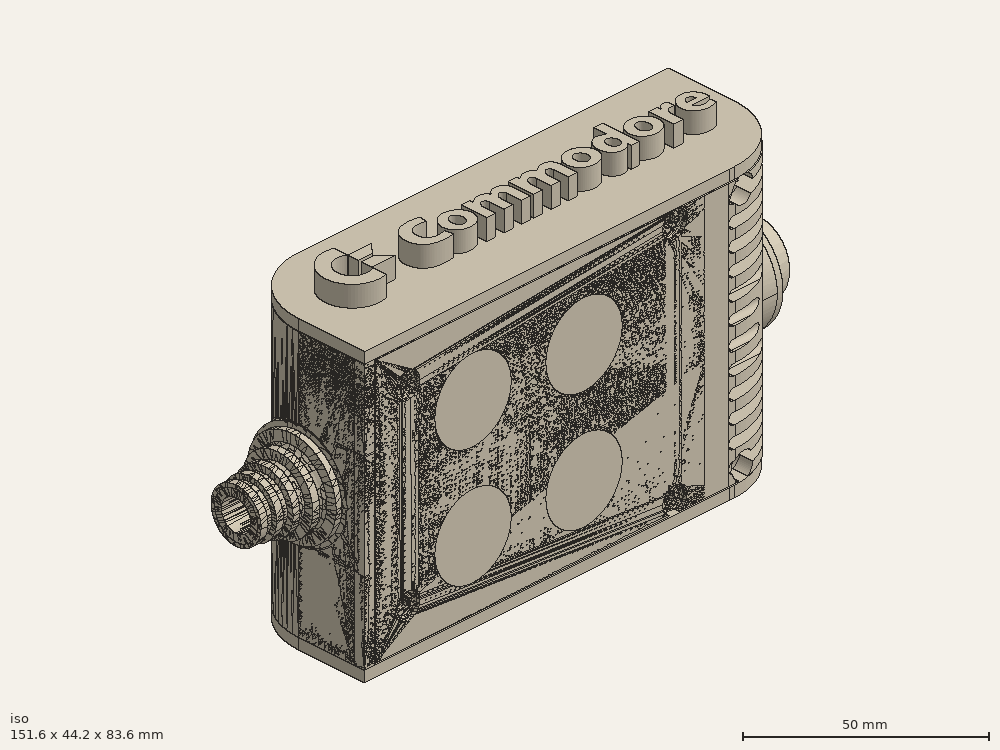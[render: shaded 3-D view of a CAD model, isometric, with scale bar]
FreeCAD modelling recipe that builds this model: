
FCSTD DOCUMENT  (FreeCAD 0.19R0.19.2)
Label: enclosure_209FCStd
License: All rights reserved
LicenseURL: http://en.wikipedia.org/wiki/All_rights_reserved
objects: Part::Revolution×152, Part::MultiFuse×146, Part::Feature×146, Sketcher::SketchObject×84, Part::Cut×71, Part::Cylinder×70, Part::Extrusion×69, Part::Fillet×58, Part::Box×36, App::MeasureDistance×4, Part::FeaturePython×2, Image::ImagePlane×1, PartDesign::Body×1, Part::Mirroring×1
note: 836 computed .brp shape members not serialized (recipe doc carries the construction recipe); baked Part::Feature solids carry a one-line shape summary decoded from their .brp

FEATURE [Sketcher::SketchObject] Sketch  label="topSketch"
  FullyConstrained = true
  sketch-geometry (20):
    g0: LineSegment StartX=5.21097e-06 StartY=3 StartZ=0 EndX=5.21097e-06 EndY=19 EndZ=0
    g1: ArcOfCircle CenterX=19 CenterY=19 CenterZ=0 NormalX=0 NormalY=0 NormalZ=1 AngleXU=0 Radius=19 StartAngle=1.5708 EndAngle=3.14159
    g2: ArcOfCircle CenterX=19 CenterY=19 CenterZ=0 NormalX=0 NormalY=0 NormalZ=1 AngleXU=0 Radius=16 StartAngle=1.5708 EndAngle=3.14159
    g3: LineSegment StartX=114 StartY=35 StartZ=0 EndX=19 EndY=35 EndZ=0
    g4: LineSegment StartX=5.21097e-06 StartY=3 StartZ=0 EndX=5.21097e-06 EndY=0 EndZ=0
    g5: LineSegment StartX=3 StartY=0 StartZ=0 EndX=5.21097e-06 EndY=0 EndZ=0
    g6: LineSegment StartX=3 StartY=19 StartZ=0 EndX=3 EndY=0 EndZ=0
    g7: LineSegment StartX=19 StartY=38 StartZ=0 EndX=124 EndY=38 EndZ=0
    g8: Circle CenterX=119 CenterY=35 CenterZ=0 NormalX=0 NormalY=0 NormalZ=1 AngleXU=0 Radius=1
    g9: Circle CenterX=121 CenterY=35 CenterZ=0 NormalX=0 NormalY=0 NormalZ=1 AngleXU=0 Radius=1
    g10: Circle CenterX=121 CenterY=33 CenterZ=0 NormalX=0 NormalY=0 NormalZ=1 AngleXU=0 Radius=1
    g11: BSplineCurve PolesCount=3 KnotsCount=2 Degree=2 IsPeriodic=0
    g12: GeomPoint X=119 Y=35 Z=0
    g13: GeomPoint X=121 Y=33 Z=0
    g14: LineSegment StartX=119 StartY=35 StartZ=0 EndX=114 EndY=35 EndZ=0
    g15: ArcOfCircle CenterX=105 CenterY=19 CenterZ=0 NormalX=0 NormalY=0 NormalZ=1 AngleXU=0 Radius=19 StartAngle=5.7297 EndAngle=6.28319
    g16: ArcOfCircle CenterX=105 CenterY=19 CenterZ=0 NormalX=0 NormalY=0 NormalZ=1 AngleXU=0 Radius=16 StartAngle=5.60905 EndAngle=6.28319
    g17: LineSegment StartX=121 StartY=33 StartZ=0 EndX=121 EndY=19 EndZ=0
    g18: LineSegment StartX=124 StartY=38 StartZ=0 EndX=124 EndY=19 EndZ=0
    g19: LineSegment StartX=117.5 StartY=9.01251 StartZ=0 EndX=121.163 EndY=9.0125 EndZ=0
  constraints (46):
    c: Vertical(g0)
    c: Block(g0)
    c: Coincident(g1,g0)
    c: Block(g1)
    c: Coincident(g2,g1)
    c: Block(g2)
    c: Coincident(g3,g2)
    c: Horizontal(g3)
    c: Tangent(g3,g2)
    c: Coincident(g4,g0)
    c: Distance(g4) = 3
    c: Vertical(g4)
    c: Coincident(g5,g4)
    c: Horizontal(g5)
    c: Coincident(g6,g2)
    c: Coincident(g6,g5)
    c: Vertical(g6)
    c: Horizontal(g7)
    c: Distance(g7) = 105
    c: Coincident(g7,g1)
    c: Block(g3)
    c: Weight(g8) = 1
    c: Equal(g8,g9)
    c: Equal(g8,g10)
    c: InternalAlignment(g8,g11)
    c: InternalAlignment(g9,g11)
    c: InternalAlignment(g10,g11)
    c: InternalAlignment(g12,g11)
    c: InternalAlignment(g13,g11)
    c: Block(g11)
    c: Coincident(g14,g11)
    c: Coincident(g14,g3)
    c: Horizontal(g14)
    c: Block(g15)
    c: Coincident(g16,g15)
    c: Block(g16)
    c: Coincident(g17,g11)
    c: Coincident(g17,g16)
    c: Vertical(g17)
    c: Distance(g17) = 14
    c: Coincident(g18,g7)
    c: Coincident(g18,g15)
    c: Vertical(g18)
    c: Distance(g18) = 19
    c: Coincident(g19,g16)
    c: Coincident(g19,g15)
FEATURE [Sketcher::SketchObject] Sketch001  label="bottomSketch"
  FullyConstrained = true
  sketch-geometry (32):
    g0: LineSegment StartX=3.3 StartY=-6.03275e-07 StartZ=0 EndX=98 EndY=-6.03275e-07 EndZ=0
    g1: ArcOfCircle CenterX=98 CenterY=19 CenterZ=0 NormalX=0 NormalY=0 NormalZ=1 AngleXU=0 Radius=19 StartAngle=4.71239 EndAngle=5.71103
    g2: LineSegment StartX=6.3 StartY=8 StartZ=0 EndX=3.3 EndY=8 EndZ=0
    g3: LineSegment StartX=3.3 StartY=8 StartZ=0 EndX=3.3 EndY=-6.03275e-07 EndZ=0
    g4: ArcOfCircle CenterX=8.3 CenterY=5 CenterZ=0 NormalX=0 NormalY=0 NormalZ=1 AngleXU=0 Radius=2 StartAngle=3.14159 EndAngle=4.71239
    g5: LineSegment StartX=6.3 StartY=8 StartZ=0 EndX=6.3 EndY=5 EndZ=0
    g6: ArcOfCircle CenterX=98 CenterY=19 CenterZ=0 NormalX=0 NormalY=0 NormalZ=1 AngleXU=0 Radius=12.7 StartAngle=4.71239 EndAngle=6.28319
    g7: LineSegment StartX=94.7 StartY=3 StartZ=0 EndX=8.3 EndY=3 EndZ=0
    g8-g12: Circle x5 (B-spline internal-alignment scaffolding for g13; pole/knot coordinates omitted)
    g13: BSplineCurve PolesCount=5 KnotsCount=3 Degree=3 IsPeriodic=0
    g14: GeomPoint X=98 Y=6.3 Z=0
    g15: GeomPoint X=96.3938 Y=4.71946 Z=0
    g16: GeomPoint X=94.7 Y=3 Z=0
    g17-g23: Circle x7 (B-spline internal-alignment scaffolding for g24; pole/knot coordinates omitted)
    g24: BSplineCurve PolesCount=7 KnotsCount=5 Degree=3 IsPeriodic=0
    g25-g29: GeomPoint x5 (B-spline internal-alignment scaffolding for g24; pole/knot coordinates omitted)
    g30: ArcOfCircle CenterX=98 CenterY=19 CenterZ=0 NormalX=0 NormalY=0 NormalZ=1 AngleXU=0 Radius=15.7 StartAngle=5.81226 EndAngle=6.28319
    g31: LineSegment StartX=110.7 StartY=19 StartZ=0 EndX=113.7 EndY=19 EndZ=0
  constraints (41):
    c: Horizontal(g0)
    c: Coincident(g1,g0)
    c: Block(g1)
    c: Horizontal(g2)
    c: Distance(g2) = 3
    c: Coincident(g3,g2)
    c: Vertical(g3)
    c: Coincident(g3,g0)
    c: Block(g4)
    c: Block(g2)
    c: Coincident(g5,g2)
    c: Coincident(g5,g4)
    c: Vertical(g5)
    c: Coincident(g6,g1)
    c: Block(g6)
    c: Coincident(g7,g4)
    c: Horizontal(g7)
    c: Block(g0)
    c: Block(g7)
    c: Block(g3)
    c: Coincident(g13,g6)
    c: Weight(g8) = 1
    c: Equal(g8, g9-g12) x4
    c: Coincident(g13,g7)
    c: InternalAlignment(g8-g12 -> g13) x5
    c: InternalAlignment(g14,g13)
    c: InternalAlignment(g15,g13)
    c: InternalAlignment(g16,g13)
    c: Block(g13)
    c: Weight(g17) = 1
    c: Equal(g17, g18-g23) x6
    c: Coincident(g24,g1)
    c: InternalAlignment(g17-g23 -> g24) x7
    c: InternalAlignment(g25-g29 -> g24) x5
    c: Block(g24)
    c: Coincident(g30,g24)
    c: Coincident(g31,g6)
    c: Coincident(g31,g30)
    c: Horizontal(g31)
    c: Block(g31)
    c: Block(g30)
FEATURE [Part::Extrusion] Extrude  label="top"
  Base = -> Sketch
  Dir = (0,0,1)
  DirMode = 2
  FaceMakerClass = Part::FaceMakerBullseye
  LengthFwd = 72
  LengthRev = 0
  Solid = true
  Symmetric = false
FEATURE [Part::Extrusion] Extrude001  label="bottom"
  Base = -> Sketch001
  Dir = (0,0,1)
  DirMode = 2
  FaceMakerClass = Part::FaceMakerBullseye
  LengthFwd = 71.4
  LengthRev = 0
  Placement = pos=(0,0,0.3) rot=(0,0,1;0rad)
  Solid = true
  Symmetric = false
FEATURE [Sketcher::SketchObject] Sketch002  label="topSketch001"
  FullyConstrained = true
  sketch-geometry (8):
    g0: ArcOfCircle CenterX=19 CenterY=19.0975 CenterZ=0 NormalX=0 NormalY=0 NormalZ=1 AngleXU=0 Radius=18.9025 StartAngle=1.5708 EndAngle=3.14674
    g1: LineSegment StartX=0.0977805 StartY=19.0003 StartZ=0 EndX=0.0977805 EndY=0.000251602 EndZ=0
    g2: LineSegment StartX=19 StartY=38 StartZ=0 EndX=124 EndY=38 EndZ=0
    g3: LineSegment StartX=0.0977805 StartY=0.000251602 StartZ=0 EndX=105.098 EndY=0.000251602 EndZ=0
    g4: LineSegment StartX=124 StartY=38 StartZ=0 EndX=125.616 EndY=38 EndZ=0
    g5: LineSegment StartX=105.098 StartY=0.000251602 StartZ=0 EndX=106.713 EndY=0.000251602 EndZ=0
    g6: ArcOfCircle CenterX=106.616 CenterY=19 CenterZ=0 NormalX=0 NormalY=0 NormalZ=1 AngleXU=0 Radius=19 StartAngle=4.71754 EndAngle=6.28319
    g7: LineSegment StartX=125.616 StartY=38 StartZ=0 EndX=125.616 EndY=19 EndZ=0
  constraints (21):
    c: Block(g0)
    c: Coincident(g1,g0)
    c: Vertical(g1)
    c: Horizontal(g2)
    c: Distance(g2) = 105
    c: Coincident(g2,g0)
    c: Distance(g1) = 19
    c: Coincident(g3,g1)
    c: Horizontal(g3)
    c: Distance(g3) = 105
    c: Coincident(g4,g2)
    c: Horizontal(g4)
    c: Distance(g4) = 1.61553
    c: Horizontal(g5)
    c: Equal(g4,g5) = 1.61553
    c: Coincident(g5,g3)
    c: Block(g6)
    c: Coincident(g6,g5)
    c: Coincident(g7,g4)
    c: Coincident(g7,g6)
    c: Vertical(g7)
FEATURE [Part::Extrusion] Extrude002  label="sideA"
  Base = -> Sketch002
  Dir = (0,0,1)
  DirMode = 2
  FaceMakerClass = Part::FaceMakerBullseye
  LengthFwd = 3
  LengthRev = 0
  Placement = pos=(0,0,-3) rot=(0,0,1;0rad)
  Solid = true
  Symmetric = false
FEATURE [Sketcher::SketchObject] Sketch003  label="topSketch002"
  FullyConstrained = true
  sketch-geometry (6):
    g0: LineSegment StartX=19 StartY=38 StartZ=0 EndX=117 EndY=38 EndZ=0
    g1: ArcOfCircle CenterX=19 CenterY=19 CenterZ=0 NormalX=0 NormalY=0 NormalZ=1 AngleXU=0 Radius=19 StartAngle=1.5708 EndAngle=3.14159
    g2: LineSegment StartX=117 StartY=38 StartZ=0 EndX=117 EndY=19 EndZ=0
    g3: LineSegment StartX=98 StartY=1.0161e-12 StartZ=0 EndX=5.22862e-06 EndY=1.0161e-12 EndZ=0
    g4: LineSegment StartX=5.22862e-06 StartY=19 StartZ=0 EndX=5.22862e-06 EndY=1.0161e-12 EndZ=0
    g5: ArcOfCircle CenterX=98 CenterY=19 CenterZ=0 NormalX=0 NormalY=0 NormalZ=1 AngleXU=0 Radius=19 StartAngle=4.71239 EndAngle=6.28319
  constraints (16):
    c: Horizontal(g0)
    c: Distance(g0) = 98
    c: Coincident(g1,g0)
    c: Block(g1)
    c: Coincident(g2,g0)
    c: Vertical(g2)
    c: Distance(g2) = 19
    c: Horizontal(g3)
    c: Coincident(g4,g1)
    c: Vertical(g4)
    c: Coincident(g3,g4)
    c: Block(g3)
    c: Coincident(g5,g2)
    c: Coincident(g5,g3)
    c: Block(g0)
    c: Block(g5)
FEATURE [Sketcher::SketchObject] Sketch004
  FullyConstrained = true
  MapMode = 3
  Placement = pos=(0,0,0) rot=(1,0,0;1.5708rad)
  Support = -> [Extrude]
  sketch-geometry (8):
    g0: Circle CenterX=80.351 CenterY=-67.6202 CenterZ=0 NormalX=0 NormalY=0 NormalZ=1 AngleXU=0 Radius=2
    g1: Circle CenterX=80.351 CenterY=-67.6202 CenterZ=0 NormalX=0 NormalY=0 NormalZ=1 AngleXU=0 Radius=3
    g2: Circle CenterX=80.351 CenterY=-4.92017 CenterZ=0 NormalX=0 NormalY=0 NormalZ=1 AngleXU=0 Radius=2
    g3: Circle CenterX=80.351 CenterY=-4.92017 CenterZ=0 NormalX=0 NormalY=0 NormalZ=1 AngleXU=0 Radius=3
    g4: Circle CenterX=23.851 CenterY=-4.92017 CenterZ=0 NormalX=0 NormalY=0 NormalZ=1 AngleXU=0 Radius=2
    g5: Circle CenterX=23.851 CenterY=-4.92017 CenterZ=0 NormalX=0 NormalY=0 NormalZ=1 AngleXU=0 Radius=3
    g6: Circle CenterX=23.851 CenterY=-67.6202 CenterZ=0 NormalX=0 NormalY=0 NormalZ=1 AngleXU=0 Radius=2
    g7: Circle CenterX=23.851 CenterY=-67.6202 CenterZ=0 NormalX=0 NormalY=0 NormalZ=1 AngleXU=0 Radius=3
  constraints (8):
    c: Block(g3)
    c: Block(g2)
    c: Block(g1)
    c: Block(g0)
    c: Block(g6)
    c: Block(g7)
    c: Block(g4)
    c: Block(g5)
FEATURE [Part::Extrusion] Extrude004
  Base = -> Sketch004
  Dir = (0,-1,2e-16)
  DirMode = 2
  FaceMakerClass = Part::FaceMakerBullseye
  LengthFwd = 6
  LengthRev = 0
  Placement = pos=(0,9,0) rot=(0,0,1;0rad)
  Solid = true
  Symmetric = false
FEATURE [Sketcher::SketchObject] Sketch005
  FullyConstrained = true
  MapMode = 3
  Placement = pos=(0,0,0) rot=(1,0,0;1.5708rad)
  Support = -> [Extrude]
  sketch-geometry (8):
    g0: Circle CenterX=80.351 CenterY=-67.6202 CenterZ=0 NormalX=0 NormalY=0 NormalZ=1 AngleXU=0 Radius=3
    g1: Circle CenterX=80.351 CenterY=-4.92017 CenterZ=0 NormalX=0 NormalY=0 NormalZ=1 AngleXU=0 Radius=3
    g2: Circle CenterX=23.851 CenterY=-4.92017 CenterZ=0 NormalX=0 NormalY=0 NormalZ=1 AngleXU=0 Radius=3
    g3: Circle CenterX=23.851 CenterY=-67.6202 CenterZ=0 NormalX=0 NormalY=0 NormalZ=1 AngleXU=0 Radius=3
    g4: Circle CenterX=23.851 CenterY=-67.6202 CenterZ=0 NormalX=0 NormalY=0 NormalZ=1 AngleXU=0 Radius=5
    g5: Circle CenterX=80.351 CenterY=-67.6202 CenterZ=0 NormalX=0 NormalY=0 NormalZ=1 AngleXU=0 Radius=5
    g6: Circle CenterX=23.851 CenterY=-4.92017 CenterZ=0 NormalX=0 NormalY=0 NormalZ=1 AngleXU=0 Radius=5
    g7: Circle CenterX=80.351 CenterY=-4.92017 CenterZ=0 NormalX=0 NormalY=0 NormalZ=1 AngleXU=0 Radius=5
  constraints (8):
    c: Block(g1)
    c: Block(g0)
    c: Block(g3)
    c: Block(g2)
    c: Block(g5)
    c: Block(g4)
    c: Block(g6)
    c: Block(g7)
FEATURE [Part::Extrusion] Extrude005
  Base = -> Sketch005
  Dir = (0,-1,2e-16)
  DirMode = 2
  FaceMakerClass = Part::FaceMakerBullseye
  LengthFwd = 2
  LengthRev = 0
  Solid = true
  Symmetric = false
FEATURE [Sketcher::SketchObject] Sketch006
  FullyConstrained = true
  MapMode = 3
  Placement = pos=(0,0,0) rot=(1,0,0;1.5708rad)
  sketch-geometry (8):
    g0: Circle CenterX=80.351 CenterY=-67.6202 CenterZ=0 NormalX=0 NormalY=0 NormalZ=1 AngleXU=0 Radius=3
    g1: Circle CenterX=80.351 CenterY=-4.92017 CenterZ=0 NormalX=0 NormalY=0 NormalZ=1 AngleXU=0 Radius=3
    g2: Circle CenterX=23.851 CenterY=-4.92017 CenterZ=0 NormalX=0 NormalY=0 NormalZ=1 AngleXU=0 Radius=3
    g3: Circle CenterX=23.851 CenterY=-67.6202 CenterZ=0 NormalX=0 NormalY=0 NormalZ=1 AngleXU=0 Radius=3
    g4: Circle CenterX=23.851 CenterY=-67.6202 CenterZ=0 NormalX=0 NormalY=0 NormalZ=1 AngleXU=0 Radius=5
    g5: Circle CenterX=80.351 CenterY=-67.6202 CenterZ=0 NormalX=0 NormalY=0 NormalZ=1 AngleXU=0 Radius=5
    g6: Circle CenterX=23.851 CenterY=-4.92017 CenterZ=0 NormalX=0 NormalY=0 NormalZ=1 AngleXU=0 Radius=5
    g7: Circle CenterX=80.351 CenterY=-4.92017 CenterZ=0 NormalX=0 NormalY=0 NormalZ=1 AngleXU=0 Radius=5
  constraints (8):
    c: Block(g1)
    c: Block(g0)
    c: Block(g3)
    c: Block(g2)
    c: Block(g5)
    c: Block(g4)
    c: Block(g6)
    c: Block(g7)
FEATURE [Part::Extrusion] Extrude007
  Base = -> Sketch006
  Dir = (0,-1,2e-16)
  DirMode = 2
  FaceMakerClass = Part::FaceMakerBullseye
  LengthFwd = 2
  LengthRev = 0
  Solid = true
  Symmetric = false
FEATURE [Part::Fillet] Fillet
  Base = -> Extrude007
  Edges = 4 edges r=1.99: [Edge6,Edge12,Edge18,Edge24]
FEATURE [Part::Cut] Cut
  Base = -> Extrude005
  Placement = pos=(0,5,0) rot=(0,0,1;0rad)
  Tool = -> Fillet
FEATURE [Part::MultiFuse] Fusion  label="pCBScrews"
  Placement = pos=(-2.5,0,72.3) rot=(0,0,1;0rad)
  Shapes = -> [Extrude004,Cut]
FEATURE [App::MeasureDistance] Distance  label="Distance: 0.69 mm"
  Distance = 0.685967
  P1 = (24.0138,2.9647,0.3)
  P2 = (23.8901,3,-0.373787)
FEATURE [App::MeasureDistance] Distance001  label="Distance: 0.53 mm"
  Distance = 0.533607
  P1 = (80.2939,3,72.2334)
  P2 = (80.281,2.99661,71.7)
FEATURE [Part::Fillet] Fillet001
  Base = -> Extrude001
  Edges = 1 edges r=2.4: [Edge17]
FEATURE [Part::Fillet] Fillet002  label="bottom001"
  Base = -> Fillet001
  Edges = 1 edges r=2.4: [Edge36]
FEATURE [Part::Fillet] Fillet003  label="top001"
  Base = -> Extrude
  Edges = 1 edges r=2: [Edge1]
FEATURE [Sketcher::SketchObject] Sketch007
  FullyConstrained = true
  sketch-geometry (16):
    g0: LineSegment StartX=4 StartY=0 StartZ=0 EndX=4 EndY=2.4 EndZ=0
    g1: LineSegment StartX=4 StartY=2.4 StartZ=0 EndX=7 EndY=2.4 EndZ=0
    g2: LineSegment StartX=4 StartY=0 StartZ=0 EndX=5.7 EndY=0 EndZ=0
    g3: LineSegment StartX=5.7 StartY=0 StartZ=0 EndX=5.7 EndY=-5.6 EndZ=0
    g4-g8: Circle x5 (B-spline internal-alignment scaffolding for g9; pole/knot coordinates omitted)
    g9: BSplineCurve PolesCount=5 KnotsCount=3 Degree=3 IsPeriodic=0
    g10: GeomPoint X=7 Y=2.4 Z=0
    g11: GeomPoint X=10.4582 Y=-1.55472 Z=0
    g12: GeomPoint X=14 Y=-5.6 Z=0
    g13: LineSegment StartX=14 StartY=-5.6 StartZ=0 EndX=14 EndY=-14.1 EndZ=0
    g14: LineSegment StartX=14 StartY=-14.1 StartZ=0 EndX=6.5 EndY=-14.1 EndZ=0
    g15: LineSegment StartX=5.7 StartY=-5.6 StartZ=0 EndX=6.5 EndY=-14.1 EndZ=0
  constraints (28):
    c: Distance(g0) = 2.4
    c: Vertical(g0)
    c: Block(g0)
    c: Coincident(g1,g0)
    c: Horizontal(g1)
    c: Distance(g1) = 3
    c: Coincident(g2,g0)
    c: Horizontal(g2)
    c: Distance(g2) = 1.7
    c: Coincident(g3,g2)
    c: Vertical(g3)
    c: Distance(g3) = 5.6
    c: Coincident(g9,g1)
    c: Weight(g4) = 1
    c: Equal(g4, g5-g8) x4
    c: InternalAlignment(g4-g8 -> g9) x5
    c: InternalAlignment(g10,g9)
    c: InternalAlignment(g11,g9)
    c: InternalAlignment(g12,g9)
    c: Block(g9)
    c: Coincident(g13,g9)
    c: Vertical(g13)
    c: Distance(g13) = 8.5
    c: Coincident(g14,g13)
    c: Horizontal(g14)
    c: Distance(g14) = 7.5
    c: Coincident(g15,g3)
    c: Coincident(g15,g14)
FEATURE [Part::Feature] Face
  shape: bbox 10 x 16.5 x 2e-07 mm, 1 faces, 0 solids (baked)
FEATURE [Part::Revolution] Revolve  label="plugHousing"
  Angle = 360
  Axis = (0,1,0)
  Base = (0,0,0)
  FaceMakerClass = Part::FaceMakerBullseye
  Placement = pos=(0,0,36.15) rot=(0,0,1;0rad)
  Solid = false
  Source = -> Face
  Symmetric = false
FEATURE [Part::Feature] Face001
  shape: bbox 10 x 16.5 x 2e-07 mm, 1 faces, 0 solids (baked)
FEATURE [Part::Revolution] Revolve001  label="plugHousing001"
  Angle = 360
  Axis = (0,1,0)
  Base = (0,0,0)
  FaceMakerClass = Part::FaceMakerBullseye
  Placement = pos=(0,0,36.15) rot=(0,0,1;0rad)
  Solid = false
  Source = -> Face001
  Symmetric = false
FEATURE [Part::MultiFuse] Fusion001  label="plugHousing002"
  Placement = pos=(0,0,0) rot=(0,0,1;1.5708rad)
  Shapes = -> [Revolve001,Revolve]
FEATURE [Part::Feature] Face002
  shape: bbox 10 x 16.5 x 2e-07 mm, 1 faces, 0 solids (baked)
FEATURE [Part::Revolution] Revolve003  label="plugHousing005"
  Angle = 360
  Axis = (0,1,0)
  Base = (0,0,0)
  FaceMakerClass = Part::FaceMakerBullseye
  Placement = pos=(0,0,36.15) rot=(0,0,1;0rad)
  Solid = false
  Source = -> Face002
  Symmetric = false
FEATURE [Part::Feature] Face003
  shape: bbox 10 x 16.5 x 2e-07 mm, 1 faces, 0 solids (baked)
FEATURE [Part::Revolution] Revolve002  label="plugHousing003"
  Angle = 360
  Axis = (0,1,0)
  Base = (0,0,0)
  FaceMakerClass = Part::FaceMakerBullseye
  Placement = pos=(0,0,36.15) rot=(0,0,1;0rad)
  Solid = false
  Source = -> Face003
  Symmetric = false
FEATURE [Part::MultiFuse] Fusion002  label="plugHousing004"
  Placement = pos=(0,0,0) rot=(0,0,1;1.5708rad)
  Shapes = -> [Revolve002,Revolve003]
FEATURE [Part::MultiFuse] Fusion003  label="plugHousing006"
  Placement = pos=(0,19,0) rot=(0,0,1;3.14159rad)
  Shapes = -> [Fusion002,Fusion001]
FEATURE [Part::Feature] Face004
  shape: bbox 10 x 16.5 x 2e-07 mm, 1 faces, 0 solids (baked)
FEATURE [Part::Revolution] Revolve006  label="plugHousing010"
  Angle = 360
  Axis = (0,1,0)
  Base = (0,0,0)
  FaceMakerClass = Part::FaceMakerBullseye
  Placement = pos=(0,0,36.15) rot=(0,0,1;0rad)
  Solid = false
  Source = -> Face004
  Symmetric = false
FEATURE [Part::Feature] Face005
  shape: bbox 10 x 16.5 x 2e-07 mm, 1 faces, 0 solids (baked)
FEATURE [Part::Revolution] Revolve007  label="plugHousing011"
  Angle = 360
  Axis = (0,1,0)
  Base = (0,0,0)
  FaceMakerClass = Part::FaceMakerBullseye
  Placement = pos=(0,0,36.15) rot=(0,0,1;0rad)
  Solid = false
  Source = -> Face005
  Symmetric = false
FEATURE [Part::Feature] Face006
  shape: bbox 10 x 16.5 x 2e-07 mm, 1 faces, 0 solids (baked)
FEATURE [Part::Revolution] Revolve004  label="plugHousing007"
  Angle = 360
  Axis = (0,1,0)
  Base = (0,0,0)
  FaceMakerClass = Part::FaceMakerBullseye
  Placement = pos=(0,0,36.15) rot=(0,0,1;0rad)
  Solid = false
  Source = -> Face006
  Symmetric = false
FEATURE [Part::MultiFuse] Fusion004  label="plugHousing009"
  Placement = pos=(0,0,0) rot=(0,0,1;1.5708rad)
  Shapes = -> [Revolve004,Revolve007]
FEATURE [Part::Feature] Face007
  shape: bbox 10 x 16.5 x 2e-07 mm, 1 faces, 0 solids (baked)
FEATURE [Part::Revolution] Revolve005  label="plugHousing008"
  Angle = 360
  Axis = (0,1,0)
  Base = (0,0,0)
  FaceMakerClass = Part::FaceMakerBullseye
  Placement = pos=(0,0,36.15) rot=(0,0,1;0rad)
  Solid = false
  Source = -> Face007
  Symmetric = false
FEATURE [Part::MultiFuse] Fusion005  label="plugHousing012"
  Placement = pos=(0,0,0) rot=(0,0,1;1.5708rad)
  Shapes = -> [Revolve006,Revolve005]
FEATURE [Part::MultiFuse] Fusion006  label="plugHousing013"
  Placement = pos=(0,19,0) rot=(0,0,1;3.14159rad)
  Shapes = -> [Fusion005,Fusion004]
FEATURE [Part::MultiFuse] Fusion007  label="plugHousing014"
  Placement = pos=(122.621,0,-0.15) rot=(0,0,1;0rad)
  Shapes = -> [Fusion003,Fusion006]
FEATURE [Part::Cylinder] Cylinder002
  Angle = 360
  AttacherType = Attacher::AttachEngine3D
  Height = 20
  Placement = pos=(0,0,36.15) rot=(0,0,1;0rad)
  Radius = 4
FEATURE [Part::Cylinder] Cylinder003
  Angle = 360
  AttacherType = Attacher::AttachEngine3D
  Height = 10
  Placement = pos=(0,0,36.15) rot=(0,0,1;0rad)
  Radius = 4
FEATURE [Part::MultiFuse] Fusion009  label="removeToCreateHoleForPlugHousing"
  Placement = pos=(70,19,36.15) rot=(0,1,0;1.5708rad)
  Shapes = -> [Cylinder002,Cylinder003]
FEATURE [Part::Cylinder] Cylinder004
  Angle = 360
  AttacherType = Attacher::AttachEngine3D
  Height = 20
  Placement = pos=(0,0,36.15) rot=(0,0,1;0rad)
  Radius = 4
FEATURE [Part::Cylinder] Cylinder005
  Angle = 360
  AttacherType = Attacher::AttachEngine3D
  Height = 10
  Placement = pos=(0,0,36.15) rot=(0,0,1;0rad)
  Radius = 4
FEATURE [Part::MultiFuse] Fusion010  label="removeToCreateHoleForPlugHousing001"
  Placement = pos=(70,19,36.15) rot=(0,1,0;1.5708rad)
  Shapes = -> [Cylinder004,Cylinder005]
FEATURE [Part::Cut] Cut001
  Base = -> Fillet003
  Tool = -> Fusion010
FEATURE [Part::Cut] Cut002  label="Bottom"
  Base = -> Fillet002
  Tool = -> Fusion009
FEATURE [Part::Feature] Face008
  shape: bbox 10 x 16.5 x 2e-07 mm, 1 faces, 0 solids (baked)
FEATURE [Part::Revolution] Revolve011  label="plugHousing021"
  Angle = 360
  Axis = (0,1,0)
  Base = (0,0,0)
  FaceMakerClass = Part::FaceMakerBullseye
  Placement = pos=(0,0,36.15) rot=(0,0,1;0rad)
  Solid = false
  Source = -> Face008
  Symmetric = false
FEATURE [Part::Feature] Face009
  shape: bbox 10 x 16.5 x 2e-07 mm, 1 faces, 0 solids (baked)
FEATURE [Part::Revolution] Revolve012  label="plugHousing022"
  Angle = 360
  Axis = (0,1,0)
  Base = (0,0,0)
  FaceMakerClass = Part::FaceMakerBullseye
  Placement = pos=(0,0,36.15) rot=(0,0,1;0rad)
  Solid = false
  Source = -> Face009
  Symmetric = false
FEATURE [Part::Feature] Face010 .. Face013  x4 (patterned run collapsed; names and placements below)
  shape: bbox 10 x 16.5 x 2e-07 mm, 1 faces, 0 solids (baked)
FEATURE [Part::Revolution] Revolve015  label="plugHousing027"
  Angle = 360
  Axis = (0,1,0)
  Base = (0,0,0)
  FaceMakerClass = Part::FaceMakerBullseye
  Placement = pos=(0,0,36.15) rot=(0,0,1;0rad)
  Solid = false
  Source = -> Face013
  Symmetric = false
FEATURE [Part::Feature] Face014
  shape: bbox 10 x 16.5 x 2e-07 mm, 1 faces, 0 solids (baked)
FEATURE [Part::Feature] Face015
  shape: bbox 10 x 16.5 x 2e-07 mm, 1 faces, 0 solids (baked)
FEATURE [Part::Feature] Face016
  shape: bbox 10 x 16.5 x 2e-07 mm, 1 faces, 0 solids (baked)
FEATURE [Part::Revolution] Revolve019  label="plugHousing033"
  Angle = 360
  Axis = (0,1,0)
  Base = (0,0,0)
  FaceMakerClass = Part::FaceMakerBullseye
  Placement = pos=(0,0,36.15) rot=(0,0,1;0rad)
  Solid = false
  Source = -> Face016
  Symmetric = false
FEATURE [Part::Feature] Face017
  shape: bbox 10 x 16.5 x 2e-07 mm, 1 faces, 0 solids (baked)
FEATURE [Part::Revolution] Revolve020  label="plugHousing034"
  Angle = 360
  Axis = (0,1,0)
  Base = (0,0,0)
  FaceMakerClass = Part::FaceMakerBullseye
  Placement = pos=(0,0,36.15) rot=(0,0,1;0rad)
  Solid = false
  Source = -> Face017
  Symmetric = false
FEATURE [Part::Feature] Face018
  shape: bbox 10 x 16.5 x 2e-07 mm, 1 faces, 0 solids (baked)
FEATURE [Part::Revolution] Revolve016  label="plugHousing030"
  Angle = 360
  Axis = (0,1,0)
  Base = (0,0,0)
  FaceMakerClass = Part::FaceMakerBullseye
  Placement = pos=(0,0,36.15) rot=(0,0,1;0rad)
  Solid = false
  Source = -> Face018
  Symmetric = false
FEATURE [Part::MultiFuse] Fusion020  label="plugHousing038"
  Placement = pos=(0,0,0) rot=(0,0,1;1.5708rad)
  Shapes = -> [Revolve016,Revolve020]
FEATURE [Part::Feature] Face019
  shape: bbox 10 x 16.5 x 2e-07 mm, 1 faces, 0 solids (baked)
FEATURE [Part::Feature] Face020
  shape: bbox 10 x 16.5 x 2e-07 mm, 1 faces, 0 solids (baked)
FEATURE [Part::Revolution] Revolve017  label="plugHousing031"
  Angle = 360
  Axis = (0,1,0)
  Base = (0,0,0)
  FaceMakerClass = Part::FaceMakerBullseye
  Placement = pos=(0,0,36.15) rot=(0,0,1;0rad)
  Solid = false
  Source = -> Face020
  Symmetric = false
FEATURE [Part::MultiFuse] Fusion021  label="plugHousing039"
  Placement = pos=(0,0,0) rot=(0,0,1;1.5708rad)
  Shapes = -> [Revolve019,Revolve017]
FEATURE [Part::MultiFuse] Fusion023  label="plugHousing041"
  Placement = pos=(0,19,0) rot=(0,0,1;3.14159rad)
  Shapes = -> [Fusion021,Fusion020]
FEATURE [Part::Revolution] Revolve022  label="plugHousing043"
  Angle = 360
  Axis = (0,1,0)
  Base = (0,0,0)
  FaceMakerClass = Part::FaceMakerBullseye
  Placement = pos=(0,0,36.15) rot=(0,0,1;0rad)
  Solid = false
  Source = -> Face019
  Symmetric = false
FEATURE [Part::Feature] Face021
  shape: bbox 10 x 16.5 x 2e-07 mm, 1 faces, 0 solids (baked)
FEATURE [Part::Revolution] Revolve023  label="plugHousing044"
  Angle = 360
  Axis = (0,1,0)
  Base = (0,0,0)
  FaceMakerClass = Part::FaceMakerBullseye
  Placement = pos=(0,0,36.15) rot=(0,0,1;0rad)
  Solid = false
  Source = -> Face021
  Symmetric = false
FEATURE [Part::Feature] Face022
  shape: bbox 10 x 16.5 x 2e-07 mm, 1 faces, 0 solids (baked)
FEATURE [Part::Revolution] Revolve018  label="plugHousing032"
  Angle = 360
  Axis = (0,1,0)
  Base = (0,0,0)
  FaceMakerClass = Part::FaceMakerBullseye
  Placement = pos=(0,0,36.15) rot=(0,0,1;0rad)
  Solid = false
  Source = -> Face022
  Symmetric = false
FEATURE [Part::MultiFuse] Fusion022  label="plugHousing040"
  Placement = pos=(0,0,0) rot=(0,0,1;1.5708rad)
  Shapes = -> [Revolve018,Revolve023]
FEATURE [Part::Feature] Face023
  shape: bbox 10 x 16.5 x 2e-07 mm, 1 faces, 0 solids (baked)
FEATURE [Part::Revolution] Revolve021  label="plugHousing035"
  Angle = 360
  Axis = (0,1,0)
  Base = (0,0,0)
  FaceMakerClass = Part::FaceMakerBullseye
  Placement = pos=(0,0,36.15) rot=(0,0,1;0rad)
  Solid = false
  Source = -> Face023
  Symmetric = false
FEATURE [Part::MultiFuse] Fusion018  label="plugHousing036"
  Placement = pos=(0,0,0) rot=(0,0,1;1.5708rad)
  Shapes = -> [Revolve022,Revolve021]
FEATURE [Part::MultiFuse] Fusion019  label="plugHousing037"
  Placement = pos=(0,19,0) rot=(0,0,1;3.14159rad)
  Shapes = -> [Fusion018,Fusion022]
FEATURE [Part::MultiFuse] Fusion024  label="plugHousing042"
  Placement = pos=(122.621,0,-0.15) rot=(0,0,1;0rad)
  Shapes = -> [Fusion023,Fusion019]
FEATURE [Part::Cylinder] Cylinder006
  Angle = 360
  AttacherType = Attacher::AttachEngine3D
  Height = 20
  Placement = pos=(0,0,36.15) rot=(0,0,1;0rad)
  Radius = 14.3
FEATURE [Part::Cylinder] Cylinder007
  Angle = 360
  AttacherType = Attacher::AttachEngine3D
  Height = 10
  Placement = pos=(0,0,36.15) rot=(0,0,1;0rad)
  Radius = 4
FEATURE [Part::MultiFuse] Fusion026  label="removeToCreteHoleForPlugHousing"
  Placement = pos=(70,19,36) rot=(0,1,0;1.5708rad)
  Shapes = -> [Cylinder006,Cylinder007]
FEATURE [Part::Box] Box001  label="Cube001"
  AttacherType = Attacher::AttachEngine3D
  Height = 28
  Length = 3
  Placement = pos=(110.7,19,22) rot=(0,0,1;0rad)
  Width = 15.7
FEATURE [Part::Cut] Cut003  label="top002"
  Base = -> Cut001
  Tool = -> Fusion007
FEATURE [Part::Revolution] Revolve008  label="plugHousing015"
  Angle = 360
  Axis = (0,1,0)
  Base = (0,0,0)
  FaceMakerClass = Part::FaceMakerBullseye
  Placement = pos=(0,0,36.15) rot=(0,0,1;0rad)
  Solid = false
  Source = -> Face010
  Symmetric = false
FEATURE [Part::MultiFuse] Fusion013  label="plugHousing020"
  Placement = pos=(0,0,0) rot=(0,0,1;1.5708rad)
  Shapes = -> [Revolve008,Revolve012]
FEATURE [Part::Cut] Cut004  label="top003"
  Base = -> Cut003
  Placement = pos=(1,0,0) rot=(0,0,1;0rad)
  Tool = -> Fusion026
FEATURE [Part::Cylinder] Cylinder008
  Angle = 360
  AttacherType = Attacher::AttachEngine3D
  Height = 20
  Placement = pos=(0,0,36.15) rot=(0,0,1;0rad)
  Radius = 10.3
FEATURE [Part::Cylinder] Cylinder009
  Angle = 360
  AttacherType = Attacher::AttachEngine3D
  Height = 10
  Placement = pos=(0,0,36.15) rot=(0,0,1;0rad)
  Radius = 4
FEATURE [Part::MultiFuse] Fusion027  label="removeToCreteHoleForPlugHousing001"
  Placement = pos=(70,19,36) rot=(0,1,0;1.5708rad)
  Shapes = -> [Cylinder008,Cylinder009]
FEATURE [Part::Cut] Cut005  label="plugHousingTab"
  Base = -> Box001
  Tool = -> Fusion027
FEATURE [Part::MultiFuse] Fusion028  label="plugHousing045"
  Shapes = -> [Fusion024,Cut005]
FEATURE [Part::Box] Box002  label="Cube002"
  AttacherType = Attacher::AttachEngine3D
  Height = 28.8
  Length = 3
  Placement = pos=(107.3,28,21.6) rot=(0,0,1;0rad)
  Width = 7
FEATURE [Part::Box] Box003  label="Cube003"
  AttacherType = Attacher::AttachEngine3D
  Height = 3
  Length = 6.4
  Placement = pos=(107.3,28,18.6) rot=(0,0,1;0rad)
  Width = 7
FEATURE [Part::Box] Box004  label="Cube004"
  AttacherType = Attacher::AttachEngine3D
  Height = 3
  Length = 6.4
  Placement = pos=(107.3,28,50.4) rot=(0,0,1;0rad)
  Width = 7
FEATURE [Part::MultiFuse] Fusion029  label="plugHousingBracketHolder"
  Shapes = -> [Box004,Box002,Box003]
FEATURE [Part::Cylinder] Cylinder010
  Angle = 360
  AttacherType = Attacher::AttachEngine3D
  Height = 20
  Placement = pos=(0,0,36.15) rot=(0,0,1;0rad)
  Radius = 14.3
FEATURE [Part::Cylinder] Cylinder011
  Angle = 360
  AttacherType = Attacher::AttachEngine3D
  Height = 10
  Placement = pos=(0,0,36.15) rot=(0,0,1;0rad)
  Radius = 4
FEATURE [Part::MultiFuse] Fusion030  label="removeToCreteHoleForPlugHousing002"
  Placement = pos=(70,19,36) rot=(0,1,0;1.5708rad)
  Shapes = -> [Cylinder010,Cylinder011]
FEATURE [Part::Cut] Cut006  label="plugHousingBracketHolder001"
  Base = -> Fusion029
  Tool = -> Fusion030
FEATURE [Part::Cylinder] Cylinder012
  Angle = 360
  AttacherType = Attacher::AttachEngine3D
  Height = 20
  Placement = pos=(0,0,36.15) rot=(0,0,1;0rad)
  Radius = 7
FEATURE [Part::Cylinder] Cylinder013
  Angle = 360
  AttacherType = Attacher::AttachEngine3D
  Height = 10
  Placement = pos=(0,0,36.15) rot=(0,0,1;0rad)
  Radius = 4
FEATURE [Part::MultiFuse] Fusion032  label="removeToCreteHoleForPlugHousing003"
  Placement = pos=(70,19,36) rot=(0,1,0;1.5708rad)
  Shapes = -> [Cylinder012,Cylinder013]
FEATURE [Part::Cut] Cut007  label="bottom002"
  Base = -> Cut002
  Tool = -> Fusion032
FEATURE [Sketcher::SketchObject] Sketch008
  FullyConstrained = true
  sketch-geometry (54):
    g0: LineSegment StartX=-4.2 StartY=0 StartZ=0 EndX=-6.2 EndY=0 EndZ=0
    g1: LineSegment StartX=-14 StartY=-18 StartZ=0 EndX=-14 EndY=-26.5 EndZ=0
    g2: LineSegment StartX=-4.2 StartY=0 StartZ=0 EndX=-4.2 EndY=-13.4877 EndZ=0
    g3: Circle CenterX=-4.2 CenterY=-13.4877 CenterZ=0 NormalX=0 NormalY=0 NormalZ=1 AngleXU=0 Radius=1
    g4: Circle CenterX=-4.2 CenterY=-26.5 CenterZ=0 NormalX=0 NormalY=0 NormalZ=1 AngleXU=0 Radius=1
    g5: Circle CenterX=-8.2 CenterY=-26.5 CenterZ=0 NormalX=0 NormalY=0 NormalZ=1 AngleXU=0 Radius=1
    g6: BSplineCurve PolesCount=3 KnotsCount=2 Degree=2 IsPeriodic=0
    g7: GeomPoint X=-4.2 Y=-13.4877 Z=0
    g8: GeomPoint X=-8.2 Y=-26.5 Z=0
    g9: LineSegment StartX=-14 StartY=-26.5 StartZ=0 EndX=-8.2 EndY=-26.5 EndZ=0
    g10: LineSegment StartX=-10.15 StartY=-12 StartZ=0 EndX=-10.15 EndY=-14 EndZ=0
    g11: LineSegment StartX=-12.8401 StartY=-16 StartZ=0 EndX=-10.1571 EndY=-16 EndZ=0
    g12: LineSegment StartX=-10.15 StartY=-14 StartZ=0 EndX=-8.70761 EndY=-14 EndZ=0
    g13: LineSegment StartX=-12.8401 StartY=-16 StartZ=0 EndX=-12.8401 EndY=-17.6958 EndZ=0
    g14: LineSegment StartX=-10.15 StartY=-12 StartZ=0 EndX=-7.79258 EndY=-12 EndZ=0
    g15: Circle CenterX=-6.2215 CenterY=-2 CenterZ=0 NormalX=0 NormalY=0 NormalZ=1 AngleXU=0 Radius=1
    g16: Circle CenterX=-6.22762 CenterY=-2.58724 CenterZ=0 NormalX=0 NormalY=0 NormalZ=1 AngleXU=0 Radius=1
    g17: Circle CenterX=-6.32538 CenterY=-4 CenterZ=0 NormalX=0 NormalY=0 NormalZ=1 AngleXU=0 Radius=1
    g18: BSplineCurve PolesCount=3 KnotsCount=2 Degree=2 IsPeriodic=0
    g19: GeomPoint X=-6.2215 Y=-2 Z=0
    g20: GeomPoint X=-6.32538 Y=-4 Z=0
    g21: Circle CenterX=-6.48644 CenterY=-5.99526 CenterZ=0 NormalX=0 NormalY=0 NormalZ=1 AngleXU=0 Radius=1
    g22: Circle CenterX=-6.58486 CenterY=-6.99526 CenterZ=0 NormalX=0 NormalY=0 NormalZ=1 AngleXU=0 Radius=1
    g23: Circle CenterX=-6.77343 CenterY=-8 CenterZ=0 NormalX=0 NormalY=0 NormalZ=1 AngleXU=0 Radius=1
    g24: BSplineCurve PolesCount=3 KnotsCount=2 Degree=2 IsPeriodic=0
    g25: GeomPoint X=-6.48644 Y=-5.99526 Z=0
    g26: GeomPoint X=-6.77343 Y=-8 Z=0
    g27: Circle CenterX=-7.19003 CenterY=-10 CenterZ=0 NormalX=0 NormalY=0 NormalZ=1 AngleXU=0 Radius=1
    g28: Circle CenterX=-7.44407 CenterY=-11.0915 CenterZ=0 NormalX=0 NormalY=0 NormalZ=1 AngleXU=0 Radius=1
    g29: Circle CenterX=-7.79258 CenterY=-12 CenterZ=0 NormalX=0 NormalY=0 NormalZ=1 AngleXU=0 Radius=1
    g30: BSplineCurve PolesCount=3 KnotsCount=2 Degree=2 IsPeriodic=0
    g31: GeomPoint X=-7.19003 Y=-10 Z=0
    g32: GeomPoint X=-7.79258 Y=-12 Z=0
    g33: Circle CenterX=-8.70761 CenterY=-14 CenterZ=0 NormalX=0 NormalY=0 NormalZ=1 AngleXU=0 Radius=1
    g34: Circle CenterX=-9.33087 CenterY=-15.1837 CenterZ=0 NormalX=0 NormalY=0 NormalZ=1 AngleXU=0 Radius=1
    g35: Circle CenterX=-10.1571 CenterY=-16 CenterZ=0 NormalX=0 NormalY=0 NormalZ=1 AngleXU=0 Radius=1
    g36: BSplineCurve PolesCount=3 KnotsCount=2 Degree=2 IsPeriodic=0
    g37: GeomPoint X=-8.70761 Y=-14 Z=0
    g38: GeomPoint X=-10.1571 Y=-16 Z=0
    g39: Circle CenterX=-12.8401 CenterY=-17.6958 CenterZ=0 NormalX=0 NormalY=0 NormalZ=1 AngleXU=0 Radius=1
    g40: Circle CenterX=-13.3521 CenterY=-17.9027 CenterZ=0 NormalX=0 NormalY=0 NormalZ=1 AngleXU=0 Radius=1
    g41: Circle CenterX=-14 CenterY=-18 CenterZ=0 NormalX=0 NormalY=0 NormalZ=1 AngleXU=0 Radius=1
    g42: BSplineCurve PolesCount=3 KnotsCount=2 Degree=2 IsPeriodic=0
    g43: GeomPoint X=-12.8401 Y=-17.6958 Z=0
    g44: GeomPoint X=-14 Y=-18 Z=0
    g45: LineSegment StartX=-6.2 StartY=0 StartZ=0 EndX=-7.2 EndY=0 EndZ=0
    g46: LineSegment StartX=-7.2 StartY=0 StartZ=0 EndX=-7.2 EndY=-2 EndZ=0
    g47: LineSegment StartX=-7.2 StartY=-2 StartZ=0 EndX=-6.2215 EndY=-2 EndZ=0
    g48: LineSegment StartX=-6.32538 StartY=-4 StartZ=0 EndX=-7.65538 EndY=-4 EndZ=0
    g49: LineSegment StartX=-7.65538 StartY=-4 StartZ=0 EndX=-7.65538 EndY=-5.99526 EndZ=0
    g50: LineSegment StartX=-7.65538 StartY=-5.99526 StartZ=0 EndX=-6.48644 EndY=-5.99526 EndZ=0
    g51: LineSegment StartX=-6.77343 StartY=-8 StartZ=0 EndX=-8.43343 EndY=-8 EndZ=0
    g52: LineSegment StartX=-8.43343 StartY=-8 StartZ=0 EndX=-8.43343 EndY=-10 EndZ=0
    g53: LineSegment StartX=-8.43343 StartY=-10 StartZ=0 EndX=-7.19003 EndY=-10 EndZ=0
  constraints (112):
    c: Horizontal(g0)
    c: Distance(g0) = 2
    c: Block(g0)
    c: Vertical(g1)
    c: Coincident(g2,g0)
    c: Vertical(g2)
    c: Block(g2)
    c: Coincident(g6,g2)
    c: Weight(g3) = 1
    c: Equal(g3,g4)
    c: Equal(g3,g5)
    c: InternalAlignment(g3,g6)
    c: InternalAlignment(g4,g6)
    c: InternalAlignment(g5,g6)
    c: InternalAlignment(g7,g6)
    c: InternalAlignment(g8,g6)
    c: Block(g6)
    c: Coincident(g9,g1)
    c: Coincident(g9,g6)
    c: Horizontal(g9)
    c: Vertical(g10)
    c: Block(g10)
    c: Horizontal(g11)
    c: Block(g11)
    c: Coincident(g12,g10)
    c: Horizontal(g12)
    c: Block(g12)
    c: Coincident(g13,g11)
    c: Vertical(g13)
    c: Block(g13)
    c: Coincident(g14,g10)
    c: Horizontal(g14)
    c: Block(g14)
    c: Block(g9)
    c: Block(g1)
    c: Weight(g15) = 1
    c: Equal(g15,g16)
    c: Equal(g15,g17)
    c: InternalAlignment(g15,g18)
    c: InternalAlignment(g16,g18)
    c: InternalAlignment(g17,g18)
    c: InternalAlignment(g19,g18)
    c: InternalAlignment(g20,g18)
    c: Weight(g21) = 1
    c: Equal(g21,g22)
    c: Equal(g21,g23)
    c: InternalAlignment(g21,g24)
    c: InternalAlignment(g22,g24)
    c: InternalAlignment(g23,g24)
    c: InternalAlignment(g25,g24)
    c: InternalAlignment(g26,g24)
    c: Weight(g27) = 1
    c: Equal(g27,g28)
    c: Equal(g27,g29)
    c: Coincident(g30,g14)
    c: InternalAlignment(g27,g30)
    c: InternalAlignment(g28,g30)
    c: InternalAlignment(g29,g30)
    c: InternalAlignment(g31,g30)
    c: InternalAlignment(g32,g30)
    c: Coincident(g36,g12)
    c: Weight(g33) = 1
    c: Equal(g33,g34)
    c: Equal(g33,g35)
    c: Coincident(g36,g11)
    c: InternalAlignment(g33,g36)
    c: InternalAlignment(g34,g36)
    c: InternalAlignment(g35,g36)
    c: InternalAlignment(g37,g36)
    c: InternalAlignment(g38,g36)
    c: Coincident(g42,g13)
    c: Weight(g39) = 1
    c: Equal(g39,g40)
    c: Equal(g39,g41)
    c: Coincident(g42,g1)
    c: InternalAlignment(g39,g42)
    c: InternalAlignment(g40,g42)
    c: InternalAlignment(g41,g42)
    c: InternalAlignment(g43,g42)
    c: InternalAlignment(g44,g42)
    c: Block(g18)
    c: Block(g24)
    c: Block(g30)
    c: Block(g36)
    c: Block(g42)
    c: Horizontal(g45)
    c: Coincident(g45,g0)
    c: Vertical(g46)
    c: Coincident(g46,g45)
    c: Coincident(g47,g46)
    c: Coincident(g47,g18)
    c: Horizontal(g47)
    c: Block(g46)
    c: Coincident(g48,g18)
    c: Horizontal(g48)
    c: Distance(g48) = 1.33
    c: Vertical(g49)
    c: Coincident(g49,g48)
    c: Coincident(g50,g49)
    c: Coincident(g50,g24)
    c: Horizontal(g50)
    c: Tangent(g50,g22)
    c: Horizontal(g51)
    c: Coincident(g51,g24)
    c: Block(g51)
    c: Vertical(g52)
    c: Block(g52)
    c: Coincident(g52,g51)
    c: Coincident(g53,g52)
    c: Coincident(g53,g30)
    c: Horizontal(g53)
    c: Distance(g1) = 8.5
FEATURE [Part::Feature] Face024
  shape: bbox 9.8 x 26.5 x 2e-07 mm, 1 faces, 0 solids (baked)
FEATURE [Part::Revolution] Revolve024
  Angle = 360
  Axis = (0,1,0)
  Base = (0,0,0)
  FaceMakerClass = Part::FaceMakerBullseye
  Placement = pos=(0,0,0) rot=(0,0,1;1.5708rad)
  Solid = false
  Source = -> Face024
  Symmetric = false
FEATURE [Part::Feature] Face025
  shape: bbox 9.8 x 26.5 x 2e-07 mm, 1 faces, 0 solids (baked)
FEATURE [Part::Revolution] Revolve025
  Angle = 360
  Axis = (0,1,0)
  Base = (0,0,0)
  FaceMakerClass = Part::FaceMakerBullseye
  Placement = pos=(0,0,0) rot=(0,0,1;1.5708rad)
  Solid = false
  Source = -> Face025
  Symmetric = false
FEATURE [Part::MultiFuse] Fusion033
  Placement = pos=(-18,19,36) rot=(0,0,1;0rad)
  Shapes = -> [Revolve025,Revolve024]
FEATURE [Part::Cylinder] Cylinder014
  Angle = 360
  AttacherType = Attacher::AttachEngine3D
  Height = 20
  Placement = pos=(0,0,36.15) rot=(0,0,1;0rad)
  Radius = 14.3
FEATURE [Part::Cylinder] Cylinder015
  Angle = 360
  AttacherType = Attacher::AttachEngine3D
  Height = 10
  Placement = pos=(0,0,36.15) rot=(0,0,1;0rad)
  Radius = 4
FEATURE [Part::MultiFuse] Fusion034  label="removeToCreteHoleForPlugHousing004"
  Placement = pos=(-42,19,36) rot=(0,1,0;1.5708rad)
  Shapes = -> [Cylinder014,Cylinder015]
FEATURE [Part::Cut] Cut008  label="top004"
  Base = -> Cut004
  Placement = pos=(-1,0,0) rot=(0,0,1;0rad)
  Tool = -> Fusion034
FEATURE [Part::Box] Box005  label="Cube005"
  AttacherType = Attacher::AttachEngine3D
  Height = 28
  Length = 3
  Placement = pos=(110.7,19,22) rot=(0,0,1;0rad)
  Width = 15.7
FEATURE [Part::Cylinder] Cylinder016
  Angle = 360
  AttacherType = Attacher::AttachEngine3D
  Height = 10
  Placement = pos=(0,0,36.15) rot=(0,0,1;0rad)
  Radius = 4
FEATURE [Part::Cylinder] Cylinder017
  Angle = 360
  AttacherType = Attacher::AttachEngine3D
  Height = 20
  Placement = pos=(0,0,36.15) rot=(0,0,1;0rad)
  Radius = 10.3
FEATURE [Part::MultiFuse] Fusion035  label="removeToCreteHoleForPlugHousing005"
  Placement = pos=(70,19,36) rot=(0,1,0;1.5708rad)
  Shapes = -> [Cylinder017,Cylinder016]
FEATURE [Part::Cut] Cut009  label="plugHousingTab001"
  Base = -> Box005
  Placement = pos=(-107.4,-14,0) rot=(0,0,1;0rad)
  Tool = -> Fusion035
FEATURE [Part::Box] Box006  label="Cube006"
  AttacherType = Attacher::AttachEngine3D
  Height = 28
  Length = 3
  Placement = pos=(110.7,19,22) rot=(0,0,1;0rad)
  Width = 15.7
FEATURE [Part::Cylinder] Cylinder018
  Angle = 360
  AttacherType = Attacher::AttachEngine3D
  Height = 10
  Placement = pos=(0,0,36.15) rot=(0,0,1;0rad)
  Radius = 4
FEATURE [Part::Cylinder] Cylinder019
  Angle = 360
  AttacherType = Attacher::AttachEngine3D
  Height = 20
  Placement = pos=(0,0,36.15) rot=(0,0,1;0rad)
  Radius = 10.3
FEATURE [Part::MultiFuse] Fusion036  label="removeToCreteHoleForPlugHousing006"
  Placement = pos=(70,19,36) rot=(0,1,0;1.5708rad)
  Shapes = -> [Cylinder019,Cylinder018]
FEATURE [Part::Cut] Cut010  label="plugHousingTab002"
  Base = -> Box006
  Placement = pos=(-107.4,-14,0) rot=(0,0,1;0rad)
  Tool = -> Fusion036
FEATURE [Part::MultiFuse] Fusion037
  Placement = pos=(9.6,23,0) rot=(0,0,1;3.14159rad)
  Shapes = -> [Cut009,Cut010]
FEATURE [Part::Box] Box  label="Cube"
  AttacherType = Attacher::AttachEngine3D
  Height = 10
  Length = 3
  Placement = pos=(3.3,4,12) rot=(0,0,1;0rad)
  Width = 10
FEATURE [Part::Fillet] Fillet004
  Base = -> Fusion028
  Edges = 1 edges r=2: [Edge25]
FEATURE [Part::Fillet] Fillet005  label="plugHousing046"
  Base = -> Fillet004
  Edges = 1 edges r=2: [Edge8]
FEATURE [Part::Fillet] Fillet006
  Base = -> Box
  Edges = 1 edges r=2: [Edge11]
FEATURE [Part::Box] Box007  label="Cube007"
  AttacherType = Attacher::AttachEngine3D
  Height = 10
  Length = 3
  Placement = pos=(3.3,4,50) rot=(0,0,1;0rad)
  Width = 10
FEATURE [Part::Fillet] Fillet007
  Base = -> Box007
  Edges = 1 edges r=2: [Edge12]
FEATURE [Part::Box] Box008  label="Cube008"
  AttacherType = Attacher::AttachEngine3D
  Height = 28
  Length = 4
  Placement = pos=(5,0,22) rot=(0,0,1;0rad)
  Width = 10
FEATURE [Part::Fillet] Fillet008
  Base = -> Box008
  Edges = 1 edges r=1: [Edge7]
FEATURE [Part::Fillet] Fillet009
  Base = -> Fillet008
  Edges = 1 edges r=2: [Edge5]
FEATURE [Part::Fillet] Fillet010
  Base = -> Fillet009
  Edges = 1 edges r=2: [Edge2]
FEATURE [Sketcher::SketchObject] Sketch009  label="topSketch003"
  FullyConstrained = true
  sketch-geometry (4):
    g0: LineSegment StartX=16.8446 StartY=31.512 StartZ=0 EndX=16.3251 EndY=34.4666 EndZ=0
    g1: ArcOfCircle CenterX=19 CenterY=19.2524 CenterZ=0 NormalX=0 NormalY=0 NormalZ=1 AngleXU=0 Radius=15.4476 StartAngle=1.74483 EndAngle=2.72717
    g2: ArcOfCircle CenterX=19 CenterY=19.2524 CenterZ=0 NormalX=0 NormalY=0 NormalZ=1 AngleXU=0 Radius=12.4476 StartAngle=1.74483 EndAngle=2.73189
    g3: LineSegment StartX=4.86004 StartY=25.4725 StartZ=0 EndX=7.58253 EndY=24.2107 EndZ=0
  constraints (7):
    c: Block(g0)
    c: Coincident(g1,g0)
    c: Coincident(g2,g0)
    c: Coincident(g3,g1)
    c: Coincident(g3,g2)
    c: Block(g1)
    c: Block(g2)
FEATURE [Part::Extrusion] Extrude008
  Base = -> Sketch009
  Dir = (0,0,1)
  DirMode = 2
  FaceMakerClass = Part::FaceMakerBullseye
  LengthFwd = 10
  LengthRev = 0
  Placement = pos=(0,0,31) rot=(0,0,1;0rad)
  Solid = true
  Symmetric = false
FEATURE [Part::Cylinder] Cylinder020
  Angle = 360
  AttacherType = Attacher::AttachEngine3D
  Height = 20
  Placement = pos=(0,0,36.15) rot=(0,0,1;0rad)
  Radius = 8.2
FEATURE [Part::Cylinder] Cylinder021
  Angle = 360
  AttacherType = Attacher::AttachEngine3D
  Height = 10
  Placement = pos=(0,0,36.15) rot=(0,0,1;0rad)
  Radius = 4
FEATURE [Part::MultiFuse] Fusion038  label="removeToCreteHoleForPlugHousing007"
  Placement = pos=(-42,19,36) rot=(0,1,0;1.5708rad)
  Shapes = -> [Cylinder020,Cylinder021]
FEATURE [Part::Cut] Cut011
  Base = -> Extrude008
  Tool = -> Fusion038
FEATURE [Part::Fillet] Fillet011
  Base = -> Cut011
  Edges = 1 edges r=2: [Edge1]
FEATURE [Part::Fillet] Fillet012
  Base = -> Fillet011
  Edges = 1 edges r=2.5: [Edge1]
FEATURE [Part::Fillet] Fillet013
  Base = -> Fillet012
  Edges = 1 edges r=2.5: [Edge2]
FEATURE [Part::Box] Box010  label="Cube010"
  AttacherType = Attacher::AttachEngine3D
  Height = 16
  Length = 8
  Placement = pos=(12.7,31.52,28) rot=(0,0,1;0rad)
  Width = 4
FEATURE [Sketcher::SketchObject] Sketch010  label="topSketch004"
  FullyConstrained = true
  sketch-geometry (4):
    g0: LineSegment StartX=16.8446 StartY=31.512 StartZ=0 EndX=16.3251 EndY=34.4666 EndZ=0
    g1: ArcOfCircle CenterX=19 CenterY=19.2524 CenterZ=0 NormalX=0 NormalY=0 NormalZ=1 AngleXU=0 Radius=15.4476 StartAngle=1.74483 EndAngle=2.72717
    g2: ArcOfCircle CenterX=19 CenterY=19.2524 CenterZ=0 NormalX=0 NormalY=0 NormalZ=1 AngleXU=0 Radius=12.4476 StartAngle=1.74483 EndAngle=2.73189
    g3: LineSegment StartX=4.86004 StartY=25.4725 StartZ=0 EndX=7.58253 EndY=24.2107 EndZ=0
  constraints (7):
    c: Block(g0)
    c: Coincident(g1,g0)
    c: Coincident(g2,g0)
    c: Coincident(g3,g1)
    c: Coincident(g3,g2)
    c: Block(g1)
    c: Block(g2)
FEATURE [Part::Cylinder] Cylinder022
  Angle = 360
  AttacherType = Attacher::AttachEngine3D
  Height = 10
  Placement = pos=(0,0,36.15) rot=(0,0,1;0rad)
  Radius = 4
FEATURE [Sketcher::SketchObject] Sketch011  label="topSketch005"
  FullyConstrained = true
  sketch-geometry (4):
    g0: LineSegment StartX=16.8446 StartY=31.512 StartZ=0 EndX=16.3251 EndY=34.4666 EndZ=0
    g1: ArcOfCircle CenterX=19 CenterY=19.2524 CenterZ=0 NormalX=0 NormalY=0 NormalZ=1 AngleXU=0 Radius=15.4476 StartAngle=1.74483 EndAngle=2.72717
    g2: ArcOfCircle CenterX=19 CenterY=19.2524 CenterZ=0 NormalX=0 NormalY=0 NormalZ=1 AngleXU=0 Radius=12.4476 StartAngle=1.74483 EndAngle=2.73189
    g3: LineSegment StartX=4.86004 StartY=25.4725 StartZ=0 EndX=7.58253 EndY=24.2107 EndZ=0
  constraints (7):
    c: Block(g0)
    c: Coincident(g1,g0)
    c: Coincident(g2,g0)
    c: Coincident(g3,g1)
    c: Coincident(g3,g2)
    c: Block(g1)
    c: Block(g2)
FEATURE [Part::Extrusion] Extrude010
  Base = -> Sketch011
  Dir = (0,0,1)
  DirMode = 2
  FaceMakerClass = Part::FaceMakerBullseye
  LengthFwd = 10.6
  LengthRev = 0
  Placement = pos=(0,0,31) rot=(0,0,1;0rad)
  Solid = true
  Symmetric = false
FEATURE [Part::Cylinder] Cylinder023
  Angle = 360
  AttacherType = Attacher::AttachEngine3D
  Height = 20
  Placement = pos=(0,0,36.15) rot=(0,0,1;0rad)
  Radius = 8.2
FEATURE [Part::MultiFuse] Fusion039  label="removeToCreteHoleForPlugHousing008"
  Placement = pos=(-42,19,36) rot=(0,1,0;1.5708rad)
  Shapes = -> [Cylinder023,Cylinder022]
FEATURE [Part::Cut] Cut012
  Base = -> Extrude010
  Placement = pos=(0,0,-0.3) rot=(0,0,1;0rad)
  Tool = -> Fusion039
FEATURE [Part::Cut] Cut013
  Base = -> Box010
  Tool = -> Cut012
FEATURE [Part::Fillet] Fillet014
  Base = -> Cut013
  Edges = 1 edges r=0.7: [Edge13]
FEATURE [Part::Fillet] Fillet015
  Base = -> Fillet014
  Edges = 1 edges r=0.7: [Edge13]
FEATURE [Part::Fillet] Fillet016
  Base = -> Fillet015
  Edges = 1 edges r=0.7: [Edge16]
FEATURE [Part::Fillet] Fillet017
  Base = -> Fillet016
  Edges = 1 edges r=0.7: [Edge11]
FEATURE [Part::Fillet] Fillet018
  Base = -> Fillet017
  Edges = 1 edges r=0.7: [Edge10]
FEATURE [Part::Fillet] Fillet019
  Base = -> Fillet018
  Edges = 1 edges r=1.2: [Edge5]
FEATURE [Part::Fillet] Fillet020
  Base = -> Fillet019
  Edges = 1 edges r=1.2: [Edge12]
FEATURE [Part::Fillet] Fillet021
  Base = -> Fillet020
  Edges = 1 edges r=2: [Edge1]
  Placement = pos=(0.3,0,0) rot=(0,0,1;0rad)
FEATURE [Part::MultiFuse] Fusion040  label="top005"
  Shapes = -> [Cut008,Fillet021]
FEATURE [Part::MultiFuse] Fusion041  label="wireHolder"
  Shapes = -> [Fusion033,Fillet013]
FEATURE [Part::MultiFuse] Fusion042
  Shapes = -> [Fillet007,Fusion041]
FEATURE [Part::MultiFuse] Fusion043  label="wireHolder001"
  Shapes = -> [Fusion042,Fillet010]
FEATURE [Part::MultiFuse] Fusion044  label="wireHolder002"
  Shapes = -> [Fillet006,Fusion037,Fusion043]
FEATURE [Part::Feature] Face026
  shape: bbox 11 x 6 x 2e-07 mm, 1 faces, 0 solids (baked)
FEATURE [Part::Revolution] Revolve026
  Angle = 360
  Axis = (0,1,0)
  Base = (0,0,0)
  FaceMakerClass = Part::FaceMakerBullseye
  Placement = pos=(30.3,-1,19.7) rot=(0,0,1;0rad)
  Solid = false
  Source = -> Face026
  Symmetric = false
FEATURE [Sketcher::SketchObject] Sketch013  label="topSketch006"
  FullyConstrained = true
  sketch-geometry (13):
    g0: LineSegment StartX=117 StartY=19 StartZ=0 EndX=117 EndY=38 EndZ=0
    g1: ArcOfCircle CenterX=98 CenterY=19 CenterZ=0 NormalX=0 NormalY=0 NormalZ=1 AngleXU=0 Radius=19 StartAngle=5.7297 EndAngle=6.28319
    g2: LineSegment StartX=0 StartY=3 StartZ=0 EndX=0 EndY=19 EndZ=0
    g3: LineSegment StartX=19 StartY=38 StartZ=0 EndX=117 EndY=38 EndZ=0
    g4: ArcOfCircle CenterX=19 CenterY=19 CenterZ=0 NormalX=0 NormalY=0 NormalZ=1 AngleXU=0 Radius=19 StartAngle=1.5708 EndAngle=3.14159
    g5: ArcOfCircle CenterX=19 CenterY=19 CenterZ=0 NormalX=0 NormalY=0 NormalZ=1 AngleXU=0 Radius=16 StartAngle=1.5708 EndAngle=3.14159
    g6: ArcOfCircle CenterX=98 CenterY=19 CenterZ=0 NormalX=0 NormalY=0 NormalZ=1 AngleXU=0 Radius=16 StartAngle=5.60905 EndAngle=6.28319
    g7: LineSegment StartX=114 StartY=19 StartZ=0 EndX=114 EndY=35 EndZ=0
    g8: LineSegment StartX=110.5 StartY=9.01251 StartZ=0 EndX=114.163 EndY=9.01251 EndZ=0
    g9: LineSegment StartX=114 StartY=35 StartZ=0 EndX=19 EndY=35 EndZ=0
    g10: LineSegment StartX=0 StartY=3 StartZ=0 EndX=0 EndY=0 EndZ=0
    g11: LineSegment StartX=3 StartY=0 StartZ=0 EndX=0 EndY=0 EndZ=0
    g12: LineSegment StartX=3 StartY=19 StartZ=0 EndX=3 EndY=0 EndZ=0
  constraints (33):
    c: Vertical(g0)
    c: Distance(g0) = 19
    c: Block(g0)
    c: Coincident(g1,g0)
    c: Block(g1)
    c: Vertical(g2)
    c: Block(g2)
    c: Coincident(g3,g0)
    c: Horizontal(g3)
    c: Distance(g3) = 98
    c: Coincident(g4,g3)
    c: Coincident(g4,g2)
    c: Block(g4)
    c: Coincident(g5,g4)
    c: Coincident(g6,g1)
    c: Block(g6)
    c: Block(g5)
    c: Coincident(g7,g6)
    c: Vertical(g7)
    c: Coincident(g8,g6)
    c: Coincident(g8,g1)
    c: Coincident(g9,g7)
    c: Coincident(g9,g5)
    c: Horizontal(g9)
    c: Tangent(g9,g5)
    c: Coincident(g10,g2)
    c: Distance(g10) = 3
    c: Vertical(g10)
    c: Coincident(g11,g10)
    c: Horizontal(g11)
    c: Coincident(g12,g5)
    c: Coincident(g12,g11)
    c: Vertical(g12)
FEATURE [Part::Extrusion] Extrude011  label="top006"
  Base = -> Sketch013
  Dir = (0,0,1)
  DirMode = 2
  FaceMakerClass = Part::FaceMakerBullseye
  LengthFwd = 72
  LengthRev = 0
  Solid = true
  Symmetric = false
FEATURE [Sketcher::SketchObject] Sketch014
  FullyConstrained = true
  MapMode = 3
  Placement = pos=(0,0,0) rot=(1,0,0;1.5708rad)
  Support = -> [Extrude011]
  sketch-geometry (8):
    g0: Circle CenterX=80.351 CenterY=-67.6202 CenterZ=0 NormalX=0 NormalY=0 NormalZ=1 AngleXU=0 Radius=2
    g1: Circle CenterX=80.351 CenterY=-67.6202 CenterZ=0 NormalX=0 NormalY=0 NormalZ=1 AngleXU=0 Radius=3
    g2: Circle CenterX=80.351 CenterY=-4.92017 CenterZ=0 NormalX=0 NormalY=0 NormalZ=1 AngleXU=0 Radius=2
    g3: Circle CenterX=80.351 CenterY=-4.92017 CenterZ=0 NormalX=0 NormalY=0 NormalZ=1 AngleXU=0 Radius=3
    g4: Circle CenterX=23.851 CenterY=-4.92017 CenterZ=0 NormalX=0 NormalY=0 NormalZ=1 AngleXU=0 Radius=2
    g5: Circle CenterX=23.851 CenterY=-4.92017 CenterZ=0 NormalX=0 NormalY=0 NormalZ=1 AngleXU=0 Radius=3
    g6: Circle CenterX=23.851 CenterY=-67.6202 CenterZ=0 NormalX=0 NormalY=0 NormalZ=1 AngleXU=0 Radius=2
    g7: Circle CenterX=23.851 CenterY=-67.6202 CenterZ=0 NormalX=0 NormalY=0 NormalZ=1 AngleXU=0 Radius=3
  constraints (8):
    c: Block(g3)
    c: Block(g2)
    c: Block(g1)
    c: Block(g0)
    c: Block(g6)
    c: Block(g7)
    c: Block(g4)
    c: Block(g5)
FEATURE [Part::Feature] Face027
  shape: bbox 11 x 6 x 2e-07 mm, 1 faces, 0 solids (baked)
FEATURE [Part::Revolution] Revolve027
  Angle = 360
  Axis = (0,1,0)
  Base = (0,0,0)
  FaceMakerClass = Part::FaceMakerBullseye
  Placement = pos=(30.3,-1,51.7) rot=(0,0,1;0rad)
  Solid = false
  Source = -> Face027
  Symmetric = false
FEATURE [Part::Feature] Face028
  shape: bbox 11 x 6 x 2e-07 mm, 1 faces, 0 solids (baked)
FEATURE [Part::Revolution] Revolve028
  Angle = 360
  Axis = (0,1,0)
  Base = (0,0,0)
  FaceMakerClass = Part::FaceMakerBullseye
  Placement = pos=(62.3,-1,19.7) rot=(0,0,1;0rad)
  Solid = false
  Source = -> Face028
  Symmetric = false
FEATURE [Part::Feature] Face029
  shape: bbox 11 x 6 x 2e-07 mm, 1 faces, 0 solids (baked)
FEATURE [Part::Revolution] Revolve029
  Angle = 360
  Axis = (0,1,0)
  Base = (0,0,0)
  FaceMakerClass = Part::FaceMakerBullseye
  Placement = pos=(62.3,-1,51.7) rot=(0,0,1;0rad)
  Solid = false
  Source = -> Face029
  Symmetric = false
FEATURE [Part::Feature] Wire
  shape: bbox 11 x 5.2 x 2e-07 mm, 0 faces, 0 solids (baked)
FEATURE [Part::Revolution] Revolve030
  Angle = 360
  Axis = (0,1,0)
  Base = (0,0,0)
  FaceMakerClass = Part::FaceMakerBullseye
  Placement = pos=(30.3,38,19.7) rot=(0,0,1;0rad)
  Solid = true
  Source = -> Wire
  Symmetric = false
FEATURE [Part::Feature] Wire001
  shape: bbox 11 x 5.2 x 2e-07 mm, 0 faces, 0 solids (baked)
FEATURE [Part::Revolution] Revolve031
  Angle = 360
  Axis = (0,1,0)
  Base = (0,0,0)
  FaceMakerClass = Part::FaceMakerBullseye
  Placement = pos=(30.3,38,51.7) rot=(0,0,1;0rad)
  Solid = true
  Source = -> Wire001
  Symmetric = false
FEATURE [Part::Feature] Wire002
  shape: bbox 11 x 5.2 x 2e-07 mm, 0 faces, 0 solids (baked)
FEATURE [Part::Revolution] Revolve032
  Angle = 360
  Axis = (0,1,0)
  Base = (0,0,0)
  FaceMakerClass = Part::FaceMakerBullseye
  Placement = pos=(62.3,38,51.7) rot=(0,0,1;0rad)
  Solid = true
  Source = -> Wire002
  Symmetric = false
FEATURE [Part::Feature] Wire003
  shape: bbox 11 x 5.2 x 2e-07 mm, 0 faces, 0 solids (baked)
FEATURE [Part::Revolution] Revolve033
  Angle = 360
  Axis = (0,1,0)
  Base = (0,0,0)
  FaceMakerClass = Part::FaceMakerBullseye
  Placement = pos=(62.3,38,19.7) rot=(0,0,1;0rad)
  Solid = true
  Source = -> Wire003
  Symmetric = false
FEATURE [Part::MultiFuse] Fusion045  label="altRandScrewHousing"
  Shapes = -> [Revolve029,Revolve027,Revolve028,Revolve026]
FEATURE [Part::MultiFuse] Fusion046  label="fanScrewHousing"
  Shapes = -> [Revolve033,Revolve032,Revolve031,Revolve030]
FEATURE [Sketcher::SketchObject] Sketch015
  FullyConstrained = true
  sketch-geometry (17):
    g0: Circle CenterX=-3.5 CenterY=23.5 CenterZ=0 NormalX=0 NormalY=0 NormalZ=1 AngleXU=0 Radius=1
    g1: Circle CenterX=-1 CenterY=15.25 CenterZ=0 NormalX=0 NormalY=0 NormalZ=1 AngleXU=0 Radius=1
    g2: Circle CenterX=-3.5 CenterY=7 CenterZ=0 NormalX=0 NormalY=0 NormalZ=1 AngleXU=0 Radius=1
    g3: BSplineCurve PolesCount=3 KnotsCount=2 Degree=2 IsPeriodic=0
    g4: GeomPoint X=-3.5 Y=23.5 Z=0
    g5: GeomPoint X=-3.5 Y=7 Z=0
    g6: Circle CenterX=-4.8 CenterY=30.5 CenterZ=0 NormalX=0 NormalY=0 NormalZ=1 AngleXU=0 Radius=1
    g7: Circle CenterX=-3.5 CenterY=30.5 CenterZ=0 NormalX=0 NormalY=0 NormalZ=1 AngleXU=0 Radius=1
    g8: Circle CenterX=-3.5 CenterY=29.2 CenterZ=0 NormalX=0 NormalY=0 NormalZ=1 AngleXU=0 Radius=1
    g9: BSplineCurve PolesCount=3 KnotsCount=2 Degree=2 IsPeriodic=0
    g10: GeomPoint X=-4.8 Y=30.5 Z=0
    g11: GeomPoint X=-3.5 Y=29.2 Z=0
    g12: LineSegment StartX=-3.5 StartY=29.2 StartZ=0 EndX=-3.5 EndY=23.5 EndZ=0
    g13: LineSegment StartX=-4.8 StartY=30.5 StartZ=0 EndX=0 EndY=30.5 EndZ=0
    g14: LineSegment StartX=-3.5 StartY=0.3 StartZ=0 EndX=0 EndY=0.3 EndZ=0
    g15: LineSegment StartX=-3.5 StartY=0.3 StartZ=0 EndX=-3.5 EndY=7 EndZ=0
    g16: LineSegment StartX=0 StartY=0.3 StartZ=0 EndX=0 EndY=30.5 EndZ=0
  constraints (33):
    c: Weight(g0) = 1
    c: Equal(g0,g1)
    c: Equal(g0,g2)
    c: InternalAlignment(g0,g3)
    c: InternalAlignment(g1,g3)
    c: InternalAlignment(g2,g3)
    c: InternalAlignment(g4,g3)
    c: InternalAlignment(g5,g3)
    c: Block(g3)
    c: Weight(g6) = 1
    c: Equal(g6,g7)
    c: Equal(g6,g8)
    c: InternalAlignment(g6,g9)
    c: InternalAlignment(g7,g9)
    c: InternalAlignment(g8,g9)
    c: InternalAlignment(g10,g9)
    c: InternalAlignment(g11,g9)
    c: Block(g9)
    c: Coincident(g12,g9)
    c: Coincident(g12,g3)
    c: Vertical(g12)
    c: Coincident(g13,g9)
    c: Horizontal(g13)
    c: Distance(g13) = 4.8
    c: Horizontal(g14)
    c: Block(g14)
    c: Coincident(g15,g14)
    c: Coincident(g15,g3)
    c: Vertical(g15)
    c: Coincident(g16,g14)
    c: Coincident(g16,g13)
    c: Vertical(g16)
    c: Tangent(g16,g1)
FEATURE [Sketcher::SketchObject] Sketch016
  FullyConstrained = true
  sketch-geometry (16):
    g0: Circle CenterX=-3.5 CenterY=23.5 CenterZ=0 NormalX=0 NormalY=0 NormalZ=1 AngleXU=0 Radius=1
    g1: Circle CenterX=-1 CenterY=15.25 CenterZ=0 NormalX=0 NormalY=0 NormalZ=1 AngleXU=0 Radius=1
    g2: Circle CenterX=-3.5 CenterY=7 CenterZ=0 NormalX=0 NormalY=0 NormalZ=1 AngleXU=0 Radius=1
    g3: BSplineCurve PolesCount=3 KnotsCount=2 Degree=2 IsPeriodic=0
    g4: GeomPoint X=-3.5 Y=23.5 Z=0
    g5: GeomPoint X=-3.5 Y=7 Z=0
    g6: LineSegment StartX=-3.5 StartY=28.2 StartZ=0 EndX=-3.5 EndY=23.5 EndZ=0
    g7: LineSegment StartX=0 StartY=29.5 StartZ=0 EndX=0 EndY=30 EndZ=0
    g8: LineSegment StartX=-3.5 StartY=28.2 StartZ=0 EndX=-3.5 EndY=30 EndZ=0
    g9: LineSegment StartX=0 StartY=30 StartZ=0 EndX=0 EndY=30.5 EndZ=0
    g10: LineSegment StartX=0 StartY=30.5 StartZ=0 EndX=-3.5 EndY=30.5 EndZ=0
    g11: LineSegment StartX=-3.5 StartY=30.5 StartZ=0 EndX=-3.5 EndY=30 EndZ=0
    g12: LineSegment StartX=0 StartY=29.5 StartZ=0 EndX=0 EndY=5 EndZ=0
    g13: LineSegment StartX=-3.5 StartY=0.3 StartZ=0 EndX=-3.5 EndY=7 EndZ=0
    g14: LineSegment StartX=-3.5 StartY=0.3 StartZ=0 EndX=0 EndY=0.3 EndZ=0
    g15: LineSegment StartX=0 StartY=5 StartZ=0 EndX=0 EndY=0.3 EndZ=0
  constraints (39):
    c: Weight(g0) = 1
    c: Equal(g0,g1)
    c: Equal(g0,g2)
    c: InternalAlignment(g0,g3)
    c: InternalAlignment(g1,g3)
    c: InternalAlignment(g2,g3)
    c: InternalAlignment(g4,g3)
    c: InternalAlignment(g5,g3)
    c: Block(g3)
    c: Coincident(g6,g3)
    c: Vertical(g6)
    c: Vertical(g7)
    c: Distance(g7) = 0.5
    c: Coincident(g8,g6)
    c: Vertical(g8)
    c: Block(g6)
    c: Block(g7)
    c: Vertical(g9)
    c: Equal(g7,g9) = 0.5
    c: Block(g9)
    c: Coincident(g9,g7)
    c: Horizontal(g10)
    c: Coincident(g10,g9)
    c: Coincident(g11,g10)
    c: Coincident(g11,g8)
    c: Vertical(g11)
    c: Block(g11)
    c: Coincident(g12,g7)
    c: Vertical(g12)
    c: Coincident(g13,g3)
    c: Vertical(g13)
    c: Distance(g13) = 6.7
    c: Coincident(g14,g13)
    c: Horizontal(g14)
    c: Block(g14)
    c: Coincident(g15,g12)
    c: Coincident(g15,g14)
    c: Vertical(g15)
    c: Block(g15)
FEATURE [Sketcher::SketchObject] Sketch017
  FullyConstrained = true
  sketch-geometry (11):
    g0: LineSegment StartX=-3.5 StartY=1e-16 StartZ=0 EndX=-1.6 EndY=1e-16 EndZ=0
    g1: LineSegment StartX=-1.6 StartY=1e-16 StartZ=0 EndX=-1.6 EndY=1.5 EndZ=0
    g2: LineSegment StartX=-3.5 StartY=1.5 StartZ=0 EndX=-1.6 EndY=1.5 EndZ=0
    g3: LineSegment StartX=-3.5 StartY=1e-16 StartZ=0 EndX=-4.8 EndY=1e-16 EndZ=0
    g4: Circle CenterX=-3.5 CenterY=1.3 CenterZ=0 NormalX=0 NormalY=0 NormalZ=1 AngleXU=0 Radius=1
    g5: Circle CenterX=-3.5 CenterY=1e-16 CenterZ=0 NormalX=0 NormalY=0 NormalZ=1 AngleXU=0 Radius=1
    g6: Circle CenterX=-4.8 CenterY=1e-16 CenterZ=0 NormalX=0 NormalY=0 NormalZ=1 AngleXU=0 Radius=1
    g7: BSplineCurve PolesCount=3 KnotsCount=2 Degree=2 IsPeriodic=0
    g8: GeomPoint X=-3.5 Y=1.3 Z=0
    g9: GeomPoint X=-4.8 Y=1e-16 Z=0
    g10: LineSegment StartX=-3.5 StartY=1.3 StartZ=0 EndX=-3.5 EndY=1.5 EndZ=0
  constraints (24):
    c: Horizontal(g0)
    c: Distance(g0) = 1.9
    c: Block(g0)
    c: Coincident(g1,g0)
    c: Vertical(g1)
    c: Coincident(g2,g1)
    c: Horizontal(g2)
    c: Coincident(g3,g0)
    c: Horizontal(g3)
    c: Distance(g3) = 1.3
    c: Weight(g4) = 1
    c: Equal(g4,g5)
    c: Coincident(g5,g0)
    c: Equal(g4,g6)
    c: Coincident(g7,g3)
    c: InternalAlignment(g4,g7)
    c: InternalAlignment(g5,g7)
    c: InternalAlignment(g6,g7)
    c: InternalAlignment(g8,g7)
    c: InternalAlignment(g9,g7)
    c: Coincident(g10,g7)
    c: Coincident(g10,g2)
    c: Vertical(g10)
    c: Block(g10)
FEATURE [Part::Feature] Face035
  shape: bbox 3.2 x 1.5 x 2e-07 mm, 1 faces, 0 solids (baked)
FEATURE [Part::Revolution] Revolve039  label="backCaseScrewRetainer"
  Angle = 360
  Axis = (0,1,0)
  Base = (0,0,0)
  FaceMakerClass = Part::FaceMakerBullseye
  Placement = pos=(12.5,3,62) rot=(0,0,1;0rad)
  Solid = false
  Source = -> Face035
  Symmetric = false
FEATURE [Part::Feature] Face036
  shape: bbox 3.2 x 1.5 x 2e-07 mm, 1 faces, 0 solids (baked)
FEATURE [Part::Feature] Face039
  shape: bbox 4.8 x 30.2 x 2e-07 mm, 1 faces, 0 solids (baked)
FEATURE [Part::Revolution] Revolve043  label="frontCaseScrewPost002"
  Angle = 360
  Axis = (0,1,0)
  Base = (0,0,0)
  FaceMakerClass = Part::FaceMakerBullseye
  Placement = pos=(89.5,4.5,3.5) rot=(0,0,1;0rad)
  Solid = false
  Source = -> Face039
  Symmetric = false
FEATURE [Part::Feature] Face042
  shape: bbox 4.8 x 30.2 x 2e-07 mm, 1 faces, 0 solids (baked)
FEATURE [Part::Revolution] Revolve046  label="frontCaseScrewPost003"
  Angle = 360
  Axis = (0,1,0)
  Base = (0,0,0)
  FaceMakerClass = Part::FaceMakerBullseye
  Placement = pos=(89.5,4.5,68.5) rot=(0,0,1;0rad)
  Solid = false
  Source = -> Face042
  Symmetric = false
FEATURE [Part::Feature] Face043
  shape: bbox 3.2 x 1.5 x 2e-07 mm, 1 faces, 0 solids (baked)
FEATURE [Part::Revolution] Revolve047  label="frontCaseScrewRetainer002"
  Angle = 360
  Axis = (0,1,0)
  Base = (0,0,0)
  FaceMakerClass = Part::FaceMakerBullseye
  Placement = pos=(89.5,3,68.5) rot=(0,0,1;0rad)
  Solid = false
  Source = -> Face043
  Symmetric = false
FEATURE [Part::Feature] Face044
  shape: bbox 3.2 x 1.5 x 2e-07 mm, 1 faces, 0 solids (baked)
FEATURE [Part::Revolution] Revolve048  label="frontCaseScrewRetainer003"
  Angle = 360
  Axis = (0,1,0)
  Base = (0,0,0)
  FaceMakerClass = Part::FaceMakerBullseye
  Placement = pos=(89.5,3,3.5) rot=(0,0,1;0rad)
  Solid = false
  Source = -> Face044
  Symmetric = false
FEATURE [App::MeasureDistance] Distance002  label="Distance: 1.67 mm"
  Distance = 1.66921
  P1 = (99.2361,4.7524,71.7)
  P2 = (99.2347,6.42161,71.7)
FEATURE [Sketcher::SketchObject] Sketch018
  FullyConstrained = true
  sketch-geometry (7):
    g0: LineSegment StartX=0 StartY=0 StartZ=0 EndX=0 EndY=6 EndZ=0
    g1: Circle CenterX=0 CenterY=0 CenterZ=0 NormalX=0 NormalY=0 NormalZ=1 AngleXU=0 Radius=1
    g2: Circle CenterX=8 CenterY=6 CenterZ=0 NormalX=0 NormalY=0 NormalZ=1 AngleXU=0 Radius=1
    g3: BSplineCurve PolesCount=3 KnotsCount=2 Degree=2 IsPeriodic=0
    g4: GeomPoint X=0 Y=0 Z=0
    g5: GeomPoint X=8 Y=6 Z=0
    g6: LineSegment StartX=0 StartY=6 StartZ=0 EndX=8 EndY=6 EndZ=0
  constraints (14):
    c: Coincident(g0,g-1)
    c: Distance(g0) = 6
    c: Vertical(g0)
    c: Coincident(g3,g0)
    c: Weight(g1) = 1
    c: Equal(g1,g2)
    c: InternalAlignment(g1,g3)
    c: InternalAlignment(g2,g3)
    c: InternalAlignment(g4,g3)
    c: InternalAlignment(g5,g3)
    c: Block(g3)
    c: Coincident(g6,g0)
    c: Coincident(g6,g3)
    c: Horizontal(g6)
FEATURE [Part::Extrusion] Extrude012  label="caseScrewPillarBracket"
  Base = -> Sketch018
  Dir = (0,0,1)
  DirMode = 2
  FaceMakerClass = Part::FaceMakerBullseye
  LengthFwd = 2.4
  LengthRev = 0
  Placement = pos=(15.76,29,8.8) rot=(0,1,0;0rad)
  Solid = true
  Symmetric = false
FEATURE [Sketcher::SketchObject] Sketch019
  FullyConstrained = true
  sketch-geometry (7):
    g0: LineSegment StartX=0 StartY=0 StartZ=0 EndX=0 EndY=6 EndZ=0
    g1: Circle CenterX=0 CenterY=0 CenterZ=0 NormalX=0 NormalY=0 NormalZ=1 AngleXU=0 Radius=1
    g2: Circle CenterX=8 CenterY=6 CenterZ=0 NormalX=0 NormalY=0 NormalZ=1 AngleXU=0 Radius=1
    g3: BSplineCurve PolesCount=3 KnotsCount=2 Degree=2 IsPeriodic=0
    g4: GeomPoint X=0 Y=0 Z=0
    g5: GeomPoint X=8 Y=6 Z=0
    g6: LineSegment StartX=0 StartY=6 StartZ=0 EndX=8 EndY=6 EndZ=0
  constraints (14):
    c: Coincident(g0,g-1)
    c: Distance(g0) = 6
    c: Vertical(g0)
    c: Coincident(g3,g0)
    c: Weight(g1) = 1
    c: Equal(g1,g2)
    c: InternalAlignment(g1,g3)
    c: InternalAlignment(g2,g3)
    c: InternalAlignment(g4,g3)
    c: InternalAlignment(g5,g3)
    c: Block(g3)
    c: Coincident(g6,g0)
    c: Coincident(g6,g3)
    c: Horizontal(g6)
FEATURE [Part::Extrusion] Extrude013  label="caseScrewPillarBracket001"
  Base = -> Sketch019
  Dir = (0,0,1)
  DirMode = 2
  FaceMakerClass = Part::FaceMakerBullseye
  LengthFwd = 2.4
  LengthRev = 0
  Placement = pos=(15.76,29,60.8) rot=(0,0,1;0rad)
  Solid = true
  Symmetric = false
FEATURE [Sketcher::SketchObject] Sketch020
  FullyConstrained = true
  sketch-geometry (7):
    g0: LineSegment StartX=0 StartY=0 StartZ=0 EndX=0 EndY=6 EndZ=0
    g1: Circle CenterX=0 CenterY=0 CenterZ=0 NormalX=0 NormalY=0 NormalZ=1 AngleXU=0 Radius=1
    g2: Circle CenterX=8 CenterY=6 CenterZ=0 NormalX=0 NormalY=0 NormalZ=1 AngleXU=0 Radius=1
    g3: BSplineCurve PolesCount=3 KnotsCount=2 Degree=2 IsPeriodic=0
    g4: GeomPoint X=0 Y=0 Z=0
    g5: GeomPoint X=8 Y=6 Z=0
    g6: LineSegment StartX=0 StartY=6 StartZ=0 EndX=8 EndY=6 EndZ=0
  constraints (14):
    c: Coincident(g0,g-1)
    c: Distance(g0) = 6
    c: Vertical(g0)
    c: Coincident(g3,g0)
    c: Weight(g1) = 1
    c: Equal(g1,g2)
    c: InternalAlignment(g1,g3)
    c: InternalAlignment(g2,g3)
    c: InternalAlignment(g4,g3)
    c: InternalAlignment(g5,g3)
    c: Block(g3)
    c: Coincident(g6,g0)
    c: Coincident(g6,g3)
    c: Horizontal(g6)
FEATURE [Part::Extrusion] Extrude014  label="caseScrewPillarBracket002"
  Base = -> Sketch020
  Dir = (0,0,1)
  DirMode = 2
  FaceMakerClass = Part::FaceMakerBullseye
  LengthFwd = 2.4
  LengthRev = 0
  Placement = pos=(13.7,29,13.26) rot=(0,-1,0;1.5708rad)
  Solid = true
  Symmetric = false
FEATURE [Sketcher::SketchObject] Sketch021
  FullyConstrained = true
  sketch-geometry (7):
    g0: LineSegment StartX=0 StartY=0 StartZ=0 EndX=0 EndY=6 EndZ=0
    g1: Circle CenterX=0 CenterY=0 CenterZ=0 NormalX=0 NormalY=0 NormalZ=1 AngleXU=0 Radius=1
    g2: Circle CenterX=8 CenterY=6 CenterZ=0 NormalX=0 NormalY=0 NormalZ=1 AngleXU=0 Radius=1
    g3: BSplineCurve PolesCount=3 KnotsCount=2 Degree=2 IsPeriodic=0
    g4: GeomPoint X=0 Y=0 Z=0
    g5: GeomPoint X=8 Y=6 Z=0
    g6: LineSegment StartX=0 StartY=6 StartZ=0 EndX=8 EndY=6 EndZ=0
  constraints (14):
    c: Coincident(g0,g-1)
    c: Distance(g0) = 6
    c: Vertical(g0)
    c: Coincident(g3,g0)
    c: Weight(g1) = 1
    c: Equal(g1,g2)
    c: InternalAlignment(g1,g3)
    c: InternalAlignment(g2,g3)
    c: InternalAlignment(g4,g3)
    c: InternalAlignment(g5,g3)
    c: Block(g3)
    c: Coincident(g6,g0)
    c: Coincident(g6,g3)
    c: Horizontal(g6)
FEATURE [Part::Extrusion] Extrude015  label="caseScrewPillarBracket003"
  Base = -> Sketch021
  Dir = (0,0,1)
  DirMode = 2
  FaceMakerClass = Part::FaceMakerBullseye
  LengthFwd = 2.4
  LengthRev = 0
  Placement = pos=(11.3,29,58.74) rot=(0,1,0;1.5708rad)
  Solid = true
  Symmetric = false
FEATURE [Sketcher::SketchObject] Sketch022
  FullyConstrained = true
  sketch-geometry (7):
    g0: LineSegment StartX=0 StartY=0 StartZ=0 EndX=0 EndY=6 EndZ=0
    g1: Circle CenterX=0 CenterY=0 CenterZ=0 NormalX=0 NormalY=0 NormalZ=1 AngleXU=0 Radius=1
    g2: Circle CenterX=8 CenterY=6 CenterZ=0 NormalX=0 NormalY=0 NormalZ=1 AngleXU=0 Radius=1
    g3: BSplineCurve PolesCount=3 KnotsCount=2 Degree=2 IsPeriodic=0
    g4: GeomPoint X=0 Y=0 Z=0
    g5: GeomPoint X=8 Y=6 Z=0
    g6: LineSegment StartX=0 StartY=6 StartZ=0 EndX=8 EndY=6 EndZ=0
  constraints (14):
    c: Coincident(g0,g-1)
    c: Distance(g0) = 6
    c: Vertical(g0)
    c: Coincident(g3,g0)
    c: Weight(g1) = 1
    c: Equal(g1,g2)
    c: InternalAlignment(g1,g3)
    c: InternalAlignment(g2,g3)
    c: InternalAlignment(g4,g3)
    c: InternalAlignment(g5,g3)
    c: Block(g3)
    c: Coincident(g6,g0)
    c: Coincident(g6,g3)
    c: Horizontal(g6)
FEATURE [Part::Extrusion] Extrude016  label="caseScrewPillarBracket004"
  Base = -> Sketch022
  Dir = (0,0,1)
  DirMode = 2
  FaceMakerClass = Part::FaceMakerBullseye
  LengthFwd = 2.4
  LengthRev = 0
  Placement = pos=(88.3,29,65.23) rot=(0,1,0;1.5708rad)
  Solid = true
  Symmetric = false
FEATURE [Sketcher::SketchObject] Sketch023
  FullyConstrained = true
  sketch-geometry (7):
    g0: LineSegment StartX=0 StartY=0 StartZ=0 EndX=0 EndY=6 EndZ=0
    g1: Circle CenterX=0 CenterY=0 CenterZ=0 NormalX=0 NormalY=0 NormalZ=1 AngleXU=0 Radius=1
    g2: Circle CenterX=8 CenterY=6 CenterZ=0 NormalX=0 NormalY=0 NormalZ=1 AngleXU=0 Radius=1
    g3: BSplineCurve PolesCount=3 KnotsCount=2 Degree=2 IsPeriodic=0
    g4: GeomPoint X=0 Y=0 Z=0
    g5: GeomPoint X=8 Y=6 Z=0
    g6: LineSegment StartX=0 StartY=6 StartZ=0 EndX=8 EndY=6 EndZ=0
  constraints (14):
    c: Coincident(g0,g-1)
    c: Distance(g0) = 6
    c: Vertical(g0)
    c: Coincident(g3,g0)
    c: Weight(g1) = 1
    c: Equal(g1,g2)
    c: InternalAlignment(g1,g3)
    c: InternalAlignment(g2,g3)
    c: InternalAlignment(g4,g3)
    c: InternalAlignment(g5,g3)
    c: Block(g3)
    c: Coincident(g6,g0)
    c: Coincident(g6,g3)
    c: Horizontal(g6)
FEATURE [Part::Extrusion] Extrude017  label="caseScrewPillarBracket005"
  Base = -> Sketch023
  Dir = (0,0,1)
  DirMode = 2
  FaceMakerClass = Part::FaceMakerBullseye
  LengthFwd = 2.4
  LengthRev = 0
  Placement = pos=(90.7,29,6.77) rot=(0,-1,0;1.5708rad)
  Solid = true
  Symmetric = false
FEATURE [Sketcher::SketchObject] Sketch024
  FullyConstrained = true
  sketch-geometry (7):
    g0: LineSegment StartX=0 StartY=0 StartZ=0 EndX=0 EndY=6 EndZ=0
    g1: Circle CenterX=0 CenterY=0 CenterZ=0 NormalX=0 NormalY=0 NormalZ=1 AngleXU=0 Radius=1
    g2: Circle CenterX=8 CenterY=6 CenterZ=0 NormalX=0 NormalY=0 NormalZ=1 AngleXU=0 Radius=1
    g3: BSplineCurve PolesCount=3 KnotsCount=2 Degree=2 IsPeriodic=0
    g4: GeomPoint X=0 Y=0 Z=0
    g5: GeomPoint X=8 Y=6 Z=0
    g6: LineSegment StartX=0 StartY=6 StartZ=0 EndX=8 EndY=6 EndZ=0
  constraints (14):
    c: Coincident(g0,g-1)
    c: Distance(g0) = 6
    c: Vertical(g0)
    c: Coincident(g3,g0)
    c: Weight(g1) = 1
    c: Equal(g1,g2)
    c: InternalAlignment(g1,g3)
    c: InternalAlignment(g2,g3)
    c: InternalAlignment(g4,g3)
    c: InternalAlignment(g5,g3)
    c: Block(g3)
    c: Coincident(g6,g0)
    c: Coincident(g6,g3)
    c: Horizontal(g6)
FEATURE [Part::Extrusion] Extrude018  label="caseScrewPillarBracket006"
  Base = -> Sketch024
  Dir = (0,0,1)
  DirMode = 2
  FaceMakerClass = Part::FaceMakerBullseye
  LengthFwd = 2.4
  LengthRev = 0
  Placement = pos=(103.7,29,6.77) rot=(0,-1,0;1.5708rad)
  Solid = true
  Symmetric = false
FEATURE [Sketcher::SketchObject] Sketch025
  FullyConstrained = true
  sketch-geometry (7):
    g0: LineSegment StartX=0 StartY=0 StartZ=0 EndX=0 EndY=6 EndZ=0
    g1: Circle CenterX=0 CenterY=0 CenterZ=0 NormalX=0 NormalY=0 NormalZ=1 AngleXU=0 Radius=1
    g2: Circle CenterX=8 CenterY=6 CenterZ=0 NormalX=0 NormalY=0 NormalZ=1 AngleXU=0 Radius=1
    g3: BSplineCurve PolesCount=3 KnotsCount=2 Degree=2 IsPeriodic=0
    g4: GeomPoint X=0 Y=0 Z=0
    g5: GeomPoint X=8 Y=6 Z=0
    g6: LineSegment StartX=0 StartY=6 StartZ=0 EndX=8 EndY=6 EndZ=0
  constraints (14):
    c: Coincident(g0,g-1)
    c: Distance(g0) = 6
    c: Vertical(g0)
    c: Coincident(g3,g0)
    c: Weight(g1) = 1
    c: Equal(g1,g2)
    c: InternalAlignment(g1,g3)
    c: InternalAlignment(g2,g3)
    c: InternalAlignment(g4,g3)
    c: InternalAlignment(g5,g3)
    c: Block(g3)
    c: Coincident(g6,g0)
    c: Coincident(g6,g3)
    c: Horizontal(g6)
FEATURE [Part::Extrusion] Extrude019  label="caseScrewPillarBracket007"
  Base = -> Sketch025
  Dir = (0,0,1)
  DirMode = 2
  FaceMakerClass = Part::FaceMakerBullseye
  LengthFwd = 2.4
  LengthRev = 0
  Placement = pos=(101.3,29,65.23) rot=(0,1,0;1.5708rad)
  Solid = true
  Symmetric = false
FEATURE [Part::Box] Box011  label="frontCaseScrewPillarBracket"
  AttacherType = Attacher::AttachEngine3D
  Height = 2.4
  Length = 16
  Placement = pos=(87,28,2.3) rot=(0,0,1;0rad)
  Width = 7
FEATURE [Part::Box] Box012  label="frontCaseScrewPillarBracket001"
  AttacherType = Attacher::AttachEngine3D
  Height = 2.4
  Length = 16
  Placement = pos=(87,28,67.3) rot=(0,0,1;0rad)
  Width = 7
FEATURE [Sketcher::SketchObject] Sketch026
  FullyConstrained = true
  sketch-geometry (17):
    g0: Circle CenterX=-3.5 CenterY=23.5 CenterZ=0 NormalX=0 NormalY=0 NormalZ=1 AngleXU=0 Radius=1
    g1: Circle CenterX=-1 CenterY=15.25 CenterZ=0 NormalX=0 NormalY=0 NormalZ=1 AngleXU=0 Radius=1
    g2: Circle CenterX=-3.5 CenterY=7 CenterZ=0 NormalX=0 NormalY=0 NormalZ=1 AngleXU=0 Radius=1
    g3: BSplineCurve PolesCount=3 KnotsCount=2 Degree=2 IsPeriodic=0
    g4: GeomPoint X=-3.5 Y=23.5 Z=0
    g5: GeomPoint X=-3.5 Y=7 Z=0
    g6: Circle CenterX=-4.8 CenterY=30.5 CenterZ=0 NormalX=0 NormalY=0 NormalZ=1 AngleXU=0 Radius=1
    g7: Circle CenterX=-3.5 CenterY=30.5 CenterZ=0 NormalX=0 NormalY=0 NormalZ=1 AngleXU=0 Radius=1
    g8: Circle CenterX=-3.5 CenterY=29.2 CenterZ=0 NormalX=0 NormalY=0 NormalZ=1 AngleXU=0 Radius=1
    g9: BSplineCurve PolesCount=3 KnotsCount=2 Degree=2 IsPeriodic=0
    g10: GeomPoint X=-4.8 Y=30.5 Z=0
    g11: GeomPoint X=-3.5 Y=29.2 Z=0
    g12: LineSegment StartX=-3.5 StartY=29.2 StartZ=0 EndX=-3.5 EndY=23.5 EndZ=0
    g13: LineSegment StartX=-4.8 StartY=30.5 StartZ=0 EndX=0 EndY=30.5 EndZ=0
    g14: LineSegment StartX=-3.5 StartY=5 StartZ=0 EndX=-3.5 EndY=7 EndZ=0
    g15: LineSegment StartX=0 StartY=5 StartZ=0 EndX=0 EndY=30.5 EndZ=0
    g16: LineSegment StartX=-3.5 StartY=5 StartZ=0 EndX=0 EndY=5 EndZ=0
  constraints (33):
    c: Weight(g0) = 1
    c: Equal(g0,g1)
    c: Equal(g0,g2)
    c: InternalAlignment(g0,g3)
    c: InternalAlignment(g1,g3)
    c: InternalAlignment(g2,g3)
    c: InternalAlignment(g4,g3)
    c: InternalAlignment(g5,g3)
    c: Block(g3)
    c: Weight(g6) = 1
    c: Equal(g6,g7)
    c: Equal(g6,g8)
    c: InternalAlignment(g6,g9)
    c: InternalAlignment(g7,g9)
    c: InternalAlignment(g8,g9)
    c: InternalAlignment(g10,g9)
    c: InternalAlignment(g11,g9)
    c: Block(g9)
    c: Coincident(g12,g9)
    c: Coincident(g12,g3)
    c: Vertical(g12)
    c: Coincident(g13,g9)
    c: Horizontal(g13)
    c: Distance(g13) = 4.8
    c: Coincident(g14,g3)
    c: Vertical(g14)
    c: Coincident(g15,g13)
    c: Vertical(g15)
    c: Tangent(g15,g1)
    c: Distance(g14) = 2
    c: Coincident(g16,g14)
    c: Horizontal(g16)
    c: Coincident(g15,g16)
FEATURE [Part::Feature] Face050
  shape: bbox 4.8 x 25.5 x 2e-07 mm, 1 faces, 0 solids (baked)
FEATURE [Part::Revolution] Revolve054  label="moreFrontCaseScrewPost001"
  Angle = 360
  Axis = (0,1,0)
  Base = (0,0,0)
  FaceMakerClass = Part::FaceMakerBullseye
  Placement = pos=(102.5,4.5,3.5) rot=(0,0,1;0rad)
  Solid = false
  Source = -> Face050
  Symmetric = false
FEATURE [Part::Feature] Face051
  shape: bbox 4.8 x 25.5 x 2e-07 mm, 1 faces, 0 solids (baked)
FEATURE [Part::Revolution] Revolve055  label="moreFrontCaseScrewPost002"
  Angle = 360
  Axis = (0,1,0)
  Base = (0,0,0)
  FaceMakerClass = Part::FaceMakerBullseye
  Placement = pos=(102.5,4.5,68.5) rot=(0,0,1;0rad)
  Solid = false
  Source = -> Face051
  Symmetric = false
FEATURE [Sketcher::SketchObject] Sketch027
  FullyConstrained = true
  sketch-geometry (10):
    g0: LineSegment StartX=-1.6 StartY=4.7 StartZ=0 EndX=-1.6 EndY=1.7 EndZ=0
    g1: LineSegment StartX=-3.5 StartY=4.7 StartZ=0 EndX=-1.6 EndY=4.7 EndZ=0
    g2: LineSegment StartX=-1.6 StartY=1.7 StartZ=0 EndX=-1.6 EndY=1.5 EndZ=0
    g3: LineSegment StartX=-1.6 StartY=1.5 StartZ=0 EndX=-5.2 EndY=1.5 EndZ=0
    g4: Circle CenterX=-3.5 CenterY=4.7 CenterZ=0 NormalX=0 NormalY=0 NormalZ=1 AngleXU=0 Radius=1
    g5: Circle CenterX=-3.59627 CenterY=2.99743 CenterZ=0 NormalX=0 NormalY=0 NormalZ=1 AngleXU=0 Radius=1
    g6: Circle CenterX=-5.2 CenterY=1.5 CenterZ=0 NormalX=0 NormalY=0 NormalZ=1 AngleXU=0 Radius=1
    g7: BSplineCurve PolesCount=3 KnotsCount=2 Degree=2 IsPeriodic=0
    g8: GeomPoint X=-3.5 Y=4.7 Z=0
    g9: GeomPoint X=-5.2 Y=1.5 Z=0
  constraints (23):
    c: Vertical(g0)
    c: Distance(g0) = 3
    c: Coincident(g1,g0)
    c: Horizontal(g1)
    c: Block(g0)
    c: Block(g1)
    c: Coincident(g2,g0)
    c: Vertical(g2)
    c: Distance(g2) = 0.2
    c: Coincident(g3,g2)
    c: Horizontal(g3)
    c: Block(g3)
    c: Coincident(g7,g1)
    c: Weight(g4) = 1
    c: Equal(g4,g5)
    c: Equal(g4,g6)
    c: Coincident(g7,g3)
    c: InternalAlignment(g4,g7)
    c: InternalAlignment(g5,g7)
    c: InternalAlignment(g6,g7)
    c: InternalAlignment(g8,g7)
    c: InternalAlignment(g9,g7)
    c: Block(g7)
FEATURE [Sketcher::SketchObject] Sketch028
  FullyConstrained = true
  sketch-geometry (18):
    g0: LineSegment StartX=0 StartY=3e-16 StartZ=0 EndX=0 EndY=1.7 EndZ=0
    g1: LineSegment StartX=-3.5 StartY=0 StartZ=0 EndX=-3.5 EndY=0.9 EndZ=0
    g2: Circle CenterX=-2.7 CenterY=1.7 CenterZ=0 NormalX=0 NormalY=0 NormalZ=1 AngleXU=0 Radius=1
    g3: Circle CenterX=-3.5 CenterY=1.7 CenterZ=0 NormalX=0 NormalY=0 NormalZ=1 AngleXU=0 Radius=1
    g4: Circle CenterX=-3.5 CenterY=0.9 CenterZ=0 NormalX=0 NormalY=0 NormalZ=1 AngleXU=0 Radius=1
    g5: BSplineCurve PolesCount=3 KnotsCount=2 Degree=2 IsPeriodic=0
    g6: GeomPoint X=-2.7 Y=1.7 Z=0
    g7: GeomPoint X=-3.5 Y=0.9 Z=0
    g8: LineSegment StartX=-3.5 StartY=0 StartZ=0 EndX=-3.5 EndY=-7 EndZ=0
    g9: LineSegment StartX=0 StartY=3e-16 StartZ=0 EndX=0 EndY=-7 EndZ=0
    g10: LineSegment StartX=-3.5 StartY=-7 StartZ=0 EndX=0 EndY=-7 EndZ=0
    g11: LineSegment StartX=-2.7 StartY=1.7 StartZ=0 EndX=-1.6 EndY=1.7 EndZ=0
    g12: LineSegment StartX=0 StartY=1.7 StartZ=0 EndX=0 EndY=4.5 EndZ=0
    g13: LineSegment StartX=0 StartY=4.5 StartZ=0 EndX=0 EndY=10.8 EndZ=0
    g14: LineSegment StartX=0 StartY=10.8 StartZ=0 EndX=-2 EndY=10.8 EndZ=0
    g15: LineSegment StartX=-1.6 StartY=4.7 StartZ=0 EndX=-1.6 EndY=1.7 EndZ=0
    g16: LineSegment StartX=-1.6 StartY=4.7 StartZ=0 EndX=-2 EndY=4.7 EndZ=0
    g17: LineSegment StartX=-2 StartY=4.7 StartZ=0 EndX=-2 EndY=10.8 EndZ=0
  constraints (44):
    c: Vertical(g0)
    c: Vertical(g1)
    c: Distance(g1) = 0.9
    c: Block(g0)
    c: Distance(g0) = 1.7
    c: Weight(g2) = 1
    c: Equal(g2,g3)
    c: Equal(g2,g4)
    c: Coincident(g5,g1)
    c: InternalAlignment(g2,g5)
    c: InternalAlignment(g3,g5)
    c: InternalAlignment(g4,g5)
    c: InternalAlignment(g6,g5)
    c: InternalAlignment(g7,g5)
    c: Block(g5)
    c: Coincident(g8,g1)
    c: Vertical(g8)
    c: Distance(g8) = 7
    c: Vertical(g9)
    c: Equal(g8,g9) = 7
    c: Coincident(g9,g0)
    c: Coincident(g10,g8)
    c: Coincident(g10,g9)
    c: Horizontal(g10)
    c: Coincident(g11,g5)
    c: Horizontal(g11)
    c: Coincident(g12,g0)
    c: Vertical(g12)
    c: Distance(g12) = 2.8
    c: Coincident(g13,g12)
    c: Vertical(g13)
    c: Distance(g13) = 6.3
    c: Coincident(g14,g13)
    c: Horizontal(g14)
    c: Distance(g14) = 2
    c: Vertical(g15)
    c: Distance(g15) = 3
    c: Block(g11)
    c: Coincident(g15,g11)
    c: Coincident(g16,g15)
    c: Horizontal(g16)
    c: Coincident(g17,g16)
    c: Coincident(g17,g14)
    c: Vertical(g17)
FEATURE [Part::Revolution] Revolve040  label="backCaseScrewRetainer001"
  Angle = 360
  Axis = (0,1,0)
  Base = (0,0,0)
  FaceMakerClass = Part::FaceMakerBullseye
  Placement = pos=(12.5,3,10) rot=(0,0,1;0rad)
  Solid = false
  Source = -> Face036
  Symmetric = false
FEATURE [Part::Feature] Face055
  shape: bbox 3.5 x 30.2 x 2e-07 mm, 1 faces, 0 solids (baked)
FEATURE [Part::Revolution] Revolve059  label="backCaseScrewPost"
  Angle = 360
  Axis = (0,1,0)
  Base = (0,0,0)
  FaceMakerClass = Part::FaceMakerBullseye
  Placement = pos=(12.5,4.5,10) rot=(0,0,1;0rad)
  Solid = false
  Source = -> Face055
  Symmetric = false
FEATURE [Part::Feature] Face056
  shape: bbox 3.5 x 30.2 x 2e-07 mm, 1 faces, 0 solids (baked)
FEATURE [Part::Revolution] Revolve060  label="backCaseScrewPost001"
  Angle = 360
  Axis = (0,1,0)
  Base = (0,0,0)
  FaceMakerClass = Part::FaceMakerBullseye
  Placement = pos=(12.5,4.5,62) rot=(0,0,1;0rad)
  Solid = false
  Source = -> Face056
  Symmetric = false
FEATURE [Part::Feature] Face057
  shape: bbox 3.5 x 17.8 x 2e-07 mm, 1 faces, 0 solids (baked)
FEATURE [Part::Revolution] Revolve061  label="removeToCreateScrewAndThreadedInsertHole"
  Angle = 360
  Axis = (0,1,0)
  Base = (0,0,0)
  FaceMakerClass = Part::FaceMakerBullseye
  Placement = pos=(12.5,0,10) rot=(0,0,1;0rad)
  Solid = false
  Source = -> Face057
  Symmetric = false
FEATURE [Part::Feature] Face058
  shape: bbox 3.5 x 17.8 x 2e-07 mm, 1 faces, 0 solids (baked)
FEATURE [Part::Revolution] Revolve062  label="removeToCreateScrewAndThreadedInsertHole001"
  Angle = 360
  Axis = (0,1,0)
  Base = (0,0,0)
  FaceMakerClass = Part::FaceMakerBullseye
  Placement = pos=(12.5,0,62) rot=(0,0,1;0rad)
  Solid = false
  Source = -> Face058
  Symmetric = false
FEATURE [Part::Feature] Face059
  shape: bbox 3.5 x 17.8 x 2e-07 mm, 1 faces, 0 solids (baked)
FEATURE [Part::Revolution] Revolve063  label="removeToCreateScrewAndThreadedInsertHole002"
  Angle = 360
  Axis = (0,1,0)
  Base = (0,0,0)
  FaceMakerClass = Part::FaceMakerBullseye
  Placement = pos=(89.5,0,68.5) rot=(0,0,1;0rad)
  Solid = false
  Source = -> Face059
  Symmetric = false
FEATURE [Part::Feature] Face060
  shape: bbox 3.5 x 17.8 x 2e-07 mm, 1 faces, 0 solids (baked)
FEATURE [Part::Revolution] Revolve064  label="removeToCreateScrewAndThreadedInsertHole003"
  Angle = 360
  Axis = (0,1,0)
  Base = (0,0,0)
  FaceMakerClass = Part::FaceMakerBullseye
  Placement = pos=(89.5,0,3.5) rot=(0,0,1;0rad)
  Solid = false
  Source = -> Face060
  Symmetric = false
FEATURE [Part::Feature] Face061
  shape: bbox 3.5 x 17.8 x 2e-07 mm, 1 faces, 0 solids (baked)
FEATURE [Part::Revolution] Revolve065  label="removeToCreateScrewAndThreadedInsertHole004"
  Angle = 360
  Axis = (0,1,0)
  Base = (0,0,0)
  FaceMakerClass = Part::FaceMakerBullseye
  Placement = pos=(102.5,4.7,3.5) rot=(0,0,1;0rad)
  Solid = false
  Source = -> Face061
  Symmetric = false
FEATURE [Part::Feature] Face062
  shape: bbox 3.5 x 17.8 x 2e-07 mm, 1 faces, 0 solids (baked)
FEATURE [Part::Revolution] Revolve066  label="removeToCreateScrewAndThreadedInsertHole005"
  Angle = 360
  Axis = (0,1,0)
  Base = (0,0,0)
  FaceMakerClass = Part::FaceMakerBullseye
  Placement = pos=(102.5,4.7,68.5) rot=(0,0,1;0rad)
  Solid = false
  Source = -> Face062
  Symmetric = false
FEATURE [Part::MultiFuse] Fusion047  label="makeHoles"
  Shapes = -> [Revolve066,Revolve065,Revolve064,Revolve063,Revolve062,Revolve061]
FEATURE [Part::Feature] Face063
  shape: bbox 3.6 x 3.2 x 2e-07 mm, 1 faces, 0 solids (baked)
FEATURE [Part::Revolution] Revolve067  label="moreFrontCaseScrewRetainer002"
  Angle = 360
  Axis = (0,1,0)
  Base = (0,0,0)
  FaceMakerClass = Part::FaceMakerBullseye
  Placement = pos=(102.5,4.5,68.5) rot=(0,0,1;0rad)
  Solid = false
  Source = -> Face063
  Symmetric = false
FEATURE [Part::Feature] Face064
  shape: bbox 3.6 x 3.2 x 2e-07 mm, 1 faces, 0 solids (baked)
FEATURE [Part::Revolution] Revolve068  label="moreFrontCaseScrewRetainer003"
  Angle = 360
  Axis = (0,1,0)
  Base = (0,0,0)
  FaceMakerClass = Part::FaceMakerBullseye
  Placement = pos=(102.5,4.5,3.5) rot=(0,0,1;0rad)
  Solid = false
  Source = -> Face064
  Symmetric = false
FEATURE [Part::Feature] Face065
  shape: bbox 3.5 x 17.8 x 2e-07 mm, 1 faces, 0 solids (baked)
FEATURE [Part::Revolution] Revolve069  label="removeToCreateScrewAndThreadedInsertHole006"
  Angle = 360
  Axis = (0,1,0)
  Base = (0,0,0)
  FaceMakerClass = Part::FaceMakerBullseye
  Placement = pos=(12.5,0,10) rot=(0,0,1;0rad)
  Solid = false
  Source = -> Face065
  Symmetric = false
FEATURE [Part::Feature] Face066
  shape: bbox 3.5 x 17.8 x 2e-07 mm, 1 faces, 0 solids (baked)
FEATURE [Part::Revolution] Revolve070  label="removeToCreateScrewAndThreadedInsertHole007"
  Angle = 360
  Axis = (0,1,0)
  Base = (0,0,0)
  FaceMakerClass = Part::FaceMakerBullseye
  Placement = pos=(12.5,0,62) rot=(0,0,1;0rad)
  Solid = false
  Source = -> Face066
  Symmetric = false
FEATURE [Part::Feature] Face067
  shape: bbox 3.5 x 17.8 x 2e-07 mm, 1 faces, 0 solids (baked)
FEATURE [Part::Revolution] Revolve071  label="removeToCreateScrewAndThreadedInsertHole008"
  Angle = 360
  Axis = (0,1,0)
  Base = (0,0,0)
  FaceMakerClass = Part::FaceMakerBullseye
  Placement = pos=(89.5,0,68.5) rot=(0,0,1;0rad)
  Solid = false
  Source = -> Face067
  Symmetric = false
FEATURE [Part::Feature] Face068
  shape: bbox 3.5 x 17.8 x 2e-07 mm, 1 faces, 0 solids (baked)
FEATURE [Part::Revolution] Revolve072  label="removeToCreateScrewAndThreadedInsertHole009"
  Angle = 360
  Axis = (0,1,0)
  Base = (0,0,0)
  FaceMakerClass = Part::FaceMakerBullseye
  Placement = pos=(89.5,0,3.5) rot=(0,0,1;0rad)
  Solid = false
  Source = -> Face068
  Symmetric = false
FEATURE [Part::Feature] Face069
  shape: bbox 3.5 x 17.8 x 2e-07 mm, 1 faces, 0 solids (baked)
FEATURE [Part::Feature] Face070
  shape: bbox 3.5 x 17.8 x 2e-07 mm, 1 faces, 0 solids (baked)
FEATURE [Part::Revolution] Revolve073  label="removeToCreateScrewAndThreadedInsertHole010"
  Angle = 360
  Axis = (0,1,0)
  Base = (0,0,0)
  FaceMakerClass = Part::FaceMakerBullseye
  Placement = pos=(102.5,4.7,3.5) rot=(0,0,1;0rad)
  Solid = false
  Source = -> Face069
  Symmetric = false
FEATURE [Part::Revolution] Revolve074  label="removeToCreateScrewAndThreadedInsertHole011"
  Angle = 360
  Axis = (0,1,0)
  Base = (0,0,0)
  FaceMakerClass = Part::FaceMakerBullseye
  Placement = pos=(102.5,4.7,68.5) rot=(0,0,1;0rad)
  Solid = false
  Source = -> Face070
  Symmetric = false
FEATURE [Part::MultiFuse] Fusion048  label="makeHoles001"
  Shapes = -> [Revolve074,Revolve073,Revolve072,Revolve071,Revolve070,Revolve069]
FEATURE [Part::MultiFuse] Fusion049  label="caseScrewRetainers"
  Shapes = -> [Revolve067,Revolve068,Revolve048,Revolve047,Revolve039,Revolve040]
FEATURE [Part::Cut] Cut015  label="caseScrewRetainers001"
  Base = -> Fusion049
  Tool = -> Fusion048
FEATURE [Part::MultiFuse] Fusion050  label="casePillars"
  Shapes = -> [Revolve055,Revolve054,Revolve043,Revolve046,Revolve059,Revolve060]
FEATURE [Part::Feature] Face071 .. Face076  x6 (patterned run collapsed; names and placements below)
  shape: bbox 3.5 x 17.8 x 2e-07 mm, 1 faces, 0 solids (baked)
FEATURE [Part::Revolution] Revolve075  label="removeToCreateScrewAndThreadedInsertHole012"
  Angle = 360
  Axis = (0,1,0)
  Base = (0,0,0)
  FaceMakerClass = Part::FaceMakerBullseye
  Placement = pos=(12.5,0,10) rot=(0,0,1;0rad)
  Solid = false
  Source = -> Face071
  Symmetric = false
FEATURE [Part::Revolution] Revolve076  label="removeToCreateScrewAndThreadedInsertHole013"
  Angle = 360
  Axis = (0,1,0)
  Base = (0,0,0)
  FaceMakerClass = Part::FaceMakerBullseye
  Placement = pos=(12.5,0,62) rot=(0,0,1;0rad)
  Solid = false
  Source = -> Face072
  Symmetric = false
FEATURE [Part::Revolution] Revolve077  label="removeToCreateScrewAndThreadedInsertHole014"
  Angle = 360
  Axis = (0,1,0)
  Base = (0,0,0)
  FaceMakerClass = Part::FaceMakerBullseye
  Placement = pos=(89.5,0,68.5) rot=(0,0,1;0rad)
  Solid = false
  Source = -> Face073
  Symmetric = false
FEATURE [Part::Revolution] Revolve078  label="removeToCreateScrewAndThreadedInsertHole015"
  Angle = 360
  Axis = (0,1,0)
  Base = (0,0,0)
  FaceMakerClass = Part::FaceMakerBullseye
  Placement = pos=(89.5,0,3.5) rot=(0,0,1;0rad)
  Solid = false
  Source = -> Face074
  Symmetric = false
FEATURE [Part::Revolution] Revolve079  label="removeToCreateScrewAndThreadedInsertHole016"
  Angle = 360
  Axis = (0,1,0)
  Base = (0,0,0)
  FaceMakerClass = Part::FaceMakerBullseye
  Placement = pos=(102.5,4.7,3.5) rot=(0,0,1;0rad)
  Solid = false
  Source = -> Face075
  Symmetric = false
FEATURE [Part::Revolution] Revolve080  label="removeToCreateScrewAndThreadedInsertHole017"
  Angle = 360
  Axis = (0,1,0)
  Base = (0,0,0)
  FaceMakerClass = Part::FaceMakerBullseye
  Placement = pos=(102.5,4.7,68.5) rot=(0,0,1;0rad)
  Solid = false
  Source = -> Face076
  Symmetric = false
FEATURE [Part::MultiFuse] Fusion051  label="makeHoles002"
  Shapes = -> [Revolve080,Revolve079,Revolve078,Revolve077,Revolve076,Revolve075]
FEATURE [Part::Cut] Cut016  label="caesPillars"
  Base = -> Fusion050
  Tool = -> Fusion051
FEATURE [Part::Revolution] Revolve009  label="plugHousing016"
  Angle = 360
  Axis = (0,1,0)
  Base = (0,0,0)
  FaceMakerClass = Part::FaceMakerBullseye
  Placement = pos=(0,0,36.15) rot=(0,0,1;0rad)
  Solid = false
  Source = -> Face012
  Symmetric = false
FEATURE [Part::MultiFuse] Fusion014  label="plugHousing023"
  Placement = pos=(0,0,0) rot=(0,0,1;1.5708rad)
  Shapes = -> [Revolve011,Revolve009]
FEATURE [Part::Revolution] Revolve010  label="plugHousing017"
  Angle = 360
  Axis = (0,1,0)
  Base = (0,0,0)
  FaceMakerClass = Part::FaceMakerBullseye
  Placement = pos=(0,0,36.15) rot=(0,0,1;0rad)
  Solid = false
  Source = -> Face014
  Symmetric = false
FEATURE [Part::MultiFuse] Fusion015  label="plugHousing024"
  Placement = pos=(0,0,0) rot=(0,0,1;1.5708rad)
  Shapes = -> [Revolve010,Revolve015]
FEATURE [Part::Revolution] Revolve014  label="plugHousing026"
  Angle = 360
  Axis = (0,1,0)
  Base = (0,0,0)
  FaceMakerClass = Part::FaceMakerBullseye
  Placement = pos=(0,0,36.15) rot=(0,0,1;0rad)
  Solid = false
  Source = -> Face011
  Symmetric = false
FEATURE [Part::Revolution] Revolve013  label="plugHousing025"
  Angle = 360
  Axis = (0,1,0)
  Base = (0,0,0)
  FaceMakerClass = Part::FaceMakerBullseye
  Placement = pos=(0,0,36.15) rot=(0,0,1;0rad)
  Solid = false
  Source = -> Face015
  Symmetric = false
FEATURE [Part::MultiFuse] Fusion016  label="plugHousing028"
  Placement = pos=(0,19,0) rot=(0,0,1;3.14159rad)
  Shapes = -> [Fusion014,Fusion013]
FEATURE [Part::MultiFuse] Fusion011  label="plugHousing018"
  Placement = pos=(0,0,0) rot=(0,0,1;1.5708rad)
  Shapes = -> [Revolve014,Revolve013]
FEATURE [Part::MultiFuse] Fusion012  label="plugHousing019"
  Placement = pos=(0,19,0) rot=(0,0,1;3.14159rad)
  Shapes = -> [Fusion011,Fusion015]
FEATURE [Part::MultiFuse] Fusion017  label="plugHousing029"
  Placement = pos=(122.621,0,-0.15) rot=(0,0,1;0rad)
  Shapes = -> [Fusion016,Fusion012]
FEATURE [Part::MultiFuse] Fusion052  label="casePillarRetainers"
  Shapes = -> [Extrude012,Extrude013,Extrude014,Extrude015,Extrude016,Extrude017,Extrude018,Extrude019,Box011,Box012]
FEATURE [Part::Feature] Face077
  shape: bbox 3.5 x 17.8 x 2e-07 mm, 1 faces, 0 solids (baked)
FEATURE [Part::Revolution] Revolve081  label="removeToCreateScrewAndThreadedInsertHole018"
  Angle = 360
  Axis = (0,1,0)
  Base = (0,0,0)
  FaceMakerClass = Part::FaceMakerBullseye
  Placement = pos=(62.3,30.3,19.7) rot=(0,0,1;0rad)
  Solid = false
  Source = -> Face077
  Symmetric = false
FEATURE [Part::Feature] Face078
  shape: bbox 3.5 x 17.8 x 2e-07 mm, 1 faces, 0 solids (baked)
FEATURE [Part::Revolution] Revolve082  label="removeToCreateScrewAndThreadedInsertHole019"
  Angle = 360
  Axis = (0,1,0)
  Base = (0,0,0)
  FaceMakerClass = Part::FaceMakerBullseye
  Placement = pos=(62.3,30.3,51.7) rot=(0,0,1;0rad)
  Solid = false
  Source = -> Face078
  Symmetric = false
FEATURE [Part::Feature] Face079
  shape: bbox 3.5 x 17.8 x 2e-07 mm, 1 faces, 0 solids (baked)
FEATURE [Part::Revolution] Revolve083  label="removeToCreateScrewAndThreadedInsertHole020"
  Angle = 360
  Axis = (0,1,0)
  Base = (0,0,0)
  FaceMakerClass = Part::FaceMakerBullseye
  Placement = pos=(30.3,30.3,19.7) rot=(0,0,1;0rad)
  Solid = false
  Source = -> Face079
  Symmetric = false
FEATURE [Part::Feature] Face080
  shape: bbox 3.5 x 17.8 x 2e-07 mm, 1 faces, 0 solids (baked)
FEATURE [Part::Revolution] Revolve084  label="removeToCreateScrewAndThreadedInsertHole021"
  Angle = 360
  Axis = (0,1,0)
  Base = (0,0,0)
  FaceMakerClass = Part::FaceMakerBullseye
  Placement = pos=(30.3,30.3,51.7) rot=(0,0,1;0rad)
  Solid = false
  Source = -> Face080
  Symmetric = false
FEATURE [Part::MultiFuse] Fusion053  label="createThreadedInsertHolesForFan"
  Shapes = -> [Revolve081,Revolve082,Revolve083,Revolve084]
FEATURE [Part::Cut] Cut017  label="fanScrewHousing001"
  Base = -> Fusion046
  Tool = -> Fusion053
FEATURE [Part::Feature] Face081
  shape: bbox 3.5 x 17.8 x 2e-07 mm, 1 faces, 0 solids (baked)
FEATURE [Part::Revolution] Revolve085  label="removeToCreateScrewAndThreadedInsertHole022"
  Angle = 360
  Axis = (0,1,0)
  Base = (0,0,0)
  FaceMakerClass = Part::FaceMakerBullseye
  Placement = pos=(62.3,30.3,19.7) rot=(0,0,1;0rad)
  Solid = false
  Source = -> Face081
  Symmetric = false
FEATURE [Part::Feature] Face082
  shape: bbox 3.5 x 17.8 x 2e-07 mm, 1 faces, 0 solids (baked)
FEATURE [Part::Revolution] Revolve086  label="removeToCreateScrewAndThreadedInsertHole023"
  Angle = 360
  Axis = (0,1,0)
  Base = (0,0,0)
  FaceMakerClass = Part::FaceMakerBullseye
  Placement = pos=(62.3,30.3,51.7) rot=(0,0,1;0rad)
  Solid = false
  Source = -> Face082
  Symmetric = false
FEATURE [Part::Feature] Face083
  shape: bbox 3.5 x 17.8 x 2e-07 mm, 1 faces, 0 solids (baked)
FEATURE [Part::Revolution] Revolve087  label="removeToCreateScrewAndThreadedInsertHole024"
  Angle = 360
  Axis = (0,1,0)
  Base = (0,0,0)
  FaceMakerClass = Part::FaceMakerBullseye
  Placement = pos=(30.3,30.3,19.7) rot=(0,0,1;0rad)
  Solid = false
  Source = -> Face083
  Symmetric = false
FEATURE [Part::Feature] Face084
  shape: bbox 3.5 x 17.8 x 2e-07 mm, 1 faces, 0 solids (baked)
FEATURE [Part::Revolution] Revolve088  label="removeToCreateScrewAndThreadedInsertHole025"
  Angle = 360
  Axis = (0,1,0)
  Base = (0,0,0)
  FaceMakerClass = Part::FaceMakerBullseye
  Placement = pos=(30.3,30.3,51.7) rot=(0,0,1;0rad)
  Solid = false
  Source = -> Face084
  Symmetric = false
FEATURE [Part::MultiFuse] Fusion054  label="createThreadedInsertHolesForFan001"
  Shapes = -> [Revolve085,Revolve086,Revolve087,Revolve088]
FEATURE [Part::Cut] Cut018  label="top007"
  Base = -> Fusion040
  Tool = -> Fusion054
FEATURE [Sketcher::SketchObject] Sketch029
  FullyConstrained = false
  Placement = pos=(0,0,0) rot=(1,0,0;1.5708rad)
  sketch-geometry (24):
    g0: ArcOfCircle CenterX=-4 CenterY=-10.5 CenterZ=0 NormalX=0 NormalY=0 NormalZ=1 AngleXU=0 Radius=1.5 StartAngle=6e-16 EndAngle=3.14159
    g1: ArcOfCircle CenterX=-34.2 CenterY=-10.5 CenterZ=0 NormalX=0 NormalY=0 NormalZ=1 AngleXU=0 Radius=1.5 StartAngle=0 EndAngle=3.14159
    g2: ArcOfCircle CenterX=-34.2 CenterY=-27.7 CenterZ=0 NormalX=0 NormalY=0 NormalZ=1 AngleXU=0 Radius=1.5 StartAngle=3.14159 EndAngle=6.28319
    g3: ArcOfCircle CenterX=-4 CenterY=-27.7 CenterZ=0 NormalX=0 NormalY=0 NormalZ=1 AngleXU=0 Radius=1.5 StartAngle=3.1416 EndAngle=6.28319
    g4: ArcOfCircle CenterX=-10 CenterY=-4.3 CenterZ=0 NormalX=0 NormalY=0 NormalZ=1 AngleXU=0 Radius=1.5 StartAngle=2e-16 EndAngle=3.14159
    g5: ArcOfCircle CenterX=-16.1 CenterY=-1.8 CenterZ=0 NormalX=0 NormalY=0 NormalZ=1 AngleXU=0 Radius=1.5 StartAngle=5e-16 EndAngle=3.14159
    g6: ArcOfCircle CenterX=-22.1 CenterY=-1.8 CenterZ=0 NormalX=0 NormalY=0 NormalZ=1 AngleXU=0 Radius=1.5 StartAngle=5e-16 EndAngle=3.14159
    g7: ArcOfCircle CenterX=-28.2 CenterY=-4.3 CenterZ=0 NormalX=0 NormalY=0 NormalZ=1 AngleXU=0 Radius=1.5 StartAngle=2e-16 EndAngle=3.14159
    g8: ArcOfCircle CenterX=-10 CenterY=-33.9 CenterZ=0 NormalX=0 NormalY=0 NormalZ=1 AngleXU=0 Radius=1.5 StartAngle=3.14159 EndAngle=6.28319
    g9: ArcOfCircle CenterX=-16.1 CenterY=-36.4 CenterZ=0 NormalX=0 NormalY=0 NormalZ=1 AngleXU=0 Radius=1.5 StartAngle=3.14159 EndAngle=6.28319
    g10: ArcOfCircle CenterX=-22.1 CenterY=-36.4 CenterZ=0 NormalX=0 NormalY=0 NormalZ=1 AngleXU=0 Radius=1.5 StartAngle=3.14159 EndAngle=6.28319
    g11: ArcOfCircle CenterX=-28.2 CenterY=-33.9 CenterZ=0 NormalX=0 NormalY=0 NormalZ=1 AngleXU=0 Radius=1.5 StartAngle=3.14159 EndAngle=6.28319
    g12: LineSegment StartX=-35.7 StartY=-10.5 StartZ=0 EndX=-35.7 EndY=-27.7 EndZ=0
    g13: LineSegment StartX=-32.7 StartY=-10.5 StartZ=0 EndX=-32.7 EndY=-27.7 EndZ=0
    g14: LineSegment StartX=-29.7 StartY=-33.9 StartZ=0 EndX=-29.7 EndY=-4.3 EndZ=0
    g15: LineSegment StartX=-26.7 StartY=-33.9 StartZ=0 EndX=-26.7 EndY=-4.3 EndZ=0
    g16: LineSegment StartX=-2.5 StartY=-10.5 StartZ=0 EndX=-2.5 EndY=-27.7 EndZ=0
    g17: LineSegment StartX=-8.5 StartY=-4.3 StartZ=0 EndX=-8.5 EndY=-33.9 EndZ=0
    g18: LineSegment StartX=-5.5 StartY=-10.5 StartZ=0 EndX=-5.5 EndY=-27.7 EndZ=0
    g19: LineSegment StartX=-11.5 StartY=-4.3 StartZ=0 EndX=-11.5 EndY=-33.9 EndZ=0
    g20: LineSegment StartX=-14.6 StartY=-1.8 StartZ=0 EndX=-14.6 EndY=-36.4 EndZ=0
    g21: LineSegment StartX=-17.6 StartY=-1.8 StartZ=0 EndX=-17.6 EndY=-36.4 EndZ=0
    g22: LineSegment StartX=-20.6 StartY=-36.4 StartZ=0 EndX=-20.6 EndY=-1.8 EndZ=0
    g23: LineSegment StartX=-23.6 StartY=-1.8 StartZ=0 EndX=-23.6 EndY=-36.4 EndZ=0
  constraints (48):
    c: Block(g0)
    c: Block(g1)
    c: Block(g2)
    c: Block(g3)
    c: Block(g4)
    c: Block(g5)
    c: Block(g6)
    c: Block(g7)
    c: Block(g8)
    c: Block(g9)
    c: Block(g10)
    c: Block(g11)
    c: Coincident(g12,g1)
    c: Coincident(g12,g2)
    c: Vertical(g12)
    c: Coincident(g13,g1)
    c: Coincident(g13,g2)
    c: Vertical(g13)
    c: Coincident(g14,g11)
    c: Coincident(g14,g7)
    c: Vertical(g14)
    c: Coincident(g15,g11)
    c: Coincident(g15,g7)
    c: Vertical(g15)
    c: Coincident(g16,g0)
    c: Coincident(g16,g3)
    c: Vertical(g16)
    c: Coincident(g17,g4)
    c: Coincident(g17,g8)
    c: Vertical(g17)
    c: Coincident(g18,g0)
    c: Coincident(g18,g3)
    c: Vertical(g18)
    c: Coincident(g19,g4)
    c: Coincident(g19,g8)
    c: Vertical(g19)
    c: Coincident(g20,g5)
    c: Coincident(g20,g9)
    c: Vertical(g20)
    c: Coincident(g21,g5)
    c: Coincident(g21,g9)
    c: Vertical(g21)
    c: Coincident(g22,g10)
    c: Coincident(g22,g6)
    c: Vertical(g22)
    c: Coincident(g23,g6)
    c: Coincident(g23,g10)
    c: Vertical(g23)
FEATURE [Part::Extrusion] Extrude020  label="removeToCreateFanGrillHoles"
  Base = -> Sketch029
  Dir = (0,-1,6e-16)
  DirMode = 2
  FaceMakerClass = Part::FaceMakerBullseye
  LengthFwd = 10
  LengthRev = 0
  Placement = pos=(65.4,44,54.82) rot=(0,0,1;0rad)
  Solid = true
  Symmetric = false
FEATURE [Part::MultiFuse] Fusion055  label="top008"
  Shapes = -> [Cut017,Cut018]
FEATURE [Part::Cut] Cut019  label="top009"
  Base = -> Fusion055
  Tool = -> Extrude020
FEATURE [App::MeasureDistance] Distance003  label="Distance: 71.95 mm"
  Distance = 71.9513
  P1 = (117,38,72)
  P2 = (117,38,0.0487319)
FEATURE [Sketcher::SketchObject] Sketch030
  FullyConstrained = true
  Placement = pos=(117,19,0) rot=(0.57735,0.57735,0.57735;2.0944rad)
  sketch-geometry (48):
    g0: LineSegment StartX=-49.19 StartY=69.25 StartZ=0 EndX=-49.19 EndY=66.25 EndZ=0
    g1: LineSegment StartX=-49.19 StartY=63.5 StartZ=0 EndX=-49.19 EndY=60.5 EndZ=0
    g2: LineSegment StartX=-49.19 StartY=57.75 StartZ=0 EndX=-49.19 EndY=54.75 EndZ=0
    g3: LineSegment StartX=-49.19 StartY=52 StartZ=0 EndX=-49.19 EndY=49 EndZ=0
    g4: LineSegment StartX=-49.19 StartY=46.25 StartZ=0 EndX=-49.19 EndY=43.25 EndZ=0
    g5: LineSegment StartX=-49.19 StartY=40.5 StartZ=0 EndX=-49.19 EndY=37.5 EndZ=0
    g6: LineSegment StartX=-49.19 StartY=34.5 StartZ=0 EndX=-49.19 EndY=31.5 EndZ=0
    g7: LineSegment StartX=-49.19 StartY=28.75 StartZ=0 EndX=-49.19 EndY=25.75 EndZ=0
    g8: LineSegment StartX=-49.19 StartY=23 StartZ=0 EndX=-49.19 EndY=20 EndZ=0
    g9: LineSegment StartX=-49.19 StartY=17.25 StartZ=0 EndX=-49.19 EndY=14.25 EndZ=0
    g10: LineSegment StartX=-49.19 StartY=11.5 StartZ=0 EndX=-49.19 EndY=8.5 EndZ=0
    g11: LineSegment StartX=-49.19 StartY=5.75 StartZ=0 EndX=-49.19 EndY=2.75 EndZ=0
    g12: ArcOfCircle CenterX=-1.5 CenterY=67.75 CenterZ=0 NormalX=0 NormalY=0 NormalZ=1 AngleXU=0 Radius=1.5 StartAngle=4.71239 EndAngle=7.85398
    g13: ArcOfCircle CenterX=-1.5 CenterY=62 CenterZ=0 NormalX=0 NormalY=0 NormalZ=1 AngleXU=0 Radius=1.5 StartAngle=4.71239 EndAngle=7.85398
    g14: ArcOfCircle CenterX=-1.5 CenterY=56.25 CenterZ=0 NormalX=0 NormalY=0 NormalZ=1 AngleXU=0 Radius=1.5 StartAngle=4.71239 EndAngle=7.85398
    g15: ArcOfCircle CenterX=-11.49 CenterY=50.5 CenterZ=0 NormalX=0 NormalY=0 NormalZ=1 AngleXU=0 Radius=1.5 StartAngle=4.71239 EndAngle=7.85398
    g16: ArcOfCircle CenterX=-16.28 CenterY=44.75 CenterZ=0 NormalX=0 NormalY=0 NormalZ=1 AngleXU=0 Radius=1.5 StartAngle=4.71239 EndAngle=7.85398
    g17: ArcOfCircle CenterX=-18.2337 CenterY=39 CenterZ=0 NormalX=0 NormalY=0 NormalZ=1 AngleXU=0 Radius=1.5 StartAngle=4.71485 EndAngle=7.85398
    g18: ArcOfCircle CenterX=-16.2837 CenterY=27.25 CenterZ=0 NormalX=0 NormalY=0 NormalZ=1 AngleXU=0 Radius=1.5 StartAngle=4.71485 EndAngle=7.85398
    g19: ArcOfCircle CenterX=-18.2337 CenterY=33 CenterZ=0 NormalX=0 NormalY=0 NormalZ=1 AngleXU=0 Radius=1.5 StartAngle=4.71485 EndAngle=7.85398
    g20: ArcOfCircle CenterX=-11.49 CenterY=21.5 CenterZ=0 NormalX=0 NormalY=0 NormalZ=1 AngleXU=0 Radius=1.5 StartAngle=4.71239 EndAngle=7.85398
    g21: ArcOfCircle CenterX=-1.5 CenterY=4.25 CenterZ=0 NormalX=0 NormalY=0 NormalZ=1 AngleXU=0 Radius=1.5 StartAngle=4.71239 EndAngle=7.85398
    g22: ArcOfCircle CenterX=-1.5 CenterY=10 CenterZ=0 NormalX=0 NormalY=0 NormalZ=1 AngleXU=0 Radius=1.5 StartAngle=4.71239 EndAngle=7.85398
    g23: ArcOfCircle CenterX=-1.5 CenterY=15.75 CenterZ=0 NormalX=0 NormalY=0 NormalZ=1 AngleXU=0 Radius=1.5 StartAngle=4.71239 EndAngle=7.85398
    g24: LineSegment StartX=-49.19 StartY=69.25 StartZ=0 EndX=-1.5 EndY=69.25 EndZ=0
    g25: LineSegment StartX=-49.19 StartY=66.25 StartZ=0 EndX=-1.5 EndY=66.25 EndZ=0
    g26: LineSegment StartX=-49.19 StartY=63.5 StartZ=0 EndX=-1.5 EndY=63.5 EndZ=0
    g27: LineSegment StartX=-49.19 StartY=60.5 StartZ=0 EndX=-1.5 EndY=60.5 EndZ=0
    g28: LineSegment StartX=-49.19 StartY=57.75 StartZ=0 EndX=-1.5 EndY=57.75 EndZ=0
    g29: LineSegment StartX=-49.19 StartY=54.75 StartZ=0 EndX=-1.5 EndY=54.75 EndZ=0
    g30: LineSegment StartX=-49.19 StartY=52 StartZ=0 EndX=-11.49 EndY=52 EndZ=0
    g31: LineSegment StartX=-49.19 StartY=49 StartZ=0 EndX=-11.49 EndY=49 EndZ=0
    g32: LineSegment StartX=-49.19 StartY=46.25 StartZ=0 EndX=-16.28 EndY=46.25 EndZ=0
    g33: LineSegment StartX=-49.19 StartY=43.25 StartZ=0 EndX=-16.28 EndY=43.25 EndZ=0
    g34: LineSegment StartX=-49.19 StartY=40.5 StartZ=0 EndX=-18.2337 EndY=40.5 EndZ=0
    g35: LineSegment StartX=-49.19 StartY=37.5 StartZ=0 EndX=-18.23 EndY=37.5 EndZ=0
    g36: LineSegment StartX=-49.19 StartY=34.5 StartZ=0 EndX=-18.2337 EndY=34.5 EndZ=0
    g37: LineSegment StartX=-49.19 StartY=31.5 StartZ=0 EndX=-18.23 EndY=31.5 EndZ=0
    g38: LineSegment StartX=-49.19 StartY=28.75 StartZ=0 EndX=-16.2837 EndY=28.75 EndZ=0
    g39: LineSegment StartX=-49.19 StartY=25.75 StartZ=0 EndX=-16.28 EndY=25.75 EndZ=0
    g40: LineSegment StartX=-49.19 StartY=23 StartZ=0 EndX=-11.49 EndY=23 EndZ=0
    g41: LineSegment StartX=-49.19 StartY=20 StartZ=0 EndX=-11.49 EndY=20 EndZ=0
    g42: LineSegment StartX=-49.19 StartY=17.25 StartZ=0 EndX=-1.5 EndY=17.25 EndZ=0
    g43: LineSegment StartX=-49.19 StartY=14.25 StartZ=0 EndX=-1.5 EndY=14.25 EndZ=0
    g44: LineSegment StartX=-49.19 StartY=11.5 StartZ=0 EndX=-1.5 EndY=11.5 EndZ=0
    g45: LineSegment StartX=-49.19 StartY=8.5 StartZ=0 EndX=-1.5 EndY=8.5 EndZ=0
    g46: LineSegment StartX=-49.19 StartY=5.75 StartZ=0 EndX=-1.5 EndY=5.75 EndZ=0
    g47: LineSegment StartX=-49.19 StartY=2.75 StartZ=0 EndX=-1.5 EndY=2.75 EndZ=0
  constraints (120):
    c: Vertical(g0)
    c: Distance(g0) = 3
    c: Block(g0)
    c: Vertical(g1)
    c: Distance(g1) = 3
    c: Vertical(g2)
    c: Equal(g0,g2) = 3
    c: Block(g2)
    c: Vertical(g3)
    c: Equal(g1,g3) = 3
    c: Vertical(g4)
    c: Equal(g0,g4) = 3
    c: Block(g4)
    c: Vertical(g5)
    c: Equal(g1,g5) = 3
    c: Vertical(g6)
    c: Equal(g0,g6) = 3
    c: Block(g6)
    c: Vertical(g7)
    c: Equal(g1,g7) = 3
    c: Vertical(g8)
    c: Equal(g0,g8) = 3
    c: Block(g8)
    c: Vertical(g9)
    c: Equal(g1,g9) = 3
    c: Vertical(g10)
    c: Equal(g0,g10) = 3
    c: Block(g10)
    c: Vertical(g11)
    c: Equal(g1,g11) = 3
    c: Block(g12)
    c: Block(g13)
    c: Block(g14)
    c: Block(g15)
    c: Block(g16)
    c: Block(g17)
    c: Block(g18)
    c: Block(g19)
    c: Block(g20)
    c: Block(g21)
    c: Block(g22)
    c: Block(g23)
    c: Block(g11)
    c: Block(g9)
    c: Block(g7)
    c: Block(g5)
    c: Block(g3)
    c: Block(g1)
    c: Coincident(g24,g0)
    c: Coincident(g24,g12)
    c: Horizontal(g24)
    c: Coincident(g25,g0)
    c: Coincident(g25,g12)
    c: Horizontal(g25)
    c: Coincident(g26,g1)
    c: Coincident(g26,g13)
    c: Horizontal(g26)
    c: Coincident(g27,g1)
    c: Coincident(g27,g13)
    c: Horizontal(g27)
    c: Coincident(g28,g2)
    c: Coincident(g28,g14)
    c: Horizontal(g28)
    c: Coincident(g29,g2)
    c: Coincident(g29,g14)
    c: Horizontal(g29)
    c: Coincident(g30,g3)
    c: Coincident(g30,g15)
    c: Horizontal(g30)
    c: Coincident(g31,g3)
    c: Coincident(g31,g15)
    c: Horizontal(g31)
    c: Coincident(g32,g4)
    c: Coincident(g32,g16)
    c: Horizontal(g32)
    c: Coincident(g33,g4)
    c: Coincident(g33,g16)
    c: Horizontal(g33)
    c: Coincident(g34,g5)
    c: Coincident(g34,g17)
    c: Horizontal(g34)
    c: Coincident(g35,g5)
    c: Coincident(g35,g17)
    c: Horizontal(g35)
    c: Coincident(g36,g6)
    c: Coincident(g36,g19)
    c: Horizontal(g36)
    c: Coincident(g37,g6)
    c: Coincident(g37,g19)
    c: Horizontal(g37)
    c: Coincident(g38,g7)
    c: Coincident(g38,g18)
    c: Horizontal(g38)
    c: Coincident(g39,g7)
    c: Coincident(g39,g18)
    c: Horizontal(g39)
    c: Coincident(g40,g8)
    c: Coincident(g40,g20)
    c: Horizontal(g40)
    c: Coincident(g41,g8)
    c: Coincident(g41,g20)
    c: Horizontal(g41)
    c: Coincident(g42,g9)
    c: Coincident(g42,g23)
    c: Horizontal(g42)
    c: Coincident(g43,g9)
    c: Coincident(g43,g23)
    c: Horizontal(g43)
    c: Coincident(g44,g10)
    c: Coincident(g44,g22)
    c: Horizontal(g44)
    c: Coincident(g45,g10)
    c: Coincident(g45,g22)
    c: Horizontal(g45)
    c: Coincident(g46,g11)
    c: Coincident(g46,g21)
    c: Horizontal(g46)
    c: Coincident(g47,g11)
    c: Coincident(g47,g21)
    c: Horizontal(g47)
FEATURE [Sketcher::SketchObject] Sketch031
  FullyConstrained = true
  Placement = pos=(117,19,0) rot=(0.57735,0.57735,0.57735;2.0944rad)
  sketch-geometry (24):
    g0: ArcOfCircle CenterX=-49.19 CenterY=67.75 CenterZ=0 NormalX=0 NormalY=0 NormalZ=1 AngleXU=0 Radius=1.5 StartAngle=1.5708 EndAngle=4.71239
    g1: ArcOfCircle CenterX=-49.19 CenterY=62 CenterZ=0 NormalX=0 NormalY=0 NormalZ=1 AngleXU=0 Radius=1.5 StartAngle=1.5708 EndAngle=4.71239
    g2: ArcOfCircle CenterX=-49.19 CenterY=56.25 CenterZ=0 NormalX=0 NormalY=0 NormalZ=1 AngleXU=0 Radius=1.5 StartAngle=1.5708 EndAngle=4.71239
    g3: ArcOfCircle CenterX=-49.19 CenterY=50.5 CenterZ=0 NormalX=0 NormalY=0 NormalZ=1 AngleXU=0 Radius=1.5 StartAngle=1.5708 EndAngle=4.71239
    g4: ArcOfCircle CenterX=-49.19 CenterY=44.75 CenterZ=0 NormalX=0 NormalY=0 NormalZ=1 AngleXU=0 Radius=1.5 StartAngle=1.5708 EndAngle=4.71239
    g5: ArcOfCircle CenterX=-49.19 CenterY=39 CenterZ=0 NormalX=0 NormalY=0 NormalZ=1 AngleXU=0 Radius=1.5 StartAngle=1.5708 EndAngle=4.71239
    g6: ArcOfCircle CenterX=-49.19 CenterY=33 CenterZ=0 NormalX=0 NormalY=0 NormalZ=1 AngleXU=0 Radius=1.5 StartAngle=1.5708 EndAngle=4.71239
    g7: ArcOfCircle CenterX=-49.19 CenterY=27.25 CenterZ=0 NormalX=0 NormalY=0 NormalZ=1 AngleXU=0 Radius=1.5 StartAngle=1.5708 EndAngle=4.71239
    g8: ArcOfCircle CenterX=-49.19 CenterY=21.5 CenterZ=0 NormalX=0 NormalY=0 NormalZ=1 AngleXU=0 Radius=1.5 StartAngle=1.5708 EndAngle=4.71239
    g9: ArcOfCircle CenterX=-49.19 CenterY=15.75 CenterZ=0 NormalX=0 NormalY=0 NormalZ=1 AngleXU=0 Radius=1.5 StartAngle=1.5708 EndAngle=4.71239
    g10: ArcOfCircle CenterX=-49.19 CenterY=10 CenterZ=0 NormalX=0 NormalY=0 NormalZ=1 AngleXU=0 Radius=1.5 StartAngle=1.5708 EndAngle=4.71239
    g11: ArcOfCircle CenterX=-49.19 CenterY=4.25 CenterZ=0 NormalX=0 NormalY=0 NormalZ=1 AngleXU=0 Radius=1.5 StartAngle=1.5708 EndAngle=4.71239
    g12: LineSegment StartX=-49.19 StartY=69.25 StartZ=0 EndX=-49.19 EndY=66.25 EndZ=0
    g13: LineSegment StartX=-49.19 StartY=63.5 StartZ=0 EndX=-49.19 EndY=60.5 EndZ=0
    g14: LineSegment StartX=-49.19 StartY=57.75 StartZ=0 EndX=-49.19 EndY=54.75 EndZ=0
    g15: LineSegment StartX=-49.19 StartY=52 StartZ=0 EndX=-49.19 EndY=49 EndZ=0
    g16: LineSegment StartX=-49.19 StartY=46.25 StartZ=0 EndX=-49.19 EndY=43.25 EndZ=0
    g17: LineSegment StartX=-49.19 StartY=40.5 StartZ=0 EndX=-49.19 EndY=37.5 EndZ=0
    g18: LineSegment StartX=-49.19 StartY=34.5 StartZ=0 EndX=-49.19 EndY=31.5 EndZ=0
    g19: LineSegment StartX=-49.19 StartY=28.75 StartZ=0 EndX=-49.19 EndY=25.75 EndZ=0
    g20: LineSegment StartX=-49.19 StartY=23 StartZ=0 EndX=-49.19 EndY=20 EndZ=0
    g21: LineSegment StartX=-49.19 StartY=17.25 StartZ=0 EndX=-49.19 EndY=14.25 EndZ=0
    g22: LineSegment StartX=-49.19 StartY=11.5 StartZ=0 EndX=-49.19 EndY=8.5 EndZ=0
    g23: LineSegment StartX=-49.19 StartY=5.75 StartZ=0 EndX=-49.19 EndY=2.75 EndZ=0
  constraints (48):
    c: Block(g0)
    c: Block(g1)
    c: Block(g2)
    c: Block(g3)
    c: Block(g4)
    c: Block(g5)
    c: Block(g6)
    c: Block(g7)
    c: Block(g8)
    c: Block(g9)
    c: Block(g10)
    c: Block(g11)
    c: Coincident(g12,g0)
    c: Coincident(g12,g0)
    c: Vertical(g12)
    c: Vertical(g13)
    c: Coincident(g13,g1)
    c: Vertical(g14)
    c: Coincident(g14,g2)
    c: Vertical(g15)
    c: Coincident(g15,g3)
    c: Vertical(g16)
    c: Coincident(g16,g4)
    c: Vertical(g17)
    c: Coincident(g17,g5)
    c: Vertical(g18)
    c: Coincident(g18,g6)
    c: Vertical(g19)
    c: Coincident(g19,g7)
    c: Vertical(g20)
    c: Coincident(g20,g8)
    c: Vertical(g21)
    c: Coincident(g21,g9)
    c: Vertical(g22)
    c: Coincident(g22,g10)
    c: Vertical(g23)
    c: Coincident(g23,g11)
    c: Block(g23)
    c: Block(g22)
    c: Block(g21)
    c: Block(g20)
    c: Block(g13)
    c: Block(g14)
    c: Block(g15)
    c: Block(g16)
    c: Block(g17)
    c: Block(g18)
    c: Block(g19)
FEATURE [Part::Extrusion] Extrude022
  Base = -> Sketch030
  Dir = (1,-2e-16,2e-16)
  DirMode = 2
  FaceMakerClass = Part::FaceMakerBullseye
  LengthFwd = 19
  LengthRev = 0
  Placement = pos=(-19,0,0) rot=(0,0,1;0rad)
  Solid = true
  Symmetric = false
FEATURE [Part::Fillet] Fillet022
  Base = -> Extrude022
  Edges = 24 edges r=1.49: [Edge6,Edge11,Edge18,Edge23,Edge30,Edge35,Edge42,Edge47,Edge54,Edge59,Edge66,Edge71,Edge78,Edge83,Edge90,Edge95,Edge102,Edge107,Edge114,Edge119,Edge126,Edge131,Edge138,Edge143]
FEATURE [Part::Cut] Cut020  label="top010"
  Base = -> Cut019
  Tool = -> Fillet022
FEATURE [Sketcher::SketchObject] Sketch032
  FullyConstrained = true
  Placement = pos=(117,19,0) rot=(0.57735,0.57735,0.57735;2.0944rad)
  sketch-geometry (48):
    g0: LineSegment StartX=-49.19 StartY=69.25 StartZ=0 EndX=-49.19 EndY=66.25 EndZ=0
    g1: LineSegment StartX=-49.19 StartY=63.5 StartZ=0 EndX=-49.19 EndY=60.5 EndZ=0
    g2: LineSegment StartX=-49.19 StartY=57.75 StartZ=0 EndX=-49.19 EndY=54.75 EndZ=0
    g3: LineSegment StartX=-49.19 StartY=52 StartZ=0 EndX=-49.19 EndY=49 EndZ=0
    g4: LineSegment StartX=-49.19 StartY=46.25 StartZ=0 EndX=-49.19 EndY=43.25 EndZ=0
    g5: LineSegment StartX=-49.19 StartY=40.5 StartZ=0 EndX=-49.19 EndY=37.5 EndZ=0
    g6: LineSegment StartX=-49.19 StartY=34.5 StartZ=0 EndX=-49.19 EndY=31.5 EndZ=0
    g7: LineSegment StartX=-49.19 StartY=28.75 StartZ=0 EndX=-49.19 EndY=25.75 EndZ=0
    g8: LineSegment StartX=-49.19 StartY=23 StartZ=0 EndX=-49.19 EndY=20 EndZ=0
    g9: LineSegment StartX=-49.19 StartY=17.25 StartZ=0 EndX=-49.19 EndY=14.25 EndZ=0
    g10: LineSegment StartX=-49.19 StartY=11.5 StartZ=0 EndX=-49.19 EndY=8.5 EndZ=0
    g11: LineSegment StartX=-49.19 StartY=5.75 StartZ=0 EndX=-49.19 EndY=2.75 EndZ=0
    g12: ArcOfCircle CenterX=-1.5 CenterY=67.75 CenterZ=0 NormalX=0 NormalY=0 NormalZ=1 AngleXU=0 Radius=1.5 StartAngle=4.71239 EndAngle=7.85398
    g13: ArcOfCircle CenterX=-1.5 CenterY=62 CenterZ=0 NormalX=0 NormalY=0 NormalZ=1 AngleXU=0 Radius=1.5 StartAngle=4.71239 EndAngle=7.85398
    g14: ArcOfCircle CenterX=-1.5 CenterY=56.25 CenterZ=0 NormalX=0 NormalY=0 NormalZ=1 AngleXU=0 Radius=1.5 StartAngle=4.71239 EndAngle=7.85398
    g15: ArcOfCircle CenterX=-11.49 CenterY=50.5 CenterZ=0 NormalX=0 NormalY=0 NormalZ=1 AngleXU=0 Radius=1.5 StartAngle=4.71239 EndAngle=7.85398
    g16: ArcOfCircle CenterX=-16.28 CenterY=44.75 CenterZ=0 NormalX=0 NormalY=0 NormalZ=1 AngleXU=0 Radius=1.5 StartAngle=4.71239 EndAngle=7.85398
    g17: ArcOfCircle CenterX=-18.2337 CenterY=39 CenterZ=0 NormalX=0 NormalY=0 NormalZ=1 AngleXU=0 Radius=1.5 StartAngle=4.71485 EndAngle=7.85398
    g18: ArcOfCircle CenterX=-16.2837 CenterY=27.25 CenterZ=0 NormalX=0 NormalY=0 NormalZ=1 AngleXU=0 Radius=1.5 StartAngle=4.71485 EndAngle=7.85398
    g19: ArcOfCircle CenterX=-18.2337 CenterY=33 CenterZ=0 NormalX=0 NormalY=0 NormalZ=1 AngleXU=0 Radius=1.5 StartAngle=4.71485 EndAngle=7.85398
    g20: ArcOfCircle CenterX=-11.49 CenterY=21.5 CenterZ=0 NormalX=0 NormalY=0 NormalZ=1 AngleXU=0 Radius=1.5 StartAngle=4.71239 EndAngle=7.85398
    g21: ArcOfCircle CenterX=-1.5 CenterY=4.25 CenterZ=0 NormalX=0 NormalY=0 NormalZ=1 AngleXU=0 Radius=1.5 StartAngle=4.71239 EndAngle=7.85398
    g22: ArcOfCircle CenterX=-1.5 CenterY=10 CenterZ=0 NormalX=0 NormalY=0 NormalZ=1 AngleXU=0 Radius=1.5 StartAngle=4.71239 EndAngle=7.85398
    g23: ArcOfCircle CenterX=-1.5 CenterY=15.75 CenterZ=0 NormalX=0 NormalY=0 NormalZ=1 AngleXU=0 Radius=1.5 StartAngle=4.71239 EndAngle=7.85398
    g24: LineSegment StartX=-49.19 StartY=69.25 StartZ=0 EndX=-1.5 EndY=69.25 EndZ=0
    g25: LineSegment StartX=-49.19 StartY=66.25 StartZ=0 EndX=-1.5 EndY=66.25 EndZ=0
    g26: LineSegment StartX=-49.19 StartY=63.5 StartZ=0 EndX=-1.5 EndY=63.5 EndZ=0
    g27: LineSegment StartX=-49.19 StartY=60.5 StartZ=0 EndX=-1.5 EndY=60.5 EndZ=0
    g28: LineSegment StartX=-49.19 StartY=57.75 StartZ=0 EndX=-1.5 EndY=57.75 EndZ=0
    g29: LineSegment StartX=-49.19 StartY=54.75 StartZ=0 EndX=-1.5 EndY=54.75 EndZ=0
    g30: LineSegment StartX=-49.19 StartY=52 StartZ=0 EndX=-11.49 EndY=52 EndZ=0
    g31: LineSegment StartX=-49.19 StartY=49 StartZ=0 EndX=-11.49 EndY=49 EndZ=0
    g32: LineSegment StartX=-49.19 StartY=46.25 StartZ=0 EndX=-16.28 EndY=46.25 EndZ=0
    g33: LineSegment StartX=-49.19 StartY=43.25 StartZ=0 EndX=-16.28 EndY=43.25 EndZ=0
    g34: LineSegment StartX=-49.19 StartY=40.5 StartZ=0 EndX=-18.2337 EndY=40.5 EndZ=0
    g35: LineSegment StartX=-49.19 StartY=37.5 StartZ=0 EndX=-18.23 EndY=37.5 EndZ=0
    g36: LineSegment StartX=-49.19 StartY=34.5 StartZ=0 EndX=-18.2337 EndY=34.5 EndZ=0
    g37: LineSegment StartX=-49.19 StartY=31.5 StartZ=0 EndX=-18.23 EndY=31.5 EndZ=0
    g38: LineSegment StartX=-49.19 StartY=28.75 StartZ=0 EndX=-16.2837 EndY=28.75 EndZ=0
    g39: LineSegment StartX=-49.19 StartY=25.75 StartZ=0 EndX=-16.28 EndY=25.75 EndZ=0
    g40: LineSegment StartX=-49.19 StartY=23 StartZ=0 EndX=-11.49 EndY=23 EndZ=0
    g41: LineSegment StartX=-49.19 StartY=20 StartZ=0 EndX=-11.49 EndY=20 EndZ=0
    g42: LineSegment StartX=-49.19 StartY=17.25 StartZ=0 EndX=-1.5 EndY=17.25 EndZ=0
    g43: LineSegment StartX=-49.19 StartY=14.25 StartZ=0 EndX=-1.5 EndY=14.25 EndZ=0
    g44: LineSegment StartX=-49.19 StartY=11.5 StartZ=0 EndX=-1.5 EndY=11.5 EndZ=0
    g45: LineSegment StartX=-49.19 StartY=8.5 StartZ=0 EndX=-1.5 EndY=8.5 EndZ=0
    g46: LineSegment StartX=-49.19 StartY=5.75 StartZ=0 EndX=-1.5 EndY=5.75 EndZ=0
    g47: LineSegment StartX=-49.19 StartY=2.75 StartZ=0 EndX=-1.5 EndY=2.75 EndZ=0
  constraints (120):
    c: Vertical(g0)
    c: Distance(g0) = 3
    c: Block(g0)
    c: Vertical(g1)
    c: Distance(g1) = 3
    c: Vertical(g2)
    c: Equal(g0,g2) = 3
    c: Block(g2)
    c: Vertical(g3)
    c: Equal(g1,g3) = 3
    c: Vertical(g4)
    c: Equal(g0,g4) = 3
    c: Block(g4)
    c: Vertical(g5)
    c: Equal(g1,g5) = 3
    c: Vertical(g6)
    c: Equal(g0,g6) = 3
    c: Block(g6)
    c: Vertical(g7)
    c: Equal(g1,g7) = 3
    c: Vertical(g8)
    c: Equal(g0,g8) = 3
    c: Block(g8)
    c: Vertical(g9)
    c: Equal(g1,g9) = 3
    c: Vertical(g10)
    c: Equal(g0,g10) = 3
    c: Block(g10)
    c: Vertical(g11)
    c: Equal(g1,g11) = 3
    c: Block(g12)
    c: Block(g13)
    c: Block(g14)
    c: Block(g15)
    c: Block(g16)
    c: Block(g17)
    c: Block(g18)
    c: Block(g19)
    c: Block(g20)
    c: Block(g21)
    c: Block(g22)
    c: Block(g23)
    c: Block(g11)
    c: Block(g9)
    c: Block(g7)
    c: Block(g5)
    c: Block(g3)
    c: Block(g1)
    c: Coincident(g24,g0)
    c: Coincident(g24,g12)
    c: Horizontal(g24)
    c: Coincident(g25,g0)
    c: Coincident(g25,g12)
    c: Horizontal(g25)
    c: Coincident(g26,g1)
    c: Coincident(g26,g13)
    c: Horizontal(g26)
    c: Coincident(g27,g1)
    c: Coincident(g27,g13)
    c: Horizontal(g27)
    c: Coincident(g28,g2)
    c: Coincident(g28,g14)
    c: Horizontal(g28)
    c: Coincident(g29,g2)
    c: Coincident(g29,g14)
    c: Horizontal(g29)
    c: Coincident(g30,g3)
    c: Coincident(g30,g15)
    c: Horizontal(g30)
    c: Coincident(g31,g3)
    c: Coincident(g31,g15)
    c: Horizontal(g31)
    c: Coincident(g32,g4)
    c: Coincident(g32,g16)
    c: Horizontal(g32)
    c: Coincident(g33,g4)
    c: Coincident(g33,g16)
    c: Horizontal(g33)
    c: Coincident(g34,g5)
    c: Coincident(g34,g17)
    c: Horizontal(g34)
    c: Coincident(g35,g5)
    c: Coincident(g35,g17)
    c: Horizontal(g35)
    c: Coincident(g36,g6)
    c: Coincident(g36,g19)
    c: Horizontal(g36)
    c: Coincident(g37,g6)
    c: Coincident(g37,g19)
    c: Horizontal(g37)
    c: Coincident(g38,g7)
    c: Coincident(g38,g18)
    c: Horizontal(g38)
    c: Coincident(g39,g7)
    c: Coincident(g39,g18)
    c: Horizontal(g39)
    c: Coincident(g40,g8)
    c: Coincident(g40,g20)
    c: Horizontal(g40)
    c: Coincident(g41,g8)
    c: Coincident(g41,g20)
    c: Horizontal(g41)
    c: Coincident(g42,g9)
    c: Coincident(g42,g23)
    c: Horizontal(g42)
    c: Coincident(g43,g9)
    c: Coincident(g43,g23)
    c: Horizontal(g43)
    c: Coincident(g44,g10)
    c: Coincident(g44,g22)
    c: Horizontal(g44)
    c: Coincident(g45,g10)
    c: Coincident(g45,g22)
    c: Horizontal(g45)
    c: Coincident(g46,g11)
    c: Coincident(g46,g21)
    c: Horizontal(g46)
    c: Coincident(g47,g11)
    c: Coincident(g47,g21)
    c: Horizontal(g47)
FEATURE [Part::Extrusion] Extrude023
  Base = -> Sketch032
  Dir = (1,-2e-16,2e-16)
  DirMode = 2
  FaceMakerClass = Part::FaceMakerBullseye
  LengthFwd = 19
  LengthRev = 0
  Placement = pos=(-19,0,0) rot=(0,0,1;0rad)
  Solid = true
  Symmetric = false
FEATURE [Part::Fillet] Fillet023
  Base = -> Extrude023
  Edges = <same value as first occurrence — deduplicated (x6 in doc)>
  Placement = pos=(0,0.05,0) rot=(0,0,1;0rad)
FEATURE [Part::Cut] Cut014  label="bottom003"
  Base = -> Cut007
  Tool = -> Fusion047
FEATURE [Part::Cut] Cut021  label="bottom004"
  Base = -> Cut014
  Tool = -> Fillet023
FEATURE [Sketcher::SketchObject] Sketch033
  FullyConstrained = true
  Placement = pos=(117,19,0) rot=(0.57735,0.57735,0.57735;2.0944rad)
  sketch-geometry (8):
    g0: LineSegment StartX=-49.19 StartY=69.25 StartZ=0 EndX=-49.19 EndY=66.25 EndZ=0
    g1: LineSegment StartX=-49.19 StartY=5.75 StartZ=0 EndX=-49.19 EndY=2.75 EndZ=0
    g2: ArcOfCircle CenterX=-1.5 CenterY=67.75 CenterZ=0 NormalX=0 NormalY=0 NormalZ=1 AngleXU=0 Radius=1.5 StartAngle=4.71239 EndAngle=7.85398
    g3: ArcOfCircle CenterX=-1.5 CenterY=4.25 CenterZ=0 NormalX=0 NormalY=0 NormalZ=1 AngleXU=0 Radius=1.5 StartAngle=4.71239 EndAngle=7.85398
    g4: LineSegment StartX=-49.19 StartY=69.25 StartZ=0 EndX=-1.5 EndY=69.25 EndZ=0
    g5: LineSegment StartX=-49.19 StartY=66.25 StartZ=0 EndX=-1.5 EndY=66.25 EndZ=0
    g6: LineSegment StartX=-49.19 StartY=5.75 StartZ=0 EndX=-1.5 EndY=5.75 EndZ=0
    g7: LineSegment StartX=-49.19 StartY=2.75 StartZ=0 EndX=-1.5 EndY=2.75 EndZ=0
  constraints (19):
    c: Vertical(g0)
    c: Distance(g0) = 3
    c: Block(g0)
    c: Vertical(g1)
    c: Block(g2)
    c: Block(g3)
    c: Block(g1)
    c: Coincident(g4,g0)
    c: Coincident(g4,g2)
    c: Horizontal(g4)
    c: Coincident(g5,g0)
    c: Coincident(g5,g2)
    c: Horizontal(g5)
    c: Coincident(g6,g1)
    c: Coincident(g6,g3)
    c: Horizontal(g6)
    c: Coincident(g7,g1)
    c: Coincident(g7,g3)
    c: Horizontal(g7)
FEATURE [Sketcher::SketchObject] Sketch034
  FullyConstrained = true
  Placement = pos=(117,19,0) rot=(0.57735,0.57735,0.57735;2.0944rad)
  sketch-geometry (8):
    g0: LineSegment StartX=-49.19 StartY=63.5 StartZ=0 EndX=-49.19 EndY=60.5 EndZ=0
    g1: LineSegment StartX=-49.19 StartY=11.5 StartZ=0 EndX=-49.19 EndY=8.5 EndZ=0
    g2: ArcOfCircle CenterX=-1.5 CenterY=62 CenterZ=0 NormalX=0 NormalY=0 NormalZ=1 AngleXU=0 Radius=1.5 StartAngle=4.71239 EndAngle=7.85398
    g3: ArcOfCircle CenterX=-1.5 CenterY=10 CenterZ=0 NormalX=0 NormalY=0 NormalZ=1 AngleXU=0 Radius=1.5 StartAngle=4.71239 EndAngle=7.85398
    g4: LineSegment StartX=-49.19 StartY=63.5 StartZ=0 EndX=-1.5 EndY=63.5 EndZ=0
    g5: LineSegment StartX=-49.19 StartY=60.5 StartZ=0 EndX=-1.5 EndY=60.5 EndZ=0
    g6: LineSegment StartX=-49.19 StartY=11.5 StartZ=0 EndX=-1.5 EndY=11.5 EndZ=0
    g7: LineSegment StartX=-49.19 StartY=8.5 StartZ=0 EndX=-1.5 EndY=8.5 EndZ=0
  constraints (19):
    c: Vertical(g0)
    c: Distance(g0) = 3
    c: Vertical(g1)
    c: Block(g1)
    c: Block(g2)
    c: Block(g3)
    c: Block(g0)
    c: Coincident(g4,g0)
    c: Coincident(g4,g2)
    c: Horizontal(g4)
    c: Coincident(g5,g0)
    c: Coincident(g5,g2)
    c: Horizontal(g5)
    c: Coincident(g6,g1)
    c: Coincident(g6,g3)
    c: Horizontal(g6)
    c: Coincident(g7,g1)
    c: Coincident(g7,g3)
    c: Horizontal(g7)
FEATURE [Part::Extrusion] Extrude024
  Base = -> Sketch033
  Dir = (1,0,0)
  DirMode = 2
  FaceMakerClass = Part::FaceMakerBullseye
  LengthFwd = 10
  LengthRev = 0
  Solid = true
  Symmetric = false
FEATURE [Part::Extrusion] Extrude025
  Base = -> Sketch034
  Dir = (1,0,0)
  DirMode = 2
  FaceMakerClass = Part::FaceMakerBullseye
  LengthFwd = 10
  LengthRev = 0
  Solid = true
  Symmetric = false
FEATURE [Part::Fillet] Fillet024  label="removeFromtMoreFrontCaseScrewRetainers"
  Base = -> Extrude024
  Edges = 4 edges r=1.49: [Edge6,Edge11,Edge18,Edge23]
  Placement = pos=(-11,0,0) rot=(0,0,1;0rad)
FEATURE [Part::Fillet] Fillet025  label="removeFromtMoreFrontCaseScrewRetainers001"
  Base = -> Extrude025
  Edges = 4 edges r=1.49: [Edge6,Edge11,Edge18,Edge23]
  Placement = pos=(-19,0,0) rot=(0,0,1;0rad)
FEATURE [Part::Cut] Cut022
  Base = -> Cut015
  Tool = -> Fillet025
FEATURE [Part::Cut] Cut023  label="screwRetainers"
  Base = -> Cut022
  Tool = -> Fillet024
FEATURE [Part::MultiFuse] Fusion056  label="bottom005"
  Shapes = -> [Fusion044,Cut021]
FEATURE [Part::MultiFuse] Fusion057  label="casePillars001"
  Shapes = -> [Cut016,Fusion052]
FEATURE [Part::MultiFuse] Fusion058  label="bottom006"
  Shapes = -> [Fusion056,Cut023]
FEATURE [Part::MultiFuse] Fusion059  label="bottom007"
  Shapes = -> [Fusion058,Fillet005]
FEATURE [Part::MultiFuse] Fusion060  label="bottom008"
  Shapes = -> [Fusion059,Fusion]
FEATURE [Part::MultiFuse] Fusion061  label="top011"
  Shapes = -> [Cut006,Cut020]
FEATURE [Part::MultiFuse] Fusion062  label="top012"
  Shapes = -> [Fusion057,Fusion061]
FEATURE [Sketcher::SketchObject] Sketch035  label="topSketch007"
  FullyConstrained = true
  sketch-geometry (6):
    g0: LineSegment StartX=19 StartY=38 StartZ=0 EndX=117 EndY=38 EndZ=0
    g1: ArcOfCircle CenterX=19 CenterY=19 CenterZ=0 NormalX=0 NormalY=0 NormalZ=1 AngleXU=0 Radius=19 StartAngle=1.5708 EndAngle=3.14159
    g2: LineSegment StartX=117 StartY=38 StartZ=0 EndX=117 EndY=19 EndZ=0
    g3: LineSegment StartX=98 StartY=1.0161e-12 StartZ=0 EndX=5.22862e-06 EndY=1.0161e-12 EndZ=0
    g4: LineSegment StartX=5.22862e-06 StartY=19 StartZ=0 EndX=5.22862e-06 EndY=1.0161e-12 EndZ=0
    g5: ArcOfCircle CenterX=98 CenterY=19 CenterZ=0 NormalX=0 NormalY=0 NormalZ=1 AngleXU=0 Radius=19 StartAngle=4.71239 EndAngle=6.28319
  constraints (16):
    c: Horizontal(g0)
    c: Distance(g0) = 98
    c: Coincident(g1,g0)
    c: Block(g1)
    c: Coincident(g2,g0)
    c: Vertical(g2)
    c: Distance(g2) = 19
    c: Horizontal(g3)
    c: Coincident(g4,g1)
    c: Vertical(g4)
    c: Coincident(g3,g4)
    c: Block(g3)
    c: Coincident(g5,g2)
    c: Coincident(g5,g3)
    c: Block(g0)
    c: Block(g5)
FEATURE [Part::Extrusion] Extrude026  label="sideA001"
  Base = -> Sketch035
  Dir = (0,0,1)
  DirMode = 2
  FaceMakerClass = Part::FaceMakerBullseye
  LengthFwd = 3
  LengthRev = 0
  Placement = pos=(0,0,-2.7) rot=(0,0,1;0rad)
  Solid = true
  Symmetric = false
FEATURE [Sketcher::SketchObject] Sketch036  label="topSketch008"
  FullyConstrained = true
  sketch-geometry (6):
    g0: LineSegment StartX=19 StartY=38 StartZ=0 EndX=117 EndY=38 EndZ=0
    g1: ArcOfCircle CenterX=19 CenterY=19 CenterZ=0 NormalX=0 NormalY=0 NormalZ=1 AngleXU=0 Radius=19 StartAngle=1.5708 EndAngle=3.14159
    g2: LineSegment StartX=117 StartY=38 StartZ=0 EndX=117 EndY=19 EndZ=0
    g3: LineSegment StartX=98 StartY=1.0161e-12 StartZ=0 EndX=5.22862e-06 EndY=1.0161e-12 EndZ=0
    g4: LineSegment StartX=5.22862e-06 StartY=19 StartZ=0 EndX=5.22862e-06 EndY=1.0161e-12 EndZ=0
    g5: ArcOfCircle CenterX=98 CenterY=19 CenterZ=0 NormalX=0 NormalY=0 NormalZ=1 AngleXU=0 Radius=19 StartAngle=4.71239 EndAngle=6.28319
  constraints (16):
    c: Horizontal(g0)
    c: Distance(g0) = 98
    c: Coincident(g1,g0)
    c: Block(g1)
    c: Coincident(g2,g0)
    c: Vertical(g2)
    c: Distance(g2) = 19
    c: Horizontal(g3)
    c: Coincident(g4,g1)
    c: Vertical(g4)
    c: Coincident(g3,g4)
    c: Block(g3)
    c: Coincident(g5,g2)
    c: Coincident(g5,g3)
    c: Block(g0)
    c: Block(g5)
FEATURE [Part::Extrusion] Extrude027  label="sideB001"
  Base = -> Sketch036
  Dir = (0,0,1)
  DirMode = 2
  FaceMakerClass = Part::FaceMakerBullseye
  LengthFwd = 3
  LengthRev = 0
  Placement = pos=(0,0,71.7) rot=(0,0,1;0rad)
  Solid = true
  Symmetric = false
FEATURE [Part::MultiFuse] Fusion064  label="removeFromBottom"
  Shapes = -> [Extrude026,Extrude027]
FEATURE [Part::Cut] Cut024  label="bottom009"
  Base = -> Fusion060
  Tool = -> Fusion064
FEATURE [Sketcher::SketchObject] Sketch037  label="topSketch009"
  FullyConstrained = true
  sketch-geometry (8):
    g0: ArcOfCircle CenterX=19 CenterY=19.1201 CenterZ=0 NormalX=0 NormalY=0 NormalZ=1 AngleXU=0 Radius=18.8799 StartAngle=1.5708 EndAngle=3.14793
    g1: LineSegment StartX=0.120501 StartY=19.0004 StartZ=0 EndX=0.120501 EndY=0.000382114 EndZ=0
    g2: LineSegment StartX=19 StartY=38 StartZ=0 EndX=124 EndY=38 EndZ=0
    g3: LineSegment StartX=0.120501 StartY=0.000382114 StartZ=0 EndX=105.121 EndY=0.000382114 EndZ=0
    g4: LineSegment StartX=124 StartY=38 StartZ=0 EndX=125.616 EndY=38 EndZ=0
    g5: LineSegment StartX=105.121 StartY=0.000382114 StartZ=0 EndX=106.736 EndY=0.000382114 EndZ=0
    g6: ArcOfCircle CenterX=106.616 CenterY=19 CenterZ=0 NormalX=0 NormalY=0 NormalZ=1 AngleXU=0 Radius=19 StartAngle=4.71873 EndAngle=6.28319
    g7: LineSegment StartX=125.616 StartY=38 StartZ=0 EndX=125.616 EndY=19 EndZ=0
  constraints (21):
    c: Block(g0)
    c: Coincident(g1,g0)
    c: Vertical(g1)
    c: Horizontal(g2)
    c: Distance(g2) = 105
    c: Coincident(g2,g0)
    c: Distance(g1) = 19
    c: Coincident(g3,g1)
    c: Horizontal(g3)
    c: Distance(g3) = 105
    c: Coincident(g4,g2)
    c: Horizontal(g4)
    c: Distance(g4) = 1.61553
    c: Horizontal(g5)
    c: Equal(g4,g5) = 1.61553
    c: Coincident(g5,g3)
    c: Block(g6)
    c: Coincident(g6,g5)
    c: Coincident(g7,g4)
    c: Coincident(g7,g6)
    c: Vertical(g7)
FEATURE [Part::Extrusion] Extrude028  label="sideB"
  Base = -> Sketch037
  Dir = (0,0,1)
  DirMode = 2
  FaceMakerClass = Part::FaceMakerBullseye
  LengthFwd = 3
  LengthRev = 0
  Placement = pos=(0,0,72) rot=(0,0,1;0rad)
  Solid = true
  Symmetric = false
FEATURE [Sketcher::SketchObject] Sketch038  label="topSketch010"
  FullyConstrained = true
  sketch-geometry (22):
    g0: LineSegment StartX=5.21097e-06 StartY=3 StartZ=0 EndX=5.21097e-06 EndY=19 EndZ=0
    g1: ArcOfCircle CenterX=19 CenterY=19 CenterZ=0 NormalX=0 NormalY=0 NormalZ=1 AngleXU=0 Radius=19 StartAngle=1.5708 EndAngle=3.14159
    g2: ArcOfCircle CenterX=19 CenterY=19 CenterZ=0 NormalX=0 NormalY=0 NormalZ=1 AngleXU=0 Radius=16 StartAngle=1.5708 EndAngle=3.14159
    g3: LineSegment StartX=114 StartY=35 StartZ=0 EndX=19 EndY=35 EndZ=0
    g4: LineSegment StartX=5.21097e-06 StartY=3 StartZ=0 EndX=5.21097e-06 EndY=0 EndZ=0
    g5: LineSegment StartX=3 StartY=0 StartZ=0 EndX=5.21097e-06 EndY=0 EndZ=0
    g6: LineSegment StartX=3 StartY=19 StartZ=0 EndX=3 EndY=0 EndZ=0
    g7: LineSegment StartX=19 StartY=38 StartZ=0 EndX=124 EndY=38 EndZ=0
    g8: Circle CenterX=119 CenterY=35 CenterZ=0 NormalX=0 NormalY=0 NormalZ=1 AngleXU=0 Radius=1
    g9: Circle CenterX=121 CenterY=35 CenterZ=0 NormalX=0 NormalY=0 NormalZ=1 AngleXU=0 Radius=1
    g10: Circle CenterX=121 CenterY=33 CenterZ=0 NormalX=0 NormalY=0 NormalZ=1 AngleXU=0 Radius=1
    g11: BSplineCurve PolesCount=3 KnotsCount=2 Degree=2 IsPeriodic=0
    g12: GeomPoint X=119 Y=35 Z=0
    g13: GeomPoint X=121 Y=33 Z=0
    g14: LineSegment StartX=119 StartY=35 StartZ=0 EndX=114 EndY=35 EndZ=0
    g15: ArcOfCircle CenterX=105 CenterY=19 CenterZ=0 NormalX=0 NormalY=0 NormalZ=1 AngleXU=0 Radius=16 StartAngle=5.60905 EndAngle=6.28319
    g16: LineSegment StartX=121 StartY=33 StartZ=0 EndX=121 EndY=19 EndZ=0
    g17: LineSegment StartX=117.5 StartY=9.01251 StartZ=0 EndX=121.163 EndY=9.0125 EndZ=0
    g18: ArcOfCircle CenterX=105 CenterY=19 CenterZ=0 NormalX=0 NormalY=0 NormalZ=1 AngleXU=0 Radius=20.6155 StartAngle=5.7297 EndAngle=6.28319
    g19: LineSegment StartX=121.163 StartY=9.0125 StartZ=0 EndX=122.538 EndY=8.16329 EndZ=0
    g20: LineSegment StartX=124 StartY=38 StartZ=0 EndX=125.616 EndY=38 EndZ=0
    g21: LineSegment StartX=125.616 StartY=19 StartZ=0 EndX=125.616 EndY=38 EndZ=0
  constraints (49):
    c: Vertical(g0)
    c: Block(g0)
    c: Coincident(g1,g0)
    c: Block(g1)
    c: Coincident(g2,g1)
    c: Block(g2)
    c: Coincident(g3,g2)
    c: Horizontal(g3)
    c: Tangent(g3,g2)
    c: Coincident(g4,g0)
    c: Distance(g4) = 3
    c: Vertical(g4)
    c: Coincident(g5,g4)
    c: Horizontal(g5)
    c: Coincident(g6,g2)
    c: Coincident(g6,g5)
    c: Vertical(g6)
    c: Horizontal(g7)
    c: Distance(g7) = 105
    c: Coincident(g7,g1)
    c: Block(g3)
    c: Weight(g8) = 1
    c: Equal(g8,g9)
    c: Equal(g8,g10)
    c: InternalAlignment(g8,g11)
    c: InternalAlignment(g9,g11)
    c: InternalAlignment(g10,g11)
    c: InternalAlignment(g12,g11)
    c: InternalAlignment(g13,g11)
    c: Block(g11)
    c: Coincident(g14,g11)
    c: Coincident(g14,g3)
    c: Horizontal(g14)
    c: Block(g15)
    c: Coincident(g16,g11)
    c: Coincident(g16,g15)
    c: Vertical(g16)
    c: Distance(g16) = 14
    c: Coincident(g17,g15)
    c: Block(g18)
    c: Coincident(g19,g18)
    c: Coincident(g20,g7)
    c: Horizontal(g20)
    c: Vertical(g21)
    c: Coincident(g20,g21)
    c: Block(g20)
    c: Block(g21)
    c: Block(g19)
    c: Block(g17)
FEATURE [Part::Extrusion] Extrude029
  Base = -> Sketch038
  Dir = (0,0,1)
  DirMode = 2
  FaceMakerClass = Part::FaceMakerBullseye
  LengthFwd = 72
  LengthRev = 0
  Solid = true
  Symmetric = false
FEATURE [Part::Feature] Face085
  shape: bbox 4.8 x 25.5 x 2e-07 mm, 1 faces, 0 solids (baked)
FEATURE [Part::Revolution] Revolve089  label="moreFrontCaseScrewPost003"
  Angle = 360
  Axis = (0,1,0)
  Base = (0,0,0)
  FaceMakerClass = Part::FaceMakerBullseye
  Placement = pos=(109.5,4.5,3.5) rot=(0,0,1;0rad)
  Solid = false
  Source = -> Face085
  Symmetric = false
FEATURE [Part::Feature] Face086
  shape: bbox 4.8 x 25.5 x 2e-07 mm, 1 faces, 0 solids (baked)
FEATURE [Part::Revolution] Revolve090  label="moreFrontCaseScrewPost004"
  Angle = 360
  Axis = (0,1,0)
  Base = (0,0,0)
  FaceMakerClass = Part::FaceMakerBullseye
  Placement = pos=(109.5,4.5,68.5) rot=(0,0,1;0rad)
  Solid = false
  Source = -> Face086
  Symmetric = false
FEATURE [Part::Fillet] Fillet026  label="top013"
  Base = -> Extrude029
  Edges = 1 edges r=2: [Edge35]
FEATURE [Sketcher::SketchObject] Sketch039
  FullyConstrained = true
  sketch-geometry (7):
    g0: LineSegment StartX=0 StartY=0 StartZ=0 EndX=0 EndY=6 EndZ=0
    g1: Circle CenterX=0 CenterY=0 CenterZ=0 NormalX=0 NormalY=0 NormalZ=1 AngleXU=0 Radius=1
    g2: Circle CenterX=8 CenterY=6 CenterZ=0 NormalX=0 NormalY=0 NormalZ=1 AngleXU=0 Radius=1
    g3: BSplineCurve PolesCount=3 KnotsCount=2 Degree=2 IsPeriodic=0
    g4: GeomPoint X=0 Y=0 Z=0
    g5: GeomPoint X=8 Y=6 Z=0
    g6: LineSegment StartX=0 StartY=6 StartZ=0 EndX=8 EndY=6 EndZ=0
  constraints (14):
    c: Coincident(g0,g-1)
    c: Distance(g0) = 6
    c: Vertical(g0)
    c: Coincident(g3,g0)
    c: Weight(g1) = 1
    c: Equal(g1,g2)
    c: InternalAlignment(g1,g3)
    c: InternalAlignment(g2,g3)
    c: InternalAlignment(g4,g3)
    c: InternalAlignment(g5,g3)
    c: Block(g3)
    c: Coincident(g6,g0)
    c: Coincident(g6,g3)
    c: Horizontal(g6)
FEATURE [Sketcher::SketchObject] Sketch040
  FullyConstrained = true
  sketch-geometry (7):
    g0: LineSegment StartX=0 StartY=0 StartZ=0 EndX=0 EndY=6 EndZ=0
    g1: Circle CenterX=0 CenterY=0 CenterZ=0 NormalX=0 NormalY=0 NormalZ=1 AngleXU=0 Radius=1
    g2: Circle CenterX=8 CenterY=6 CenterZ=0 NormalX=0 NormalY=0 NormalZ=1 AngleXU=0 Radius=1
    g3: BSplineCurve PolesCount=3 KnotsCount=2 Degree=2 IsPeriodic=0
    g4: GeomPoint X=0 Y=0 Z=0
    g5: GeomPoint X=8 Y=6 Z=0
    g6: LineSegment StartX=0 StartY=6 StartZ=0 EndX=8 EndY=6 EndZ=0
  constraints (14):
    c: Coincident(g0,g-1)
    c: Distance(g0) = 6
    c: Vertical(g0)
    c: Coincident(g3,g0)
    c: Weight(g1) = 1
    c: Equal(g1,g2)
    c: InternalAlignment(g1,g3)
    c: InternalAlignment(g2,g3)
    c: InternalAlignment(g4,g3)
    c: InternalAlignment(g5,g3)
    c: Block(g3)
    c: Coincident(g6,g0)
    c: Coincident(g6,g3)
    c: Horizontal(g6)
FEATURE [Sketcher::SketchObject] Sketch041
  FullyConstrained = true
  sketch-geometry (7):
    g0: LineSegment StartX=0 StartY=0 StartZ=0 EndX=0 EndY=6 EndZ=0
    g1: Circle CenterX=0 CenterY=0 CenterZ=0 NormalX=0 NormalY=0 NormalZ=1 AngleXU=0 Radius=1
    g2: Circle CenterX=8 CenterY=6 CenterZ=0 NormalX=0 NormalY=0 NormalZ=1 AngleXU=0 Radius=1
    g3: BSplineCurve PolesCount=3 KnotsCount=2 Degree=2 IsPeriodic=0
    g4: GeomPoint X=0 Y=0 Z=0
    g5: GeomPoint X=8 Y=6 Z=0
    g6: LineSegment StartX=0 StartY=6 StartZ=0 EndX=8 EndY=6 EndZ=0
  constraints (14):
    c: Coincident(g0,g-1)
    c: Distance(g0) = 6
    c: Vertical(g0)
    c: Coincident(g3,g0)
    c: Weight(g1) = 1
    c: Equal(g1,g2)
    c: InternalAlignment(g1,g3)
    c: InternalAlignment(g2,g3)
    c: InternalAlignment(g4,g3)
    c: InternalAlignment(g5,g3)
    c: Block(g3)
    c: Coincident(g6,g0)
    c: Coincident(g6,g3)
    c: Horizontal(g6)
FEATURE [Sketcher::SketchObject] Sketch042
  FullyConstrained = true
  sketch-geometry (7):
    g0: LineSegment StartX=0 StartY=0 StartZ=0 EndX=0 EndY=6 EndZ=0
    g1: Circle CenterX=0 CenterY=0 CenterZ=0 NormalX=0 NormalY=0 NormalZ=1 AngleXU=0 Radius=1
    g2: Circle CenterX=8 CenterY=6 CenterZ=0 NormalX=0 NormalY=0 NormalZ=1 AngleXU=0 Radius=1
    g3: BSplineCurve PolesCount=3 KnotsCount=2 Degree=2 IsPeriodic=0
    g4: GeomPoint X=0 Y=0 Z=0
    g5: GeomPoint X=8 Y=6 Z=0
    g6: LineSegment StartX=0 StartY=6 StartZ=0 EndX=8 EndY=6 EndZ=0
  constraints (14):
    c: Coincident(g0,g-1)
    c: Distance(g0) = 6
    c: Vertical(g0)
    c: Coincident(g3,g0)
    c: Weight(g1) = 1
    c: Equal(g1,g2)
    c: InternalAlignment(g1,g3)
    c: InternalAlignment(g2,g3)
    c: InternalAlignment(g4,g3)
    c: InternalAlignment(g5,g3)
    c: Block(g3)
    c: Coincident(g6,g0)
    c: Coincident(g6,g3)
    c: Horizontal(g6)
FEATURE [Part::Extrusion] Extrude030  label="caseScrewPillarBracket008"
  Base = -> Sketch039
  Dir = (0,0,1)
  DirMode = 2
  FaceMakerClass = Part::FaceMakerBullseye
  LengthFwd = 2.4
  LengthRev = 0
  Placement = pos=(15.76,29,8.8) rot=(0,1,0;0rad)
  Solid = true
  Symmetric = false
FEATURE [Part::Extrusion] Extrude031  label="caseScrewPillarBracket009"
  Base = -> Sketch040
  Dir = (0,0,1)
  DirMode = 2
  FaceMakerClass = Part::FaceMakerBullseye
  LengthFwd = 2.4
  LengthRev = 0
  Placement = pos=(15.76,29,60.8) rot=(0,0,1;0rad)
  Solid = true
  Symmetric = false
FEATURE [Part::Extrusion] Extrude032  label="caseScrewPillarBracket010"
  Base = -> Sketch041
  Dir = (0,0,1)
  DirMode = 2
  FaceMakerClass = Part::FaceMakerBullseye
  LengthFwd = 2.4
  LengthRev = 0
  Placement = pos=(13.7,29,13.26) rot=(0,-1,0;1.5708rad)
  Solid = true
  Symmetric = false
FEATURE [Part::Extrusion] Extrude033  label="caseScrewPillarBracket011"
  Base = -> Sketch042
  Dir = (0,0,1)
  DirMode = 2
  FaceMakerClass = Part::FaceMakerBullseye
  LengthFwd = 2.4
  LengthRev = 0
  Placement = pos=(11.3,29,58.74) rot=(0,1,0;1.5708rad)
  Solid = true
  Symmetric = false
FEATURE [Sketcher::SketchObject] Sketch043
  FullyConstrained = true
  sketch-geometry (7):
    g0: LineSegment StartX=0 StartY=0 StartZ=0 EndX=0 EndY=6 EndZ=0
    g1: Circle CenterX=0 CenterY=0 CenterZ=0 NormalX=0 NormalY=0 NormalZ=1 AngleXU=0 Radius=1
    g2: Circle CenterX=8 CenterY=6 CenterZ=0 NormalX=0 NormalY=0 NormalZ=1 AngleXU=0 Radius=1
    g3: BSplineCurve PolesCount=3 KnotsCount=2 Degree=2 IsPeriodic=0
    g4: GeomPoint X=0 Y=0 Z=0
    g5: GeomPoint X=8 Y=6 Z=0
    g6: LineSegment StartX=0 StartY=6 StartZ=0 EndX=8 EndY=6 EndZ=0
  constraints (14):
    c: Coincident(g0,g-1)
    c: Distance(g0) = 6
    c: Vertical(g0)
    c: Coincident(g3,g0)
    c: Weight(g1) = 1
    c: Equal(g1,g2)
    c: InternalAlignment(g1,g3)
    c: InternalAlignment(g2,g3)
    c: InternalAlignment(g4,g3)
    c: InternalAlignment(g5,g3)
    c: Block(g3)
    c: Coincident(g6,g0)
    c: Coincident(g6,g3)
    c: Horizontal(g6)
FEATURE [Part::Extrusion] Extrude034  label="caseScrewPillarBracket012"
  Base = -> Sketch043
  Dir = (0,0,1)
  DirMode = 2
  FaceMakerClass = Part::FaceMakerBullseye
  LengthFwd = 2.4
  LengthRev = 0
  Placement = pos=(88.3,29,65.23) rot=(0,1,0;1.5708rad)
  Solid = true
  Symmetric = false
FEATURE [Sketcher::SketchObject] Sketch044
  FullyConstrained = true
  sketch-geometry (7):
    g0: LineSegment StartX=0 StartY=0 StartZ=0 EndX=0 EndY=6 EndZ=0
    g1: Circle CenterX=0 CenterY=0 CenterZ=0 NormalX=0 NormalY=0 NormalZ=1 AngleXU=0 Radius=1
    g2: Circle CenterX=8 CenterY=6 CenterZ=0 NormalX=0 NormalY=0 NormalZ=1 AngleXU=0 Radius=1
    g3: BSplineCurve PolesCount=3 KnotsCount=2 Degree=2 IsPeriodic=0
    g4: GeomPoint X=0 Y=0 Z=0
    g5: GeomPoint X=8 Y=6 Z=0
    g6: LineSegment StartX=0 StartY=6 StartZ=0 EndX=8 EndY=6 EndZ=0
  constraints (14):
    c: Coincident(g0,g-1)
    c: Distance(g0) = 6
    c: Vertical(g0)
    c: Coincident(g3,g0)
    c: Weight(g1) = 1
    c: Equal(g1,g2)
    c: InternalAlignment(g1,g3)
    c: InternalAlignment(g2,g3)
    c: InternalAlignment(g4,g3)
    c: InternalAlignment(g5,g3)
    c: Block(g3)
    c: Coincident(g6,g0)
    c: Coincident(g6,g3)
    c: Horizontal(g6)
FEATURE [Part::Extrusion] Extrude035  label="caseScrewPillarBracket013"
  Base = -> Sketch044
  Dir = (0,0,1)
  DirMode = 2
  FaceMakerClass = Part::FaceMakerBullseye
  LengthFwd = 2.4
  LengthRev = 0
  Placement = pos=(90.7,29,6.77) rot=(0,-1,0;1.5708rad)
  Solid = true
  Symmetric = false
FEATURE [Sketcher::SketchObject] Sketch045
  FullyConstrained = true
  sketch-geometry (7):
    g0: LineSegment StartX=0 StartY=0 StartZ=0 EndX=0 EndY=6 EndZ=0
    g1: Circle CenterX=0 CenterY=0 CenterZ=0 NormalX=0 NormalY=0 NormalZ=1 AngleXU=0 Radius=1
    g2: Circle CenterX=8 CenterY=6 CenterZ=0 NormalX=0 NormalY=0 NormalZ=1 AngleXU=0 Radius=1
    g3: BSplineCurve PolesCount=3 KnotsCount=2 Degree=2 IsPeriodic=0
    g4: GeomPoint X=0 Y=0 Z=0
    g5: GeomPoint X=8 Y=6 Z=0
    g6: LineSegment StartX=0 StartY=6 StartZ=0 EndX=8 EndY=6 EndZ=0
  constraints (14):
    c: Coincident(g0,g-1)
    c: Distance(g0) = 6
    c: Vertical(g0)
    c: Coincident(g3,g0)
    c: Weight(g1) = 1
    c: Equal(g1,g2)
    c: InternalAlignment(g1,g3)
    c: InternalAlignment(g2,g3)
    c: InternalAlignment(g4,g3)
    c: InternalAlignment(g5,g3)
    c: Block(g3)
    c: Coincident(g6,g0)
    c: Coincident(g6,g3)
    c: Horizontal(g6)
FEATURE [Sketcher::SketchObject] Sketch046
  FullyConstrained = true
  sketch-geometry (7):
    g0: LineSegment StartX=0 StartY=0 StartZ=0 EndX=0 EndY=6 EndZ=0
    g1: Circle CenterX=0 CenterY=0 CenterZ=0 NormalX=0 NormalY=0 NormalZ=1 AngleXU=0 Radius=1
    g2: Circle CenterX=8 CenterY=6 CenterZ=0 NormalX=0 NormalY=0 NormalZ=1 AngleXU=0 Radius=1
    g3: BSplineCurve PolesCount=3 KnotsCount=2 Degree=2 IsPeriodic=0
    g4: GeomPoint X=0 Y=0 Z=0
    g5: GeomPoint X=8 Y=6 Z=0
    g6: LineSegment StartX=0 StartY=6 StartZ=0 EndX=8 EndY=6 EndZ=0
  constraints (14):
    c: Coincident(g0,g-1)
    c: Distance(g0) = 6
    c: Vertical(g0)
    c: Coincident(g3,g0)
    c: Weight(g1) = 1
    c: Equal(g1,g2)
    c: InternalAlignment(g1,g3)
    c: InternalAlignment(g2,g3)
    c: InternalAlignment(g4,g3)
    c: InternalAlignment(g5,g3)
    c: Block(g3)
    c: Coincident(g6,g0)
    c: Coincident(g6,g3)
    c: Horizontal(g6)
FEATURE [Part::Extrusion] Extrude036  label="caseScrewPillarBracket014"
  Base = -> Sketch045
  Dir = (0,0,1)
  DirMode = 2
  FaceMakerClass = Part::FaceMakerBullseye
  LengthFwd = 2.4
  LengthRev = 0
  Placement = pos=(110.7,29,6.77) rot=(0,-1,0;1.5708rad)
  Solid = true
  Symmetric = false
FEATURE [Part::Extrusion] Extrude037  label="caseScrewPillarBracket015"
  Base = -> Sketch046
  Dir = (0,0,1)
  DirMode = 2
  FaceMakerClass = Part::FaceMakerBullseye
  LengthFwd = 2.4
  LengthRev = 0
  Placement = pos=(108.3,29,65.23) rot=(0,1,0;1.5708rad)
  Solid = true
  Symmetric = false
FEATURE [Part::Box] Box013  label="frontCaseScrewPillarBracket002"
  AttacherType = Attacher::AttachEngine3D
  Height = 2.4
  Length = 22
  Placement = pos=(87,28,2.3) rot=(0,0,1;0rad)
  Width = 7
FEATURE [Part::Box] Box014  label="frontCaseScrewPillarBracket003"
  AttacherType = Attacher::AttachEngine3D
  Height = 2.4
  Length = 22
  Placement = pos=(87,28,67.3) rot=(0,0,1;0rad)
  Width = 7
FEATURE [Part::Feature] Face087
  shape: bbox 4.8 x 30.2 x 2e-07 mm, 1 faces, 0 solids (baked)
FEATURE [Part::Revolution] Revolve091  label="frontCaseScrewPost004"
  Angle = 360
  Axis = (0,1,0)
  Base = (0,0,0)
  FaceMakerClass = Part::FaceMakerBullseye
  Placement = pos=(89.5,4.5,3.5) rot=(0,0,1;0rad)
  Solid = false
  Source = -> Face087
  Symmetric = false
FEATURE [Part::Feature] Face088
  shape: bbox 4.8 x 30.2 x 2e-07 mm, 1 faces, 0 solids (baked)
FEATURE [Part::Revolution] Revolve092  label="frontCaseScrewPost005"
  Angle = 360
  Axis = (0,1,0)
  Base = (0,0,0)
  FaceMakerClass = Part::FaceMakerBullseye
  Placement = pos=(89.5,4.5,68.5) rot=(0,0,1;0rad)
  Solid = false
  Source = -> Face088
  Symmetric = false
FEATURE [Part::Feature] Face089
  shape: bbox 3.5 x 30.2 x 2e-07 mm, 1 faces, 0 solids (baked)
FEATURE [Part::Revolution] Revolve093  label="backCaseScrewPost002"
  Angle = 360
  Axis = (0,1,0)
  Base = (0,0,0)
  FaceMakerClass = Part::FaceMakerBullseye
  Placement = pos=(12.5,4.5,10) rot=(0,0,1;0rad)
  Solid = false
  Source = -> Face089
  Symmetric = false
FEATURE [Part::Feature] Face090
  shape: bbox 3.5 x 30.2 x 2e-07 mm, 1 faces, 0 solids (baked)
FEATURE [Part::Revolution] Revolve094  label="backCaseScrewPost003"
  Angle = 360
  Axis = (0,1,0)
  Base = (0,0,0)
  FaceMakerClass = Part::FaceMakerBullseye
  Placement = pos=(12.5,4.5,62) rot=(0,0,1;0rad)
  Solid = false
  Source = -> Face090
  Symmetric = false
FEATURE [Part::Box] Box015  label="Cube011"
  AttacherType = Attacher::AttachEngine3D
  Height = 28.8
  Length = 3
  Placement = pos=(107.3,28,21.6) rot=(0,0,1;0rad)
  Width = 7
FEATURE [Part::Box] Box016  label="Cube012"
  AttacherType = Attacher::AttachEngine3D
  Height = 3
  Length = 7.4
  Placement = pos=(107.3,28,18.6) rot=(0,0,1;0rad)
  Width = 7
FEATURE [Part::Box] Box017  label="Cube013"
  AttacherType = Attacher::AttachEngine3D
  Height = 3
  Length = 7.4
  Placement = pos=(107.3,28,50.4) rot=(0,0,1;0rad)
  Width = 7
FEATURE [Part::Cylinder] Cylinder024
  Angle = 360
  AttacherType = Attacher::AttachEngine3D
  Height = 20
  Placement = pos=(0,0,36.15) rot=(0,0,1;0rad)
  Radius = 14.3
FEATURE [Part::Cylinder] Cylinder025
  Angle = 360
  AttacherType = Attacher::AttachEngine3D
  Height = 10
  Placement = pos=(0,0,36.15) rot=(0,0,1;0rad)
  Radius = 4
FEATURE [Part::MultiFuse] Fusion066  label="removeToCreteHoleForPlugHousing009"
  Placement = pos=(70,19,36) rot=(0,1,0;1.5708rad)
  Shapes = -> [Cylinder024,Cylinder025]
FEATURE [Part::MultiFuse] Fusion065  label="plugHousingBracketHolder002"
  Shapes = -> [Box017,Box015,Box016]
FEATURE [Part::Cut] Cut025  label="plugHousingBracketHolder003"
  Base = -> Fusion065
  Placement = pos=(7,0,0) rot=(0,0,1;0rad)
  Tool = -> Fusion066
FEATURE [Sketcher::SketchObject] Sketch047
  FullyConstrained = false
  Placement = pos=(0,0,0) rot=(1,0,0;1.5708rad)
  sketch-geometry (24):
    g0: ArcOfCircle CenterX=-4 CenterY=-10.5 CenterZ=0 NormalX=0 NormalY=0 NormalZ=1 AngleXU=0 Radius=1.5 StartAngle=6e-16 EndAngle=3.14159
    g1: ArcOfCircle CenterX=-34.2 CenterY=-10.5 CenterZ=0 NormalX=0 NormalY=0 NormalZ=1 AngleXU=0 Radius=1.5 StartAngle=0 EndAngle=3.14159
    g2: ArcOfCircle CenterX=-34.2 CenterY=-27.7 CenterZ=0 NormalX=0 NormalY=0 NormalZ=1 AngleXU=0 Radius=1.5 StartAngle=3.14159 EndAngle=6.28319
    g3: ArcOfCircle CenterX=-4 CenterY=-27.7 CenterZ=0 NormalX=0 NormalY=0 NormalZ=1 AngleXU=0 Radius=1.5 StartAngle=3.1416 EndAngle=6.28319
    g4: ArcOfCircle CenterX=-10 CenterY=-4.3 CenterZ=0 NormalX=0 NormalY=0 NormalZ=1 AngleXU=0 Radius=1.5 StartAngle=2e-16 EndAngle=3.14159
    g5: ArcOfCircle CenterX=-16.1 CenterY=-1.8 CenterZ=0 NormalX=0 NormalY=0 NormalZ=1 AngleXU=0 Radius=1.5 StartAngle=5e-16 EndAngle=3.14159
    g6: ArcOfCircle CenterX=-22.1 CenterY=-1.8 CenterZ=0 NormalX=0 NormalY=0 NormalZ=1 AngleXU=0 Radius=1.5 StartAngle=5e-16 EndAngle=3.14159
    g7: ArcOfCircle CenterX=-28.2 CenterY=-4.3 CenterZ=0 NormalX=0 NormalY=0 NormalZ=1 AngleXU=0 Radius=1.5 StartAngle=2e-16 EndAngle=3.14159
    g8: ArcOfCircle CenterX=-10 CenterY=-33.9 CenterZ=0 NormalX=0 NormalY=0 NormalZ=1 AngleXU=0 Radius=1.5 StartAngle=3.14159 EndAngle=6.28319
    g9: ArcOfCircle CenterX=-16.1 CenterY=-36.4 CenterZ=0 NormalX=0 NormalY=0 NormalZ=1 AngleXU=0 Radius=1.5 StartAngle=3.14159 EndAngle=6.28319
    g10: ArcOfCircle CenterX=-22.1 CenterY=-36.4 CenterZ=0 NormalX=0 NormalY=0 NormalZ=1 AngleXU=0 Radius=1.5 StartAngle=3.14159 EndAngle=6.28319
    g11: ArcOfCircle CenterX=-28.2 CenterY=-33.9 CenterZ=0 NormalX=0 NormalY=0 NormalZ=1 AngleXU=0 Radius=1.5 StartAngle=3.14159 EndAngle=6.28319
    g12: LineSegment StartX=-35.7 StartY=-10.5 StartZ=0 EndX=-35.7 EndY=-27.7 EndZ=0
    g13: LineSegment StartX=-32.7 StartY=-10.5 StartZ=0 EndX=-32.7 EndY=-27.7 EndZ=0
    g14: LineSegment StartX=-29.7 StartY=-33.9 StartZ=0 EndX=-29.7 EndY=-4.3 EndZ=0
    g15: LineSegment StartX=-26.7 StartY=-33.9 StartZ=0 EndX=-26.7 EndY=-4.3 EndZ=0
    g16: LineSegment StartX=-2.5 StartY=-10.5 StartZ=0 EndX=-2.5 EndY=-27.7 EndZ=0
    g17: LineSegment StartX=-8.5 StartY=-4.3 StartZ=0 EndX=-8.5 EndY=-33.9 EndZ=0
    g18: LineSegment StartX=-5.5 StartY=-10.5 StartZ=0 EndX=-5.5 EndY=-27.7 EndZ=0
    g19: LineSegment StartX=-11.5 StartY=-4.3 StartZ=0 EndX=-11.5 EndY=-33.9 EndZ=0
    g20: LineSegment StartX=-14.6 StartY=-1.8 StartZ=0 EndX=-14.6 EndY=-36.4 EndZ=0
    g21: LineSegment StartX=-17.6 StartY=-1.8 StartZ=0 EndX=-17.6 EndY=-36.4 EndZ=0
    g22: LineSegment StartX=-20.6 StartY=-36.4 StartZ=0 EndX=-20.6 EndY=-1.8 EndZ=0
    g23: LineSegment StartX=-23.6 StartY=-1.8 StartZ=0 EndX=-23.6 EndY=-36.4 EndZ=0
  constraints (48):
    c: Block(g0)
    c: Block(g1)
    c: Block(g2)
    c: Block(g3)
    c: Block(g4)
    c: Block(g5)
    c: Block(g6)
    c: Block(g7)
    c: Block(g8)
    c: Block(g9)
    c: Block(g10)
    c: Block(g11)
    c: Coincident(g12,g1)
    c: Coincident(g12,g2)
    c: Vertical(g12)
    c: Coincident(g13,g1)
    c: Coincident(g13,g2)
    c: Vertical(g13)
    c: Coincident(g14,g11)
    c: Coincident(g14,g7)
    c: Vertical(g14)
    c: Coincident(g15,g11)
    c: Coincident(g15,g7)
    c: Vertical(g15)
    c: Coincident(g16,g0)
    c: Coincident(g16,g3)
    c: Vertical(g16)
    c: Coincident(g17,g4)
    c: Coincident(g17,g8)
    c: Vertical(g17)
    c: Coincident(g18,g0)
    c: Coincident(g18,g3)
    c: Vertical(g18)
    c: Coincident(g19,g4)
    c: Coincident(g19,g8)
    c: Vertical(g19)
    c: Coincident(g20,g5)
    c: Coincident(g20,g9)
    c: Vertical(g20)
    c: Coincident(g21,g5)
    c: Coincident(g21,g9)
    c: Vertical(g21)
    c: Coincident(g22,g10)
    c: Coincident(g22,g6)
    c: Vertical(g22)
    c: Coincident(g23,g6)
    c: Coincident(g23,g10)
    c: Vertical(g23)
FEATURE [Part::Extrusion] Extrude038  label="removeToCreateFanGrillHoles001"
  Base = -> Sketch047
  Dir = (0,-1,6e-16)
  DirMode = 2
  FaceMakerClass = Part::FaceMakerBullseye
  LengthFwd = 10
  LengthRev = 0
  Placement = pos=(65.4,44,54.82) rot=(0,0,1;0rad)
  Solid = true
  Symmetric = false
FEATURE [Part::Feature] Wire004
  shape: bbox 11 x 5.2 x 2e-07 mm, 0 faces, 0 solids (baked)
FEATURE [Part::Revolution] Revolve095
  Angle = 360
  Axis = (0,1,0)
  Base = (0,0,0)
  FaceMakerClass = Part::FaceMakerBullseye
  Placement = pos=(30.3,38,19.7) rot=(0,0,1;0rad)
  Solid = true
  Source = -> Wire004
  Symmetric = false
FEATURE [Part::Feature] Wire005
  shape: bbox 11 x 5.2 x 2e-07 mm, 0 faces, 0 solids (baked)
FEATURE [Part::Revolution] Revolve096
  Angle = 360
  Axis = (0,1,0)
  Base = (0,0,0)
  FaceMakerClass = Part::FaceMakerBullseye
  Placement = pos=(30.3,38,51.7) rot=(0,0,1;0rad)
  Solid = true
  Source = -> Wire005
  Symmetric = false
FEATURE [Part::Feature] Wire006
  shape: bbox 11 x 5.2 x 2e-07 mm, 0 faces, 0 solids (baked)
FEATURE [Part::Revolution] Revolve097
  Angle = 360
  Axis = (0,1,0)
  Base = (0,0,0)
  FaceMakerClass = Part::FaceMakerBullseye
  Placement = pos=(62.3,38,51.7) rot=(0,0,1;0rad)
  Solid = true
  Source = -> Wire006
  Symmetric = false
FEATURE [Part::Feature] Wire007
  shape: bbox 11 x 5.2 x 2e-07 mm, 0 faces, 0 solids (baked)
FEATURE [Part::Revolution] Revolve098
  Angle = 360
  Axis = (0,1,0)
  Base = (0,0,0)
  FaceMakerClass = Part::FaceMakerBullseye
  Placement = pos=(62.3,38,19.7) rot=(0,0,1;0rad)
  Solid = true
  Source = -> Wire007
  Symmetric = false
FEATURE [Part::MultiFuse] Fusion067  label="fanScrewHousing002"
  Shapes = -> [Revolve098,Revolve097,Revolve096,Revolve095]
FEATURE [Part::Feature] Face091 .. Face094  x4 (patterned run collapsed; names and placements below)
  shape: bbox 3.5 x 17.8 x 2e-07 mm, 1 faces, 0 solids (baked)
FEATURE [Part::Revolution] Revolve099  label="removeToCreateScrewAndThreadedInsertHole026"
  Angle = 360
  Axis = (0,1,0)
  Base = (0,0,0)
  FaceMakerClass = Part::FaceMakerBullseye
  Placement = pos=(62.3,30.3,19.7) rot=(0,0,1;0rad)
  Solid = false
  Source = -> Face091
  Symmetric = false
FEATURE [Part::Revolution] Revolve100  label="removeToCreateScrewAndThreadedInsertHole027"
  Angle = 360
  Axis = (0,1,0)
  Base = (0,0,0)
  FaceMakerClass = Part::FaceMakerBullseye
  Placement = pos=(62.3,30.3,51.7) rot=(0,0,1;0rad)
  Solid = false
  Source = -> Face092
  Symmetric = false
FEATURE [Part::Revolution] Revolve101  label="removeToCreateScrewAndThreadedInsertHole028"
  Angle = 360
  Axis = (0,1,0)
  Base = (0,0,0)
  FaceMakerClass = Part::FaceMakerBullseye
  Placement = pos=(30.3,30.3,19.7) rot=(0,0,1;0rad)
  Solid = false
  Source = -> Face093
  Symmetric = false
FEATURE [Part::Revolution] Revolve102  label="removeToCreateScrewAndThreadedInsertHole029"
  Angle = 360
  Axis = (0,1,0)
  Base = (0,0,0)
  FaceMakerClass = Part::FaceMakerBullseye
  Placement = pos=(30.3,30.3,51.7) rot=(0,0,1;0rad)
  Solid = false
  Source = -> Face094
  Symmetric = false
FEATURE [Part::MultiFuse] Fusion068  label="createThreadedInsertHolesForFan002"
  Shapes = -> [Revolve099,Revolve100,Revolve101,Revolve102]
FEATURE [Part::Cut] Cut026  label="fanScrewHousing003"
  Base = -> Fusion067
  Tool = -> Fusion068
FEATURE [Sketcher::SketchObject] Sketch048
  FullyConstrained = false
  Placement = pos=(0,0,0) rot=(1,0,0;1.5708rad)
  sketch-geometry (24):
    g0: ArcOfCircle CenterX=-4 CenterY=-10.5 CenterZ=0 NormalX=0 NormalY=0 NormalZ=1 AngleXU=0 Radius=1.5 StartAngle=6e-16 EndAngle=3.14159
    g1: ArcOfCircle CenterX=-34.2 CenterY=-10.5 CenterZ=0 NormalX=0 NormalY=0 NormalZ=1 AngleXU=0 Radius=1.5 StartAngle=0 EndAngle=3.14159
    g2: ArcOfCircle CenterX=-34.2 CenterY=-27.7 CenterZ=0 NormalX=0 NormalY=0 NormalZ=1 AngleXU=0 Radius=1.5 StartAngle=3.14159 EndAngle=6.28319
    g3: ArcOfCircle CenterX=-4 CenterY=-27.7 CenterZ=0 NormalX=0 NormalY=0 NormalZ=1 AngleXU=0 Radius=1.5 StartAngle=3.1416 EndAngle=6.28319
    g4: ArcOfCircle CenterX=-10 CenterY=-4.3 CenterZ=0 NormalX=0 NormalY=0 NormalZ=1 AngleXU=0 Radius=1.5 StartAngle=2e-16 EndAngle=3.14159
    g5: ArcOfCircle CenterX=-16.1 CenterY=-1.8 CenterZ=0 NormalX=0 NormalY=0 NormalZ=1 AngleXU=0 Radius=1.5 StartAngle=5e-16 EndAngle=3.14159
    g6: ArcOfCircle CenterX=-22.1 CenterY=-1.8 CenterZ=0 NormalX=0 NormalY=0 NormalZ=1 AngleXU=0 Radius=1.5 StartAngle=5e-16 EndAngle=3.14159
    g7: ArcOfCircle CenterX=-28.2 CenterY=-4.3 CenterZ=0 NormalX=0 NormalY=0 NormalZ=1 AngleXU=0 Radius=1.5 StartAngle=2e-16 EndAngle=3.14159
    g8: ArcOfCircle CenterX=-10 CenterY=-33.9 CenterZ=0 NormalX=0 NormalY=0 NormalZ=1 AngleXU=0 Radius=1.5 StartAngle=3.14159 EndAngle=6.28319
    g9: ArcOfCircle CenterX=-16.1 CenterY=-36.4 CenterZ=0 NormalX=0 NormalY=0 NormalZ=1 AngleXU=0 Radius=1.5 StartAngle=3.14159 EndAngle=6.28319
    g10: ArcOfCircle CenterX=-22.1 CenterY=-36.4 CenterZ=0 NormalX=0 NormalY=0 NormalZ=1 AngleXU=0 Radius=1.5 StartAngle=3.14159 EndAngle=6.28319
    g11: ArcOfCircle CenterX=-28.2 CenterY=-33.9 CenterZ=0 NormalX=0 NormalY=0 NormalZ=1 AngleXU=0 Radius=1.5 StartAngle=3.14159 EndAngle=6.28319
    g12: LineSegment StartX=-35.7 StartY=-10.5 StartZ=0 EndX=-35.7 EndY=-27.7 EndZ=0
    g13: LineSegment StartX=-32.7 StartY=-10.5 StartZ=0 EndX=-32.7 EndY=-27.7 EndZ=0
    g14: LineSegment StartX=-29.7 StartY=-33.9 StartZ=0 EndX=-29.7 EndY=-4.3 EndZ=0
    g15: LineSegment StartX=-26.7 StartY=-33.9 StartZ=0 EndX=-26.7 EndY=-4.3 EndZ=0
    g16: LineSegment StartX=-2.5 StartY=-10.5 StartZ=0 EndX=-2.5 EndY=-27.7 EndZ=0
    g17: LineSegment StartX=-8.5 StartY=-4.3 StartZ=0 EndX=-8.5 EndY=-33.9 EndZ=0
    g18: LineSegment StartX=-5.5 StartY=-10.5 StartZ=0 EndX=-5.5 EndY=-27.7 EndZ=0
    g19: LineSegment StartX=-11.5 StartY=-4.3 StartZ=0 EndX=-11.5 EndY=-33.9 EndZ=0
    g20: LineSegment StartX=-14.6 StartY=-1.8 StartZ=0 EndX=-14.6 EndY=-36.4 EndZ=0
    g21: LineSegment StartX=-17.6 StartY=-1.8 StartZ=0 EndX=-17.6 EndY=-36.4 EndZ=0
    g22: LineSegment StartX=-20.6 StartY=-36.4 StartZ=0 EndX=-20.6 EndY=-1.8 EndZ=0
    g23: LineSegment StartX=-23.6 StartY=-1.8 StartZ=0 EndX=-23.6 EndY=-36.4 EndZ=0
  constraints (48):
    c: Block(g0)
    c: Block(g1)
    c: Block(g2)
    c: Block(g3)
    c: Block(g4)
    c: Block(g5)
    c: Block(g6)
    c: Block(g7)
    c: Block(g8)
    c: Block(g9)
    c: Block(g10)
    c: Block(g11)
    c: Coincident(g12,g1)
    c: Coincident(g12,g2)
    c: Vertical(g12)
    c: Coincident(g13,g1)
    c: Coincident(g13,g2)
    c: Vertical(g13)
    c: Coincident(g14,g11)
    c: Coincident(g14,g7)
    c: Vertical(g14)
    c: Coincident(g15,g11)
    c: Coincident(g15,g7)
    c: Vertical(g15)
    c: Coincident(g16,g0)
    c: Coincident(g16,g3)
    c: Vertical(g16)
    c: Coincident(g17,g4)
    c: Coincident(g17,g8)
    c: Vertical(g17)
    c: Coincident(g18,g0)
    c: Coincident(g18,g3)
    c: Vertical(g18)
    c: Coincident(g19,g4)
    c: Coincident(g19,g8)
    c: Vertical(g19)
    c: Coincident(g20,g5)
    c: Coincident(g20,g9)
    c: Vertical(g20)
    c: Coincident(g21,g5)
    c: Coincident(g21,g9)
    c: Vertical(g21)
    c: Coincident(g22,g10)
    c: Coincident(g22,g6)
    c: Vertical(g22)
    c: Coincident(g23,g6)
    c: Coincident(g23,g10)
    c: Vertical(g23)
FEATURE [Part::Extrusion] Extrude039  label="removeToCreateFanGrillHoles002"
  Base = -> Sketch048
  Dir = (0,-1,6e-16)
  DirMode = 2
  FaceMakerClass = Part::FaceMakerBullseye
  LengthFwd = 10
  LengthRev = 0
  Placement = pos=(65.4,44,54.82) rot=(0,0,1;0rad)
  Solid = true
  Symmetric = false
FEATURE [Part::Cut] Cut027  label="fanScrewHousing004"
  Base = -> Cut026
  Tool = -> Extrude038
FEATURE [Part::Cut] Cut028  label="top014"
  Base = -> Fillet026
  Tool = -> Extrude039
FEATURE [Part::Feature] Face095 .. Face098  x4 (patterned run collapsed; names and placements below)
  shape: bbox 3.5 x 17.8 x 2e-07 mm, 1 faces, 0 solids (baked)
FEATURE [Part::Revolution] Revolve103  label="removeToCreateScrewAndThreadedInsertHole030"
  Angle = 360
  Axis = (0,1,0)
  Base = (0,0,0)
  FaceMakerClass = Part::FaceMakerBullseye
  Placement = pos=(62.3,30.3,19.7) rot=(0,0,1;0rad)
  Solid = false
  Source = -> Face095
  Symmetric = false
FEATURE [Part::Revolution] Revolve104  label="removeToCreateScrewAndThreadedInsertHole031"
  Angle = 360
  Axis = (0,1,0)
  Base = (0,0,0)
  FaceMakerClass = Part::FaceMakerBullseye
  Placement = pos=(62.3,30.3,51.7) rot=(0,0,1;0rad)
  Solid = false
  Source = -> Face096
  Symmetric = false
FEATURE [Part::Revolution] Revolve105  label="removeToCreateScrewAndThreadedInsertHole032"
  Angle = 360
  Axis = (0,1,0)
  Base = (0,0,0)
  FaceMakerClass = Part::FaceMakerBullseye
  Placement = pos=(30.3,30.3,19.7) rot=(0,0,1;0rad)
  Solid = false
  Source = -> Face097
  Symmetric = false
FEATURE [Part::Revolution] Revolve106  label="removeToCreateScrewAndThreadedInsertHole033"
  Angle = 360
  Axis = (0,1,0)
  Base = (0,0,0)
  FaceMakerClass = Part::FaceMakerBullseye
  Placement = pos=(30.3,30.3,51.7) rot=(0,0,1;0rad)
  Solid = false
  Source = -> Face098
  Symmetric = false
FEATURE [Part::MultiFuse] Fusion069  label="createThreadedInsertHolesForFan003"
  Shapes = -> [Revolve103,Revolve104,Revolve105,Revolve106]
FEATURE [Part::Cut] Cut029  label="top015"
  Base = -> Cut028
  Tool = -> Fusion054
FEATURE [Part::Cut] Cut030  label="fanScrewHousing005"
  Base = -> Cut027
  Tool = -> Fusion069
FEATURE [Part::Cylinder] Cylinder026  label="removeToCreteHoleForPlugHousing010"
  Angle = 360
  AttacherType = Attacher::AttachEngine3D
  Height = 20
  Placement = pos=(-2,19,36) rot=(0,1,0;1.5708rad)
  Radius = 14.3
FEATURE [Part::Box] Box018  label="removeToCreteHoleForPlugHousing011"
  AttacherType = Attacher::AttachEngine3D
  Height = 28.6
  Length = 10
  Placement = pos=(-2,0,21.7) rot=(0,0,1;0rad)
  Width = 19
FEATURE [Part::Box] Box019  label="wireHolderBottomCaseBit"
  AttacherType = Attacher::AttachEngine3D
  Height = 28
  Length = 3
  Placement = pos=(0,0,22) rot=(0,0,1;0rad)
  Width = 21
FEATURE [Part::Cylinder] Cylinder027  label="removeToCreteHoleForPlugHousing012"
  Angle = 360
  AttacherType = Attacher::AttachEngine3D
  Height = 20
  Placement = pos=(-2,19,36) rot=(0,1,0;1.5708rad)
  Radius = 14.3
FEATURE [Part::Cut] Cut031  label="wireHolderBottomCaseBit001"
  Base = -> Box019
  Tool = -> Cylinder027
FEATURE [Part::MultiFuse] Fusion070  label="removeToCreteHoleForPlugHousing013"
  Shapes = -> [Box018,Cylinder026]
FEATURE [Part::Cut] Cut032  label="top016"
  Base = -> Cut029
  Tool = -> Fusion070
FEATURE [Part::Cylinder] Cylinder028
  Angle = 360
  AttacherType = Attacher::AttachEngine3D
  Height = 20
  Placement = pos=(0,0,36.15) rot=(0,0,1;0rad)
  Radius = 14.3
FEATURE [Part::Cylinder] Cylinder029
  Angle = 360
  AttacherType = Attacher::AttachEngine3D
  Height = 10
  Placement = pos=(0,0,36.15) rot=(0,0,1;0rad)
  Radius = 4
FEATURE [Part::MultiFuse] Fusion071  label="removeToCreteHoleForPlugHousing014"
  Placement = pos=(70,19,36) rot=(0,1,0;1.5708rad)
  Shapes = -> [Cylinder028,Cylinder029]
FEATURE [Sketcher::SketchObject] Sketch049  label="topSketch011"
  FullyConstrained = true
  sketch-geometry (4):
    g0: ArcOfCircle CenterX=105 CenterY=19 CenterZ=0 NormalX=0 NormalY=0 NormalZ=1 AngleXU=0 Radius=20.6155 StartAngle=5.54125 EndAngle=6.28319
    g1: ArcOfCircle CenterX=105 CenterY=19 CenterZ=0 NormalX=0 NormalY=0 NormalZ=1 AngleXU=0 Radius=13 StartAngle=5.54125 EndAngle=6.28319
    g2: LineSegment StartX=118 StartY=19 StartZ=0 EndX=125.616 EndY=19 EndZ=0
    g3: LineSegment StartX=114.583 StartY=10.2157 StartZ=0 EndX=120.197 EndY=5.06982 EndZ=0
  constraints (7):
    c: Block(g0)
    c: Block(g1)
    c: Coincident(g2,g1)
    c: Coincident(g2,g0)
    c: Horizontal(g2)
    c: Coincident(g3,g1)
    c: Coincident(g3,g0)
FEATURE [Part::Box] Box020  label="removeToCreteHoleForPlugHousing015"
  AttacherType = Attacher::AttachEngine3D
  Height = 28.6
  Length = 20
  Placement = pos=(106.15,0,21.7) rot=(0,0,1;0rad)
  Width = 19
FEATURE [Part::MultiFuse] Fusion072  label="removeToCreteHoleForPlugHousing016"
  Shapes = -> [Box020,Fusion071]
FEATURE [Part::Cut] Cut033  label="removeToCreteHoleForPlugHousing017"
  Base = -> Cut032
  Tool = -> Fusion072
FEATURE [Part::Cylinder] Cylinder030
  Angle = 360
  AttacherType = Attacher::AttachEngine3D
  Height = 20
  Placement = pos=(0,0,36.15) rot=(0,0,1;0rad)
  Radius = 14.3
FEATURE [Part::Cylinder] Cylinder031
  Angle = 360
  AttacherType = Attacher::AttachEngine3D
  Height = 10
  Placement = pos=(0,0,36.15) rot=(0,0,1;0rad)
  Radius = 4
FEATURE [Part::Box] Box021  label="removeToCreteHoleForPlugHousing019"
  AttacherType = Attacher::AttachEngine3D
  Height = 28.6
  Length = 20
  Placement = pos=(106.15,0,21.7) rot=(0,0,1;0rad)
  Width = 19
FEATURE [Part::MultiFuse] Fusion074  label="removeToCreteHoleForPlugHousing020"
  Placement = pos=(70,19,36) rot=(0,1,0;1.5708rad)
  Shapes = -> [Cylinder030,Cylinder031]
FEATURE [Part::MultiFuse] Fusion073  label="removeToCreteHoleForPlugHousing018"
  Placement = pos=(0,0,28.3) rot=(0,0,1;0rad)
  Shapes = -> [Box021,Fusion074]
FEATURE [Part::Cylinder] Cylinder032
  Angle = 360
  AttacherType = Attacher::AttachEngine3D
  Height = 20
  Placement = pos=(0,0,36.15) rot=(0,0,1;0rad)
  Radius = 14.3
FEATURE [Part::Cylinder] Cylinder033
  Angle = 360
  AttacherType = Attacher::AttachEngine3D
  Height = 10
  Placement = pos=(0,0,36.15) rot=(0,0,1;0rad)
  Radius = 4
FEATURE [Part::Box] Box022  label="removeToCreteHoleForPlugHousing021"
  AttacherType = Attacher::AttachEngine3D
  Height = 28.6
  Length = 20
  Placement = pos=(106.15,0,21.7) rot=(0,0,1;0rad)
  Width = 19
FEATURE [Part::MultiFuse] Fusion076  label="removeToCreteHoleForPlugHousing023"
  Placement = pos=(70,19,36) rot=(0,1,0;1.5708rad)
  Shapes = -> [Cylinder032,Cylinder033]
FEATURE [Part::MultiFuse] Fusion075  label="removeToCreteHoleForPlugHousing022"
  Placement = pos=(0,0,-28.3) rot=(0,0,1;0rad)
  Shapes = -> [Box022,Fusion076]
FEATURE [Part::MultiFuse] Fusion077  label="removeToCreatePlugHousingBottomBit"
  Shapes = -> [Fusion075,Fusion073]
FEATURE [Part::Cylinder] Cylinder034
  Angle = 360
  AttacherType = Attacher::AttachEngine3D
  Height = 20
  Placement = pos=(0,0,36.15) rot=(0,0,1;0rad)
  Radius = 14
FEATURE [Part::Cylinder] Cylinder035
  Angle = 360
  AttacherType = Attacher::AttachEngine3D
  Height = 10
  Placement = pos=(0,0,36.15) rot=(0,0,1;0rad)
  Radius = 4
FEATURE [Part::MultiFuse] Fusion078  label="removeToCreteHoleForPlugHousing024"
  Placement = pos=(70,19,36) rot=(0,1,0;1.5708rad)
  Shapes = -> [Cylinder034,Cylinder035]
FEATURE [Part::MultiFuse] Fusion079  label="removeToCreatePlugHousingBottomBit001"
  Shapes = -> [Fusion078,Fusion077]
FEATURE [Part::Extrusion] Extrude040  label="bottomPlugHousingBit"
  Base = -> Sketch049
  Dir = (0,0,1)
  DirMode = 2
  FaceMakerClass = Part::FaceMakerBullseye
  LengthFwd = 72
  LengthRev = 0
  Solid = true
  Symmetric = false
FEATURE [Part::Cut] Cut034  label="bottomPlugHousingBit001"
  Base = -> Extrude040
  Placement = pos=(-0.09,0,0) rot=(0,0,1;0rad)
  Tool = -> Fusion079
FEATURE [Part::Box] Box023  label="Cube014"
  AttacherType = Attacher::AttachEngine3D
  Height = 16
  Length = 8
  Placement = pos=(12.7,31.52,28) rot=(0,0,1;0rad)
  Width = 4
FEATURE [Part::Cylinder] Cylinder036
  Angle = 360
  AttacherType = Attacher::AttachEngine3D
  Height = 10
  Placement = pos=(0,0,36.15) rot=(0,0,1;0rad)
  Radius = 4
FEATURE [Part::Cylinder] Cylinder037
  Angle = 360
  AttacherType = Attacher::AttachEngine3D
  Height = 20
  Placement = pos=(0,0,36.15) rot=(0,0,1;0rad)
  Radius = 8.2
FEATURE [Part::MultiFuse] Fusion080  label="removeToCreteHoleForPlugHousing025"
  Placement = pos=(-42,19,36) rot=(0,1,0;1.5708rad)
  Shapes = -> [Cylinder037,Cylinder036]
FEATURE [Sketcher::SketchObject] Sketch050  label="topSketch012"
  FullyConstrained = true
  sketch-geometry (4):
    g0: LineSegment StartX=16.8446 StartY=31.512 StartZ=0 EndX=16.3251 EndY=34.4666 EndZ=0
    g1: ArcOfCircle CenterX=19 CenterY=19.2524 CenterZ=0 NormalX=0 NormalY=0 NormalZ=1 AngleXU=0 Radius=15.4476 StartAngle=1.74483 EndAngle=2.72717
    g2: ArcOfCircle CenterX=19 CenterY=19.2524 CenterZ=0 NormalX=0 NormalY=0 NormalZ=1 AngleXU=0 Radius=12.4476 StartAngle=1.74483 EndAngle=2.73189
    g3: LineSegment StartX=4.86004 StartY=25.4725 StartZ=0 EndX=7.58253 EndY=24.2107 EndZ=0
  constraints (7):
    c: Block(g0)
    c: Coincident(g1,g0)
    c: Coincident(g2,g0)
    c: Coincident(g3,g1)
    c: Coincident(g3,g2)
    c: Block(g1)
    c: Block(g2)
FEATURE [Part::Extrusion] Extrude041
  Base = -> Sketch050
  Dir = (0,0,1)
  DirMode = 2
  FaceMakerClass = Part::FaceMakerBullseye
  LengthFwd = 10.6
  LengthRev = 0
  Placement = pos=(0,0,31) rot=(0,0,1;0rad)
  Solid = true
  Symmetric = false
FEATURE [Part::Cut] Cut035
  Base = -> Extrude041
  Placement = pos=(0,0,-0.3) rot=(0,0,1;0rad)
  Tool = -> Fusion080
FEATURE [Part::Cut] Cut036
  Base = -> Box023
  Tool = -> Cut035
FEATURE [Part::Fillet] Fillet027
  Base = -> Cut036
  Edges = 1 edges r=0.7: [Edge13]
FEATURE [Part::Fillet] Fillet028
  Base = -> Fillet027
  Edges = 1 edges r=0.7: [Edge13]
FEATURE [Part::Fillet] Fillet029
  Base = -> Fillet028
  Edges = 1 edges r=0.7: [Edge16]
FEATURE [Part::Fillet] Fillet030
  Base = -> Fillet029
  Edges = 1 edges r=0.7: [Edge11]
FEATURE [Part::Fillet] Fillet031
  Base = -> Fillet030
  Edges = 1 edges r=0.7: [Edge10]
FEATURE [Part::Fillet] Fillet032
  Base = -> Fillet031
  Edges = 1 edges r=1.2: [Edge5]
FEATURE [Part::Fillet] Fillet033
  Base = -> Fillet032
  Edges = 1 edges r=1.2: [Edge12]
FEATURE [Part::Fillet] Fillet034  label="wireHousingRetainer"
  Base = -> Fillet033
  Edges = 1 edges r=2: [Edge1]
  Placement = pos=(0.3,0,0) rot=(0,0,1;0rad)
FEATURE [Part::Feature] Face099
  shape: bbox 3.5 x 17.8 x 2e-07 mm, 1 faces, 0 solids (baked)
FEATURE [Part::Revolution] Revolve107  label="removeToCreateScrewAndThreadedInsertHole034"
  Angle = 360
  Axis = (0,1,0)
  Base = (0,0,0)
  FaceMakerClass = Part::FaceMakerBullseye
  Placement = pos=(12.5,0,10) rot=(0,0,1;0rad)
  Solid = false
  Source = -> Face099
  Symmetric = false
FEATURE [Part::Feature] Face100
  shape: bbox 3.5 x 17.8 x 2e-07 mm, 1 faces, 0 solids (baked)
FEATURE [Part::Revolution] Revolve108  label="removeToCreateScrewAndThreadedInsertHole035"
  Angle = 360
  Axis = (0,1,0)
  Base = (0,0,0)
  FaceMakerClass = Part::FaceMakerBullseye
  Placement = pos=(12.5,0,62) rot=(0,0,1;0rad)
  Solid = false
  Source = -> Face100
  Symmetric = false
FEATURE [Part::Feature] Face101
  shape: bbox 3.5 x 17.8 x 2e-07 mm, 1 faces, 0 solids (baked)
FEATURE [Part::Revolution] Revolve109  label="removeToCreateScrewAndThreadedInsertHole036"
  Angle = 360
  Axis = (0,1,0)
  Base = (0,0,0)
  FaceMakerClass = Part::FaceMakerBullseye
  Placement = pos=(89.5,0,68.5) rot=(0,0,1;0rad)
  Solid = false
  Source = -> Face101
  Symmetric = false
FEATURE [Part::Feature] Face102
  shape: bbox 3.5 x 17.8 x 2e-07 mm, 1 faces, 0 solids (baked)
FEATURE [Part::Revolution] Revolve110  label="removeToCreateScrewAndThreadedInsertHole037"
  Angle = 360
  Axis = (0,1,0)
  Base = (0,0,0)
  FaceMakerClass = Part::FaceMakerBullseye
  Placement = pos=(89.5,0,3.5) rot=(0,0,1;0rad)
  Solid = false
  Source = -> Face102
  Symmetric = false
FEATURE [Part::Feature] Face103
  shape: bbox 3.5 x 17.8 x 2e-07 mm, 1 faces, 0 solids (baked)
FEATURE [Part::Revolution] Revolve111  label="removeToCreateScrewAndThreadedInsertHole038"
  Angle = 360
  Axis = (0,1,0)
  Base = (0,0,0)
  FaceMakerClass = Part::FaceMakerBullseye
  Placement = pos=(109.5,4.7,3.5) rot=(0,0,1;0rad)
  Solid = false
  Source = -> Face103
  Symmetric = false
FEATURE [Part::Feature] Face104
  shape: bbox 3.5 x 17.8 x 2e-07 mm, 1 faces, 0 solids (baked)
FEATURE [Part::Revolution] Revolve112  label="removeToCreateScrewAndThreadedInsertHole039"
  Angle = 360
  Axis = (0,1,0)
  Base = (0,0,0)
  FaceMakerClass = Part::FaceMakerBullseye
  Placement = pos=(109.5,4.7,68.5) rot=(0,0,1;0rad)
  Solid = false
  Source = -> Face104
  Symmetric = false
FEATURE [Part::MultiFuse] Fusion081  label="removeToCreateScrewAndThreadedInsertHole040"
  Shapes = -> [Revolve107,Revolve108,Revolve109,Revolve110,Revolve111,Revolve112]
FEATURE [Part::MultiFuse] Fusion082  label="casePillars002"
  Shapes = -> [Revolve094,Revolve092,Revolve090,Revolve089,Revolve091,Revolve093]
FEATURE [Part::Cut] Cut037  label="casePillars003"
  Base = -> Fusion082
  Tool = -> Fusion081
FEATURE [Sketcher::SketchObject] Sketch051
  FullyConstrained = true
  Placement = pos=(117,19,0) rot=(0.57735,0.57735,0.57735;2.0944rad)
  sketch-geometry (48):
    g0: LineSegment StartX=-49.19 StartY=69.25 StartZ=0 EndX=-49.19 EndY=66.25 EndZ=0
    g1: LineSegment StartX=-49.19 StartY=63.5 StartZ=0 EndX=-49.19 EndY=60.5 EndZ=0
    g2: LineSegment StartX=-49.19 StartY=57.75 StartZ=0 EndX=-49.19 EndY=54.75 EndZ=0
    g3: LineSegment StartX=-49.19 StartY=52 StartZ=0 EndX=-49.19 EndY=49 EndZ=0
    g4: LineSegment StartX=-49.19 StartY=46.25 StartZ=0 EndX=-49.19 EndY=43.25 EndZ=0
    g5: LineSegment StartX=-49.19 StartY=40.5 StartZ=0 EndX=-49.19 EndY=37.5 EndZ=0
    g6: LineSegment StartX=-49.19 StartY=34.5 StartZ=0 EndX=-49.19 EndY=31.5 EndZ=0
    g7: LineSegment StartX=-49.19 StartY=28.75 StartZ=0 EndX=-49.19 EndY=25.75 EndZ=0
    g8: LineSegment StartX=-49.19 StartY=23 StartZ=0 EndX=-49.19 EndY=20 EndZ=0
    g9: LineSegment StartX=-49.19 StartY=17.25 StartZ=0 EndX=-49.19 EndY=14.25 EndZ=0
    g10: LineSegment StartX=-49.19 StartY=11.5 StartZ=0 EndX=-49.19 EndY=8.5 EndZ=0
    g11: LineSegment StartX=-49.19 StartY=5.75 StartZ=0 EndX=-49.19 EndY=2.75 EndZ=0
    g12: ArcOfCircle CenterX=-1.5 CenterY=67.75 CenterZ=0 NormalX=0 NormalY=0 NormalZ=1 AngleXU=0 Radius=1.5 StartAngle=4.71239 EndAngle=7.85398
    g13: ArcOfCircle CenterX=-1.5 CenterY=62 CenterZ=0 NormalX=0 NormalY=0 NormalZ=1 AngleXU=0 Radius=1.5 StartAngle=4.71239 EndAngle=7.85398
    g14: ArcOfCircle CenterX=-1.5 CenterY=56.25 CenterZ=0 NormalX=0 NormalY=0 NormalZ=1 AngleXU=0 Radius=1.5 StartAngle=4.71239 EndAngle=7.85398
    g15: ArcOfCircle CenterX=-11.49 CenterY=50.5 CenterZ=0 NormalX=0 NormalY=0 NormalZ=1 AngleXU=0 Radius=1.5 StartAngle=4.71239 EndAngle=7.85398
    g16: ArcOfCircle CenterX=-16.28 CenterY=44.75 CenterZ=0 NormalX=0 NormalY=0 NormalZ=1 AngleXU=0 Radius=1.5 StartAngle=4.71239 EndAngle=7.85398
    g17: ArcOfCircle CenterX=-18.2337 CenterY=39 CenterZ=0 NormalX=0 NormalY=0 NormalZ=1 AngleXU=0 Radius=1.5 StartAngle=4.71485 EndAngle=7.85398
    g18: ArcOfCircle CenterX=-16.2837 CenterY=27.25 CenterZ=0 NormalX=0 NormalY=0 NormalZ=1 AngleXU=0 Radius=1.5 StartAngle=4.71485 EndAngle=7.85398
    g19: ArcOfCircle CenterX=-18.2337 CenterY=33 CenterZ=0 NormalX=0 NormalY=0 NormalZ=1 AngleXU=0 Radius=1.5 StartAngle=4.71485 EndAngle=7.85398
    g20: ArcOfCircle CenterX=-11.49 CenterY=21.5 CenterZ=0 NormalX=0 NormalY=0 NormalZ=1 AngleXU=0 Radius=1.5 StartAngle=4.71239 EndAngle=7.85398
    g21: ArcOfCircle CenterX=-1.5 CenterY=4.25 CenterZ=0 NormalX=0 NormalY=0 NormalZ=1 AngleXU=0 Radius=1.5 StartAngle=4.71239 EndAngle=7.85398
    g22: ArcOfCircle CenterX=-1.5 CenterY=10 CenterZ=0 NormalX=0 NormalY=0 NormalZ=1 AngleXU=0 Radius=1.5 StartAngle=4.71239 EndAngle=7.85398
    g23: ArcOfCircle CenterX=-1.5 CenterY=15.75 CenterZ=0 NormalX=0 NormalY=0 NormalZ=1 AngleXU=0 Radius=1.5 StartAngle=4.71239 EndAngle=7.85398
    g24: LineSegment StartX=-49.19 StartY=69.25 StartZ=0 EndX=-1.5 EndY=69.25 EndZ=0
    g25: LineSegment StartX=-49.19 StartY=66.25 StartZ=0 EndX=-1.5 EndY=66.25 EndZ=0
    g26: LineSegment StartX=-49.19 StartY=63.5 StartZ=0 EndX=-1.5 EndY=63.5 EndZ=0
    g27: LineSegment StartX=-49.19 StartY=60.5 StartZ=0 EndX=-1.5 EndY=60.5 EndZ=0
    g28: LineSegment StartX=-49.19 StartY=57.75 StartZ=0 EndX=-1.5 EndY=57.75 EndZ=0
    g29: LineSegment StartX=-49.19 StartY=54.75 StartZ=0 EndX=-1.5 EndY=54.75 EndZ=0
    g30: LineSegment StartX=-49.19 StartY=52 StartZ=0 EndX=-11.49 EndY=52 EndZ=0
    g31: LineSegment StartX=-49.19 StartY=49 StartZ=0 EndX=-11.49 EndY=49 EndZ=0
    g32: LineSegment StartX=-49.19 StartY=46.25 StartZ=0 EndX=-16.28 EndY=46.25 EndZ=0
    g33: LineSegment StartX=-49.19 StartY=43.25 StartZ=0 EndX=-16.28 EndY=43.25 EndZ=0
    g34: LineSegment StartX=-49.19 StartY=40.5 StartZ=0 EndX=-18.2337 EndY=40.5 EndZ=0
    g35: LineSegment StartX=-49.19 StartY=37.5 StartZ=0 EndX=-18.23 EndY=37.5 EndZ=0
    g36: LineSegment StartX=-49.19 StartY=34.5 StartZ=0 EndX=-18.2337 EndY=34.5 EndZ=0
    g37: LineSegment StartX=-49.19 StartY=31.5 StartZ=0 EndX=-18.23 EndY=31.5 EndZ=0
    g38: LineSegment StartX=-49.19 StartY=28.75 StartZ=0 EndX=-16.2837 EndY=28.75 EndZ=0
    g39: LineSegment StartX=-49.19 StartY=25.75 StartZ=0 EndX=-16.28 EndY=25.75 EndZ=0
    g40: LineSegment StartX=-49.19 StartY=23 StartZ=0 EndX=-11.49 EndY=23 EndZ=0
    g41: LineSegment StartX=-49.19 StartY=20 StartZ=0 EndX=-11.49 EndY=20 EndZ=0
    g42: LineSegment StartX=-49.19 StartY=17.25 StartZ=0 EndX=-1.5 EndY=17.25 EndZ=0
    g43: LineSegment StartX=-49.19 StartY=14.25 StartZ=0 EndX=-1.5 EndY=14.25 EndZ=0
    g44: LineSegment StartX=-49.19 StartY=11.5 StartZ=0 EndX=-1.5 EndY=11.5 EndZ=0
    g45: LineSegment StartX=-49.19 StartY=8.5 StartZ=0 EndX=-1.5 EndY=8.5 EndZ=0
    g46: LineSegment StartX=-49.19 StartY=5.75 StartZ=0 EndX=-1.5 EndY=5.75 EndZ=0
    g47: LineSegment StartX=-49.19 StartY=2.75 StartZ=0 EndX=-1.5 EndY=2.75 EndZ=0
  constraints (120):
    c: Vertical(g0)
    c: Distance(g0) = 3
    c: Block(g0)
    c: Vertical(g1)
    c: Distance(g1) = 3
    c: Vertical(g2)
    c: Equal(g0,g2) = 3
    c: Block(g2)
    c: Vertical(g3)
    c: Equal(g1,g3) = 3
    c: Vertical(g4)
    c: Equal(g0,g4) = 3
    c: Block(g4)
    c: Vertical(g5)
    c: Equal(g1,g5) = 3
    c: Vertical(g6)
    c: Equal(g0,g6) = 3
    c: Block(g6)
    c: Vertical(g7)
    c: Equal(g1,g7) = 3
    c: Vertical(g8)
    c: Equal(g0,g8) = 3
    c: Block(g8)
    c: Vertical(g9)
    c: Equal(g1,g9) = 3
    c: Vertical(g10)
    c: Equal(g0,g10) = 3
    c: Block(g10)
    c: Vertical(g11)
    c: Equal(g1,g11) = 3
    c: Block(g12)
    c: Block(g13)
    c: Block(g14)
    c: Block(g15)
    c: Block(g16)
    c: Block(g17)
    c: Block(g18)
    c: Block(g19)
    c: Block(g20)
    c: Block(g21)
    c: Block(g22)
    c: Block(g23)
    c: Block(g11)
    c: Block(g9)
    c: Block(g7)
    c: Block(g5)
    c: Block(g3)
    c: Block(g1)
    c: Coincident(g24,g0)
    c: Coincident(g24,g12)
    c: Horizontal(g24)
    c: Coincident(g25,g0)
    c: Coincident(g25,g12)
    c: Horizontal(g25)
    c: Coincident(g26,g1)
    c: Coincident(g26,g13)
    c: Horizontal(g26)
    c: Coincident(g27,g1)
    c: Coincident(g27,g13)
    c: Horizontal(g27)
    c: Coincident(g28,g2)
    c: Coincident(g28,g14)
    c: Horizontal(g28)
    c: Coincident(g29,g2)
    c: Coincident(g29,g14)
    c: Horizontal(g29)
    c: Coincident(g30,g3)
    c: Coincident(g30,g15)
    c: Horizontal(g30)
    c: Coincident(g31,g3)
    c: Coincident(g31,g15)
    c: Horizontal(g31)
    c: Coincident(g32,g4)
    c: Coincident(g32,g16)
    c: Horizontal(g32)
    c: Coincident(g33,g4)
    c: Coincident(g33,g16)
    c: Horizontal(g33)
    c: Coincident(g34,g5)
    c: Coincident(g34,g17)
    c: Horizontal(g34)
    c: Coincident(g35,g5)
    c: Coincident(g35,g17)
    c: Horizontal(g35)
    c: Coincident(g36,g6)
    c: Coincident(g36,g19)
    c: Horizontal(g36)
    c: Coincident(g37,g6)
    c: Coincident(g37,g19)
    c: Horizontal(g37)
    c: Coincident(g38,g7)
    c: Coincident(g38,g18)
    c: Horizontal(g38)
    c: Coincident(g39,g7)
    c: Coincident(g39,g18)
    c: Horizontal(g39)
    c: Coincident(g40,g8)
    c: Coincident(g40,g20)
    c: Horizontal(g40)
    c: Coincident(g41,g8)
    c: Coincident(g41,g20)
    c: Horizontal(g41)
    c: Coincident(g42,g9)
    c: Coincident(g42,g23)
    c: Horizontal(g42)
    c: Coincident(g43,g9)
    c: Coincident(g43,g23)
    c: Horizontal(g43)
    c: Coincident(g44,g10)
    c: Coincident(g44,g22)
    c: Horizontal(g44)
    c: Coincident(g45,g10)
    c: Coincident(g45,g22)
    c: Horizontal(g45)
    c: Coincident(g46,g11)
    c: Coincident(g46,g21)
    c: Horizontal(g46)
    c: Coincident(g47,g11)
    c: Coincident(g47,g21)
    c: Horizontal(g47)
FEATURE [Part::Extrusion] Extrude042
  Base = -> Sketch051
  Dir = (1,-2e-16,2e-16)
  DirMode = 2
  FaceMakerClass = Part::FaceMakerBullseye
  LengthFwd = 19
  LengthRev = 0
  Placement = pos=(-19,0,0) rot=(0,0,1;0rad)
  Solid = true
  Symmetric = false
FEATURE [Part::Fillet] Fillet035  label="removeToCreateVentalationHoles"
  Base = -> Extrude042
  Edges = <same value as first occurrence — deduplicated (x6 in doc)>
  Placement = pos=(7,0,0) rot=(0,0,1;0rad)
FEATURE [Part::Cut] Cut038  label="top017"
  Base = -> Cut033
  Tool = -> Fillet035
FEATURE [Sketcher::SketchObject] Sketch052  label="bottomSketch001"
  FullyConstrained = true
  sketch-geometry (45):
    g0: LineSegment StartX=6.29999 StartY=8 StartZ=0 EndX=3.29999 EndY=8 EndZ=0
    g1: LineSegment StartX=3.29999 StartY=8 StartZ=0 EndX=3.29999 EndY=-6.03275e-07 EndZ=0
    g2: ArcOfCircle CenterX=8.29999 CenterY=5 CenterZ=0 NormalX=0 NormalY=0 NormalZ=1 AngleXU=0 Radius=2 StartAngle=3.14159 EndAngle=4.71239
    g3: LineSegment StartX=6.29999 StartY=8 StartZ=0 EndX=6.29999 EndY=5 EndZ=0
    g4: ArcOfCircle CenterX=105 CenterY=19 CenterZ=0 NormalX=0 NormalY=0 NormalZ=1 AngleXU=0 Radius=12.7 StartAngle=4.71239 EndAngle=5.94289
    g5-g11: Circle x7 (B-spline internal-alignment scaffolding for g12; pole/knot coordinates omitted)
    g12: BSplineCurve PolesCount=7 KnotsCount=5 Degree=3 IsPeriodic=0
    g13-g17: GeomPoint x5 (B-spline internal-alignment scaffolding for g12; pole/knot coordinates omitted)
    g18: ArcOfCircle CenterX=105 CenterY=19 CenterZ=0 NormalX=0 NormalY=0 NormalZ=1 AngleXU=0 Radius=15.7 StartAngle=5.81226 EndAngle=6.28319
    g19: BSplineCurve PolesCount=5 KnotsCount=3 Degree=3 IsPeriodic=0
    g20: LineSegment StartX=8.29999 StartY=3 StartZ=0 EndX=101.7 EndY=3 EndZ=0
    g21: LineSegment StartX=3.29999 StartY=-6.03275e-07 StartZ=0 EndX=105 EndY=-6.03275e-07 EndZ=0
    g22: LineSegment StartX=120.974 StartY=8.71251 StartZ=0 EndX=122.332 EndY=7.83778 EndZ=0
    g23: LineSegment StartX=105 StartY=-6.03274e-07 StartZ=0 EndX=113 EndY=-6.03274e-07 EndZ=0
    g24: ArcOfCircle CenterX=105 CenterY=19 CenterZ=0 NormalX=0 NormalY=0 NormalZ=1 AngleXU=0 Radius=20.6155 StartAngle=5.11091 EndAngle=5.71103
    g25: ArcOfCircle CenterX=117.7 CenterY=19 CenterZ=0 NormalX=0 NormalY=0 NormalZ=1 AngleXU=0 Radius=3 StartAngle=1.2e-15 EndAngle=2.10468
    g26: Circle CenterX=116.345 CenterY=16.3232 CenterZ=0 NormalX=0 NormalY=0 NormalZ=1 AngleXU=0 Radius=1
    g27: Circle CenterX=117.24 CenterY=15.7584 CenterZ=0 NormalX=0 NormalY=0 NormalZ=1 AngleXU=0 Radius=1
    g28: Circle CenterX=116.972 CenterY=14.7612 CenterZ=0 NormalX=0 NormalY=0 NormalZ=1 AngleXU=0 Radius=1
    g29: BSplineCurve PolesCount=3 KnotsCount=2 Degree=2 IsPeriodic=0
    g30: GeomPoint X=116.345 Y=16.3232 Z=0
    g31: GeomPoint X=116.972 Y=14.7612 Z=0
    g32: Circle CenterX=115.828 CenterY=17.157 CenterZ=0 NormalX=0 NormalY=0 NormalZ=1 AngleXU=0 Radius=1
    g33: Circle CenterX=115.841 CenterY=16.639 CenterZ=0 NormalX=0 NormalY=0 NormalZ=1 AngleXU=0 Radius=1
    g34: Circle CenterX=116.345 CenterY=16.3232 CenterZ=0 NormalX=0 NormalY=0 NormalZ=1 AngleXU=0 Radius=1
    g35: BSplineCurve PolesCount=3 KnotsCount=2 Degree=2 IsPeriodic=0
    g36: GeomPoint X=115.828 Y=17.157 Z=0
    g37: GeomPoint X=116.345 Y=16.3232 Z=0
    g38: LineSegment StartX=115.828 StartY=17.157 StartZ=0 EndX=115.828 EndY=20.8307 EndZ=0
    g39: Circle CenterX=115.828 CenterY=20.8307 CenterZ=0 NormalX=0 NormalY=0 NormalZ=1 AngleXU=0 Radius=1
    g40: Circle CenterX=115.831 CenterY=21.3396 CenterZ=0 NormalX=0 NormalY=0 NormalZ=1 AngleXU=0 Radius=1
    g41: Circle CenterX=116.173 CenterY=21.5825 CenterZ=0 NormalX=0 NormalY=0 NormalZ=1 AngleXU=0 Radius=1
    g42: BSplineCurve PolesCount=3 KnotsCount=2 Degree=2 IsPeriodic=0
    g43: GeomPoint X=115.828 Y=20.8307 Z=0
    g44: GeomPoint X=116.173 Y=21.5825 Z=0
  constraints (70):
    c: Horizontal(g0)
    c: Distance(g0) = 3
    c: Coincident(g1,g0)
    c: Vertical(g1)
    c: Block(g2)
    c: Block(g0)
    c: Coincident(g3,g0)
    c: Coincident(g3,g2)
    c: Vertical(g3)
    c: Block(g1)
    c: Block(g4)
    c: Coincident(g19,g4)
    c: Block(g19)
    c: Equal(g5, g6-g11) x6
    c: InternalAlignment(g5-g11 -> g12) x7
    c: InternalAlignment(g13-g17 -> g12) x5
    c: Block(g12)
    c: Coincident(g18,g12)
    c: Block(g18)
    c: Coincident(g20,g2)
    c: Coincident(g20,g19)
    c: Horizontal(g20)
    c: Distance(g20) = 93.4
    c: Coincident(g21,g1)
    c: Horizontal(g21)
    c: Distance(g21) = 101.7
    c: Horizontal(g23)
    c: Distance(g23) = 8
    c: Coincident(g24,g23)
    c: Block(g23)
    c: Coincident(g22,g24)
    c: Block(g24)
    c: Block(g22)
    c: Distance(g22) = 1.61553
    c: Coincident(g25,g18)
    c: Block(g25)
    c: Weight(g26) = 1
    c: Equal(g26,g27)
    c: Equal(g26,g28)
    c: Coincident(g29,g4)
    c: InternalAlignment(g26,g29)
    c: InternalAlignment(g27,g29)
    c: InternalAlignment(g28,g29)
    c: InternalAlignment(g30,g29)
    c: InternalAlignment(g31,g29)
    c: Block(g29)
    c: Weight(g32) = 1
    c: Equal(g32,g33)
    c: Equal(g32,g34)
    c: Coincident(g35,g29)
    c: InternalAlignment(g32,g35)
    c: InternalAlignment(g33,g35)
    c: InternalAlignment(g34,g35)
    c: InternalAlignment(g36,g35)
    c: InternalAlignment(g37,g35)
    c: Block(g35)
    c: Coincident(g38,g35)
    c: Vertical(g38)
    c: Block(g38)
    c: Coincident(g42,g38)
    c: Weight(g39) = 1
    c: Equal(g39,g40)
    c: Equal(g39,g41)
    c: Coincident(g42,g25)
    c: InternalAlignment(g39,g42)
    c: InternalAlignment(g40,g42)
    c: InternalAlignment(g41,g42)
    c: InternalAlignment(g43,g42)
    c: InternalAlignment(g44,g42)
    c: Block(g42)
FEATURE [Part::Extrusion] Extrude043  label="bottom010"
  Base = -> Sketch052
  Dir = (0,0,1)
  DirMode = 2
  FaceMakerClass = Part::FaceMakerBullseye
  LengthFwd = 71.4
  LengthRev = 0
  Placement = pos=(0,0,0.3) rot=(0,0,1;0rad)
  Solid = true
  Symmetric = false
FEATURE [Sketcher::SketchObject] Sketch053  label="topSketch013"
  FullyConstrained = true
  sketch-geometry (22):
    g0: LineSegment StartX=5.21097e-06 StartY=3 StartZ=0 EndX=5.21097e-06 EndY=19 EndZ=0
    g1: ArcOfCircle CenterX=19 CenterY=19 CenterZ=0 NormalX=0 NormalY=0 NormalZ=1 AngleXU=0 Radius=19 StartAngle=1.5708 EndAngle=3.14159
    g2: ArcOfCircle CenterX=19 CenterY=19 CenterZ=0 NormalX=0 NormalY=0 NormalZ=1 AngleXU=0 Radius=16 StartAngle=1.5708 EndAngle=3.14159
    g3: LineSegment StartX=114 StartY=35 StartZ=0 EndX=19 EndY=35 EndZ=0
    g4: LineSegment StartX=5.21097e-06 StartY=3 StartZ=0 EndX=5.21097e-06 EndY=0 EndZ=0
    g5: LineSegment StartX=3 StartY=0 StartZ=0 EndX=5.21097e-06 EndY=0 EndZ=0
    g6: LineSegment StartX=3 StartY=19 StartZ=0 EndX=3 EndY=0 EndZ=0
    g7: LineSegment StartX=19 StartY=38 StartZ=0 EndX=124 EndY=38 EndZ=0
    g8: Circle CenterX=119 CenterY=35 CenterZ=0 NormalX=0 NormalY=0 NormalZ=1 AngleXU=0 Radius=1
    g9: Circle CenterX=121 CenterY=35 CenterZ=0 NormalX=0 NormalY=0 NormalZ=1 AngleXU=0 Radius=1
    g10: Circle CenterX=121 CenterY=33 CenterZ=0 NormalX=0 NormalY=0 NormalZ=1 AngleXU=0 Radius=1
    g11: BSplineCurve PolesCount=3 KnotsCount=2 Degree=2 IsPeriodic=0
    g12: GeomPoint X=119 Y=35 Z=0
    g13: GeomPoint X=121 Y=33 Z=0
    g14: LineSegment StartX=119 StartY=35 StartZ=0 EndX=114 EndY=35 EndZ=0
    g15: ArcOfCircle CenterX=105 CenterY=19 CenterZ=0 NormalX=0 NormalY=0 NormalZ=1 AngleXU=0 Radius=16 StartAngle=5.60905 EndAngle=6.28319
    g16: LineSegment StartX=121 StartY=33 StartZ=0 EndX=121 EndY=19 EndZ=0
    g17: LineSegment StartX=117.5 StartY=9.01251 StartZ=0 EndX=121.163 EndY=9.0125 EndZ=0
    g18: ArcOfCircle CenterX=105 CenterY=19 CenterZ=0 NormalX=0 NormalY=0 NormalZ=1 AngleXU=0 Radius=20.6155 StartAngle=5.7297 EndAngle=6.28319
    g19: LineSegment StartX=121.163 StartY=9.0125 StartZ=0 EndX=122.538 EndY=8.16329 EndZ=0
    g20: LineSegment StartX=124 StartY=38 StartZ=0 EndX=125.616 EndY=38 EndZ=0
    g21: LineSegment StartX=125.616 StartY=19 StartZ=0 EndX=125.616 EndY=38 EndZ=0
  constraints (50):
    c: Vertical(g0)
    c: Block(g0)
    c: Coincident(g1,g0)
    c: Block(g1)
    c: Coincident(g2,g1)
    c: Block(g2)
    c: Coincident(g3,g2)
    c: Horizontal(g3)
    c: Tangent(g3,g2)
    c: Coincident(g4,g0)
    c: Distance(g4) = 3
    c: Vertical(g4)
    c: Coincident(g5,g4)
    c: Horizontal(g5)
    c: Coincident(g6,g2)
    c: Coincident(g6,g5)
    c: Vertical(g6)
    c: Horizontal(g7)
    c: Distance(g7) = 105
    c: Coincident(g7,g1)
    c: Block(g3)
    c: Weight(g8) = 1
    c: Equal(g8,g9)
    c: Equal(g8,g10)
    c: InternalAlignment(g8,g11)
    c: InternalAlignment(g9,g11)
    c: InternalAlignment(g10,g11)
    c: InternalAlignment(g12,g11)
    c: InternalAlignment(g13,g11)
    c: Block(g11)
    c: Coincident(g14,g11)
    c: Coincident(g14,g3)
    c: Horizontal(g14)
    c: Block(g15)
    c: Coincident(g16,g11)
    c: Coincident(g16,g15)
    c: Vertical(g16)
    c: Distance(g16) = 14
    c: Coincident(g17,g15)
    c: Block(g18)
    c: Coincident(g19,g18)
    c: Coincident(g20,g7)
    c: Horizontal(g20)
    c: Vertical(g21)
    c: Coincident(g20,g21)
    c: Block(g20)
    c: Block(g21)
    c: Block(g19)
    c: Block(g17)
    c: Distance(g20) = 1.61553
FEATURE [Part::Extrusion] Extrude044
  Base = -> Sketch053
  Dir = (0,0,1)
  DirMode = 2
  FaceMakerClass = Part::FaceMakerBullseye
  LengthFwd = 72
  LengthRev = 0
  Solid = true
  Symmetric = false
FEATURE [Part::Fillet] Fillet036  label="top018"
  Base = -> Extrude044
  Edges = 1 edges r=2: [Edge41]
FEATURE [Sketcher::SketchObject] Sketch054
  FullyConstrained = false
  Placement = pos=(0,0,0) rot=(1,0,0;1.5708rad)
  sketch-geometry (24):
    g0: ArcOfCircle CenterX=-4 CenterY=-10.5 CenterZ=0 NormalX=0 NormalY=0 NormalZ=1 AngleXU=0 Radius=1.5 StartAngle=6e-16 EndAngle=3.14159
    g1: ArcOfCircle CenterX=-34.2 CenterY=-10.5 CenterZ=0 NormalX=0 NormalY=0 NormalZ=1 AngleXU=0 Radius=1.5 StartAngle=0 EndAngle=3.14159
    g2: ArcOfCircle CenterX=-34.2 CenterY=-27.7 CenterZ=0 NormalX=0 NormalY=0 NormalZ=1 AngleXU=0 Radius=1.5 StartAngle=3.14159 EndAngle=6.28319
    g3: ArcOfCircle CenterX=-4 CenterY=-27.7 CenterZ=0 NormalX=0 NormalY=0 NormalZ=1 AngleXU=0 Radius=1.5 StartAngle=3.1416 EndAngle=6.28319
    g4: ArcOfCircle CenterX=-10 CenterY=-4.3 CenterZ=0 NormalX=0 NormalY=0 NormalZ=1 AngleXU=0 Radius=1.5 StartAngle=2e-16 EndAngle=3.14159
    g5: ArcOfCircle CenterX=-16.1 CenterY=-1.8 CenterZ=0 NormalX=0 NormalY=0 NormalZ=1 AngleXU=0 Radius=1.5 StartAngle=5e-16 EndAngle=3.14159
    g6: ArcOfCircle CenterX=-22.1 CenterY=-1.8 CenterZ=0 NormalX=0 NormalY=0 NormalZ=1 AngleXU=0 Radius=1.5 StartAngle=5e-16 EndAngle=3.14159
    g7: ArcOfCircle CenterX=-28.2 CenterY=-4.3 CenterZ=0 NormalX=0 NormalY=0 NormalZ=1 AngleXU=0 Radius=1.5 StartAngle=2e-16 EndAngle=3.14159
    g8: ArcOfCircle CenterX=-10 CenterY=-33.9 CenterZ=0 NormalX=0 NormalY=0 NormalZ=1 AngleXU=0 Radius=1.5 StartAngle=3.14159 EndAngle=6.28319
    g9: ArcOfCircle CenterX=-16.1 CenterY=-36.4 CenterZ=0 NormalX=0 NormalY=0 NormalZ=1 AngleXU=0 Radius=1.5 StartAngle=3.14159 EndAngle=6.28319
    g10: ArcOfCircle CenterX=-22.1 CenterY=-36.4 CenterZ=0 NormalX=0 NormalY=0 NormalZ=1 AngleXU=0 Radius=1.5 StartAngle=3.14159 EndAngle=6.28319
    g11: ArcOfCircle CenterX=-28.2 CenterY=-33.9 CenterZ=0 NormalX=0 NormalY=0 NormalZ=1 AngleXU=0 Radius=1.5 StartAngle=3.14159 EndAngle=6.28319
    g12: LineSegment StartX=-35.7 StartY=-10.5 StartZ=0 EndX=-35.7 EndY=-27.7 EndZ=0
    g13: LineSegment StartX=-32.7 StartY=-10.5 StartZ=0 EndX=-32.7 EndY=-27.7 EndZ=0
    g14: LineSegment StartX=-29.7 StartY=-33.9 StartZ=0 EndX=-29.7 EndY=-4.3 EndZ=0
    g15: LineSegment StartX=-26.7 StartY=-33.9 StartZ=0 EndX=-26.7 EndY=-4.3 EndZ=0
    g16: LineSegment StartX=-2.5 StartY=-10.5 StartZ=0 EndX=-2.5 EndY=-27.7 EndZ=0
    g17: LineSegment StartX=-8.5 StartY=-4.3 StartZ=0 EndX=-8.5 EndY=-33.9 EndZ=0
    g18: LineSegment StartX=-5.5 StartY=-10.5 StartZ=0 EndX=-5.5 EndY=-27.7 EndZ=0
    g19: LineSegment StartX=-11.5 StartY=-4.3 StartZ=0 EndX=-11.5 EndY=-33.9 EndZ=0
    g20: LineSegment StartX=-14.6 StartY=-1.8 StartZ=0 EndX=-14.6 EndY=-36.4 EndZ=0
    g21: LineSegment StartX=-17.6 StartY=-1.8 StartZ=0 EndX=-17.6 EndY=-36.4 EndZ=0
    g22: LineSegment StartX=-20.6 StartY=-36.4 StartZ=0 EndX=-20.6 EndY=-1.8 EndZ=0
    g23: LineSegment StartX=-23.6 StartY=-1.8 StartZ=0 EndX=-23.6 EndY=-36.4 EndZ=0
  constraints (48):
    c: Block(g0)
    c: Block(g1)
    c: Block(g2)
    c: Block(g3)
    c: Block(g4)
    c: Block(g5)
    c: Block(g6)
    c: Block(g7)
    c: Block(g8)
    c: Block(g9)
    c: Block(g10)
    c: Block(g11)
    c: Coincident(g12,g1)
    c: Coincident(g12,g2)
    c: Vertical(g12)
    c: Coincident(g13,g1)
    c: Coincident(g13,g2)
    c: Vertical(g13)
    c: Coincident(g14,g11)
    c: Coincident(g14,g7)
    c: Vertical(g14)
    c: Coincident(g15,g11)
    c: Coincident(g15,g7)
    c: Vertical(g15)
    c: Coincident(g16,g0)
    c: Coincident(g16,g3)
    c: Vertical(g16)
    c: Coincident(g17,g4)
    c: Coincident(g17,g8)
    c: Vertical(g17)
    c: Coincident(g18,g0)
    c: Coincident(g18,g3)
    c: Vertical(g18)
    c: Coincident(g19,g4)
    c: Coincident(g19,g8)
    c: Vertical(g19)
    c: Coincident(g20,g5)
    c: Coincident(g20,g9)
    c: Vertical(g20)
    c: Coincident(g21,g5)
    c: Coincident(g21,g9)
    c: Vertical(g21)
    c: Coincident(g22,g10)
    c: Coincident(g22,g6)
    c: Vertical(g22)
    c: Coincident(g23,g6)
    c: Coincident(g23,g10)
    c: Vertical(g23)
FEATURE [Part::Extrusion] Extrude045  label="removeToCreateFanGrillHoles003"
  Base = -> Sketch054
  Dir = (0,-1,6e-16)
  DirMode = 2
  FaceMakerClass = Part::FaceMakerBullseye
  LengthFwd = 10
  LengthRev = 0
  Placement = pos=(65.4,44,54.82) rot=(0,0,1;0rad)
  Solid = true
  Symmetric = false
FEATURE [Part::Feature] Face105 .. Face108  x4 (patterned run collapsed; names and placements below)
  shape: bbox 3.5 x 17.8 x 2e-07 mm, 1 faces, 0 solids (baked)
FEATURE [Part::Revolution] Revolve113  label="removeToCreateScrewAndThreadedInsertHole041"
  Angle = 360
  Axis = (0,1,0)
  Base = (0,0,0)
  FaceMakerClass = Part::FaceMakerBullseye
  Placement = pos=(62.3,30.3,19.7) rot=(0,0,1;0rad)
  Solid = false
  Source = -> Face105
  Symmetric = false
FEATURE [Part::Revolution] Revolve114  label="removeToCreateScrewAndThreadedInsertHole042"
  Angle = 360
  Axis = (0,1,0)
  Base = (0,0,0)
  FaceMakerClass = Part::FaceMakerBullseye
  Placement = pos=(62.3,30.3,51.7) rot=(0,0,1;0rad)
  Solid = false
  Source = -> Face106
  Symmetric = false
FEATURE [Part::Revolution] Revolve115  label="removeToCreateScrewAndThreadedInsertHole043"
  Angle = 360
  Axis = (0,1,0)
  Base = (0,0,0)
  FaceMakerClass = Part::FaceMakerBullseye
  Placement = pos=(30.3,30.3,19.7) rot=(0,0,1;0rad)
  Solid = false
  Source = -> Face107
  Symmetric = false
FEATURE [Part::Revolution] Revolve116  label="removeToCreateScrewAndThreadedInsertHole044"
  Angle = 360
  Axis = (0,1,0)
  Base = (0,0,0)
  FaceMakerClass = Part::FaceMakerBullseye
  Placement = pos=(30.3,30.3,51.7) rot=(0,0,1;0rad)
  Solid = false
  Source = -> Face108
  Symmetric = false
FEATURE [Part::MultiFuse] Fusion083  label="createThreadedInsertHolesForFan004"
  Shapes = -> [Revolve113,Revolve114,Revolve115,Revolve116]
FEATURE [Part::Box] Box024  label="removeToCreteHoleForPlugHousing026"
  AttacherType = Attacher::AttachEngine3D
  Height = 28.6
  Length = 10
  Placement = pos=(-2,0,21.7) rot=(0,0,1;0rad)
  Width = 19
FEATURE [Part::Cylinder] Cylinder038  label="removeToCreteHoleForPlugHousing027"
  Angle = 360
  AttacherType = Attacher::AttachEngine3D
  Height = 20
  Placement = pos=(-2,19,36) rot=(0,1,0;1.5708rad)
  Radius = 14.3
FEATURE [Part::MultiFuse] Fusion084  label="removeToCreteHoleForPlugHousing028"
  Shapes = -> [Box024,Cylinder038]
FEATURE [Part::Cylinder] Cylinder039
  Angle = 360
  AttacherType = Attacher::AttachEngine3D
  Height = 20
  Placement = pos=(0,0,36.15) rot=(0,0,1;0rad)
  Radius = 14.3
FEATURE [Part::Cylinder] Cylinder040
  Angle = 360
  AttacherType = Attacher::AttachEngine3D
  Height = 10
  Placement = pos=(0,0,36.15) rot=(0,0,1;0rad)
  Radius = 4
FEATURE [Part::Box] Box025  label="removeToCreteHoleForPlugHousing030"
  AttacherType = Attacher::AttachEngine3D
  Height = 28.6
  Length = 20
  Placement = pos=(106.15,0,21.7) rot=(0,0,1;0rad)
  Width = 19
FEATURE [Part::MultiFuse] Fusion086  label="removeToCreteHoleForPlugHousing031"
  Placement = pos=(70,19,36) rot=(0,1,0;1.5708rad)
  Shapes = -> [Cylinder039,Cylinder040]
FEATURE [Part::MultiFuse] Fusion085  label="removeToCreteHoleForPlugHousing029"
  Shapes = -> [Box025,Fusion086]
FEATURE [Sketcher::SketchObject] Sketch055
  FullyConstrained = true
  Placement = pos=(117,19,0) rot=(0.57735,0.57735,0.57735;2.0944rad)
  sketch-geometry (48):
    g0: LineSegment StartX=-49.19 StartY=69.25 StartZ=0 EndX=-49.19 EndY=66.25 EndZ=0
    g1: LineSegment StartX=-49.19 StartY=63.5 StartZ=0 EndX=-49.19 EndY=60.5 EndZ=0
    g2: LineSegment StartX=-49.19 StartY=57.75 StartZ=0 EndX=-49.19 EndY=54.75 EndZ=0
    g3: LineSegment StartX=-49.19 StartY=52 StartZ=0 EndX=-49.19 EndY=49 EndZ=0
    g4: LineSegment StartX=-49.19 StartY=46.25 StartZ=0 EndX=-49.19 EndY=43.25 EndZ=0
    g5: LineSegment StartX=-49.19 StartY=40.5 StartZ=0 EndX=-49.19 EndY=37.5 EndZ=0
    g6: LineSegment StartX=-49.19 StartY=34.5 StartZ=0 EndX=-49.19 EndY=31.5 EndZ=0
    g7: LineSegment StartX=-49.19 StartY=28.75 StartZ=0 EndX=-49.19 EndY=25.75 EndZ=0
    g8: LineSegment StartX=-49.19 StartY=23 StartZ=0 EndX=-49.19 EndY=20 EndZ=0
    g9: LineSegment StartX=-49.19 StartY=17.25 StartZ=0 EndX=-49.19 EndY=14.25 EndZ=0
    g10: LineSegment StartX=-49.19 StartY=11.5 StartZ=0 EndX=-49.19 EndY=8.5 EndZ=0
    g11: LineSegment StartX=-49.19 StartY=5.75 StartZ=0 EndX=-49.19 EndY=2.75 EndZ=0
    g12: ArcOfCircle CenterX=-1.5 CenterY=67.75 CenterZ=0 NormalX=0 NormalY=0 NormalZ=1 AngleXU=0 Radius=1.5 StartAngle=4.71239 EndAngle=7.85398
    g13: ArcOfCircle CenterX=-1.5 CenterY=62 CenterZ=0 NormalX=0 NormalY=0 NormalZ=1 AngleXU=0 Radius=1.5 StartAngle=4.71239 EndAngle=7.85398
    g14: ArcOfCircle CenterX=-1.5 CenterY=56.25 CenterZ=0 NormalX=0 NormalY=0 NormalZ=1 AngleXU=0 Radius=1.5 StartAngle=4.71239 EndAngle=7.85398
    g15: ArcOfCircle CenterX=-11.49 CenterY=50.5 CenterZ=0 NormalX=0 NormalY=0 NormalZ=1 AngleXU=0 Radius=1.5 StartAngle=4.71239 EndAngle=7.85398
    g16: ArcOfCircle CenterX=-16.28 CenterY=44.75 CenterZ=0 NormalX=0 NormalY=0 NormalZ=1 AngleXU=0 Radius=1.5 StartAngle=4.71239 EndAngle=7.85398
    g17: ArcOfCircle CenterX=-18.2337 CenterY=39 CenterZ=0 NormalX=0 NormalY=0 NormalZ=1 AngleXU=0 Radius=1.5 StartAngle=4.71485 EndAngle=7.85398
    g18: ArcOfCircle CenterX=-16.2837 CenterY=27.25 CenterZ=0 NormalX=0 NormalY=0 NormalZ=1 AngleXU=0 Radius=1.5 StartAngle=4.71485 EndAngle=7.85398
    g19: ArcOfCircle CenterX=-18.2337 CenterY=33 CenterZ=0 NormalX=0 NormalY=0 NormalZ=1 AngleXU=0 Radius=1.5 StartAngle=4.71485 EndAngle=7.85398
    g20: ArcOfCircle CenterX=-11.49 CenterY=21.5 CenterZ=0 NormalX=0 NormalY=0 NormalZ=1 AngleXU=0 Radius=1.5 StartAngle=4.71239 EndAngle=7.85398
    g21: ArcOfCircle CenterX=-1.5 CenterY=4.25 CenterZ=0 NormalX=0 NormalY=0 NormalZ=1 AngleXU=0 Radius=1.5 StartAngle=4.71239 EndAngle=7.85398
    g22: ArcOfCircle CenterX=-1.5 CenterY=10 CenterZ=0 NormalX=0 NormalY=0 NormalZ=1 AngleXU=0 Radius=1.5 StartAngle=4.71239 EndAngle=7.85398
    g23: ArcOfCircle CenterX=-1.5 CenterY=15.75 CenterZ=0 NormalX=0 NormalY=0 NormalZ=1 AngleXU=0 Radius=1.5 StartAngle=4.71239 EndAngle=7.85398
    g24: LineSegment StartX=-49.19 StartY=69.25 StartZ=0 EndX=-1.5 EndY=69.25 EndZ=0
    g25: LineSegment StartX=-49.19 StartY=66.25 StartZ=0 EndX=-1.5 EndY=66.25 EndZ=0
    g26: LineSegment StartX=-49.19 StartY=63.5 StartZ=0 EndX=-1.5 EndY=63.5 EndZ=0
    g27: LineSegment StartX=-49.19 StartY=60.5 StartZ=0 EndX=-1.5 EndY=60.5 EndZ=0
    g28: LineSegment StartX=-49.19 StartY=57.75 StartZ=0 EndX=-1.5 EndY=57.75 EndZ=0
    g29: LineSegment StartX=-49.19 StartY=54.75 StartZ=0 EndX=-1.5 EndY=54.75 EndZ=0
    g30: LineSegment StartX=-49.19 StartY=52 StartZ=0 EndX=-11.49 EndY=52 EndZ=0
    g31: LineSegment StartX=-49.19 StartY=49 StartZ=0 EndX=-11.49 EndY=49 EndZ=0
    g32: LineSegment StartX=-49.19 StartY=46.25 StartZ=0 EndX=-16.28 EndY=46.25 EndZ=0
    g33: LineSegment StartX=-49.19 StartY=43.25 StartZ=0 EndX=-16.28 EndY=43.25 EndZ=0
    g34: LineSegment StartX=-49.19 StartY=40.5 StartZ=0 EndX=-18.2337 EndY=40.5 EndZ=0
    g35: LineSegment StartX=-49.19 StartY=37.5 StartZ=0 EndX=-18.23 EndY=37.5 EndZ=0
    g36: LineSegment StartX=-49.19 StartY=34.5 StartZ=0 EndX=-18.2337 EndY=34.5 EndZ=0
    g37: LineSegment StartX=-49.19 StartY=31.5 StartZ=0 EndX=-18.23 EndY=31.5 EndZ=0
    g38: LineSegment StartX=-49.19 StartY=28.75 StartZ=0 EndX=-16.2837 EndY=28.75 EndZ=0
    g39: LineSegment StartX=-49.19 StartY=25.75 StartZ=0 EndX=-16.28 EndY=25.75 EndZ=0
    g40: LineSegment StartX=-49.19 StartY=23 StartZ=0 EndX=-11.49 EndY=23 EndZ=0
    g41: LineSegment StartX=-49.19 StartY=20 StartZ=0 EndX=-11.49 EndY=20 EndZ=0
    g42: LineSegment StartX=-49.19 StartY=17.25 StartZ=0 EndX=-1.5 EndY=17.25 EndZ=0
    g43: LineSegment StartX=-49.19 StartY=14.25 StartZ=0 EndX=-1.5 EndY=14.25 EndZ=0
    g44: LineSegment StartX=-49.19 StartY=11.5 StartZ=0 EndX=-1.5 EndY=11.5 EndZ=0
    g45: LineSegment StartX=-49.19 StartY=8.5 StartZ=0 EndX=-1.5 EndY=8.5 EndZ=0
    g46: LineSegment StartX=-49.19 StartY=5.75 StartZ=0 EndX=-1.5 EndY=5.75 EndZ=0
    g47: LineSegment StartX=-49.19 StartY=2.75 StartZ=0 EndX=-1.5 EndY=2.75 EndZ=0
  constraints (120):
    c: Vertical(g0)
    c: Distance(g0) = 3
    c: Block(g0)
    c: Vertical(g1)
    c: Distance(g1) = 3
    c: Vertical(g2)
    c: Equal(g0,g2) = 3
    c: Block(g2)
    c: Vertical(g3)
    c: Equal(g1,g3) = 3
    c: Vertical(g4)
    c: Equal(g0,g4) = 3
    c: Block(g4)
    c: Vertical(g5)
    c: Equal(g1,g5) = 3
    c: Vertical(g6)
    c: Equal(g0,g6) = 3
    c: Block(g6)
    c: Vertical(g7)
    c: Equal(g1,g7) = 3
    c: Vertical(g8)
    c: Equal(g0,g8) = 3
    c: Block(g8)
    c: Vertical(g9)
    c: Equal(g1,g9) = 3
    c: Vertical(g10)
    c: Equal(g0,g10) = 3
    c: Block(g10)
    c: Vertical(g11)
    c: Equal(g1,g11) = 3
    c: Block(g12)
    c: Block(g13)
    c: Block(g14)
    c: Block(g15)
    c: Block(g16)
    c: Block(g17)
    c: Block(g18)
    c: Block(g19)
    c: Block(g20)
    c: Block(g21)
    c: Block(g22)
    c: Block(g23)
    c: Block(g11)
    c: Block(g9)
    c: Block(g7)
    c: Block(g5)
    c: Block(g3)
    c: Block(g1)
    c: Coincident(g24,g0)
    c: Coincident(g24,g12)
    c: Horizontal(g24)
    c: Coincident(g25,g0)
    c: Coincident(g25,g12)
    c: Horizontal(g25)
    c: Coincident(g26,g1)
    c: Coincident(g26,g13)
    c: Horizontal(g26)
    c: Coincident(g27,g1)
    c: Coincident(g27,g13)
    c: Horizontal(g27)
    c: Coincident(g28,g2)
    c: Coincident(g28,g14)
    c: Horizontal(g28)
    c: Coincident(g29,g2)
    c: Coincident(g29,g14)
    c: Horizontal(g29)
    c: Coincident(g30,g3)
    c: Coincident(g30,g15)
    c: Horizontal(g30)
    c: Coincident(g31,g3)
    c: Coincident(g31,g15)
    c: Horizontal(g31)
    c: Coincident(g32,g4)
    c: Coincident(g32,g16)
    c: Horizontal(g32)
    c: Coincident(g33,g4)
    c: Coincident(g33,g16)
    c: Horizontal(g33)
    c: Coincident(g34,g5)
    c: Coincident(g34,g17)
    c: Horizontal(g34)
    c: Coincident(g35,g5)
    c: Coincident(g35,g17)
    c: Horizontal(g35)
    c: Coincident(g36,g6)
    c: Coincident(g36,g19)
    c: Horizontal(g36)
    c: Coincident(g37,g6)
    c: Coincident(g37,g19)
    c: Horizontal(g37)
    c: Coincident(g38,g7)
    c: Coincident(g38,g18)
    c: Horizontal(g38)
    c: Coincident(g39,g7)
    c: Coincident(g39,g18)
    c: Horizontal(g39)
    c: Coincident(g40,g8)
    c: Coincident(g40,g20)
    c: Horizontal(g40)
    c: Coincident(g41,g8)
    c: Coincident(g41,g20)
    c: Horizontal(g41)
    c: Coincident(g42,g9)
    c: Coincident(g42,g23)
    c: Horizontal(g42)
    c: Coincident(g43,g9)
    c: Coincident(g43,g23)
    c: Horizontal(g43)
    c: Coincident(g44,g10)
    c: Coincident(g44,g22)
    c: Horizontal(g44)
    c: Coincident(g45,g10)
    c: Coincident(g45,g22)
    c: Horizontal(g45)
    c: Coincident(g46,g11)
    c: Coincident(g46,g21)
    c: Horizontal(g46)
    c: Coincident(g47,g11)
    c: Coincident(g47,g21)
    c: Horizontal(g47)
FEATURE [Part::Extrusion] Extrude046
  Base = -> Sketch055
  Dir = (1,0,0)
  DirMode = 2
  FaceMakerClass = Part::FaceMakerBullseye
  LengthFwd = 23
  LengthRev = 0
  Placement = pos=(-19,0,0) rot=(0,0,1;0rad)
  Solid = true
  Symmetric = false
FEATURE [Part::Fillet] Fillet038  label="removeToCreateVentalationHoles001"
  Base = -> Extrude046
  Edges = <same value as first occurrence — deduplicated (x6 in doc)>
  Placement = pos=(7,0,0) rot=(0,0,1;0rad)
FEATURE [Sketcher::SketchObject] Sketch056  label="topSketch014"
  FullyConstrained = true
  sketch-geometry (22):
    g0: LineSegment StartX=5.21097e-06 StartY=3 StartZ=0 EndX=5.21097e-06 EndY=19 EndZ=0
    g1: ArcOfCircle CenterX=19 CenterY=19 CenterZ=0 NormalX=0 NormalY=0 NormalZ=1 AngleXU=0 Radius=19 StartAngle=1.5708 EndAngle=3.14159
    g2: ArcOfCircle CenterX=19 CenterY=19 CenterZ=0 NormalX=0 NormalY=0 NormalZ=1 AngleXU=0 Radius=16 StartAngle=1.5708 EndAngle=3.14159
    g3: LineSegment StartX=114 StartY=35 StartZ=0 EndX=19 EndY=35 EndZ=0
    g4: LineSegment StartX=5.21097e-06 StartY=3 StartZ=0 EndX=5.21097e-06 EndY=0 EndZ=0
    g5: LineSegment StartX=3 StartY=0 StartZ=0 EndX=5.21097e-06 EndY=0 EndZ=0
    g6: LineSegment StartX=3 StartY=19 StartZ=0 EndX=3 EndY=0 EndZ=0
    g7: LineSegment StartX=19 StartY=38 StartZ=0 EndX=124 EndY=38 EndZ=0
    g8: Circle CenterX=119 CenterY=35 CenterZ=0 NormalX=0 NormalY=0 NormalZ=1 AngleXU=0 Radius=1
    g9: Circle CenterX=121 CenterY=35 CenterZ=0 NormalX=0 NormalY=0 NormalZ=1 AngleXU=0 Radius=1
    g10: Circle CenterX=121 CenterY=33 CenterZ=0 NormalX=0 NormalY=0 NormalZ=1 AngleXU=0 Radius=1
    g11: BSplineCurve PolesCount=3 KnotsCount=2 Degree=2 IsPeriodic=0
    g12: GeomPoint X=119 Y=35 Z=0
    g13: GeomPoint X=121 Y=33 Z=0
    g14: LineSegment StartX=119 StartY=35 StartZ=0 EndX=114 EndY=35 EndZ=0
    g15: ArcOfCircle CenterX=105 CenterY=19 CenterZ=0 NormalX=0 NormalY=0 NormalZ=1 AngleXU=0 Radius=16 StartAngle=5.60905 EndAngle=6.28319
    g16: LineSegment StartX=121 StartY=33 StartZ=0 EndX=121 EndY=19 EndZ=0
    g17: LineSegment StartX=117.5 StartY=9.01251 StartZ=0 EndX=121.163 EndY=9.0125 EndZ=0
    g18: ArcOfCircle CenterX=105 CenterY=19 CenterZ=0 NormalX=0 NormalY=0 NormalZ=1 AngleXU=0 Radius=20.6155 StartAngle=5.7297 EndAngle=6.28319
    g19: LineSegment StartX=121.163 StartY=9.0125 StartZ=0 EndX=122.538 EndY=8.16329 EndZ=0
    g20: LineSegment StartX=124 StartY=38 StartZ=0 EndX=125.616 EndY=38 EndZ=0
    g21: LineSegment StartX=125.616 StartY=19 StartZ=0 EndX=125.616 EndY=38 EndZ=0
  constraints (49):
    c: Vertical(g0)
    c: Block(g0)
    c: Coincident(g1,g0)
    c: Block(g1)
    c: Coincident(g2,g1)
    c: Block(g2)
    c: Coincident(g3,g2)
    c: Horizontal(g3)
    c: Tangent(g3,g2)
    c: Coincident(g4,g0)
    c: Distance(g4) = 3
    c: Vertical(g4)
    c: Coincident(g5,g4)
    c: Horizontal(g5)
    c: Coincident(g6,g2)
    c: Coincident(g6,g5)
    c: Vertical(g6)
    c: Horizontal(g7)
    c: Distance(g7) = 105
    c: Coincident(g7,g1)
    c: Block(g3)
    c: Weight(g8) = 1
    c: Equal(g8,g9)
    c: Equal(g8,g10)
    c: InternalAlignment(g8,g11)
    c: InternalAlignment(g9,g11)
    c: InternalAlignment(g10,g11)
    c: InternalAlignment(g12,g11)
    c: InternalAlignment(g13,g11)
    c: Block(g11)
    c: Coincident(g14,g11)
    c: Coincident(g14,g3)
    c: Horizontal(g14)
    c: Block(g15)
    c: Coincident(g16,g11)
    c: Coincident(g16,g15)
    c: Vertical(g16)
    c: Distance(g16) = 14
    c: Coincident(g17,g15)
    c: Block(g18)
    c: Coincident(g19,g18)
    c: Coincident(g20,g7)
    c: Horizontal(g20)
    c: Vertical(g21)
    c: Coincident(g20,g21)
    c: Block(g20)
    c: Block(g21)
    c: Block(g19)
    c: Block(g17)
FEATURE [Part::Box] Box026  label="removeToCreteHoleForPlugHousing032"
  AttacherType = Attacher::AttachEngine3D
  Height = 28.6
  Length = 10
  Placement = pos=(-2,0,21.7) rot=(0,0,1;0rad)
  Width = 19
FEATURE [Part::Feature] Face109 .. Face112  x4 (patterned run collapsed; names and placements below)
  shape: bbox 3.5 x 17.8 x 2e-07 mm, 1 faces, 0 solids (baked)
FEATURE [Part::Revolution] Revolve117  label="removeToCreateScrewAndThreadedInsertHole045"
  Angle = 360
  Axis = (0,1,0)
  Base = (0,0,0)
  FaceMakerClass = Part::FaceMakerBullseye
  Placement = pos=(62.3,30.3,19.7) rot=(0,0,1;0rad)
  Solid = false
  Source = -> Face109
  Symmetric = false
FEATURE [Part::Revolution] Revolve118  label="removeToCreateScrewAndThreadedInsertHole046"
  Angle = 360
  Axis = (0,1,0)
  Base = (0,0,0)
  FaceMakerClass = Part::FaceMakerBullseye
  Placement = pos=(62.3,30.3,51.7) rot=(0,0,1;0rad)
  Solid = false
  Source = -> Face110
  Symmetric = false
FEATURE [Part::Revolution] Revolve119  label="removeToCreateScrewAndThreadedInsertHole047"
  Angle = 360
  Axis = (0,1,0)
  Base = (0,0,0)
  FaceMakerClass = Part::FaceMakerBullseye
  Placement = pos=(30.3,30.3,19.7) rot=(0,0,1;0rad)
  Solid = false
  Source = -> Face111
  Symmetric = false
FEATURE [Part::Revolution] Revolve120  label="removeToCreateScrewAndThreadedInsertHole048"
  Angle = 360
  Axis = (0,1,0)
  Base = (0,0,0)
  FaceMakerClass = Part::FaceMakerBullseye
  Placement = pos=(30.3,30.3,51.7) rot=(0,0,1;0rad)
  Solid = false
  Source = -> Face112
  Symmetric = false
FEATURE [Part::MultiFuse] Fusion087  label="createThreadedInsertHolesForFan005"
  Shapes = -> [Revolve117,Revolve118,Revolve119,Revolve120]
FEATURE [Part::Extrusion] Extrude047
  Base = -> Sketch056
  Dir = (0,0,1)
  DirMode = 2
  FaceMakerClass = Part::FaceMakerBullseye
  LengthFwd = 72
  LengthRev = 0
  Solid = true
  Symmetric = false
FEATURE [Part::Fillet] Fillet039  label="top019"
  Base = -> Extrude047
  Edges = 1 edges r=2: [Edge35]
FEATURE [Sketcher::SketchObject] Sketch057
  FullyConstrained = false
  Placement = pos=(0,0,0) rot=(1,0,0;1.5708rad)
  sketch-geometry (24):
    g0: ArcOfCircle CenterX=-4 CenterY=-10.5 CenterZ=0 NormalX=0 NormalY=0 NormalZ=1 AngleXU=0 Radius=1.5 StartAngle=6e-16 EndAngle=3.14159
    g1: ArcOfCircle CenterX=-34.2 CenterY=-10.5 CenterZ=0 NormalX=0 NormalY=0 NormalZ=1 AngleXU=0 Radius=1.5 StartAngle=0 EndAngle=3.14159
    g2: ArcOfCircle CenterX=-34.2 CenterY=-27.7 CenterZ=0 NormalX=0 NormalY=0 NormalZ=1 AngleXU=0 Radius=1.5 StartAngle=3.14159 EndAngle=6.28319
    g3: ArcOfCircle CenterX=-4 CenterY=-27.7 CenterZ=0 NormalX=0 NormalY=0 NormalZ=1 AngleXU=0 Radius=1.5 StartAngle=3.1416 EndAngle=6.28319
    g4: ArcOfCircle CenterX=-10 CenterY=-4.3 CenterZ=0 NormalX=0 NormalY=0 NormalZ=1 AngleXU=0 Radius=1.5 StartAngle=2e-16 EndAngle=3.14159
    g5: ArcOfCircle CenterX=-16.1 CenterY=-1.8 CenterZ=0 NormalX=0 NormalY=0 NormalZ=1 AngleXU=0 Radius=1.5 StartAngle=5e-16 EndAngle=3.14159
    g6: ArcOfCircle CenterX=-22.1 CenterY=-1.8 CenterZ=0 NormalX=0 NormalY=0 NormalZ=1 AngleXU=0 Radius=1.5 StartAngle=5e-16 EndAngle=3.14159
    g7: ArcOfCircle CenterX=-28.2 CenterY=-4.3 CenterZ=0 NormalX=0 NormalY=0 NormalZ=1 AngleXU=0 Radius=1.5 StartAngle=2e-16 EndAngle=3.14159
    g8: ArcOfCircle CenterX=-10 CenterY=-33.9 CenterZ=0 NormalX=0 NormalY=0 NormalZ=1 AngleXU=0 Radius=1.5 StartAngle=3.14159 EndAngle=6.28319
    g9: ArcOfCircle CenterX=-16.1 CenterY=-36.4 CenterZ=0 NormalX=0 NormalY=0 NormalZ=1 AngleXU=0 Radius=1.5 StartAngle=3.14159 EndAngle=6.28319
    g10: ArcOfCircle CenterX=-22.1 CenterY=-36.4 CenterZ=0 NormalX=0 NormalY=0 NormalZ=1 AngleXU=0 Radius=1.5 StartAngle=3.14159 EndAngle=6.28319
    g11: ArcOfCircle CenterX=-28.2 CenterY=-33.9 CenterZ=0 NormalX=0 NormalY=0 NormalZ=1 AngleXU=0 Radius=1.5 StartAngle=3.14159 EndAngle=6.28319
    g12: LineSegment StartX=-35.7 StartY=-10.5 StartZ=0 EndX=-35.7 EndY=-27.7 EndZ=0
    g13: LineSegment StartX=-32.7 StartY=-10.5 StartZ=0 EndX=-32.7 EndY=-27.7 EndZ=0
    g14: LineSegment StartX=-29.7 StartY=-33.9 StartZ=0 EndX=-29.7 EndY=-4.3 EndZ=0
    g15: LineSegment StartX=-26.7 StartY=-33.9 StartZ=0 EndX=-26.7 EndY=-4.3 EndZ=0
    g16: LineSegment StartX=-2.5 StartY=-10.5 StartZ=0 EndX=-2.5 EndY=-27.7 EndZ=0
    g17: LineSegment StartX=-8.5 StartY=-4.3 StartZ=0 EndX=-8.5 EndY=-33.9 EndZ=0
    g18: LineSegment StartX=-5.5 StartY=-10.5 StartZ=0 EndX=-5.5 EndY=-27.7 EndZ=0
    g19: LineSegment StartX=-11.5 StartY=-4.3 StartZ=0 EndX=-11.5 EndY=-33.9 EndZ=0
    g20: LineSegment StartX=-14.6 StartY=-1.8 StartZ=0 EndX=-14.6 EndY=-36.4 EndZ=0
    g21: LineSegment StartX=-17.6 StartY=-1.8 StartZ=0 EndX=-17.6 EndY=-36.4 EndZ=0
    g22: LineSegment StartX=-20.6 StartY=-36.4 StartZ=0 EndX=-20.6 EndY=-1.8 EndZ=0
    g23: LineSegment StartX=-23.6 StartY=-1.8 StartZ=0 EndX=-23.6 EndY=-36.4 EndZ=0
  constraints (48):
    c: Block(g0)
    c: Block(g1)
    c: Block(g2)
    c: Block(g3)
    c: Block(g4)
    c: Block(g5)
    c: Block(g6)
    c: Block(g7)
    c: Block(g8)
    c: Block(g9)
    c: Block(g10)
    c: Block(g11)
    c: Coincident(g12,g1)
    c: Coincident(g12,g2)
    c: Vertical(g12)
    c: Coincident(g13,g1)
    c: Coincident(g13,g2)
    c: Vertical(g13)
    c: Coincident(g14,g11)
    c: Coincident(g14,g7)
    c: Vertical(g14)
    c: Coincident(g15,g11)
    c: Coincident(g15,g7)
    c: Vertical(g15)
    c: Coincident(g16,g0)
    c: Coincident(g16,g3)
    c: Vertical(g16)
    c: Coincident(g17,g4)
    c: Coincident(g17,g8)
    c: Vertical(g17)
    c: Coincident(g18,g0)
    c: Coincident(g18,g3)
    c: Vertical(g18)
    c: Coincident(g19,g4)
    c: Coincident(g19,g8)
    c: Vertical(g19)
    c: Coincident(g20,g5)
    c: Coincident(g20,g9)
    c: Vertical(g20)
    c: Coincident(g21,g5)
    c: Coincident(g21,g9)
    c: Vertical(g21)
    c: Coincident(g22,g10)
    c: Coincident(g22,g6)
    c: Vertical(g22)
    c: Coincident(g23,g6)
    c: Coincident(g23,g10)
    c: Vertical(g23)
FEATURE [Part::Extrusion] Extrude048  label="removeToCreateFanGrillHoles004"
  Base = -> Sketch057
  Dir = (0,-1,6e-16)
  DirMode = 2
  FaceMakerClass = Part::FaceMakerBullseye
  LengthFwd = 10
  LengthRev = 0
  Placement = pos=(65.4,44,54.82) rot=(0,0,1;0rad)
  Solid = true
  Symmetric = false
FEATURE [Part::Cut] Cut040  label="top021"
  Base = -> Fillet039
  Tool = -> Extrude048
FEATURE [Part::Cylinder] Cylinder041  label="removeToCreteHoleForPlugHousing034"
  Angle = 360
  AttacherType = Attacher::AttachEngine3D
  Height = 20
  Placement = pos=(-2,19,36) rot=(0,1,0;1.5708rad)
  Radius = 14.3
FEATURE [Part::MultiFuse] Fusion089  label="removeToCreteHoleForPlugHousing035"
  Shapes = -> [Box026,Cylinder041]
FEATURE [Part::Cylinder] Cylinder042
  Angle = 360
  AttacherType = Attacher::AttachEngine3D
  Height = 20
  Placement = pos=(0,0,36.15) rot=(0,0,1;0rad)
  Radius = 14.3
FEATURE [Part::Cylinder] Cylinder043
  Angle = 360
  AttacherType = Attacher::AttachEngine3D
  Height = 10
  Placement = pos=(0,0,36.15) rot=(0,0,1;0rad)
  Radius = 4
FEATURE [Part::Box] Box027  label="removeToCreteHoleForPlugHousing036"
  AttacherType = Attacher::AttachEngine3D
  Height = 28.6
  Length = 20
  Placement = pos=(106.15,0,21.7) rot=(0,0,1;0rad)
  Width = 19
FEATURE [Part::Cut] Cut041  label="top022"
  Base = -> Cut040
  Tool = -> Fusion087
FEATURE [Part::Cut] Cut039  label="top020"
  Base = -> Cut041
  Tool = -> Fusion089
FEATURE [Part::MultiFuse] Fusion090  label="removeToCreteHoleForPlugHousing037"
  Placement = pos=(70,19,36) rot=(0,1,0;1.5708rad)
  Shapes = -> [Cylinder042,Cylinder043]
FEATURE [Part::MultiFuse] Fusion088  label="removeToCreteHoleForPlugHousing033"
  Shapes = -> [Box027,Fusion090]
FEATURE [Part::Cut] Cut042  label="removeToCreteHoleForPlugHousing038"
  Base = -> Cut039
  Tool = -> Fusion088
FEATURE [Part::MultiFuse] Fusion091  label="removeFromTop"
  Shapes = -> [Fillet038,Fusion085,Fusion084,Fusion083,Extrude045]
FEATURE [Part::Cut] Cut043  label="REAL TOP ====="
  Base = -> Fillet036
  Tool = -> Fusion091
FEATURE [Part::MultiFuse] Fusion092  label="caseScrewPillarBracket016"
  Shapes = -> [Extrude030,Extrude031,Extrude032,Extrude033,Extrude034,Extrude035,Extrude036,Extrude037,Box013,Box014]
FEATURE [Sketcher::SketchObject] Sketch058  label="topSketch015"
  FullyConstrained = true
  sketch-geometry (20):
    g0: LineSegment StartX=5.21097e-06 StartY=3 StartZ=0 EndX=5.21097e-06 EndY=19 EndZ=0
    g1: ArcOfCircle CenterX=19 CenterY=19 CenterZ=0 NormalX=0 NormalY=0 NormalZ=1 AngleXU=0 Radius=19 StartAngle=1.5708 EndAngle=3.14159
    g2: ArcOfCircle CenterX=19 CenterY=19 CenterZ=0 NormalX=0 NormalY=0 NormalZ=1 AngleXU=0 Radius=16 StartAngle=1.5708 EndAngle=3.14159
    g3: LineSegment StartX=114 StartY=35 StartZ=0 EndX=19 EndY=35 EndZ=0
    g4: LineSegment StartX=5.21097e-06 StartY=3 StartZ=0 EndX=5.21097e-06 EndY=0 EndZ=0
    g5: LineSegment StartX=3 StartY=0 StartZ=0 EndX=5.21097e-06 EndY=0 EndZ=0
    g6: LineSegment StartX=3 StartY=19 StartZ=0 EndX=3 EndY=0 EndZ=0
    g7: LineSegment StartX=19 StartY=38 StartZ=0 EndX=124 EndY=38 EndZ=0
    g8: Circle CenterX=119 CenterY=35 CenterZ=0 NormalX=0 NormalY=0 NormalZ=1 AngleXU=0 Radius=1
    g9: Circle CenterX=121 CenterY=35 CenterZ=0 NormalX=0 NormalY=0 NormalZ=1 AngleXU=0 Radius=1
    g10: Circle CenterX=121 CenterY=33 CenterZ=0 NormalX=0 NormalY=0 NormalZ=1 AngleXU=0 Radius=1
    g11: BSplineCurve PolesCount=3 KnotsCount=2 Degree=2 IsPeriodic=0
    g12: GeomPoint X=119 Y=35 Z=0
    g13: GeomPoint X=121 Y=33 Z=0
    g14: LineSegment StartX=119 StartY=35 StartZ=0 EndX=114 EndY=35 EndZ=0
    g15: ArcOfCircle CenterX=105 CenterY=19 CenterZ=0 NormalX=0 NormalY=0 NormalZ=1 AngleXU=0 Radius=19 StartAngle=5.7297 EndAngle=6.28319
    g16: ArcOfCircle CenterX=105 CenterY=19 CenterZ=0 NormalX=0 NormalY=0 NormalZ=1 AngleXU=0 Radius=16 StartAngle=5.60905 EndAngle=6.28319
    g17: LineSegment StartX=121 StartY=33 StartZ=0 EndX=121 EndY=19 EndZ=0
    g18: LineSegment StartX=124 StartY=38 StartZ=0 EndX=124 EndY=19 EndZ=0
    g19: LineSegment StartX=117.5 StartY=9.01251 StartZ=0 EndX=121.163 EndY=9.0125 EndZ=0
  constraints (46):
    c: Vertical(g0)
    c: Block(g0)
    c: Coincident(g1,g0)
    c: Block(g1)
    c: Coincident(g2,g1)
    c: Block(g2)
    c: Coincident(g3,g2)
    c: Horizontal(g3)
    c: Tangent(g3,g2)
    c: Coincident(g4,g0)
    c: Distance(g4) = 3
    c: Vertical(g4)
    c: Coincident(g5,g4)
    c: Horizontal(g5)
    c: Coincident(g6,g2)
    c: Coincident(g6,g5)
    c: Vertical(g6)
    c: Horizontal(g7)
    c: Distance(g7) = 105
    c: Coincident(g7,g1)
    c: Block(g3)
    c: Weight(g8) = 1
    c: Equal(g8,g9)
    c: Equal(g8,g10)
    c: InternalAlignment(g8,g11)
    c: InternalAlignment(g9,g11)
    c: InternalAlignment(g10,g11)
    c: InternalAlignment(g12,g11)
    c: InternalAlignment(g13,g11)
    c: Block(g11)
    c: Coincident(g14,g11)
    c: Coincident(g14,g3)
    c: Horizontal(g14)
    c: Block(g15)
    c: Coincident(g16,g15)
    c: Block(g16)
    c: Coincident(g17,g11)
    c: Coincident(g17,g16)
    c: Vertical(g17)
    c: Distance(g17) = 14
    c: Coincident(g18,g7)
    c: Coincident(g18,g15)
    c: Vertical(g18)
    c: Distance(g18) = 19
    c: Coincident(g19,g16)
    c: Coincident(g19,g15)
FEATURE [Part::Extrusion] Extrude049  label="top023"
  Base = -> Sketch058
  Dir = (0,0,1)
  DirMode = 2
  FaceMakerClass = Part::FaceMakerBullseye
  LengthFwd = 72
  LengthRev = 0
  Solid = true
  Symmetric = false
FEATURE [Sketcher::SketchObject] Sketch059
  FullyConstrained = true
  MapMode = 3
  Placement = pos=(0,0,0) rot=(1,0,0;1.5708rad)
  Support = -> [Extrude049]
  sketch-geometry (8):
    g0: Circle CenterX=80.351 CenterY=-67.6202 CenterZ=0 NormalX=0 NormalY=0 NormalZ=1 AngleXU=0 Radius=2
    g1: Circle CenterX=80.351 CenterY=-67.6202 CenterZ=0 NormalX=0 NormalY=0 NormalZ=1 AngleXU=0 Radius=3
    g2: Circle CenterX=80.351 CenterY=-4.92017 CenterZ=0 NormalX=0 NormalY=0 NormalZ=1 AngleXU=0 Radius=2
    g3: Circle CenterX=80.351 CenterY=-4.92017 CenterZ=0 NormalX=0 NormalY=0 NormalZ=1 AngleXU=0 Radius=3
    g4: Circle CenterX=23.851 CenterY=-4.92017 CenterZ=0 NormalX=0 NormalY=0 NormalZ=1 AngleXU=0 Radius=2
    g5: Circle CenterX=23.851 CenterY=-4.92017 CenterZ=0 NormalX=0 NormalY=0 NormalZ=1 AngleXU=0 Radius=3
    g6: Circle CenterX=23.851 CenterY=-67.6202 CenterZ=0 NormalX=0 NormalY=0 NormalZ=1 AngleXU=0 Radius=2
    g7: Circle CenterX=23.851 CenterY=-67.6202 CenterZ=0 NormalX=0 NormalY=0 NormalZ=1 AngleXU=0 Radius=3
  constraints (8):
    c: Block(g3)
    c: Block(g2)
    c: Block(g1)
    c: Block(g0)
    c: Block(g6)
    c: Block(g7)
    c: Block(g4)
    c: Block(g5)
FEATURE [Sketcher::SketchObject] Sketch060
  FullyConstrained = true
  MapMode = 3
  Placement = pos=(0,0,0) rot=(1,0,0;1.5708rad)
  Support = -> [Extrude049]
  sketch-geometry (8):
    g0: Circle CenterX=80.351 CenterY=-67.6202 CenterZ=0 NormalX=0 NormalY=0 NormalZ=1 AngleXU=0 Radius=3
    g1: Circle CenterX=80.351 CenterY=-4.92017 CenterZ=0 NormalX=0 NormalY=0 NormalZ=1 AngleXU=0 Radius=3
    g2: Circle CenterX=23.851 CenterY=-4.92017 CenterZ=0 NormalX=0 NormalY=0 NormalZ=1 AngleXU=0 Radius=3
    g3: Circle CenterX=23.851 CenterY=-67.6202 CenterZ=0 NormalX=0 NormalY=0 NormalZ=1 AngleXU=0 Radius=3
    g4: Circle CenterX=23.851 CenterY=-67.6202 CenterZ=0 NormalX=0 NormalY=0 NormalZ=1 AngleXU=0 Radius=5
    g5: Circle CenterX=80.351 CenterY=-67.6202 CenterZ=0 NormalX=0 NormalY=0 NormalZ=1 AngleXU=0 Radius=5
    g6: Circle CenterX=23.851 CenterY=-4.92017 CenterZ=0 NormalX=0 NormalY=0 NormalZ=1 AngleXU=0 Radius=5
    g7: Circle CenterX=80.351 CenterY=-4.92017 CenterZ=0 NormalX=0 NormalY=0 NormalZ=1 AngleXU=0 Radius=5
  constraints (8):
    c: Block(g1)
    c: Block(g0)
    c: Block(g3)
    c: Block(g2)
    c: Block(g5)
    c: Block(g4)
    c: Block(g6)
    c: Block(g7)
FEATURE [Sketcher::SketchObject] Sketch061
  FullyConstrained = true
  MapMode = 3
  Placement = pos=(0,0,0) rot=(1,0,0;1.5708rad)
  sketch-geometry (8):
    g0: Circle CenterX=80.351 CenterY=-67.6202 CenterZ=0 NormalX=0 NormalY=0 NormalZ=1 AngleXU=0 Radius=3
    g1: Circle CenterX=80.351 CenterY=-4.92017 CenterZ=0 NormalX=0 NormalY=0 NormalZ=1 AngleXU=0 Radius=3
    g2: Circle CenterX=23.851 CenterY=-4.92017 CenterZ=0 NormalX=0 NormalY=0 NormalZ=1 AngleXU=0 Radius=3
    g3: Circle CenterX=23.851 CenterY=-67.6202 CenterZ=0 NormalX=0 NormalY=0 NormalZ=1 AngleXU=0 Radius=3
    g4: Circle CenterX=23.851 CenterY=-67.6202 CenterZ=0 NormalX=0 NormalY=0 NormalZ=1 AngleXU=0 Radius=5
    g5: Circle CenterX=80.351 CenterY=-67.6202 CenterZ=0 NormalX=0 NormalY=0 NormalZ=1 AngleXU=0 Radius=5
    g6: Circle CenterX=23.851 CenterY=-4.92017 CenterZ=0 NormalX=0 NormalY=0 NormalZ=1 AngleXU=0 Radius=5
    g7: Circle CenterX=80.351 CenterY=-4.92017 CenterZ=0 NormalX=0 NormalY=0 NormalZ=1 AngleXU=0 Radius=5
  constraints (8):
    c: Block(g1)
    c: Block(g0)
    c: Block(g3)
    c: Block(g2)
    c: Block(g5)
    c: Block(g4)
    c: Block(g6)
    c: Block(g7)
FEATURE [Sketcher::SketchObject] Sketch062  label="topSketch016"
  FullyConstrained = true
  sketch-geometry (20):
    g0: LineSegment StartX=5.21097e-06 StartY=3 StartZ=0 EndX=5.21097e-06 EndY=19 EndZ=0
    g1: ArcOfCircle CenterX=19 CenterY=19 CenterZ=0 NormalX=0 NormalY=0 NormalZ=1 AngleXU=0 Radius=19 StartAngle=1.5708 EndAngle=3.14159
    g2: ArcOfCircle CenterX=19 CenterY=19 CenterZ=0 NormalX=0 NormalY=0 NormalZ=1 AngleXU=0 Radius=16 StartAngle=1.5708 EndAngle=3.14159
    g3: LineSegment StartX=114 StartY=35 StartZ=0 EndX=19 EndY=35 EndZ=0
    g4: LineSegment StartX=5.21097e-06 StartY=3 StartZ=0 EndX=5.21097e-06 EndY=0 EndZ=0
    g5: LineSegment StartX=3 StartY=0 StartZ=0 EndX=5.21097e-06 EndY=0 EndZ=0
    g6: LineSegment StartX=3 StartY=19 StartZ=0 EndX=3 EndY=0 EndZ=0
    g7: LineSegment StartX=19 StartY=38 StartZ=0 EndX=124 EndY=38 EndZ=0
    g8: Circle CenterX=119 CenterY=35 CenterZ=0 NormalX=0 NormalY=0 NormalZ=1 AngleXU=0 Radius=1
    g9: Circle CenterX=121 CenterY=35 CenterZ=0 NormalX=0 NormalY=0 NormalZ=1 AngleXU=0 Radius=1
    g10: Circle CenterX=121 CenterY=33 CenterZ=0 NormalX=0 NormalY=0 NormalZ=1 AngleXU=0 Radius=1
    g11: BSplineCurve PolesCount=3 KnotsCount=2 Degree=2 IsPeriodic=0
    g12: GeomPoint X=119 Y=35 Z=0
    g13: GeomPoint X=121 Y=33 Z=0
    g14: LineSegment StartX=119 StartY=35 StartZ=0 EndX=114 EndY=35 EndZ=0
    g15: ArcOfCircle CenterX=105 CenterY=19 CenterZ=0 NormalX=0 NormalY=0 NormalZ=1 AngleXU=0 Radius=19 StartAngle=5.7297 EndAngle=6.28319
    g16: ArcOfCircle CenterX=105 CenterY=19 CenterZ=0 NormalX=0 NormalY=0 NormalZ=1 AngleXU=0 Radius=16 StartAngle=5.60905 EndAngle=6.28319
    g17: LineSegment StartX=121 StartY=33 StartZ=0 EndX=121 EndY=19 EndZ=0
    g18: LineSegment StartX=124 StartY=38 StartZ=0 EndX=124 EndY=19 EndZ=0
    g19: LineSegment StartX=117.5 StartY=9.01251 StartZ=0 EndX=121.163 EndY=9.0125 EndZ=0
  constraints (46):
    c: Vertical(g0)
    c: Block(g0)
    c: Coincident(g1,g0)
    c: Block(g1)
    c: Coincident(g2,g1)
    c: Block(g2)
    c: Coincident(g3,g2)
    c: Horizontal(g3)
    c: Tangent(g3,g2)
    c: Coincident(g4,g0)
    c: Distance(g4) = 3
    c: Vertical(g4)
    c: Coincident(g5,g4)
    c: Horizontal(g5)
    c: Coincident(g6,g2)
    c: Coincident(g6,g5)
    c: Vertical(g6)
    c: Horizontal(g7)
    c: Distance(g7) = 105
    c: Coincident(g7,g1)
    c: Block(g3)
    c: Weight(g8) = 1
    c: Equal(g8,g9)
    c: Equal(g8,g10)
    c: InternalAlignment(g8,g11)
    c: InternalAlignment(g9,g11)
    c: InternalAlignment(g10,g11)
    c: InternalAlignment(g12,g11)
    c: InternalAlignment(g13,g11)
    c: Block(g11)
    c: Coincident(g14,g11)
    c: Coincident(g14,g3)
    c: Horizontal(g14)
    c: Block(g15)
    c: Coincident(g16,g15)
    c: Block(g16)
    c: Coincident(g17,g11)
    c: Coincident(g17,g16)
    c: Vertical(g17)
    c: Distance(g17) = 14
    c: Coincident(g18,g7)
    c: Coincident(g18,g15)
    c: Vertical(g18)
    c: Distance(g18) = 19
    c: Coincident(g19,g16)
    c: Coincident(g19,g15)
FEATURE [Part::Extrusion] Extrude053  label="top024"
  Base = -> Sketch062
  Dir = (0,0,1)
  DirMode = 2
  FaceMakerClass = Part::FaceMakerBullseye
  LengthFwd = 72
  LengthRev = 0
  Solid = true
  Symmetric = false
FEATURE [Sketcher::SketchObject] Sketch063
  FullyConstrained = true
  MapMode = 3
  Placement = pos=(0,0,0) rot=(1,0,0;1.5708rad)
  Support = -> [Extrude053]
  sketch-geometry (8):
    g0: Circle CenterX=80.351 CenterY=-67.6202 CenterZ=0 NormalX=0 NormalY=0 NormalZ=1 AngleXU=0 Radius=2
    g1: Circle CenterX=80.351 CenterY=-67.6202 CenterZ=0 NormalX=0 NormalY=0 NormalZ=1 AngleXU=0 Radius=3
    g2: Circle CenterX=80.351 CenterY=-4.92017 CenterZ=0 NormalX=0 NormalY=0 NormalZ=1 AngleXU=0 Radius=2
    g3: Circle CenterX=80.351 CenterY=-4.92017 CenterZ=0 NormalX=0 NormalY=0 NormalZ=1 AngleXU=0 Radius=3
    g4: Circle CenterX=23.851 CenterY=-4.92017 CenterZ=0 NormalX=0 NormalY=0 NormalZ=1 AngleXU=0 Radius=2
    g5: Circle CenterX=23.851 CenterY=-4.92017 CenterZ=0 NormalX=0 NormalY=0 NormalZ=1 AngleXU=0 Radius=3
    g6: Circle CenterX=23.851 CenterY=-67.6202 CenterZ=0 NormalX=0 NormalY=0 NormalZ=1 AngleXU=0 Radius=2
    g7: Circle CenterX=23.851 CenterY=-67.6202 CenterZ=0 NormalX=0 NormalY=0 NormalZ=1 AngleXU=0 Radius=3
  constraints (8):
    c: Block(g3)
    c: Block(g2)
    c: Block(g1)
    c: Block(g0)
    c: Block(g6)
    c: Block(g7)
    c: Block(g4)
    c: Block(g5)
FEATURE [Part::Extrusion] Extrude054
  Base = -> Sketch063
  Dir = (0,-1,2e-16)
  DirMode = 2
  FaceMakerClass = Part::FaceMakerBullseye
  LengthFwd = 6
  LengthRev = 0
  Placement = pos=(0,9,0) rot=(0,0,1;0rad)
  Solid = true
  Symmetric = false
FEATURE [Sketcher::SketchObject] Sketch064  label="topSketch017"
  FullyConstrained = true
  sketch-geometry (20):
    g0: LineSegment StartX=5.21097e-06 StartY=3 StartZ=0 EndX=5.21097e-06 EndY=19 EndZ=0
    g1: ArcOfCircle CenterX=19 CenterY=19 CenterZ=0 NormalX=0 NormalY=0 NormalZ=1 AngleXU=0 Radius=19 StartAngle=1.5708 EndAngle=3.14159
    g2: ArcOfCircle CenterX=19 CenterY=19 CenterZ=0 NormalX=0 NormalY=0 NormalZ=1 AngleXU=0 Radius=16 StartAngle=1.5708 EndAngle=3.14159
    g3: LineSegment StartX=114 StartY=35 StartZ=0 EndX=19 EndY=35 EndZ=0
    g4: LineSegment StartX=5.21097e-06 StartY=3 StartZ=0 EndX=5.21097e-06 EndY=0 EndZ=0
    g5: LineSegment StartX=3 StartY=0 StartZ=0 EndX=5.21097e-06 EndY=0 EndZ=0
    g6: LineSegment StartX=3 StartY=19 StartZ=0 EndX=3 EndY=0 EndZ=0
    g7: LineSegment StartX=19 StartY=38 StartZ=0 EndX=124 EndY=38 EndZ=0
    g8: Circle CenterX=119 CenterY=35 CenterZ=0 NormalX=0 NormalY=0 NormalZ=1 AngleXU=0 Radius=1
    g9: Circle CenterX=121 CenterY=35 CenterZ=0 NormalX=0 NormalY=0 NormalZ=1 AngleXU=0 Radius=1
    g10: Circle CenterX=121 CenterY=33 CenterZ=0 NormalX=0 NormalY=0 NormalZ=1 AngleXU=0 Radius=1
    g11: BSplineCurve PolesCount=3 KnotsCount=2 Degree=2 IsPeriodic=0
    g12: GeomPoint X=119 Y=35 Z=0
    g13: GeomPoint X=121 Y=33 Z=0
    g14: LineSegment StartX=119 StartY=35 StartZ=0 EndX=114 EndY=35 EndZ=0
    g15: ArcOfCircle CenterX=105 CenterY=19 CenterZ=0 NormalX=0 NormalY=0 NormalZ=1 AngleXU=0 Radius=19 StartAngle=5.7297 EndAngle=6.28319
    g16: ArcOfCircle CenterX=105 CenterY=19 CenterZ=0 NormalX=0 NormalY=0 NormalZ=1 AngleXU=0 Radius=16 StartAngle=5.60905 EndAngle=6.28319
    g17: LineSegment StartX=121 StartY=33 StartZ=0 EndX=121 EndY=19 EndZ=0
    g18: LineSegment StartX=124 StartY=38 StartZ=0 EndX=124 EndY=19 EndZ=0
    g19: LineSegment StartX=117.5 StartY=9.01251 StartZ=0 EndX=121.163 EndY=9.0125 EndZ=0
  constraints (46):
    c: Vertical(g0)
    c: Block(g0)
    c: Coincident(g1,g0)
    c: Block(g1)
    c: Coincident(g2,g1)
    c: Block(g2)
    c: Coincident(g3,g2)
    c: Horizontal(g3)
    c: Tangent(g3,g2)
    c: Coincident(g4,g0)
    c: Distance(g4) = 3
    c: Vertical(g4)
    c: Coincident(g5,g4)
    c: Horizontal(g5)
    c: Coincident(g6,g2)
    c: Coincident(g6,g5)
    c: Vertical(g6)
    c: Horizontal(g7)
    c: Distance(g7) = 105
    c: Coincident(g7,g1)
    c: Block(g3)
    c: Weight(g8) = 1
    c: Equal(g8,g9)
    c: Equal(g8,g10)
    c: InternalAlignment(g8,g11)
    c: InternalAlignment(g9,g11)
    c: InternalAlignment(g10,g11)
    c: InternalAlignment(g12,g11)
    c: InternalAlignment(g13,g11)
    c: Block(g11)
    c: Coincident(g14,g11)
    c: Coincident(g14,g3)
    c: Horizontal(g14)
    c: Block(g15)
    c: Coincident(g16,g15)
    c: Block(g16)
    c: Coincident(g17,g11)
    c: Coincident(g17,g16)
    c: Vertical(g17)
    c: Distance(g17) = 14
    c: Coincident(g18,g7)
    c: Coincident(g18,g15)
    c: Vertical(g18)
    c: Distance(g18) = 19
    c: Coincident(g19,g16)
    c: Coincident(g19,g15)
FEATURE [Sketcher::SketchObject] Sketch065
  FullyConstrained = true
  MapMode = 3
  Placement = pos=(0,0,0) rot=(1,0,0;1.5708rad)
  sketch-geometry (8):
    g0: Circle CenterX=80.351 CenterY=-67.6202 CenterZ=0 NormalX=0 NormalY=0 NormalZ=1 AngleXU=0 Radius=3
    g1: Circle CenterX=80.351 CenterY=-4.92017 CenterZ=0 NormalX=0 NormalY=0 NormalZ=1 AngleXU=0 Radius=3
    g2: Circle CenterX=23.851 CenterY=-4.92017 CenterZ=0 NormalX=0 NormalY=0 NormalZ=1 AngleXU=0 Radius=3
    g3: Circle CenterX=23.851 CenterY=-67.6202 CenterZ=0 NormalX=0 NormalY=0 NormalZ=1 AngleXU=0 Radius=3
    g4: Circle CenterX=23.851 CenterY=-67.6202 CenterZ=0 NormalX=0 NormalY=0 NormalZ=1 AngleXU=0 Radius=5
    g5: Circle CenterX=80.351 CenterY=-67.6202 CenterZ=0 NormalX=0 NormalY=0 NormalZ=1 AngleXU=0 Radius=5
    g6: Circle CenterX=23.851 CenterY=-4.92017 CenterZ=0 NormalX=0 NormalY=0 NormalZ=1 AngleXU=0 Radius=5
    g7: Circle CenterX=80.351 CenterY=-4.92017 CenterZ=0 NormalX=0 NormalY=0 NormalZ=1 AngleXU=0 Radius=5
  constraints (8):
    c: Block(g1)
    c: Block(g0)
    c: Block(g3)
    c: Block(g2)
    c: Block(g5)
    c: Block(g4)
    c: Block(g6)
    c: Block(g7)
FEATURE [Part::Extrusion] Extrude056
  Base = -> Sketch065
  Dir = (0,-1,2e-16)
  DirMode = 2
  FaceMakerClass = Part::FaceMakerBullseye
  LengthFwd = 2
  LengthRev = 0
  Solid = true
  Symmetric = false
FEATURE [Part::Extrusion] Extrude057  label="top025"
  Base = -> Sketch064
  Dir = (0,0,1)
  DirMode = 2
  FaceMakerClass = Part::FaceMakerBullseye
  LengthFwd = 72
  LengthRev = 0
  Solid = true
  Symmetric = false
FEATURE [Sketcher::SketchObject] Sketch066
  FullyConstrained = true
  MapMode = 3
  Placement = pos=(0,0,0) rot=(1,0,0;1.5708rad)
  Support = -> [Extrude057]
  sketch-geometry (8):
    g0: Circle CenterX=80.351 CenterY=-67.6202 CenterZ=0 NormalX=0 NormalY=0 NormalZ=1 AngleXU=0 Radius=3
    g1: Circle CenterX=80.351 CenterY=-4.92017 CenterZ=0 NormalX=0 NormalY=0 NormalZ=1 AngleXU=0 Radius=3
    g2: Circle CenterX=23.851 CenterY=-4.92017 CenterZ=0 NormalX=0 NormalY=0 NormalZ=1 AngleXU=0 Radius=3
    g3: Circle CenterX=23.851 CenterY=-67.6202 CenterZ=0 NormalX=0 NormalY=0 NormalZ=1 AngleXU=0 Radius=3
    g4: Circle CenterX=23.851 CenterY=-67.6202 CenterZ=0 NormalX=0 NormalY=0 NormalZ=1 AngleXU=0 Radius=5
    g5: Circle CenterX=80.351 CenterY=-67.6202 CenterZ=0 NormalX=0 NormalY=0 NormalZ=1 AngleXU=0 Radius=5
    g6: Circle CenterX=23.851 CenterY=-4.92017 CenterZ=0 NormalX=0 NormalY=0 NormalZ=1 AngleXU=0 Radius=5
    g7: Circle CenterX=80.351 CenterY=-4.92017 CenterZ=0 NormalX=0 NormalY=0 NormalZ=1 AngleXU=0 Radius=5
  constraints (8):
    c: Block(g1)
    c: Block(g0)
    c: Block(g3)
    c: Block(g2)
    c: Block(g5)
    c: Block(g4)
    c: Block(g6)
    c: Block(g7)
FEATURE [Part::Extrusion] Extrude055
  Base = -> Sketch066
  Dir = (0,-1,2e-16)
  DirMode = 2
  FaceMakerClass = Part::FaceMakerBullseye
  LengthFwd = 2
  LengthRev = 0
  Solid = true
  Symmetric = false
FEATURE [Part::Fillet] Fillet041
  Base = -> Extrude056
  Edges = 4 edges r=1.99: [Edge6,Edge12,Edge18,Edge24]
FEATURE [Part::Cut] Cut045
  Base = -> Extrude055
  Placement = pos=(0,6,0) rot=(0,0,1;0rad)
  Tool = -> Fillet041
FEATURE [Part::MultiFuse] Fusion095  label="pcbScrewPillars"
  Placement = pos=(-3.2,-1,72.3) rot=(0,0,1;0rad)
  Shapes = -> [Cut045,Extrude054]
FEATURE [Part::Feature] Face113
  shape: bbox 3.2 x 1.5 x 2e-07 mm, 1 faces, 0 solids (baked)
FEATURE [Part::Revolution] Revolve121  label="backCaseScrewRetainer002"
  Angle = 360
  Axis = (0,1,0)
  Base = (0,0,0)
  FaceMakerClass = Part::FaceMakerBullseye
  Placement = pos=(12.5,3,62) rot=(0,0,1;0rad)
  Solid = false
  Source = -> Face113
  Symmetric = false
FEATURE [Part::Feature] Face114
  shape: bbox 3.2 x 1.5 x 2e-07 mm, 1 faces, 0 solids (baked)
FEATURE [Part::Feature] Face115
  shape: bbox 3.2 x 1.5 x 2e-07 mm, 1 faces, 0 solids (baked)
FEATURE [Part::Feature] Face116
  shape: bbox 3.2 x 1.5 x 2e-07 mm, 1 faces, 0 solids (baked)
FEATURE [Part::Revolution] Revolve122  label="frontCaseScrewRetainer004"
  Angle = 360
  Axis = (0,1,0)
  Base = (0,0,0)
  FaceMakerClass = Part::FaceMakerBullseye
  Placement = pos=(89.5,3,68.5) rot=(0,0,1;0rad)
  Solid = false
  Source = -> Face115
  Symmetric = false
FEATURE [Part::Revolution] Revolve123  label="frontCaseScrewRetainer005"
  Angle = 360
  Axis = (0,1,0)
  Base = (0,0,0)
  FaceMakerClass = Part::FaceMakerBullseye
  Placement = pos=(89.5,3,3.5) rot=(0,0,1;0rad)
  Solid = false
  Source = -> Face116
  Symmetric = false
FEATURE [Part::Revolution] Revolve124  label="backCaseScrewRetainer003"
  Angle = 360
  Axis = (0,1,0)
  Base = (0,0,0)
  FaceMakerClass = Part::FaceMakerBullseye
  Placement = pos=(12.5,3,10) rot=(0,0,1;0rad)
  Solid = false
  Source = -> Face114
  Symmetric = false
FEATURE [Part::Feature] Face117
  shape: bbox 3.6 x 3.2 x 2e-07 mm, 1 faces, 0 solids (baked)
FEATURE [Part::Revolution] Revolve125  label="moreFrontCaseScrewRetainer004"
  Angle = 360
  Axis = (0,1,0)
  Base = (0,0,0)
  FaceMakerClass = Part::FaceMakerBullseye
  Placement = pos=(109.5,4.5,68.5) rot=(0,0,1;0rad)
  Solid = false
  Source = -> Face117
  Symmetric = false
FEATURE [Part::Feature] Face118
  shape: bbox 3.6 x 3.2 x 2e-07 mm, 1 faces, 0 solids (baked)
FEATURE [Part::Revolution] Revolve126  label="moreFrontCaseScrewRetainer005"
  Angle = 360
  Axis = (0,1,0)
  Base = (0,0,0)
  FaceMakerClass = Part::FaceMakerBullseye
  Placement = pos=(109.5,4.5,3.5) rot=(0,0,1;0rad)
  Solid = false
  Source = -> Face118
  Symmetric = false
FEATURE [Part::MultiFuse] Fusion096  label="screwRetainers001"
  Shapes = -> [Revolve126,Revolve125,Revolve124,Revolve123,Revolve122,Revolve121]
FEATURE [Part::Feature] Face119
  shape: bbox 10 x 16.5 x 2e-07 mm, 1 faces, 0 solids (baked)
FEATURE [Part::Revolution] Revolve130  label="plugHousing050"
  Angle = 360
  Axis = (0,1,0)
  Base = (0,0,0)
  FaceMakerClass = Part::FaceMakerBullseye
  Placement = pos=(0,0,36.15) rot=(0,0,1;0rad)
  Solid = false
  Source = -> Face119
  Symmetric = false
FEATURE [Part::Feature] Face120
  shape: bbox 10 x 16.5 x 2e-07 mm, 1 faces, 0 solids (baked)
FEATURE [Part::Feature] Face121
  shape: bbox 10 x 16.5 x 2e-07 mm, 1 faces, 0 solids (baked)
FEATURE [Part::Revolution] Revolve127  label="plugHousing047"
  Angle = 360
  Axis = (0,1,0)
  Base = (0,0,0)
  FaceMakerClass = Part::FaceMakerBullseye
  Placement = pos=(0,0,36.15) rot=(0,0,1;0rad)
  Solid = false
  Source = -> Face121
  Symmetric = false
FEATURE [Part::Feature] Face122
  shape: bbox 10 x 16.5 x 2e-07 mm, 1 faces, 0 solids (baked)
FEATURE [Part::Feature] Face123
  shape: bbox 10 x 16.5 x 2e-07 mm, 1 faces, 0 solids (baked)
FEATURE [Part::Revolution] Revolve128  label="plugHousing048"
  Angle = 360
  Axis = (0,1,0)
  Base = (0,0,0)
  FaceMakerClass = Part::FaceMakerBullseye
  Placement = pos=(0,0,36.15) rot=(0,0,1;0rad)
  Solid = false
  Source = -> Face123
  Symmetric = false
FEATURE [Part::MultiFuse] Fusion100  label="plugHousing054"
  Placement = pos=(0,0,0) rot=(0,0,1;1.5708rad)
  Shapes = -> [Revolve130,Revolve128]
FEATURE [Part::Feature] Face124
  shape: bbox 10 x 16.5 x 2e-07 mm, 1 faces, 0 solids (baked)
FEATURE [Part::Feature] Face125
  shape: bbox 10 x 16.5 x 2e-07 mm, 1 faces, 0 solids (baked)
FEATURE [Part::Revolution] Revolve129  label="plugHousing049"
  Angle = 360
  Axis = (0,1,0)
  Base = (0,0,0)
  FaceMakerClass = Part::FaceMakerBullseye
  Placement = pos=(0,0,36.15) rot=(0,0,1;0rad)
  Solid = false
  Source = -> Face125
  Symmetric = false
FEATURE [Part::Feature] Face126
  shape: bbox 10 x 16.5 x 2e-07 mm, 1 faces, 0 solids (baked)
FEATURE [Part::Revolution] Revolve131  label="plugHousing058"
  Angle = 360
  Axis = (0,1,0)
  Base = (0,0,0)
  FaceMakerClass = Part::FaceMakerBullseye
  Placement = pos=(0,0,36.15) rot=(0,0,1;0rad)
  Solid = false
  Source = -> Face120
  Symmetric = false
FEATURE [Part::MultiFuse] Fusion099  label="plugHousing053"
  Placement = pos=(0,0,0) rot=(0,0,1;1.5708rad)
  Shapes = -> [Revolve127,Revolve131]
FEATURE [Part::MultiFuse] Fusion102  label="plugHousing056"
  Placement = pos=(0,19,0) rot=(0,0,1;3.14159rad)
  Shapes = -> [Fusion100,Fusion099]
FEATURE [Part::Revolution] Revolve132  label="plugHousing059"
  Angle = 360
  Axis = (0,1,0)
  Base = (0,0,0)
  FaceMakerClass = Part::FaceMakerBullseye
  Placement = pos=(0,0,36.15) rot=(0,0,1;0rad)
  Solid = false
  Source = -> Face126
  Symmetric = false
FEATURE [Part::Revolution] Revolve133  label="plugHousing060"
  Angle = 360
  Axis = (0,1,0)
  Base = (0,0,0)
  FaceMakerClass = Part::FaceMakerBullseye
  Placement = pos=(0,0,36.15) rot=(0,0,1;0rad)
  Solid = false
  Source = -> Face122
  Symmetric = false
FEATURE [Part::MultiFuse] Fusion097  label="plugHousing051"
  Placement = pos=(0,0,0) rot=(0,0,1;1.5708rad)
  Shapes = -> [Revolve133,Revolve132]
FEATURE [Part::Revolution] Revolve134  label="plugHousing061"
  Angle = 360
  Axis = (0,1,0)
  Base = (0,0,0)
  FaceMakerClass = Part::FaceMakerBullseye
  Placement = pos=(0,0,36.15) rot=(0,0,1;0rad)
  Solid = false
  Source = -> Face124
  Symmetric = false
FEATURE [Part::MultiFuse] Fusion101  label="plugHousing055"
  Placement = pos=(0,0,0) rot=(0,0,1;1.5708rad)
  Shapes = -> [Revolve129,Revolve134]
FEATURE [Part::MultiFuse] Fusion098  label="plugHousing052"
  Placement = pos=(0,19,0) rot=(0,0,1;3.14159rad)
  Shapes = -> [Fusion097,Fusion101]
FEATURE [Part::MultiFuse] Fusion103  label="plugHousing057"
  Placement = pos=(122.621,0,-0.15) rot=(0,0,1;0rad)
  Shapes = -> [Fusion102,Fusion098]
FEATURE [Part::Box] Box028  label="Cube015"
  AttacherType = Attacher::AttachEngine3D
  Height = 28
  Length = 3
  Placement = pos=(110.7,19,22) rot=(0,0,1;0rad)
  Width = 15.7
FEATURE [Part::Cylinder] Cylinder044
  Angle = 360
  AttacherType = Attacher::AttachEngine3D
  Height = 20
  Placement = pos=(0,0,36.15) rot=(0,0,1;0rad)
  Radius = 10.3
FEATURE [Part::Cylinder] Cylinder045
  Angle = 360
  AttacherType = Attacher::AttachEngine3D
  Height = 10
  Placement = pos=(0,0,36.15) rot=(0,0,1;0rad)
  Radius = 4
FEATURE [Part::MultiFuse] Fusion104  label="removeToCreteHoleForPlugHousing040"
  Placement = pos=(70,19,36) rot=(0,1,0;1.5708rad)
  Shapes = -> [Cylinder044,Cylinder045]
FEATURE [Part::Cut] Cut046  label="plugHousingTab003"
  Base = -> Box028
  Tool = -> Fusion104
FEATURE [Part::MultiFuse] Fusion105  label="plugHousing062"
  Shapes = -> [Fusion103,Cut046]
FEATURE [Part::Fillet] Fillet042
  Base = -> Fusion105
  Edges = 1 edges r=2: [Edge25]
FEATURE [Part::Fillet] Fillet043  label="plugHousing063"
  Base = -> Fillet042
  Edges = 1 edges r=2: [Edge8]
  Placement = pos=(7,0,0) rot=(0,0,1;0rad)
FEATURE [Part::Feature] Face127
  shape: bbox 10 x 16.5 x 2e-07 mm, 1 faces, 0 solids (baked)
FEATURE [Part::Feature] Face128
  shape: bbox 10 x 16.5 x 2e-07 mm, 1 faces, 0 solids (baked)
FEATURE [Part::Revolution] Revolve137  label="plugHousing070"
  Angle = 360
  Axis = (0,1,0)
  Base = (0,0,0)
  FaceMakerClass = Part::FaceMakerBullseye
  Placement = pos=(0,0,36.15) rot=(0,0,1;0rad)
  Solid = false
  Source = -> Face127
  Symmetric = false
FEATURE [Part::Revolution] Revolve140  label="plugHousing073"
  Angle = 360
  Axis = (0,1,0)
  Base = (0,0,0)
  FaceMakerClass = Part::FaceMakerBullseye
  Placement = pos=(0,0,36.15) rot=(0,0,1;0rad)
  Solid = false
  Source = -> Face128
  Symmetric = false
FEATURE [Part::Feature] Face129
  shape: bbox 10 x 16.5 x 2e-07 mm, 1 faces, 0 solids (baked)
FEATURE [Part::Revolution] Revolve138  label="plugHousing071"
  Angle = 360
  Axis = (0,1,0)
  Base = (0,0,0)
  FaceMakerClass = Part::FaceMakerBullseye
  Placement = pos=(0,0,36.15) rot=(0,0,1;0rad)
  Solid = false
  Source = -> Face129
  Symmetric = false
FEATURE [Part::Feature] Face130
  shape: bbox 10 x 16.5 x 2e-07 mm, 1 faces, 0 solids (baked)
FEATURE [Part::Revolution] Revolve139  label="plugHousing072"
  Angle = 360
  Axis = (0,1,0)
  Base = (0,0,0)
  FaceMakerClass = Part::FaceMakerBullseye
  Placement = pos=(0,0,36.15) rot=(0,0,1;0rad)
  Solid = false
  Source = -> Face130
  Symmetric = false
FEATURE [Part::Feature] Face131
  shape: bbox 10 x 16.5 x 2e-07 mm, 1 faces, 0 solids (baked)
FEATURE [Part::Revolution] Revolve135  label="plugHousing068"
  Angle = 360
  Axis = (0,1,0)
  Base = (0,0,0)
  FaceMakerClass = Part::FaceMakerBullseye
  Placement = pos=(0,0,36.15) rot=(0,0,1;0rad)
  Solid = false
  Source = -> Face131
  Symmetric = false
FEATURE [Part::MultiFuse] Fusion112  label="plugHousing078"
  Placement = pos=(0,0,0) rot=(0,0,1;1.5708rad)
  Shapes = -> [Revolve135,Revolve139]
FEATURE [Part::Feature] Face132
  shape: bbox 10 x 16.5 x 2e-07 mm, 1 faces, 0 solids (baked)
FEATURE [Part::Revolution] Revolve141  label="plugHousing074"
  Angle = 360
  Axis = (0,1,0)
  Base = (0,0,0)
  FaceMakerClass = Part::FaceMakerBullseye
  Placement = pos=(0,0,36.15) rot=(0,0,1;0rad)
  Solid = false
  Source = -> Face132
  Symmetric = false
FEATURE [Part::MultiFuse] Fusion110  label="plugHousing076"
  Placement = pos=(0,0,0) rot=(0,0,1;1.5708rad)
  Shapes = -> [Revolve141,Revolve140]
FEATURE [Part::Feature] Face133
  shape: bbox 10 x 16.5 x 2e-07 mm, 1 faces, 0 solids (baked)
FEATURE [Part::Revolution] Revolve136  label="plugHousing069"
  Angle = 360
  Axis = (0,1,0)
  Base = (0,0,0)
  FaceMakerClass = Part::FaceMakerBullseye
  Placement = pos=(0,0,36.15) rot=(0,0,1;0rad)
  Solid = false
  Source = -> Face133
  Symmetric = false
FEATURE [Part::MultiFuse] Fusion106  label="plugHousing064"
  Placement = pos=(0,0,0) rot=(0,0,1;1.5708rad)
  Shapes = -> [Revolve138,Revolve136]
FEATURE [Part::MultiFuse] Fusion108  label="plugHousing066"
  Placement = pos=(0,19,0) rot=(0,0,1;3.14159rad)
  Shapes = -> [Fusion106,Fusion112]
FEATURE [Part::Feature] Face134
  shape: bbox 10 x 16.5 x 2e-07 mm, 1 faces, 0 solids (baked)
FEATURE [Part::Revolution] Revolve142  label="plugHousing075"
  Angle = 360
  Axis = (0,1,0)
  Base = (0,0,0)
  FaceMakerClass = Part::FaceMakerBullseye
  Placement = pos=(0,0,36.15) rot=(0,0,1;0rad)
  Solid = false
  Source = -> Face134
  Symmetric = false
FEATURE [Part::MultiFuse] Fusion107  label="plugHousing065"
  Placement = pos=(0,0,0) rot=(0,0,1;1.5708rad)
  Shapes = -> [Revolve137,Revolve142]
FEATURE [Part::MultiFuse] Fusion111  label="plugHousing077"
  Placement = pos=(0,19,0) rot=(0,0,1;3.14159rad)
  Shapes = -> [Fusion110,Fusion107]
FEATURE [Part::MultiFuse] Fusion109  label="plugHousing067"
  Placement = pos=(131.236,0,-0.15) rot=(0,0,1;0rad)
  Shapes = -> [Fusion108,Fusion111]
FEATURE [Part::MultiFuse] Fusion113  label="plugHousing079"
  Shapes = -> [Fillet043,Fusion109]
FEATURE [Part::Feature] Face135
  shape: bbox 3.5 x 17.8 x 2e-07 mm, 1 faces, 0 solids (baked)
FEATURE [Part::Revolution] Revolve143  label="removeToCreateScrewAndThreadedInsertHole049"
  Angle = 360
  Axis = (0,1,0)
  Base = (0,0,0)
  FaceMakerClass = Part::FaceMakerBullseye
  Placement = pos=(12.5,0,10) rot=(0,0,1;0rad)
  Solid = false
  Source = -> Face135
  Symmetric = false
FEATURE [Part::Feature] Face136
  shape: bbox 3.5 x 17.8 x 2e-07 mm, 1 faces, 0 solids (baked)
FEATURE [Part::Revolution] Revolve144  label="removeToCreateScrewAndThreadedInsertHole050"
  Angle = 360
  Axis = (0,1,0)
  Base = (0,0,0)
  FaceMakerClass = Part::FaceMakerBullseye
  Placement = pos=(12.5,0,62) rot=(0,0,1;0rad)
  Solid = false
  Source = -> Face136
  Symmetric = false
FEATURE [Part::Feature] Face137
  shape: bbox 3.5 x 17.8 x 2e-07 mm, 1 faces, 0 solids (baked)
FEATURE [Part::Revolution] Revolve145  label="removeToCreateScrewAndThreadedInsertHole051"
  Angle = 360
  Axis = (0,1,0)
  Base = (0,0,0)
  FaceMakerClass = Part::FaceMakerBullseye
  Placement = pos=(89.5,0,68.5) rot=(0,0,1;0rad)
  Solid = false
  Source = -> Face137
  Symmetric = false
FEATURE [Part::Feature] Face138
  shape: bbox 3.5 x 17.8 x 2e-07 mm, 1 faces, 0 solids (baked)
FEATURE [Part::Revolution] Revolve146  label="removeToCreateScrewAndThreadedInsertHole052"
  Angle = 360
  Axis = (0,1,0)
  Base = (0,0,0)
  FaceMakerClass = Part::FaceMakerBullseye
  Placement = pos=(89.5,0,3.5) rot=(0,0,1;0rad)
  Solid = false
  Source = -> Face138
  Symmetric = false
FEATURE [Part::Feature] Face139
  shape: bbox 3.5 x 17.8 x 2e-07 mm, 1 faces, 0 solids (baked)
FEATURE [Part::Revolution] Revolve147  label="removeToCreateScrewAndThreadedInsertHole053"
  Angle = 360
  Axis = (0,1,0)
  Base = (0,0,0)
  FaceMakerClass = Part::FaceMakerBullseye
  Placement = pos=(109.5,4.7,3.5) rot=(0,0,1;0rad)
  Solid = false
  Source = -> Face139
  Symmetric = false
FEATURE [Part::Feature] Face140
  shape: bbox 3.5 x 17.8 x 2e-07 mm, 1 faces, 0 solids (baked)
FEATURE [Part::Revolution] Revolve148  label="removeToCreateScrewAndThreadedInsertHole054"
  Angle = 360
  Axis = (0,1,0)
  Base = (0,0,0)
  FaceMakerClass = Part::FaceMakerBullseye
  Placement = pos=(109.5,4.7,68.5) rot=(0,0,1;0rad)
  Solid = false
  Source = -> Face140
  Symmetric = false
FEATURE [Part::MultiFuse] Fusion114  label="removeToCreateScrewAndThreadedInsertHole055"
  Shapes = -> [Revolve148,Revolve147,Revolve146,Revolve145,Revolve144,Revolve143]
FEATURE [Part::Cut] Cut047  label="casePillars004"
  Base = -> Cut037
  Tool = -> Fusion114
FEATURE [Part::Feature] Face141
  shape: bbox 3.5 x 17.8 x 2e-07 mm, 1 faces, 0 solids (baked)
FEATURE [Part::Feature] Face142
  shape: bbox 3.5 x 17.8 x 2e-07 mm, 1 faces, 0 solids (baked)
FEATURE [Part::Feature] Face143
  shape: bbox 3.5 x 17.8 x 2e-07 mm, 1 faces, 0 solids (baked)
FEATURE [Part::Revolution] Revolve149  label="removeToCreateScrewAndThreadedInsertHole057"
  Angle = 360
  Axis = (0,1,0)
  Base = (0,0,0)
  FaceMakerClass = Part::FaceMakerBullseye
  Placement = pos=(12.5,0,10) rot=(0,0,1;0rad)
  Solid = false
  Source = -> Face141
  Symmetric = false
FEATURE [Part::Feature] Face144
  shape: bbox 3.5 x 17.8 x 2e-07 mm, 1 faces, 0 solids (baked)
FEATURE [Part::Feature] Face145
  shape: bbox 3.5 x 17.8 x 2e-07 mm, 1 faces, 0 solids (baked)
FEATURE [Part::Feature] Face146
  shape: bbox 3.5 x 17.8 x 2e-07 mm, 1 faces, 0 solids (baked)
FEATURE [Part::Revolution] Revolve150  label="removeToCreateScrewAndThreadedInsertHole058"
  Angle = 360
  Axis = (0,1,0)
  Base = (0,0,0)
  FaceMakerClass = Part::FaceMakerBullseye
  Placement = pos=(12.5,0,62) rot=(0,0,1;0rad)
  Solid = false
  Source = -> Face146
  Symmetric = false
FEATURE [Part::Revolution] Revolve151  label="removeToCreateScrewAndThreadedInsertHole059"
  Angle = 360
  Axis = (0,1,0)
  Base = (0,0,0)
  FaceMakerClass = Part::FaceMakerBullseye
  Placement = pos=(89.5,0,68.5) rot=(0,0,1;0rad)
  Solid = false
  Source = -> Face143
  Symmetric = false
FEATURE [Part::Revolution] Revolve152  label="removeToCreateScrewAndThreadedInsertHole060"
  Angle = 360
  Axis = (0,1,0)
  Base = (0,0,0)
  FaceMakerClass = Part::FaceMakerBullseye
  Placement = pos=(89.5,0,3.5) rot=(0,0,1;0rad)
  Solid = false
  Source = -> Face142
  Symmetric = false
FEATURE [Part::Revolution] Revolve153  label="removeToCreateScrewAndThreadedInsertHole061"
  Angle = 360
  Axis = (0,1,0)
  Base = (0,0,0)
  FaceMakerClass = Part::FaceMakerBullseye
  Placement = pos=(109.5,4.7,3.5) rot=(0,0,1;0rad)
  Solid = false
  Source = -> Face145
  Symmetric = false
FEATURE [Part::Revolution] Revolve154  label="removeToCreateScrewAndThreadedInsertHole062"
  Angle = 360
  Axis = (0,1,0)
  Base = (0,0,0)
  FaceMakerClass = Part::FaceMakerBullseye
  Placement = pos=(109.5,4.7,68.5) rot=(0,0,1;0rad)
  Solid = false
  Source = -> Face144
  Symmetric = false
FEATURE [Part::MultiFuse] Fusion115  label="removeToCreateScrewAndThreadedInsertHole056"
  Shapes = -> [Revolve154,Revolve153,Revolve152,Revolve151,Revolve150,Revolve149]
FEATURE [Part::Feature] Face147
  shape: bbox 9.8 x 26.5 x 2e-07 mm, 1 faces, 0 solids (baked)
FEATURE [Part::Revolution] Revolve155
  Angle = 360
  Axis = (0,1,0)
  Base = (0,0,0)
  FaceMakerClass = Part::FaceMakerBullseye
  Placement = pos=(0,0,0) rot=(0,0,1;1.5708rad)
  Solid = false
  Source = -> Face147
  Symmetric = false
FEATURE [Part::Feature] Face148
  shape: bbox 9.8 x 26.5 x 2e-07 mm, 1 faces, 0 solids (baked)
FEATURE [Part::Revolution] Revolve156
  Angle = 360
  Axis = (0,1,0)
  Base = (0,0,0)
  FaceMakerClass = Part::FaceMakerBullseye
  Placement = pos=(0,0,0) rot=(0,0,1;1.5708rad)
  Solid = false
  Source = -> Face148
  Symmetric = false
FEATURE [Part::MultiFuse] Fusion116
  Placement = pos=(-18,19,36) rot=(0,0,1;0rad)
  Shapes = -> [Revolve156,Revolve155]
FEATURE [Part::Box] Box029  label="Cube016"
  AttacherType = Attacher::AttachEngine3D
  Height = 28
  Length = 3
  Placement = pos=(110.7,19,22) rot=(0,0,1;0rad)
  Width = 15.7
FEATURE [Part::Cylinder] Cylinder046
  Angle = 360
  AttacherType = Attacher::AttachEngine3D
  Height = 10
  Placement = pos=(0,0,36.15) rot=(0,0,1;0rad)
  Radius = 4
FEATURE [Part::Cylinder] Cylinder047
  Angle = 360
  AttacherType = Attacher::AttachEngine3D
  Height = 20
  Placement = pos=(0,0,36.15) rot=(0,0,1;0rad)
  Radius = 10.3
FEATURE [Part::MultiFuse] Fusion117  label="removeToCreteHoleForPlugHousing041"
  Placement = pos=(70,19,36) rot=(0,1,0;1.5708rad)
  Shapes = -> [Cylinder047,Cylinder046]
FEATURE [Part::Cut] Cut049  label="plugHousingTab004"
  Base = -> Box029
  Placement = pos=(-107.4,-14,0) rot=(0,0,1;0rad)
  Tool = -> Fusion117
FEATURE [Part::Box] Box030  label="Cube017"
  AttacherType = Attacher::AttachEngine3D
  Height = 28
  Length = 3
  Placement = pos=(110.7,19,22) rot=(0,0,1;0rad)
  Width = 15.7
FEATURE [Part::Cylinder] Cylinder048
  Angle = 360
  AttacherType = Attacher::AttachEngine3D
  Height = 10
  Placement = pos=(0,0,36.15) rot=(0,0,1;0rad)
  Radius = 4
FEATURE [Part::Cylinder] Cylinder049
  Angle = 360
  AttacherType = Attacher::AttachEngine3D
  Height = 20
  Placement = pos=(0,0,36.15) rot=(0,0,1;0rad)
  Radius = 10.3
FEATURE [Part::MultiFuse] Fusion118  label="removeToCreteHoleForPlugHousing042"
  Placement = pos=(70,19,36) rot=(0,1,0;1.5708rad)
  Shapes = -> [Cylinder049,Cylinder048]
FEATURE [Part::Cut] Cut050  label="plugHousingTab005"
  Base = -> Box030
  Placement = pos=(-107.4,-14,0) rot=(0,0,1;0rad)
  Tool = -> Fusion118
FEATURE [Part::MultiFuse] Fusion119
  Placement = pos=(9.6,23,0) rot=(0,0,1;3.14159rad)
  Shapes = -> [Cut049,Cut050]
FEATURE [Part::Box] Box031  label="Cube018"
  AttacherType = Attacher::AttachEngine3D
  Height = 10
  Length = 3
  Placement = pos=(3.3,4,12) rot=(0,0,1;0rad)
  Width = 10
FEATURE [Part::Fillet] Fillet044
  Base = -> Box031
  Edges = 1 edges r=2: [Edge11]
FEATURE [Part::Box] Box032  label="Cube019"
  AttacherType = Attacher::AttachEngine3D
  Height = 10
  Length = 3
  Placement = pos=(3.3,4,50) rot=(0,0,1;0rad)
  Width = 10
FEATURE [Part::Fillet] Fillet045
  Base = -> Box032
  Edges = 1 edges r=2: [Edge12]
FEATURE [Part::Box] Box033  label="Cube020"
  AttacherType = Attacher::AttachEngine3D
  Height = 28
  Length = 4
  Placement = pos=(5,0,22) rot=(0,0,1;0rad)
  Width = 10
FEATURE [Part::Fillet] Fillet046
  Base = -> Box033
  Edges = 1 edges r=1: [Edge7]
FEATURE [Part::Fillet] Fillet047
  Base = -> Fillet046
  Edges = 1 edges r=2: [Edge5]
FEATURE [Part::Fillet] Fillet048
  Base = -> Fillet047
  Edges = 1 edges r=2: [Edge2]
FEATURE [Part::Cylinder] Cylinder050
  Angle = 360
  AttacherType = Attacher::AttachEngine3D
  Height = 20
  Placement = pos=(0,0,36.15) rot=(0,0,1;0rad)
  Radius = 8.2
FEATURE [Part::Cylinder] Cylinder051
  Angle = 360
  AttacherType = Attacher::AttachEngine3D
  Height = 10
  Placement = pos=(0,0,36.15) rot=(0,0,1;0rad)
  Radius = 4
FEATURE [Part::MultiFuse] Fusion120  label="removeToCreteHoleForPlugHousing043"
  Placement = pos=(-42,19,36) rot=(0,1,0;1.5708rad)
  Shapes = -> [Cylinder050,Cylinder051]
FEATURE [Sketcher::SketchObject] Sketch067  label="topSketch018"
  FullyConstrained = true
  sketch-geometry (4):
    g0: LineSegment StartX=16.8446 StartY=31.512 StartZ=0 EndX=16.3251 EndY=34.4666 EndZ=0
    g1: ArcOfCircle CenterX=19 CenterY=19.2524 CenterZ=0 NormalX=0 NormalY=0 NormalZ=1 AngleXU=0 Radius=15.4476 StartAngle=1.74483 EndAngle=2.72717
    g2: ArcOfCircle CenterX=19 CenterY=19.2524 CenterZ=0 NormalX=0 NormalY=0 NormalZ=1 AngleXU=0 Radius=12.4476 StartAngle=1.74483 EndAngle=2.73189
    g3: LineSegment StartX=4.86004 StartY=25.4725 StartZ=0 EndX=7.58253 EndY=24.2107 EndZ=0
  constraints (7):
    c: Block(g0)
    c: Coincident(g1,g0)
    c: Coincident(g2,g0)
    c: Coincident(g3,g1)
    c: Coincident(g3,g2)
    c: Block(g1)
    c: Block(g2)
FEATURE [Part::Extrusion] Extrude058
  Base = -> Sketch067
  Dir = (0,0,1)
  DirMode = 2
  FaceMakerClass = Part::FaceMakerBullseye
  LengthFwd = 10
  LengthRev = 0
  Placement = pos=(0,0,31) rot=(0,0,1;0rad)
  Solid = true
  Symmetric = false
FEATURE [Part::Cut] Cut051
  Base = -> Extrude058
  Tool = -> Fusion120
FEATURE [Part::Fillet] Fillet049
  Base = -> Cut051
  Edges = 1 edges r=2: [Edge1]
FEATURE [Part::Fillet] Fillet050
  Base = -> Fillet049
  Edges = 1 edges r=2.5: [Edge1]
FEATURE [Part::Fillet] Fillet051
  Base = -> Fillet050
  Edges = 1 edges r=2.5: [Edge2]
FEATURE [Part::MultiFuse] Fusion121  label="wireHolder003"
  Shapes = -> [Fusion116,Fillet051]
FEATURE [Part::MultiFuse] Fusion122
  Shapes = -> [Fillet045,Fusion121]
FEATURE [Part::MultiFuse] Fusion123  label="wireHolder004"
  Shapes = -> [Fusion122,Fillet048]
FEATURE [Part::MultiFuse] Fusion124  label="wireHolder005"
  Shapes = -> [Fillet044,Fusion119,Fusion123]
FEATURE [Sketcher::SketchObject] Sketch068  label="topSketch019"
  FullyConstrained = true
  sketch-geometry (6):
    g0: LineSegment StartX=19 StartY=38 StartZ=0 EndX=117 EndY=38 EndZ=0
    g1: ArcOfCircle CenterX=19 CenterY=19 CenterZ=0 NormalX=0 NormalY=0 NormalZ=1 AngleXU=0 Radius=19 StartAngle=1.5708 EndAngle=3.14159
    g2: LineSegment StartX=117 StartY=38 StartZ=0 EndX=117 EndY=19 EndZ=0
    g3: LineSegment StartX=98 StartY=1.0161e-12 StartZ=0 EndX=5.22862e-06 EndY=1.0161e-12 EndZ=0
    g4: LineSegment StartX=5.22862e-06 StartY=19 StartZ=0 EndX=5.22862e-06 EndY=1.0161e-12 EndZ=0
    g5: ArcOfCircle CenterX=98 CenterY=19 CenterZ=0 NormalX=0 NormalY=0 NormalZ=1 AngleXU=0 Radius=19 StartAngle=4.71239 EndAngle=6.28319
  constraints (16):
    c: Horizontal(g0)
    c: Distance(g0) = 98
    c: Coincident(g1,g0)
    c: Block(g1)
    c: Coincident(g2,g0)
    c: Vertical(g2)
    c: Distance(g2) = 19
    c: Horizontal(g3)
    c: Coincident(g4,g1)
    c: Vertical(g4)
    c: Coincident(g3,g4)
    c: Block(g3)
    c: Coincident(g5,g2)
    c: Coincident(g5,g3)
    c: Block(g0)
    c: Block(g5)
FEATURE [Part::Extrusion] Extrude059  label="sideA002"
  Base = -> Sketch068
  Dir = (0,0,1)
  DirMode = 2
  FaceMakerClass = Part::FaceMakerBullseye
  LengthFwd = 3
  LengthRev = 0
  Placement = pos=(0,0,-2.7) rot=(0,0,1;0rad)
  Solid = true
  Symmetric = false
FEATURE [Sketcher::SketchObject] Sketch069  label="topSketch020"
  FullyConstrained = true
  sketch-geometry (6):
    g0: LineSegment StartX=19 StartY=38 StartZ=0 EndX=117 EndY=38 EndZ=0
    g1: ArcOfCircle CenterX=19 CenterY=19 CenterZ=0 NormalX=0 NormalY=0 NormalZ=1 AngleXU=0 Radius=19 StartAngle=1.5708 EndAngle=3.14159
    g2: LineSegment StartX=117 StartY=38 StartZ=0 EndX=117 EndY=19 EndZ=0
    g3: LineSegment StartX=98 StartY=1.0161e-12 StartZ=0 EndX=5.22862e-06 EndY=1.0161e-12 EndZ=0
    g4: LineSegment StartX=5.22862e-06 StartY=19 StartZ=0 EndX=5.22862e-06 EndY=1.0161e-12 EndZ=0
    g5: ArcOfCircle CenterX=98 CenterY=19 CenterZ=0 NormalX=0 NormalY=0 NormalZ=1 AngleXU=0 Radius=19 StartAngle=4.71239 EndAngle=6.28319
  constraints (16):
    c: Horizontal(g0)
    c: Distance(g0) = 98
    c: Coincident(g1,g0)
    c: Block(g1)
    c: Coincident(g2,g0)
    c: Vertical(g2)
    c: Distance(g2) = 19
    c: Horizontal(g3)
    c: Coincident(g4,g1)
    c: Vertical(g4)
    c: Coincident(g3,g4)
    c: Block(g3)
    c: Coincident(g5,g2)
    c: Coincident(g5,g3)
    c: Block(g0)
    c: Block(g5)
FEATURE [Part::Extrusion] Extrude060  label="sideB002"
  Base = -> Sketch069
  Dir = (0,0,1)
  DirMode = 2
  FaceMakerClass = Part::FaceMakerBullseye
  LengthFwd = 3
  LengthRev = 0
  Placement = pos=(0,0,71.7) rot=(0,0,1;0rad)
  Solid = true
  Symmetric = false
FEATURE [Part::MultiFuse] Fusion127  label="removeFromBottom001"
  Placement = pos=(2,0,0) rot=(0,0,1;0rad)
  Shapes = -> [Extrude059,Extrude060]
FEATURE [Part::Cylinder] Cylinder052
  Angle = 360
  AttacherType = Attacher::AttachEngine3D
  Height = 20
  Placement = pos=(0,0,36.15) rot=(0,0,1;0rad)
  Radius = 14
FEATURE [Part::Cylinder] Cylinder053
  Angle = 360
  AttacherType = Attacher::AttachEngine3D
  Height = 10
  Placement = pos=(0,0,36.15) rot=(0,0,1;0rad)
  Radius = 4
FEATURE [Part::MultiFuse] Fusion128  label="removeToCreteHoleForPlugHousing044"
  Placement = pos=(70,19,36) rot=(0,1,0;1.5708rad)
  Shapes = -> [Cylinder052,Cylinder053]
FEATURE [Part::Cut] Cut052  label="bottom011"
  Base = -> Extrude043
  Tool = -> Fusion128
FEATURE [Part::Cut] Cut054  label="bottom012"
  Base = -> Cut052
  Tool = -> Fusion115
FEATURE [Sketcher::SketchObject] Sketch070
  FullyConstrained = true
  Placement = pos=(117,19,0) rot=(0.57735,0.57735,0.57735;2.0944rad)
  sketch-geometry (48):
    g0: LineSegment StartX=-49.19 StartY=69.25 StartZ=0 EndX=-49.19 EndY=66.25 EndZ=0
    g1: LineSegment StartX=-49.19 StartY=63.5 StartZ=0 EndX=-49.19 EndY=60.5 EndZ=0
    g2: LineSegment StartX=-49.19 StartY=57.75 StartZ=0 EndX=-49.19 EndY=54.75 EndZ=0
    g3: LineSegment StartX=-49.19 StartY=52 StartZ=0 EndX=-49.19 EndY=49 EndZ=0
    g4: LineSegment StartX=-49.19 StartY=46.25 StartZ=0 EndX=-49.19 EndY=43.25 EndZ=0
    g5: LineSegment StartX=-49.19 StartY=40.5 StartZ=0 EndX=-49.19 EndY=37.5 EndZ=0
    g6: LineSegment StartX=-49.19 StartY=34.5 StartZ=0 EndX=-49.19 EndY=31.5 EndZ=0
    g7: LineSegment StartX=-49.19 StartY=28.75 StartZ=0 EndX=-49.19 EndY=25.75 EndZ=0
    g8: LineSegment StartX=-49.19 StartY=23 StartZ=0 EndX=-49.19 EndY=20 EndZ=0
    g9: LineSegment StartX=-49.19 StartY=17.25 StartZ=0 EndX=-49.19 EndY=14.25 EndZ=0
    g10: LineSegment StartX=-49.19 StartY=11.5 StartZ=0 EndX=-49.19 EndY=8.5 EndZ=0
    g11: LineSegment StartX=-49.19 StartY=5.75 StartZ=0 EndX=-49.19 EndY=2.75 EndZ=0
    g12: ArcOfCircle CenterX=-1.5 CenterY=67.75 CenterZ=0 NormalX=0 NormalY=0 NormalZ=1 AngleXU=0 Radius=1.5 StartAngle=4.71239 EndAngle=7.85398
    g13: ArcOfCircle CenterX=-1.5 CenterY=62 CenterZ=0 NormalX=0 NormalY=0 NormalZ=1 AngleXU=0 Radius=1.5 StartAngle=4.71239 EndAngle=7.85398
    g14: ArcOfCircle CenterX=-1.5 CenterY=56.25 CenterZ=0 NormalX=0 NormalY=0 NormalZ=1 AngleXU=0 Radius=1.5 StartAngle=4.71239 EndAngle=7.85398
    g15: ArcOfCircle CenterX=-11.49 CenterY=50.5 CenterZ=0 NormalX=0 NormalY=0 NormalZ=1 AngleXU=0 Radius=1.5 StartAngle=4.71239 EndAngle=7.85398
    g16: ArcOfCircle CenterX=-16.28 CenterY=44.75 CenterZ=0 NormalX=0 NormalY=0 NormalZ=1 AngleXU=0 Radius=1.5 StartAngle=4.71239 EndAngle=7.85398
    g17: ArcOfCircle CenterX=-18.2337 CenterY=39 CenterZ=0 NormalX=0 NormalY=0 NormalZ=1 AngleXU=0 Radius=1.5 StartAngle=4.71485 EndAngle=7.85398
    g18: ArcOfCircle CenterX=-16.2837 CenterY=27.25 CenterZ=0 NormalX=0 NormalY=0 NormalZ=1 AngleXU=0 Radius=1.5 StartAngle=4.71485 EndAngle=7.85398
    g19: ArcOfCircle CenterX=-18.2337 CenterY=33 CenterZ=0 NormalX=0 NormalY=0 NormalZ=1 AngleXU=0 Radius=1.5 StartAngle=4.71485 EndAngle=7.85398
    g20: ArcOfCircle CenterX=-11.49 CenterY=21.5 CenterZ=0 NormalX=0 NormalY=0 NormalZ=1 AngleXU=0 Radius=1.5 StartAngle=4.71239 EndAngle=7.85398
    g21: ArcOfCircle CenterX=-1.5 CenterY=4.25 CenterZ=0 NormalX=0 NormalY=0 NormalZ=1 AngleXU=0 Radius=1.5 StartAngle=4.71239 EndAngle=7.85398
    g22: ArcOfCircle CenterX=-1.5 CenterY=10 CenterZ=0 NormalX=0 NormalY=0 NormalZ=1 AngleXU=0 Radius=1.5 StartAngle=4.71239 EndAngle=7.85398
    g23: ArcOfCircle CenterX=-1.5 CenterY=15.75 CenterZ=0 NormalX=0 NormalY=0 NormalZ=1 AngleXU=0 Radius=1.5 StartAngle=4.71239 EndAngle=7.85398
    g24: LineSegment StartX=-49.19 StartY=69.25 StartZ=0 EndX=-1.5 EndY=69.25 EndZ=0
    g25: LineSegment StartX=-49.19 StartY=66.25 StartZ=0 EndX=-1.5 EndY=66.25 EndZ=0
    g26: LineSegment StartX=-49.19 StartY=63.5 StartZ=0 EndX=-1.5 EndY=63.5 EndZ=0
    g27: LineSegment StartX=-49.19 StartY=60.5 StartZ=0 EndX=-1.5 EndY=60.5 EndZ=0
    g28: LineSegment StartX=-49.19 StartY=57.75 StartZ=0 EndX=-1.5 EndY=57.75 EndZ=0
    g29: LineSegment StartX=-49.19 StartY=54.75 StartZ=0 EndX=-1.5 EndY=54.75 EndZ=0
    g30: LineSegment StartX=-49.19 StartY=52 StartZ=0 EndX=-11.49 EndY=52 EndZ=0
    g31: LineSegment StartX=-49.19 StartY=49 StartZ=0 EndX=-11.49 EndY=49 EndZ=0
    g32: LineSegment StartX=-49.19 StartY=46.25 StartZ=0 EndX=-16.28 EndY=46.25 EndZ=0
    g33: LineSegment StartX=-49.19 StartY=43.25 StartZ=0 EndX=-16.28 EndY=43.25 EndZ=0
    g34: LineSegment StartX=-49.19 StartY=40.5 StartZ=0 EndX=-18.2337 EndY=40.5 EndZ=0
    g35: LineSegment StartX=-49.19 StartY=37.5 StartZ=0 EndX=-18.23 EndY=37.5 EndZ=0
    g36: LineSegment StartX=-49.19 StartY=34.5 StartZ=0 EndX=-18.2337 EndY=34.5 EndZ=0
    g37: LineSegment StartX=-49.19 StartY=31.5 StartZ=0 EndX=-18.23 EndY=31.5 EndZ=0
    g38: LineSegment StartX=-49.19 StartY=28.75 StartZ=0 EndX=-16.2837 EndY=28.75 EndZ=0
    g39: LineSegment StartX=-49.19 StartY=25.75 StartZ=0 EndX=-16.28 EndY=25.75 EndZ=0
    g40: LineSegment StartX=-49.19 StartY=23 StartZ=0 EndX=-11.49 EndY=23 EndZ=0
    g41: LineSegment StartX=-49.19 StartY=20 StartZ=0 EndX=-11.49 EndY=20 EndZ=0
    g42: LineSegment StartX=-49.19 StartY=17.25 StartZ=0 EndX=-1.5 EndY=17.25 EndZ=0
    g43: LineSegment StartX=-49.19 StartY=14.25 StartZ=0 EndX=-1.5 EndY=14.25 EndZ=0
    g44: LineSegment StartX=-49.19 StartY=11.5 StartZ=0 EndX=-1.5 EndY=11.5 EndZ=0
    g45: LineSegment StartX=-49.19 StartY=8.5 StartZ=0 EndX=-1.5 EndY=8.5 EndZ=0
    g46: LineSegment StartX=-49.19 StartY=5.75 StartZ=0 EndX=-1.5 EndY=5.75 EndZ=0
    g47: LineSegment StartX=-49.19 StartY=2.75 StartZ=0 EndX=-1.5 EndY=2.75 EndZ=0
  constraints (120):
    c: Vertical(g0)
    c: Distance(g0) = 3
    c: Block(g0)
    c: Vertical(g1)
    c: Distance(g1) = 3
    c: Vertical(g2)
    c: Equal(g0,g2) = 3
    c: Block(g2)
    c: Vertical(g3)
    c: Equal(g1,g3) = 3
    c: Vertical(g4)
    c: Equal(g0,g4) = 3
    c: Block(g4)
    c: Vertical(g5)
    c: Equal(g1,g5) = 3
    c: Vertical(g6)
    c: Equal(g0,g6) = 3
    c: Block(g6)
    c: Vertical(g7)
    c: Equal(g1,g7) = 3
    c: Vertical(g8)
    c: Equal(g0,g8) = 3
    c: Block(g8)
    c: Vertical(g9)
    c: Equal(g1,g9) = 3
    c: Vertical(g10)
    c: Equal(g0,g10) = 3
    c: Block(g10)
    c: Vertical(g11)
    c: Equal(g1,g11) = 3
    c: Block(g12)
    c: Block(g13)
    c: Block(g14)
    c: Block(g15)
    c: Block(g16)
    c: Block(g17)
    c: Block(g18)
    c: Block(g19)
    c: Block(g20)
    c: Block(g21)
    c: Block(g22)
    c: Block(g23)
    c: Block(g11)
    c: Block(g9)
    c: Block(g7)
    c: Block(g5)
    c: Block(g3)
    c: Block(g1)
    c: Coincident(g24,g0)
    c: Coincident(g24,g12)
    c: Horizontal(g24)
    c: Coincident(g25,g0)
    c: Coincident(g25,g12)
    c: Horizontal(g25)
    c: Coincident(g26,g1)
    c: Coincident(g26,g13)
    c: Horizontal(g26)
    c: Coincident(g27,g1)
    c: Coincident(g27,g13)
    c: Horizontal(g27)
    c: Coincident(g28,g2)
    c: Coincident(g28,g14)
    c: Horizontal(g28)
    c: Coincident(g29,g2)
    c: Coincident(g29,g14)
    c: Horizontal(g29)
    c: Coincident(g30,g3)
    c: Coincident(g30,g15)
    c: Horizontal(g30)
    c: Coincident(g31,g3)
    c: Coincident(g31,g15)
    c: Horizontal(g31)
    c: Coincident(g32,g4)
    c: Coincident(g32,g16)
    c: Horizontal(g32)
    c: Coincident(g33,g4)
    c: Coincident(g33,g16)
    c: Horizontal(g33)
    c: Coincident(g34,g5)
    c: Coincident(g34,g17)
    c: Horizontal(g34)
    c: Coincident(g35,g5)
    c: Coincident(g35,g17)
    c: Horizontal(g35)
    c: Coincident(g36,g6)
    c: Coincident(g36,g19)
    c: Horizontal(g36)
    c: Coincident(g37,g6)
    c: Coincident(g37,g19)
    c: Horizontal(g37)
    c: Coincident(g38,g7)
    c: Coincident(g38,g18)
    c: Horizontal(g38)
    c: Coincident(g39,g7)
    c: Coincident(g39,g18)
    c: Horizontal(g39)
    c: Coincident(g40,g8)
    c: Coincident(g40,g20)
    c: Horizontal(g40)
    c: Coincident(g41,g8)
    c: Coincident(g41,g20)
    c: Horizontal(g41)
    c: Coincident(g42,g9)
    c: Coincident(g42,g23)
    c: Horizontal(g42)
    c: Coincident(g43,g9)
    c: Coincident(g43,g23)
    c: Horizontal(g43)
    c: Coincident(g44,g10)
    c: Coincident(g44,g22)
    c: Horizontal(g44)
    c: Coincident(g45,g10)
    c: Coincident(g45,g22)
    c: Horizontal(g45)
    c: Coincident(g46,g11)
    c: Coincident(g46,g21)
    c: Horizontal(g46)
    c: Coincident(g47,g11)
    c: Coincident(g47,g21)
    c: Horizontal(g47)
FEATURE [Part::Extrusion] Extrude061
  Base = -> Sketch070
  Dir = (1,0,0)
  DirMode = 2
  FaceMakerClass = Part::FaceMakerBullseye
  LengthFwd = 23
  LengthRev = 0
  Placement = pos=(-19,0,0) rot=(0,0,1;0rad)
  Solid = true
  Symmetric = false
FEATURE [Part::Fillet] Fillet052  label="removeToCreateVentalationHoles002"
  Base = -> Extrude061
  Edges = <same value as first occurrence — deduplicated (x6 in doc)>
  Placement = pos=(7,0.02,0) rot=(0,0,1;0rad)
FEATURE [Part::MultiFuse] Fusion130  label="bottom013"
  Shapes = -> [Cut054,Cut034]
FEATURE [Part::Cut] Cut055
  Base = -> Fusion130
  Tool = -> Fillet052
FEATURE [Part::Cylinder] Cylinder054
  Angle = 360
  AttacherType = Attacher::AttachEngine3D
  Height = 20
  Placement = pos=(0,0,36.15) rot=(0,0,1;0rad)
  Radius = 4
FEATURE [Sketcher::SketchObject] Sketch071  label="bottomSketch002"
  FullyConstrained = true
  sketch-geometry (32):
    g0: LineSegment StartX=3.3 StartY=-6.03275e-07 StartZ=0 EndX=98 EndY=-6.03275e-07 EndZ=0
    g1: ArcOfCircle CenterX=98 CenterY=19 CenterZ=0 NormalX=0 NormalY=0 NormalZ=1 AngleXU=0 Radius=19 StartAngle=4.71239 EndAngle=5.71103
    g2: LineSegment StartX=6.3 StartY=8 StartZ=0 EndX=3.3 EndY=8 EndZ=0
    g3: LineSegment StartX=3.3 StartY=8 StartZ=0 EndX=3.3 EndY=-6.03275e-07 EndZ=0
    g4: ArcOfCircle CenterX=8.3 CenterY=5 CenterZ=0 NormalX=0 NormalY=0 NormalZ=1 AngleXU=0 Radius=2 StartAngle=3.14159 EndAngle=4.71239
    g5: LineSegment StartX=6.3 StartY=8 StartZ=0 EndX=6.3 EndY=5 EndZ=0
    g6: ArcOfCircle CenterX=98 CenterY=19 CenterZ=0 NormalX=0 NormalY=0 NormalZ=1 AngleXU=0 Radius=12.7 StartAngle=4.71239 EndAngle=6.28319
    g7: LineSegment StartX=94.7 StartY=3 StartZ=0 EndX=8.3 EndY=3 EndZ=0
    g8-g12: Circle x5 (B-spline internal-alignment scaffolding for g13; pole/knot coordinates omitted)
    g13: BSplineCurve PolesCount=5 KnotsCount=3 Degree=3 IsPeriodic=0
    g14: GeomPoint X=98 Y=6.3 Z=0
    g15: GeomPoint X=96.3938 Y=4.71946 Z=0
    g16: GeomPoint X=94.7 Y=3 Z=0
    g17-g23: Circle x7 (B-spline internal-alignment scaffolding for g24; pole/knot coordinates omitted)
    g24: BSplineCurve PolesCount=7 KnotsCount=5 Degree=3 IsPeriodic=0
    g25-g29: GeomPoint x5 (B-spline internal-alignment scaffolding for g24; pole/knot coordinates omitted)
    g30: ArcOfCircle CenterX=98 CenterY=19 CenterZ=0 NormalX=0 NormalY=0 NormalZ=1 AngleXU=0 Radius=15.7 StartAngle=5.81226 EndAngle=6.28319
    g31: LineSegment StartX=110.7 StartY=19 StartZ=0 EndX=113.7 EndY=19 EndZ=0
  constraints (41):
    c: Horizontal(g0)
    c: Coincident(g1,g0)
    c: Block(g1)
    c: Horizontal(g2)
    c: Distance(g2) = 3
    c: Coincident(g3,g2)
    c: Vertical(g3)
    c: Coincident(g3,g0)
    c: Block(g4)
    c: Block(g2)
    c: Coincident(g5,g2)
    c: Coincident(g5,g4)
    c: Vertical(g5)
    c: Coincident(g6,g1)
    c: Block(g6)
    c: Coincident(g7,g4)
    c: Horizontal(g7)
    c: Block(g0)
    c: Block(g7)
    c: Block(g3)
    c: Coincident(g13,g6)
    c: Weight(g8) = 1
    c: Equal(g8, g9-g12) x4
    c: Coincident(g13,g7)
    c: InternalAlignment(g8-g12 -> g13) x5
    c: InternalAlignment(g14,g13)
    c: InternalAlignment(g15,g13)
    c: InternalAlignment(g16,g13)
    c: Block(g13)
    c: Weight(g17) = 1
    c: Equal(g17, g18-g23) x6
    c: Coincident(g24,g1)
    c: InternalAlignment(g17-g23 -> g24) x7
    c: InternalAlignment(g25-g29 -> g24) x5
    c: Block(g24)
    c: Coincident(g30,g24)
    c: Coincident(g31,g6)
    c: Coincident(g31,g30)
    c: Horizontal(g31)
    c: Block(g31)
    c: Block(g30)
FEATURE [Part::Extrusion] Extrude062  label="bottom014"
  Base = -> Sketch071
  Dir = (0,0,1)
  DirMode = 2
  FaceMakerClass = Part::FaceMakerBullseye
  LengthFwd = 71.4
  LengthRev = 0
  Placement = pos=(0,0,0.3) rot=(0,0,1;0rad)
  Solid = true
  Symmetric = false
FEATURE [Part::Fillet] Fillet054
  Base = -> Extrude062
  Edges = 1 edges r=2.4: [Edge17]
FEATURE [Part::Fillet] Fillet055  label="bottom015"
  Base = -> Fillet054
  Edges = 1 edges r=2.4: [Edge36]
FEATURE [Part::Cylinder] Cylinder055
  Angle = 360
  AttacherType = Attacher::AttachEngine3D
  Height = 10
  Placement = pos=(0,0,36.15) rot=(0,0,1;0rad)
  Radius = 4
FEATURE [Part::MultiFuse] Fusion131  label="removeToCreateHoleForPlugHousing002"
  Placement = pos=(70,19,36.15) rot=(0,1,0;1.5708rad)
  Shapes = -> [Cylinder054,Cylinder055]
FEATURE [Part::Cut] Cut056  label="Bottom001"
  Base = -> Fillet055
  Placement = pos=(9,0,0) rot=(0,0,1;0rad)
  Tool = -> Fusion131
FEATURE [Part::Cut] Cut057
  Base = -> Cut055
  Tool = -> Cut056
FEATURE [Sketcher::SketchObject] Sketch072  label="topSketch021"
  FullyConstrained = true
  sketch-geometry (4):
    g0: ArcOfCircle CenterX=105 CenterY=19 CenterZ=0 NormalX=0 NormalY=0 NormalZ=1 AngleXU=0 Radius=20.6155 StartAngle=5.54125 EndAngle=6.28319
    g1: ArcOfCircle CenterX=105 CenterY=19 CenterZ=0 NormalX=0 NormalY=0 NormalZ=1 AngleXU=0 Radius=13 StartAngle=5.54125 EndAngle=6.28319
    g2: LineSegment StartX=118 StartY=19 StartZ=0 EndX=125.616 EndY=19 EndZ=0
    g3: LineSegment StartX=114.583 StartY=10.2157 StartZ=0 EndX=120.197 EndY=5.06982 EndZ=0
  constraints (7):
    c: Block(g0)
    c: Block(g1)
    c: Coincident(g2,g1)
    c: Coincident(g2,g0)
    c: Horizontal(g2)
    c: Coincident(g3,g1)
    c: Coincident(g3,g0)
FEATURE [Part::Extrusion] Extrude063  label="bottomPlugHousingBit003"
  Base = -> Sketch072
  Dir = (0,0,1)
  DirMode = 2
  FaceMakerClass = Part::FaceMakerBullseye
  LengthFwd = 72
  LengthRev = 0
  Solid = true
  Symmetric = false
FEATURE [Part::Cylinder] Cylinder056
  Angle = 360
  AttacherType = Attacher::AttachEngine3D
  Height = 20
  Placement = pos=(0,0,36.15) rot=(0,0,1;0rad)
  Radius = 14.3
FEATURE [Part::Cylinder] Cylinder057
  Angle = 360
  AttacherType = Attacher::AttachEngine3D
  Height = 10
  Placement = pos=(0,0,36.15) rot=(0,0,1;0rad)
  Radius = 4
FEATURE [Part::Box] Box034  label="removeToCreteHoleForPlugHousing047"
  AttacherType = Attacher::AttachEngine3D
  Height = 28.6
  Length = 20
  Placement = pos=(106.15,0,21.7) rot=(0,0,1;0rad)
  Width = 19
FEATURE [Part::Cylinder] Cylinder058
  Angle = 360
  AttacherType = Attacher::AttachEngine3D
  Height = 20
  Placement = pos=(0,0,36.15) rot=(0,0,1;0rad)
  Radius = 14.3
FEATURE [Part::Cylinder] Cylinder059
  Angle = 360
  AttacherType = Attacher::AttachEngine3D
  Height = 10
  Placement = pos=(0,0,36.15) rot=(0,0,1;0rad)
  Radius = 4
FEATURE [Part::MultiFuse] Fusion134  label="removeToCreteHoleForPlugHousing046"
  Placement = pos=(70,19,36) rot=(0,1,0;1.5708rad)
  Shapes = -> [Cylinder058,Cylinder059]
FEATURE [Part::Cylinder] Cylinder060
  Angle = 360
  AttacherType = Attacher::AttachEngine3D
  Height = 20
  Placement = pos=(0,0,36.15) rot=(0,0,1;0rad)
  Radius = 14
FEATURE [Part::Cylinder] Cylinder061
  Angle = 360
  AttacherType = Attacher::AttachEngine3D
  Height = 10
  Placement = pos=(0,0,36.15) rot=(0,0,1;0rad)
  Radius = 4
FEATURE [Part::MultiFuse] Fusion135  label="removeToCreteHoleForPlugHousing048"
  Placement = pos=(70,19,36) rot=(0,1,0;1.5708rad)
  Shapes = -> [Cylinder060,Cylinder061]
FEATURE [Part::Box] Box035  label="removeToCreteHoleForPlugHousing049"
  AttacherType = Attacher::AttachEngine3D
  Height = 28.6
  Length = 20
  Placement = pos=(106.15,0,21.7) rot=(0,0,1;0rad)
  Width = 19
FEATURE [Part::MultiFuse] Fusion133  label="removeToCreteHoleForPlugHousing045"
  Placement = pos=(0,0,-28.3) rot=(0,0,1;0rad)
  Shapes = -> [Box035,Fusion134]
FEATURE [Part::MultiFuse] Fusion138  label="removeToCreteHoleForPlugHousing051"
  Placement = pos=(70,19,36) rot=(0,1,0;1.5708rad)
  Shapes = -> [Cylinder056,Cylinder057]
FEATURE [Part::MultiFuse] Fusion137  label="removeToCreteHoleForPlugHousing050"
  Placement = pos=(0,0,28.3) rot=(0,0,1;0rad)
  Shapes = -> [Box034,Fusion138]
FEATURE [Part::MultiFuse] Fusion132  label="removeToCreatePlugHousingBottomBit002"
  Shapes = -> [Fusion133,Fusion137]
FEATURE [Part::MultiFuse] Fusion136  label="removeToCreatePlugHousingBottomBit003"
  Shapes = -> [Fusion135,Fusion132]
FEATURE [Part::Cut] Cut058  label="bottomPlugHousingBit002"
  Base = -> Extrude063
  Placement = pos=(-0.09,0,0) rot=(0,0,1;0rad)
  Tool = -> Fusion136
FEATURE [Sketcher::SketchObject] Sketch073  label="bottomSketch003"
  FullyConstrained = true
  sketch-geometry (45):
    g0: LineSegment StartX=6.29999 StartY=8 StartZ=0 EndX=3.29999 EndY=8 EndZ=0
    g1: LineSegment StartX=3.29999 StartY=8 StartZ=0 EndX=3.29999 EndY=-6.03275e-07 EndZ=0
    g2: ArcOfCircle CenterX=8.29999 CenterY=5 CenterZ=0 NormalX=0 NormalY=0 NormalZ=1 AngleXU=0 Radius=2 StartAngle=3.14159 EndAngle=4.71239
    g3: LineSegment StartX=6.29999 StartY=8 StartZ=0 EndX=6.29999 EndY=5 EndZ=0
    g4: ArcOfCircle CenterX=105 CenterY=19 CenterZ=0 NormalX=0 NormalY=0 NormalZ=1 AngleXU=0 Radius=12.7 StartAngle=4.71239 EndAngle=5.94289
    g5-g11: Circle x7 (B-spline internal-alignment scaffolding for g12; pole/knot coordinates omitted)
    g12: BSplineCurve PolesCount=7 KnotsCount=5 Degree=3 IsPeriodic=0
    g13-g17: GeomPoint x5 (B-spline internal-alignment scaffolding for g12; pole/knot coordinates omitted)
    g18: ArcOfCircle CenterX=105 CenterY=19 CenterZ=0 NormalX=0 NormalY=0 NormalZ=1 AngleXU=0 Radius=15.7 StartAngle=5.81226 EndAngle=6.28319
    g19: BSplineCurve PolesCount=5 KnotsCount=3 Degree=3 IsPeriodic=0
    g20: LineSegment StartX=8.29999 StartY=3 StartZ=0 EndX=101.7 EndY=3 EndZ=0
    g21: LineSegment StartX=3.29999 StartY=-6.03275e-07 StartZ=0 EndX=105 EndY=-6.03275e-07 EndZ=0
    g22: LineSegment StartX=120.974 StartY=8.71251 StartZ=0 EndX=122.332 EndY=7.83778 EndZ=0
    g23: LineSegment StartX=105 StartY=-6.03274e-07 StartZ=0 EndX=113 EndY=-6.03274e-07 EndZ=0
    g24: ArcOfCircle CenterX=105 CenterY=19 CenterZ=0 NormalX=0 NormalY=0 NormalZ=1 AngleXU=0 Radius=20.6155 StartAngle=5.11091 EndAngle=5.71103
    g25: ArcOfCircle CenterX=117.7 CenterY=19 CenterZ=0 NormalX=0 NormalY=0 NormalZ=1 AngleXU=0 Radius=3 StartAngle=1.2e-15 EndAngle=2.10468
    g26: Circle CenterX=116.345 CenterY=16.3232 CenterZ=0 NormalX=0 NormalY=0 NormalZ=1 AngleXU=0 Radius=1
    g27: Circle CenterX=117.24 CenterY=15.7584 CenterZ=0 NormalX=0 NormalY=0 NormalZ=1 AngleXU=0 Radius=1
    g28: Circle CenterX=116.972 CenterY=14.7612 CenterZ=0 NormalX=0 NormalY=0 NormalZ=1 AngleXU=0 Radius=1
    g29: BSplineCurve PolesCount=3 KnotsCount=2 Degree=2 IsPeriodic=0
    g30: GeomPoint X=116.345 Y=16.3232 Z=0
    g31: GeomPoint X=116.972 Y=14.7612 Z=0
    g32: Circle CenterX=115.828 CenterY=17.157 CenterZ=0 NormalX=0 NormalY=0 NormalZ=1 AngleXU=0 Radius=1
    g33: Circle CenterX=115.841 CenterY=16.639 CenterZ=0 NormalX=0 NormalY=0 NormalZ=1 AngleXU=0 Radius=1
    g34: Circle CenterX=116.345 CenterY=16.3232 CenterZ=0 NormalX=0 NormalY=0 NormalZ=1 AngleXU=0 Radius=1
    g35: BSplineCurve PolesCount=3 KnotsCount=2 Degree=2 IsPeriodic=0
    g36: GeomPoint X=115.828 Y=17.157 Z=0
    g37: GeomPoint X=116.345 Y=16.3232 Z=0
    g38: LineSegment StartX=115.828 StartY=17.157 StartZ=0 EndX=115.828 EndY=20.8307 EndZ=0
    g39: Circle CenterX=115.828 CenterY=20.8307 CenterZ=0 NormalX=0 NormalY=0 NormalZ=1 AngleXU=0 Radius=1
    g40: Circle CenterX=115.831 CenterY=21.3396 CenterZ=0 NormalX=0 NormalY=0 NormalZ=1 AngleXU=0 Radius=1
    g41: Circle CenterX=116.173 CenterY=21.5825 CenterZ=0 NormalX=0 NormalY=0 NormalZ=1 AngleXU=0 Radius=1
    g42: BSplineCurve PolesCount=3 KnotsCount=2 Degree=2 IsPeriodic=0
    g43: GeomPoint X=115.828 Y=20.8307 Z=0
    g44: GeomPoint X=116.173 Y=21.5825 Z=0
  constraints (70):
    c: Horizontal(g0)
    c: Distance(g0) = 3
    c: Coincident(g1,g0)
    c: Vertical(g1)
    c: Block(g2)
    c: Block(g0)
    c: Coincident(g3,g0)
    c: Coincident(g3,g2)
    c: Vertical(g3)
    c: Block(g1)
    c: Block(g4)
    c: Coincident(g19,g4)
    c: Block(g19)
    c: Equal(g5, g6-g11) x6
    c: InternalAlignment(g5-g11 -> g12) x7
    c: InternalAlignment(g13-g17 -> g12) x5
    c: Block(g12)
    c: Coincident(g18,g12)
    c: Block(g18)
    c: Coincident(g20,g2)
    c: Coincident(g20,g19)
    c: Horizontal(g20)
    c: Distance(g20) = 93.4
    c: Coincident(g21,g1)
    c: Horizontal(g21)
    c: Distance(g21) = 101.7
    c: Horizontal(g23)
    c: Distance(g23) = 8
    c: Coincident(g24,g23)
    c: Block(g23)
    c: Coincident(g22,g24)
    c: Block(g24)
    c: Block(g22)
    c: Distance(g22) = 1.61553
    c: Coincident(g25,g18)
    c: Block(g25)
    c: Weight(g26) = 1
    c: Equal(g26,g27)
    c: Equal(g26,g28)
    c: Coincident(g29,g4)
    c: InternalAlignment(g26,g29)
    c: InternalAlignment(g27,g29)
    c: InternalAlignment(g28,g29)
    c: InternalAlignment(g30,g29)
    c: InternalAlignment(g31,g29)
    c: Block(g29)
    c: Weight(g32) = 1
    c: Equal(g32,g33)
    c: Equal(g32,g34)
    c: Coincident(g35,g29)
    c: InternalAlignment(g32,g35)
    c: InternalAlignment(g33,g35)
    c: InternalAlignment(g34,g35)
    c: InternalAlignment(g36,g35)
    c: InternalAlignment(g37,g35)
    c: Block(g35)
    c: Coincident(g38,g35)
    c: Vertical(g38)
    c: Block(g38)
    c: Coincident(g42,g38)
    c: Weight(g39) = 1
    c: Equal(g39,g40)
    c: Equal(g39,g41)
    c: Coincident(g42,g25)
    c: InternalAlignment(g39,g42)
    c: InternalAlignment(g40,g42)
    c: InternalAlignment(g41,g42)
    c: InternalAlignment(g43,g42)
    c: InternalAlignment(g44,g42)
    c: Block(g42)
FEATURE [Part::Extrusion] Extrude064  label="bottom016"
  Base = -> Sketch073
  Dir = (0,0,1)
  DirMode = 2
  FaceMakerClass = Part::FaceMakerBullseye
  LengthFwd = 71.4
  LengthRev = 0
  Placement = pos=(0,0,0.3) rot=(0,0,1;0rad)
  Solid = true
  Symmetric = false
FEATURE [Part::Revolution] Revolve157  label="removeToCreateScrewAndThreadedInsertHole063"
  Angle = 360
  Axis = (0,1,0)
  Base = (0,0,0)
  FaceMakerClass = Part::FaceMakerBullseye
  Placement = pos=(12.5,0,10) rot=(0,0,1;0rad)
  Solid = false
  Source = -> Face141
  Symmetric = false
FEATURE [Sketcher::SketchObject] Sketch074
  FullyConstrained = true
  Placement = pos=(117,19,0) rot=(0.57735,0.57735,0.57735;2.0944rad)
  sketch-geometry (48):
    g0: LineSegment StartX=-49.19 StartY=69.25 StartZ=0 EndX=-49.19 EndY=66.25 EndZ=0
    g1: LineSegment StartX=-49.19 StartY=63.5 StartZ=0 EndX=-49.19 EndY=60.5 EndZ=0
    g2: LineSegment StartX=-49.19 StartY=57.75 StartZ=0 EndX=-49.19 EndY=54.75 EndZ=0
    g3: LineSegment StartX=-49.19 StartY=52 StartZ=0 EndX=-49.19 EndY=49 EndZ=0
    g4: LineSegment StartX=-49.19 StartY=46.25 StartZ=0 EndX=-49.19 EndY=43.25 EndZ=0
    g5: LineSegment StartX=-49.19 StartY=40.5 StartZ=0 EndX=-49.19 EndY=37.5 EndZ=0
    g6: LineSegment StartX=-49.19 StartY=34.5 StartZ=0 EndX=-49.19 EndY=31.5 EndZ=0
    g7: LineSegment StartX=-49.19 StartY=28.75 StartZ=0 EndX=-49.19 EndY=25.75 EndZ=0
    g8: LineSegment StartX=-49.19 StartY=23 StartZ=0 EndX=-49.19 EndY=20 EndZ=0
    g9: LineSegment StartX=-49.19 StartY=17.25 StartZ=0 EndX=-49.19 EndY=14.25 EndZ=0
    g10: LineSegment StartX=-49.19 StartY=11.5 StartZ=0 EndX=-49.19 EndY=8.5 EndZ=0
    g11: LineSegment StartX=-49.19 StartY=5.75 StartZ=0 EndX=-49.19 EndY=2.75 EndZ=0
    g12: ArcOfCircle CenterX=-1.5 CenterY=67.75 CenterZ=0 NormalX=0 NormalY=0 NormalZ=1 AngleXU=0 Radius=1.5 StartAngle=4.71239 EndAngle=7.85398
    g13: ArcOfCircle CenterX=-1.5 CenterY=62 CenterZ=0 NormalX=0 NormalY=0 NormalZ=1 AngleXU=0 Radius=1.5 StartAngle=4.71239 EndAngle=7.85398
    g14: ArcOfCircle CenterX=-1.5 CenterY=56.25 CenterZ=0 NormalX=0 NormalY=0 NormalZ=1 AngleXU=0 Radius=1.5 StartAngle=4.71239 EndAngle=7.85398
    g15: ArcOfCircle CenterX=-11.49 CenterY=50.5 CenterZ=0 NormalX=0 NormalY=0 NormalZ=1 AngleXU=0 Radius=1.5 StartAngle=4.71239 EndAngle=7.85398
    g16: ArcOfCircle CenterX=-16.28 CenterY=44.75 CenterZ=0 NormalX=0 NormalY=0 NormalZ=1 AngleXU=0 Radius=1.5 StartAngle=4.71239 EndAngle=7.85398
    g17: ArcOfCircle CenterX=-18.2337 CenterY=39 CenterZ=0 NormalX=0 NormalY=0 NormalZ=1 AngleXU=0 Radius=1.5 StartAngle=4.71485 EndAngle=7.85398
    g18: ArcOfCircle CenterX=-16.2837 CenterY=27.25 CenterZ=0 NormalX=0 NormalY=0 NormalZ=1 AngleXU=0 Radius=1.5 StartAngle=4.71485 EndAngle=7.85398
    g19: ArcOfCircle CenterX=-18.2337 CenterY=33 CenterZ=0 NormalX=0 NormalY=0 NormalZ=1 AngleXU=0 Radius=1.5 StartAngle=4.71485 EndAngle=7.85398
    g20: ArcOfCircle CenterX=-11.49 CenterY=21.5 CenterZ=0 NormalX=0 NormalY=0 NormalZ=1 AngleXU=0 Radius=1.5 StartAngle=4.71239 EndAngle=7.85398
    g21: ArcOfCircle CenterX=-1.5 CenterY=4.25 CenterZ=0 NormalX=0 NormalY=0 NormalZ=1 AngleXU=0 Radius=1.5 StartAngle=4.71239 EndAngle=7.85398
    g22: ArcOfCircle CenterX=-1.5 CenterY=10 CenterZ=0 NormalX=0 NormalY=0 NormalZ=1 AngleXU=0 Radius=1.5 StartAngle=4.71239 EndAngle=7.85398
    g23: ArcOfCircle CenterX=-1.5 CenterY=15.75 CenterZ=0 NormalX=0 NormalY=0 NormalZ=1 AngleXU=0 Radius=1.5 StartAngle=4.71239 EndAngle=7.85398
    g24: LineSegment StartX=-49.19 StartY=69.25 StartZ=0 EndX=-1.5 EndY=69.25 EndZ=0
    g25: LineSegment StartX=-49.19 StartY=66.25 StartZ=0 EndX=-1.5 EndY=66.25 EndZ=0
    g26: LineSegment StartX=-49.19 StartY=63.5 StartZ=0 EndX=-1.5 EndY=63.5 EndZ=0
    g27: LineSegment StartX=-49.19 StartY=60.5 StartZ=0 EndX=-1.5 EndY=60.5 EndZ=0
    g28: LineSegment StartX=-49.19 StartY=57.75 StartZ=0 EndX=-1.5 EndY=57.75 EndZ=0
    g29: LineSegment StartX=-49.19 StartY=54.75 StartZ=0 EndX=-1.5 EndY=54.75 EndZ=0
    g30: LineSegment StartX=-49.19 StartY=52 StartZ=0 EndX=-11.49 EndY=52 EndZ=0
    g31: LineSegment StartX=-49.19 StartY=49 StartZ=0 EndX=-11.49 EndY=49 EndZ=0
    g32: LineSegment StartX=-49.19 StartY=46.25 StartZ=0 EndX=-16.28 EndY=46.25 EndZ=0
    g33: LineSegment StartX=-49.19 StartY=43.25 StartZ=0 EndX=-16.28 EndY=43.25 EndZ=0
    g34: LineSegment StartX=-49.19 StartY=40.5 StartZ=0 EndX=-18.2337 EndY=40.5 EndZ=0
    g35: LineSegment StartX=-49.19 StartY=37.5 StartZ=0 EndX=-18.23 EndY=37.5 EndZ=0
    g36: LineSegment StartX=-49.19 StartY=34.5 StartZ=0 EndX=-18.2337 EndY=34.5 EndZ=0
    g37: LineSegment StartX=-49.19 StartY=31.5 StartZ=0 EndX=-18.23 EndY=31.5 EndZ=0
    g38: LineSegment StartX=-49.19 StartY=28.75 StartZ=0 EndX=-16.2837 EndY=28.75 EndZ=0
    g39: LineSegment StartX=-49.19 StartY=25.75 StartZ=0 EndX=-16.28 EndY=25.75 EndZ=0
    g40: LineSegment StartX=-49.19 StartY=23 StartZ=0 EndX=-11.49 EndY=23 EndZ=0
    g41: LineSegment StartX=-49.19 StartY=20 StartZ=0 EndX=-11.49 EndY=20 EndZ=0
    g42: LineSegment StartX=-49.19 StartY=17.25 StartZ=0 EndX=-1.5 EndY=17.25 EndZ=0
    g43: LineSegment StartX=-49.19 StartY=14.25 StartZ=0 EndX=-1.5 EndY=14.25 EndZ=0
    g44: LineSegment StartX=-49.19 StartY=11.5 StartZ=0 EndX=-1.5 EndY=11.5 EndZ=0
    g45: LineSegment StartX=-49.19 StartY=8.5 StartZ=0 EndX=-1.5 EndY=8.5 EndZ=0
    g46: LineSegment StartX=-49.19 StartY=5.75 StartZ=0 EndX=-1.5 EndY=5.75 EndZ=0
    g47: LineSegment StartX=-49.19 StartY=2.75 StartZ=0 EndX=-1.5 EndY=2.75 EndZ=0
  constraints (120):
    c: Vertical(g0)
    c: Distance(g0) = 3
    c: Block(g0)
    c: Vertical(g1)
    c: Distance(g1) = 3
    c: Vertical(g2)
    c: Equal(g0,g2) = 3
    c: Block(g2)
    c: Vertical(g3)
    c: Equal(g1,g3) = 3
    c: Vertical(g4)
    c: Equal(g0,g4) = 3
    c: Block(g4)
    c: Vertical(g5)
    c: Equal(g1,g5) = 3
    c: Vertical(g6)
    c: Equal(g0,g6) = 3
    c: Block(g6)
    c: Vertical(g7)
    c: Equal(g1,g7) = 3
    c: Vertical(g8)
    c: Equal(g0,g8) = 3
    c: Block(g8)
    c: Vertical(g9)
    c: Equal(g1,g9) = 3
    c: Vertical(g10)
    c: Equal(g0,g10) = 3
    c: Block(g10)
    c: Vertical(g11)
    c: Equal(g1,g11) = 3
    c: Block(g12)
    c: Block(g13)
    c: Block(g14)
    c: Block(g15)
    c: Block(g16)
    c: Block(g17)
    c: Block(g18)
    c: Block(g19)
    c: Block(g20)
    c: Block(g21)
    c: Block(g22)
    c: Block(g23)
    c: Block(g11)
    c: Block(g9)
    c: Block(g7)
    c: Block(g5)
    c: Block(g3)
    c: Block(g1)
    c: Coincident(g24,g0)
    c: Coincident(g24,g12)
    c: Horizontal(g24)
    c: Coincident(g25,g0)
    c: Coincident(g25,g12)
    c: Horizontal(g25)
    c: Coincident(g26,g1)
    c: Coincident(g26,g13)
    c: Horizontal(g26)
    c: Coincident(g27,g1)
    c: Coincident(g27,g13)
    c: Horizontal(g27)
    c: Coincident(g28,g2)
    c: Coincident(g28,g14)
    c: Horizontal(g28)
    c: Coincident(g29,g2)
    c: Coincident(g29,g14)
    c: Horizontal(g29)
    c: Coincident(g30,g3)
    c: Coincident(g30,g15)
    c: Horizontal(g30)
    c: Coincident(g31,g3)
    c: Coincident(g31,g15)
    c: Horizontal(g31)
    c: Coincident(g32,g4)
    c: Coincident(g32,g16)
    c: Horizontal(g32)
    c: Coincident(g33,g4)
    c: Coincident(g33,g16)
    c: Horizontal(g33)
    c: Coincident(g34,g5)
    c: Coincident(g34,g17)
    c: Horizontal(g34)
    c: Coincident(g35,g5)
    c: Coincident(g35,g17)
    c: Horizontal(g35)
    c: Coincident(g36,g6)
    c: Coincident(g36,g19)
    c: Horizontal(g36)
    c: Coincident(g37,g6)
    c: Coincident(g37,g19)
    c: Horizontal(g37)
    c: Coincident(g38,g7)
    c: Coincident(g38,g18)
    c: Horizontal(g38)
    c: Coincident(g39,g7)
    c: Coincident(g39,g18)
    c: Horizontal(g39)
    c: Coincident(g40,g8)
    c: Coincident(g40,g20)
    c: Horizontal(g40)
    c: Coincident(g41,g8)
    c: Coincident(g41,g20)
    c: Horizontal(g41)
    c: Coincident(g42,g9)
    c: Coincident(g42,g23)
    c: Horizontal(g42)
    c: Coincident(g43,g9)
    c: Coincident(g43,g23)
    c: Horizontal(g43)
    c: Coincident(g44,g10)
    c: Coincident(g44,g22)
    c: Horizontal(g44)
    c: Coincident(g45,g10)
    c: Coincident(g45,g22)
    c: Horizontal(g45)
    c: Coincident(g46,g11)
    c: Coincident(g46,g21)
    c: Horizontal(g46)
    c: Coincident(g47,g11)
    c: Coincident(g47,g21)
    c: Horizontal(g47)
FEATURE [Part::Extrusion] Extrude065
  Base = -> Sketch074
  Dir = (1,0,0)
  DirMode = 2
  FaceMakerClass = Part::FaceMakerBullseye
  LengthFwd = 23
  LengthRev = 0
  Placement = pos=(-19,0,0) rot=(0,0,1;0rad)
  Solid = true
  Symmetric = false
FEATURE [Part::Fillet] Fillet056  label="removeToCreateVentalationHoles003"
  Base = -> Extrude065
  Edges = <same value as first occurrence — deduplicated (x6 in doc)>
  Placement = pos=(7,0.02,0) rot=(0,0,1;0rad)
FEATURE [Part::Revolution] Revolve158  label="removeToCreateScrewAndThreadedInsertHole065"
  Angle = 360
  Axis = (0,1,0)
  Base = (0,0,0)
  FaceMakerClass = Part::FaceMakerBullseye
  Placement = pos=(12.5,0,62) rot=(0,0,1;0rad)
  Solid = false
  Source = -> Face146
  Symmetric = false
FEATURE [Part::Revolution] Revolve159  label="removeToCreateScrewAndThreadedInsertHole066"
  Angle = 360
  Axis = (0,1,0)
  Base = (0,0,0)
  FaceMakerClass = Part::FaceMakerBullseye
  Placement = pos=(89.5,0,68.5) rot=(0,0,1;0rad)
  Solid = false
  Source = -> Face143
  Symmetric = false
FEATURE [Part::Revolution] Revolve160  label="removeToCreateScrewAndThreadedInsertHole067"
  Angle = 360
  Axis = (0,1,0)
  Base = (0,0,0)
  FaceMakerClass = Part::FaceMakerBullseye
  Placement = pos=(89.5,0,3.5) rot=(0,0,1;0rad)
  Solid = false
  Source = -> Face142
  Symmetric = false
FEATURE [Part::Revolution] Revolve161  label="removeToCreateScrewAndThreadedInsertHole068"
  Angle = 360
  Axis = (0,1,0)
  Base = (0,0,0)
  FaceMakerClass = Part::FaceMakerBullseye
  Placement = pos=(109.5,4.7,3.5) rot=(0,0,1;0rad)
  Solid = false
  Source = -> Face145
  Symmetric = false
FEATURE [Part::Revolution] Revolve162  label="removeToCreateScrewAndThreadedInsertHole069"
  Angle = 360
  Axis = (0,1,0)
  Base = (0,0,0)
  FaceMakerClass = Part::FaceMakerBullseye
  Placement = pos=(109.5,4.7,68.5) rot=(0,0,1;0rad)
  Solid = false
  Source = -> Face144
  Symmetric = false
FEATURE [Part::MultiFuse] Fusion141  label="removeToCreateScrewAndThreadedInsertHole064"
  Shapes = -> [Revolve162,Revolve161,Revolve160,Revolve159,Revolve158,Revolve157]
FEATURE [Part::Cylinder] Cylinder062
  Angle = 360
  AttacherType = Attacher::AttachEngine3D
  Height = 20
  Placement = pos=(0,0,36.15) rot=(0,0,1;0rad)
  Radius = 14
FEATURE [Part::Cylinder] Cylinder063
  Angle = 360
  AttacherType = Attacher::AttachEngine3D
  Height = 10
  Placement = pos=(0,0,36.15) rot=(0,0,1;0rad)
  Radius = 4
FEATURE [Part::MultiFuse] Fusion139  label="removeToCreteHoleForPlugHousing052"
  Placement = pos=(70,19,36) rot=(0,1,0;1.5708rad)
  Shapes = -> [Cylinder062,Cylinder063]
FEATURE [Part::Cut] Cut060  label="bottom017"
  Base = -> Extrude064
  Tool = -> Fusion139
FEATURE [Part::Cut] Cut061  label="bottom019"
  Base = -> Cut060
  Tool = -> Fusion141
FEATURE [Part::MultiFuse] Fusion140  label="bottom018"
  Shapes = -> [Cut061,Cut058]
FEATURE [Part::Cut] Cut059  label="bottom020"
  Base = -> Fusion140
  Tool = -> Fillet056
FEATURE [Part::Box] Box036  label="Cube021"
  AttacherType = Attacher::AttachEngine3D
  Height = 80
  Length = 26
  Placement = pos=(0,-1,-5) rot=(0,0,1;0rad)
  Width = 11
FEATURE [Part::Cut] Cut062  label="removeFromBottom002"
  Base = -> Cut057
  Tool = -> Box036
FEATURE [Part::Cut] Cut063
  Base = -> Cut059
  Tool = -> Cut062
FEATURE [Part::Cut] Cut064  label="pcbStands"
  Base = -> Fusion095
  Tool = -> Fusion127
FEATURE [Sketcher::SketchObject] Sketch075  label="topSketch022"
  FullyConstrained = true
  sketch-geometry (6):
    g0: LineSegment StartX=19 StartY=38 StartZ=0 EndX=117 EndY=38 EndZ=0
    g1: ArcOfCircle CenterX=19 CenterY=19 CenterZ=0 NormalX=0 NormalY=0 NormalZ=1 AngleXU=0 Radius=19 StartAngle=1.5708 EndAngle=3.14159
    g2: LineSegment StartX=117 StartY=38 StartZ=0 EndX=117 EndY=19 EndZ=0
    g3: LineSegment StartX=98 StartY=1.0161e-12 StartZ=0 EndX=5.22862e-06 EndY=1.0161e-12 EndZ=0
    g4: LineSegment StartX=5.22862e-06 StartY=19 StartZ=0 EndX=5.22862e-06 EndY=1.0161e-12 EndZ=0
    g5: ArcOfCircle CenterX=98 CenterY=19 CenterZ=0 NormalX=0 NormalY=0 NormalZ=1 AngleXU=0 Radius=19 StartAngle=4.71239 EndAngle=6.28319
  constraints (16):
    c: Horizontal(g0)
    c: Distance(g0) = 98
    c: Coincident(g1,g0)
    c: Block(g1)
    c: Coincident(g2,g0)
    c: Vertical(g2)
    c: Distance(g2) = 19
    c: Horizontal(g3)
    c: Coincident(g4,g1)
    c: Vertical(g4)
    c: Coincident(g3,g4)
    c: Block(g3)
    c: Coincident(g5,g2)
    c: Coincident(g5,g3)
    c: Block(g0)
    c: Block(g5)
FEATURE [Part::Extrusion] Extrude067  label="sideB003"
  Base = -> Sketch075
  Dir = (0,0,1)
  DirMode = 2
  FaceMakerClass = Part::FaceMakerBullseye
  LengthFwd = 3
  LengthRev = 0
  Placement = pos=(0,0,71.7) rot=(0,0,1;0rad)
  Solid = true
  Symmetric = false
FEATURE [Sketcher::SketchObject] Sketch076  label="topSketch023"
  FullyConstrained = true
  sketch-geometry (6):
    g0: LineSegment StartX=19 StartY=38 StartZ=0 EndX=117 EndY=38 EndZ=0
    g1: ArcOfCircle CenterX=19 CenterY=19 CenterZ=0 NormalX=0 NormalY=0 NormalZ=1 AngleXU=0 Radius=19 StartAngle=1.5708 EndAngle=3.14159
    g2: LineSegment StartX=117 StartY=38 StartZ=0 EndX=117 EndY=19 EndZ=0
    g3: LineSegment StartX=98 StartY=1.0161e-12 StartZ=0 EndX=5.22862e-06 EndY=1.0161e-12 EndZ=0
    g4: LineSegment StartX=5.22862e-06 StartY=19 StartZ=0 EndX=5.22862e-06 EndY=1.0161e-12 EndZ=0
    g5: ArcOfCircle CenterX=98 CenterY=19 CenterZ=0 NormalX=0 NormalY=0 NormalZ=1 AngleXU=0 Radius=19 StartAngle=4.71239 EndAngle=6.28319
  constraints (16):
    c: Horizontal(g0)
    c: Distance(g0) = 98
    c: Coincident(g1,g0)
    c: Block(g1)
    c: Coincident(g2,g0)
    c: Vertical(g2)
    c: Distance(g2) = 19
    c: Horizontal(g3)
    c: Coincident(g4,g1)
    c: Vertical(g4)
    c: Coincident(g3,g4)
    c: Block(g3)
    c: Coincident(g5,g2)
    c: Coincident(g5,g3)
    c: Block(g0)
    c: Block(g5)
FEATURE [Part::Extrusion] Extrude066  label="sideA003"
  Base = -> Sketch076
  Dir = (0,0,1)
  DirMode = 2
  FaceMakerClass = Part::FaceMakerBullseye
  LengthFwd = 3
  LengthRev = 0
  Placement = pos=(0,0,-2.7) rot=(0,0,1;0rad)
  Solid = true
  Symmetric = false
FEATURE [Part::MultiFuse] Fusion142  label="removeFromBottom003"
  Placement = pos=(2,0,0) rot=(0,0,1;0rad)
  Shapes = -> [Extrude066,Extrude067]
FEATURE [Part::Cut] Cut065  label="screwRetainers002"
  Base = -> Fusion096
  Tool = -> Fusion142
FEATURE [Sketcher::SketchObject] Sketch077
  FullyConstrained = true
  Placement = pos=(117,19,0) rot=(0.57735,0.57735,0.57735;2.0944rad)
  sketch-geometry (8):
    g0: LineSegment StartX=-49.19 StartY=63.5 StartZ=0 EndX=-49.19 EndY=60.5 EndZ=0
    g1: LineSegment StartX=-49.19 StartY=11.5 StartZ=0 EndX=-49.19 EndY=8.5 EndZ=0
    g2: ArcOfCircle CenterX=-1.5 CenterY=62 CenterZ=0 NormalX=0 NormalY=0 NormalZ=1 AngleXU=0 Radius=1.5 StartAngle=4.71239 EndAngle=7.85398
    g3: ArcOfCircle CenterX=-1.5 CenterY=10 CenterZ=0 NormalX=0 NormalY=0 NormalZ=1 AngleXU=0 Radius=1.5 StartAngle=4.71239 EndAngle=7.85398
    g4: LineSegment StartX=-49.19 StartY=63.5 StartZ=0 EndX=-1.5 EndY=63.5 EndZ=0
    g5: LineSegment StartX=-49.19 StartY=60.5 StartZ=0 EndX=-1.5 EndY=60.5 EndZ=0
    g6: LineSegment StartX=-49.19 StartY=11.5 StartZ=0 EndX=-1.5 EndY=11.5 EndZ=0
    g7: LineSegment StartX=-49.19 StartY=8.5 StartZ=0 EndX=-1.5 EndY=8.5 EndZ=0
  constraints (19):
    c: Vertical(g0)
    c: Distance(g0) = 3
    c: Vertical(g1)
    c: Block(g1)
    c: Block(g2)
    c: Block(g3)
    c: Block(g0)
    c: Coincident(g4,g0)
    c: Coincident(g4,g2)
    c: Horizontal(g4)
    c: Coincident(g5,g0)
    c: Coincident(g5,g2)
    c: Horizontal(g5)
    c: Coincident(g6,g1)
    c: Coincident(g6,g3)
    c: Horizontal(g6)
    c: Coincident(g7,g1)
    c: Coincident(g7,g3)
    c: Horizontal(g7)
FEATURE [Part::Extrusion] Extrude068
  Base = -> Sketch077
  Dir = (1,0,0)
  DirMode = 2
  FaceMakerClass = Part::FaceMakerBullseye
  LengthFwd = 10
  LengthRev = 0
  Solid = true
  Symmetric = false
FEATURE [Part::Fillet] Fillet057  label="removeFromtMoreFrontCaseScrewRetainers002"
  Base = -> Extrude068
  Edges = 4 edges r=1.49: [Edge6,Edge11,Edge18,Edge23]
  Placement = pos=(-12,0,0) rot=(0,0,1;0rad)
FEATURE [Sketcher::SketchObject] Sketch078
  FullyConstrained = true
  Placement = pos=(117,19,0) rot=(0.57735,0.57735,0.57735;2.0944rad)
  sketch-geometry (8):
    g0: LineSegment StartX=-49.19 StartY=69.25 StartZ=0 EndX=-49.19 EndY=66.25 EndZ=0
    g1: LineSegment StartX=-49.19 StartY=5.75 StartZ=0 EndX=-49.19 EndY=2.75 EndZ=0
    g2: ArcOfCircle CenterX=-1.5 CenterY=67.75 CenterZ=0 NormalX=0 NormalY=0 NormalZ=1 AngleXU=0 Radius=1.5 StartAngle=4.71239 EndAngle=7.85398
    g3: ArcOfCircle CenterX=-1.5 CenterY=4.25 CenterZ=0 NormalX=0 NormalY=0 NormalZ=1 AngleXU=0 Radius=1.5 StartAngle=4.71239 EndAngle=7.85398
    g4: LineSegment StartX=-49.19 StartY=69.25 StartZ=0 EndX=-1.5 EndY=69.25 EndZ=0
    g5: LineSegment StartX=-49.19 StartY=66.25 StartZ=0 EndX=-1.5 EndY=66.25 EndZ=0
    g6: LineSegment StartX=-49.19 StartY=5.75 StartZ=0 EndX=-1.5 EndY=5.75 EndZ=0
    g7: LineSegment StartX=-49.19 StartY=2.75 StartZ=0 EndX=-1.5 EndY=2.75 EndZ=0
  constraints (19):
    c: Vertical(g0)
    c: Distance(g0) = 3
    c: Block(g0)
    c: Vertical(g1)
    c: Block(g2)
    c: Block(g3)
    c: Block(g1)
    c: Coincident(g4,g0)
    c: Coincident(g4,g2)
    c: Horizontal(g4)
    c: Coincident(g5,g0)
    c: Coincident(g5,g2)
    c: Horizontal(g5)
    c: Coincident(g6,g1)
    c: Coincident(g6,g3)
    c: Horizontal(g6)
    c: Coincident(g7,g1)
    c: Coincident(g7,g3)
    c: Horizontal(g7)
FEATURE [Part::Extrusion] Extrude069
  Base = -> Sketch078
  Dir = (1,0,0)
  DirMode = 2
  FaceMakerClass = Part::FaceMakerBullseye
  LengthFwd = 10
  LengthRev = 0
  Solid = true
  Symmetric = false
FEATURE [Part::Fillet] Fillet058  label="removeFromtMoreFrontCaseScrewRetainers003"
  Base = -> Extrude069
  Edges = 4 edges r=1.49: [Edge6,Edge11,Edge18,Edge23]
  Placement = pos=(-4,0,0) rot=(0,0,1;0rad)
FEATURE [Part::Cut] Cut066
  Base = -> Cut065
  Tool = -> Fillet058
FEATURE [Part::Cut] Cut067  label="screwPillars"
  Base = -> Cut066
  Tool = -> Fillet057
FEATURE [Part::MultiFuse] Fusion143  label="bottom021"
  Shapes = -> [Cut031,Cut063]
FEATURE [Part::Cylinder] Cylinder
  Angle = 360
  AttacherType = Attacher::AttachEngine3D
  Height = 10
  Placement = pos=(20.65,12,4.68) rot=(1,0,0;1.5708rad)
  Radius = 2
FEATURE [Part::Cylinder] Cylinder064
  Angle = 360
  AttacherType = Attacher::AttachEngine3D
  Height = 10
  Placement = pos=(20.65,12,67.38) rot=(1,0,0;1.5708rad)
  Radius = 2
FEATURE [Part::Cylinder] Cylinder065
  Angle = 360
  AttacherType = Attacher::AttachEngine3D
  Height = 10
  Placement = pos=(77.15,12,67.38) rot=(1,0,0;1.5708rad)
  Radius = 2
FEATURE [Part::Cylinder] Cylinder066
  Angle = 360
  AttacherType = Attacher::AttachEngine3D
  Height = 10
  Placement = pos=(77.15,12,4.68) rot=(1,0,0;1.5708rad)
  Radius = 2
FEATURE [Part::MultiFuse] Fusion144  label="removeFromThreadedInsertHousing"
  Shapes = -> [Cylinder065,Cylinder064,Cylinder,Cylinder066]
FEATURE [Part::Cut] Cut068  label="pcbStands001"
  Base = -> Cut064
  Tool = -> Fusion144
FEATURE [Part::MultiFuse] Fusion145
  Shapes = -> [Cut068,Fusion143]
FEATURE [Part::MultiFuse] Fusion146
  Shapes = -> [Fusion145]
FEATURE [Part::MultiFuse] Fusion147  label="bottom022"
  Shapes = -> [Cut067,Fusion146]
FEATURE [Part::MultiFuse] Fusion148  label="casePillars005"
  Shapes = -> [Cut047,Fusion092]
FEATURE [Part::MultiFuse] Fusion149  label="bottom023"
  Shapes = -> [Fusion124,Fusion113,Fusion147]
FEATURE [Part::MultiFuse] Fusion150  label="topBits"
  Shapes = -> [Cut025,Fusion148,Cut030,Fillet034]
FEATURE [Part::Feature] Face149 .. Face152  x4 (patterned run collapsed; names and placements below)
  shape: bbox 3.2 x 1.5 x 2e-07 mm, 1 faces, 0 solids (baked)
FEATURE [Part::Feature] Face153
  shape: bbox 3.6 x 3.2 x 2e-07 mm, 1 faces, 0 solids (baked)
FEATURE [Part::Feature] Face154
  shape: bbox 3.6 x 3.2 x 2e-07 mm, 1 faces, 0 solids (baked)
FEATURE [Sketcher::SketchObject] Sketch079  label="topSketch024"
  FullyConstrained = true
  sketch-geometry (6):
    g0: LineSegment StartX=19 StartY=38 StartZ=0 EndX=117 EndY=38 EndZ=0
    g1: ArcOfCircle CenterX=19 CenterY=19 CenterZ=0 NormalX=0 NormalY=0 NormalZ=1 AngleXU=0 Radius=19 StartAngle=1.5708 EndAngle=3.14159
    g2: LineSegment StartX=117 StartY=38 StartZ=0 EndX=117 EndY=19 EndZ=0
    g3: LineSegment StartX=98 StartY=1.0161e-12 StartZ=0 EndX=5.22862e-06 EndY=1.0161e-12 EndZ=0
    g4: LineSegment StartX=5.22862e-06 StartY=19 StartZ=0 EndX=5.22862e-06 EndY=1.0161e-12 EndZ=0
    g5: ArcOfCircle CenterX=98 CenterY=19 CenterZ=0 NormalX=0 NormalY=0 NormalZ=1 AngleXU=0 Radius=19 StartAngle=4.71239 EndAngle=6.28319
  constraints (16):
    c: Horizontal(g0)
    c: Distance(g0) = 98
    c: Coincident(g1,g0)
    c: Block(g1)
    c: Coincident(g2,g0)
    c: Vertical(g2)
    c: Distance(g2) = 19
    c: Horizontal(g3)
    c: Coincident(g4,g1)
    c: Vertical(g4)
    c: Coincident(g3,g4)
    c: Block(g3)
    c: Coincident(g5,g2)
    c: Coincident(g5,g3)
    c: Block(g0)
    c: Block(g5)
FEATURE [Sketcher::SketchObject] Sketch080  label="topSketch025"
  FullyConstrained = true
  sketch-geometry (6):
    g0: LineSegment StartX=19 StartY=38 StartZ=0 EndX=117 EndY=38 EndZ=0
    g1: ArcOfCircle CenterX=19 CenterY=19 CenterZ=0 NormalX=0 NormalY=0 NormalZ=1 AngleXU=0 Radius=19 StartAngle=1.5708 EndAngle=3.14159
    g2: LineSegment StartX=117 StartY=38 StartZ=0 EndX=117 EndY=19 EndZ=0
    g3: LineSegment StartX=98 StartY=1.0161e-12 StartZ=0 EndX=5.22862e-06 EndY=1.0161e-12 EndZ=0
    g4: LineSegment StartX=5.22862e-06 StartY=19 StartZ=0 EndX=5.22862e-06 EndY=1.0161e-12 EndZ=0
    g5: ArcOfCircle CenterX=98 CenterY=19 CenterZ=0 NormalX=0 NormalY=0 NormalZ=1 AngleXU=0 Radius=19 StartAngle=4.71239 EndAngle=6.28319
  constraints (16):
    c: Horizontal(g0)
    c: Distance(g0) = 98
    c: Coincident(g1,g0)
    c: Block(g1)
    c: Coincident(g2,g0)
    c: Vertical(g2)
    c: Distance(g2) = 19
    c: Horizontal(g3)
    c: Coincident(g4,g1)
    c: Vertical(g4)
    c: Coincident(g3,g4)
    c: Block(g3)
    c: Coincident(g5,g2)
    c: Coincident(g5,g3)
    c: Block(g0)
    c: Block(g5)
FEATURE [Part::Extrusion] Extrude070  label="sideA004"
  Base = -> Sketch080
  Dir = (0,0,1)
  DirMode = 2
  FaceMakerClass = Part::FaceMakerBullseye
  LengthFwd = 3
  LengthRev = 0
  Placement = pos=(0,0,-2.7) rot=(0,0,1;0rad)
  Solid = true
  Symmetric = false
FEATURE [Sketcher::SketchObject] Sketch081
  FullyConstrained = true
  Placement = pos=(117,19,0) rot=(0.57735,0.57735,0.57735;2.0944rad)
  sketch-geometry (8):
    g0: LineSegment StartX=-49.19 StartY=63.5 StartZ=0 EndX=-49.19 EndY=60.5 EndZ=0
    g1: LineSegment StartX=-49.19 StartY=11.5 StartZ=0 EndX=-49.19 EndY=8.5 EndZ=0
    g2: ArcOfCircle CenterX=-1.5 CenterY=62 CenterZ=0 NormalX=0 NormalY=0 NormalZ=1 AngleXU=0 Radius=1.5 StartAngle=4.71239 EndAngle=7.85398
    g3: ArcOfCircle CenterX=-1.5 CenterY=10 CenterZ=0 NormalX=0 NormalY=0 NormalZ=1 AngleXU=0 Radius=1.5 StartAngle=4.71239 EndAngle=7.85398
    g4: LineSegment StartX=-49.19 StartY=63.5 StartZ=0 EndX=-1.5 EndY=63.5 EndZ=0
    g5: LineSegment StartX=-49.19 StartY=60.5 StartZ=0 EndX=-1.5 EndY=60.5 EndZ=0
    g6: LineSegment StartX=-49.19 StartY=11.5 StartZ=0 EndX=-1.5 EndY=11.5 EndZ=0
    g7: LineSegment StartX=-49.19 StartY=8.5 StartZ=0 EndX=-1.5 EndY=8.5 EndZ=0
  constraints (19):
    c: Vertical(g0)
    c: Distance(g0) = 3
    c: Vertical(g1)
    c: Block(g1)
    c: Block(g2)
    c: Block(g3)
    c: Block(g0)
    c: Coincident(g4,g0)
    c: Coincident(g4,g2)
    c: Horizontal(g4)
    c: Coincident(g5,g0)
    c: Coincident(g5,g2)
    c: Horizontal(g5)
    c: Coincident(g6,g1)
    c: Coincident(g6,g3)
    c: Horizontal(g6)
    c: Coincident(g7,g1)
    c: Coincident(g7,g3)
    c: Horizontal(g7)
FEATURE [Part::Extrusion] Extrude071  label="sideB004"
  Base = -> Sketch079
  Dir = (0,0,1)
  DirMode = 2
  FaceMakerClass = Part::FaceMakerBullseye
  LengthFwd = 3
  LengthRev = 0
  Placement = pos=(0,0,71.7) rot=(0,0,1;0rad)
  Solid = true
  Symmetric = false
FEATURE [Part::MultiFuse] Fusion152  label="removeFromBottom004"
  Placement = pos=(2,0,0) rot=(0,0,1;0rad)
  Shapes = -> [Extrude070,Extrude071]
FEATURE [Part::Extrusion] Extrude072
  Base = -> Sketch081
  Dir = (1,0,0)
  DirMode = 2
  FaceMakerClass = Part::FaceMakerBullseye
  LengthFwd = 10
  LengthRev = 0
  Solid = true
  Symmetric = false
FEATURE [Part::Fillet] Fillet059  label="removeFromtMoreFrontCaseScrewRetainers004"
  Base = -> Extrude072
  Edges = 4 edges r=1.49: [Edge6,Edge11,Edge18,Edge23]
  Placement = pos=(-12,0,0) rot=(0,0,1;0rad)
FEATURE [Sketcher::SketchObject] Sketch082
  FullyConstrained = true
  Placement = pos=(117,19,0) rot=(0.57735,0.57735,0.57735;2.0944rad)
  sketch-geometry (8):
    g0: LineSegment StartX=-49.19 StartY=69.25 StartZ=0 EndX=-49.19 EndY=66.25 EndZ=0
    g1: LineSegment StartX=-49.19 StartY=5.75 StartZ=0 EndX=-49.19 EndY=2.75 EndZ=0
    g2: ArcOfCircle CenterX=-1.5 CenterY=67.75 CenterZ=0 NormalX=0 NormalY=0 NormalZ=1 AngleXU=0 Radius=1.5 StartAngle=4.71239 EndAngle=7.85398
    g3: ArcOfCircle CenterX=-1.5 CenterY=4.25 CenterZ=0 NormalX=0 NormalY=0 NormalZ=1 AngleXU=0 Radius=1.5 StartAngle=4.71239 EndAngle=7.85398
    g4: LineSegment StartX=-49.19 StartY=69.25 StartZ=0 EndX=-1.5 EndY=69.25 EndZ=0
    g5: LineSegment StartX=-49.19 StartY=66.25 StartZ=0 EndX=-1.5 EndY=66.25 EndZ=0
    g6: LineSegment StartX=-49.19 StartY=5.75 StartZ=0 EndX=-1.5 EndY=5.75 EndZ=0
    g7: LineSegment StartX=-49.19 StartY=2.75 StartZ=0 EndX=-1.5 EndY=2.75 EndZ=0
  constraints (19):
    c: Vertical(g0)
    c: Distance(g0) = 3
    c: Block(g0)
    c: Vertical(g1)
    c: Block(g2)
    c: Block(g3)
    c: Block(g1)
    c: Coincident(g4,g0)
    c: Coincident(g4,g2)
    c: Horizontal(g4)
    c: Coincident(g5,g0)
    c: Coincident(g5,g2)
    c: Horizontal(g5)
    c: Coincident(g6,g1)
    c: Coincident(g6,g3)
    c: Horizontal(g6)
    c: Coincident(g7,g1)
    c: Coincident(g7,g3)
    c: Horizontal(g7)
FEATURE [Part::Extrusion] Extrude073
  Base = -> Sketch082
  Dir = (1,0,0)
  DirMode = 2
  FaceMakerClass = Part::FaceMakerBullseye
  LengthFwd = 10
  LengthRev = 0
  Solid = true
  Symmetric = false
FEATURE [Part::Fillet] Fillet060  label="removeFromtMoreFrontCaseScrewRetainers005"
  Base = -> Extrude073
  Edges = 4 edges r=1.49: [Edge6,Edge11,Edge18,Edge23]
  Placement = pos=(-4,0,0) rot=(0,0,1;0rad)
FEATURE [Part::Revolution] Revolve163  label="backCaseScrewRetainer004"
  Angle = 360
  Axis = (0,1,0)
  Base = (0,0,0)
  FaceMakerClass = Part::FaceMakerBullseye
  Placement = pos=(12.5,3,62) rot=(0,0,1;0rad)
  Solid = false
  Source = -> Face149
  Symmetric = false
FEATURE [Part::Revolution] Revolve164  label="frontCaseScrewRetainer006"
  Angle = 360
  Axis = (0,1,0)
  Base = (0,0,0)
  FaceMakerClass = Part::FaceMakerBullseye
  Placement = pos=(89.5,3,68.5) rot=(0,0,1;0rad)
  Solid = false
  Source = -> Face151
  Symmetric = false
FEATURE [Part::Revolution] Revolve165  label="frontCaseScrewRetainer007"
  Angle = 360
  Axis = (0,1,0)
  Base = (0,0,0)
  FaceMakerClass = Part::FaceMakerBullseye
  Placement = pos=(89.5,3,3.5) rot=(0,0,1;0rad)
  Solid = false
  Source = -> Face152
  Symmetric = false
FEATURE [Part::Revolution] Revolve166  label="backCaseScrewRetainer005"
  Angle = 360
  Axis = (0,1,0)
  Base = (0,0,0)
  FaceMakerClass = Part::FaceMakerBullseye
  Placement = pos=(12.5,3,10) rot=(0,0,1;0rad)
  Solid = false
  Source = -> Face150
  Symmetric = false
FEATURE [Part::Revolution] Revolve167  label="moreFrontCaseScrewRetainer006"
  Angle = 360
  Axis = (0,1,0)
  Base = (0,0,0)
  FaceMakerClass = Part::FaceMakerBullseye
  Placement = pos=(109.5,4.5,68.5) rot=(0,0,1;0rad)
  Solid = false
  Source = -> Face153
  Symmetric = false
FEATURE [Part::Revolution] Revolve168  label="moreFrontCaseScrewRetainer007"
  Angle = 360
  Axis = (0,1,0)
  Base = (0,0,0)
  FaceMakerClass = Part::FaceMakerBullseye
  Placement = pos=(109.5,4.5,3.5) rot=(0,0,1;0rad)
  Solid = false
  Source = -> Face154
  Symmetric = false
FEATURE [Part::MultiFuse] Fusion151  label="screwRetainers003"
  Shapes = -> [Revolve168,Revolve167,Revolve166,Revolve165,Revolve164,Revolve163]
FEATURE [Part::Cut] Cut069  label="screwRetainers004"
  Base = -> Fusion151
  Tool = -> Fusion152
FEATURE [Part::Cut] Cut070
  Base = -> Cut069
  Tool = -> Fillet060
FEATURE [Part::Cut] Cut071  label="screwPillars001"
  Base = -> Cut070
  Tool = -> Fillet059
FEATURE [Part::MultiFuse] Fusion153  label="bottom024"
  Shapes = -> [Fusion149,Cut071]
FEATURE [Part::Cylinder] Cylinder067
  Angle = 360
  AttacherType = Attacher::AttachEngine3D
  Height = 10
  Placement = pos=(20.65,12,4.68) rot=(1,0,0;1.5708rad)
  Radius = 2
FEATURE [Part::Cylinder] Cylinder068
  Angle = 360
  AttacherType = Attacher::AttachEngine3D
  Height = 10
  Placement = pos=(20.65,12,67.38) rot=(1,0,0;1.5708rad)
  Radius = 2
FEATURE [Part::Cylinder] Cylinder069
  Angle = 360
  AttacherType = Attacher::AttachEngine3D
  Height = 10
  Placement = pos=(77.15,12,67.38) rot=(1,0,0;1.5708rad)
  Radius = 2
FEATURE [Part::Cylinder] Cylinder070
  Angle = 360
  AttacherType = Attacher::AttachEngine3D
  Height = 10
  Placement = pos=(77.15,12,4.68) rot=(1,0,0;1.5708rad)
  Radius = 2
FEATURE [Part::MultiFuse] Fusion154  label="removeFromThreadedInsertHousing001"
  Shapes = -> [Cylinder069,Cylinder068,Cylinder067,Cylinder070]
FEATURE [Part::Cut] Cut072  label="bottom025"
  Base = -> Fusion153
  Tool = -> Fusion154
FEATURE [Image::ImagePlane] ImagePlane
  XSize = 339
  YSize = 72
FEATURE [Sketcher::SketchObject] Sketch083
  FullyConstrained = true
  MapMode = 5
  Support = -> [XY_Plane]
  sketch-geometry (338):
    g0: LineSegment StartX=-151.619 StartY=28.8932 StartZ=0 EndX=-140.819 EndY=28.8932 EndZ=0
    g1: LineSegment StartX=-151.619 StartY=24.0313 StartZ=0 EndX=-151.619 EndY=28.8932 EndZ=0
    g2: LineSegment StartX=-140.819 StartY=17.7713 StartZ=0 EndX=-151.619 EndY=17.7713 EndZ=0
    g3: LineSegment StartX=-151.619 StartY=17.7713 StartZ=0 EndX=-151.619 EndY=22.6313 EndZ=0
    g4: LineSegment StartX=-151.619 StartY=22.6313 StartZ=0 EndX=-145.128 EndY=22.6313 EndZ=0
    g5: LineSegment StartX=-145.128 StartY=24.0313 StartZ=0 EndX=-140.819 EndY=28.8932 EndZ=0
    g6: LineSegment StartX=-145.128 StartY=22.6313 StartZ=0 EndX=-140.819 EndY=17.7713 EndZ=0
    g7: ArcOfCircle CenterX=-155.157 CenterY=23.3323 CenterZ=0 NormalX=0 NormalY=0 NormalZ=1 AngleXU=0 Radius=6.92354 StartAngle=1.03434 EndAngle=5.24885
    g8: ArcOfCircle CenterX=-155.157 CenterY=23.3323 CenterZ=0 NormalX=0 NormalY=0 NormalZ=1 AngleXU=0 Radius=12.6269 StartAngle=1.28675 EndAngle=4.99643
    g9: LineSegment StartX=-151.619 StartY=35.4532 StartZ=0 EndX=-151.619 EndY=29.2832 EndZ=0
    g10: LineSegment StartX=-151.619 StartY=17.3813 StartZ=0 EndX=-151.619 EndY=11.2113 EndZ=0
    g11-g21: Circle x11 (B-spline internal-alignment scaffolding for g22; pole/knot coordinates omitted)
    g22: BSplineCurve PolesCount=11 KnotsCount=9 Degree=3 IsPeriodic=0
    g23-g31: GeomPoint x9 (B-spline internal-alignment scaffolding for g22; pole/knot coordinates omitted)
    g32-g49: Circle x18 (B-spline internal-alignment scaffolding for g50; pole/knot coordinates omitted)
    g50: BSplineCurve PolesCount=18 KnotsCount=16 Degree=3 IsPeriodic=0
    g51-g66: GeomPoint x16 (B-spline internal-alignment scaffolding for g50; pole/knot coordinates omitted)
    g67: LineSegment StartX=-117.124 StartY=30.093 StartZ=0 EndX=-117.603 EndY=26.5272 EndZ=0
    g68: LineSegment StartX=-117.603 StartY=17.8472 StartZ=0 EndX=-117.124 EndY=14.2659 EndZ=0
    g69: Ellipse CenterX=-109.671 CenterY=20.025 CenterZ=0 NormalX=0 NormalY=0 NormalZ=1 MajorRadius=3.34798 MinorRadius=2.71052 AngleXU=-1.56793
    g70: GeomPoint X=-109.666 Y=18.0598 Z=0
    g71: GeomPoint X=-109.677 Y=21.9902 Z=0
    g72: Ellipse CenterX=-109.671 CenterY=20.0123 CenterZ=0 NormalX=0 NormalY=0 NormalZ=1 MajorRadius=6.93002 MinorRadius=6.36273 AngleXU=-3.13976
    g73: GeomPoint X=-112.417 Y=20.0073 Z=0
    g74: GeomPoint X=-106.925 Y=20.0173 Z=0
    g75: Ellipse CenterX=-51.7682 CenterY=20.1463 CenterZ=0 NormalX=0 NormalY=0 NormalZ=1 MajorRadius=3.19279 MinorRadius=2.71052 AngleXU=-1.52774
    g76: GeomPoint X=-51.6955 Y=18.4606 Z=0
    g77: GeomPoint X=-51.8408 Y=21.832 Z=0
    g78: GeomPoint X=-54.5142 Y=20.1413 Z=0
    g79: GeomPoint X=-49.0221 Y=20.1513 Z=0
    g80: Ellipse CenterX=-51.7682 CenterY=20.1463 CenterZ=0 NormalX=0 NormalY=0 NormalZ=1 MajorRadius=6.93002 MinorRadius=6.36273 AngleXU=-3.13976
    g81: Ellipse CenterX=-22.8436 CenterY=20.1783 CenterZ=0 NormalX=0 NormalY=0 NormalZ=1 MajorRadius=3.31512 MinorRadius=2.71052 AngleXU=-1.60214
    g82: GeomPoint X=-22.9034 Y=18.2706 Z=0
    g83: GeomPoint X=-22.7838 Y=22.0861 Z=0
    g84: GeomPoint X=-25.5897 Y=20.1733 Z=0
    g85: GeomPoint X=-20.0976 Y=20.1833 Z=0
    g86: Ellipse CenterX=-22.8436 CenterY=20.1783 CenterZ=0 NormalX=0 NormalY=0 NormalZ=1 MajorRadius=6.93002 MinorRadius=6.36273 AngleXU=-3.13976
    g87: LineSegment StartX=-101.889 StartY=14.1107 StartZ=0 EndX=-97.7455 EndY=14.1107 EndZ=0
    g88: LineSegment StartX=-93.8155 StartY=14.1107 StartZ=0 EndX=-89.6755 EndY=14.1107 EndZ=0
    g89: LineSegment StartX=-85.7455 StartY=14.1107 StartZ=0 EndX=-81.6055 EndY=14.1107 EndZ=0
    g90: LineSegment StartX=-101.889 StartY=14.1107 StartZ=0 EndX=-101.889 EndY=25.9907 EndZ=0
    g91: LineSegment StartX=-101.889 StartY=25.9907 StartZ=0 EndX=-97.8594 EndY=25.9907 EndZ=0
    g92: LineSegment StartX=-97.8594 StartY=25.9907 StartZ=0 EndX=-97.8594 EndY=24.0907 EndZ=0
    g93: LineSegment StartX=-97.7455 StartY=14.1107 StartZ=0 EndX=-97.7455 EndY=19.9107 EndZ=0
    g94: LineSegment StartX=-89.6755 StartY=14.1107 StartZ=0 EndX=-89.6755 EndY=19.9107 EndZ=0
    g95: LineSegment StartX=-93.8155 StartY=14.1107 StartZ=0 EndX=-93.8155 EndY=21.0107 EndZ=0
    g96-g106: Circle x11 (B-spline internal-alignment scaffolding for g107; pole/knot coordinates omitted)
    g107: BSplineCurve PolesCount=11 KnotsCount=9 Degree=3 IsPeriodic=0
    g108-g116: GeomPoint x9 (B-spline internal-alignment scaffolding for g107; pole/knot coordinates omitted)
    g117: BSplineCurve PolesCount=11 KnotsCount=9 Degree=3 IsPeriodic=0
    g118-g125: Circle x8 (B-spline internal-alignment scaffolding for g126; pole/knot coordinates omitted)
    g126: BSplineCurve PolesCount=8 KnotsCount=6 Degree=3 IsPeriodic=0
    g127-g132: GeomPoint x6 (B-spline internal-alignment scaffolding for g126; pole/knot coordinates omitted)
    g133: BSplineCurve PolesCount=8 KnotsCount=6 Degree=3 IsPeriodic=0
    g134: LineSegment StartX=-85.7455 StartY=21.0107 StartZ=0 EndX=-85.7455 EndY=14.1107 EndZ=0
    g135: LineSegment StartX=-80.0879 StartY=14.1107 StartZ=0 EndX=-75.944 EndY=14.1107 EndZ=0
    g136: LineSegment StartX=-72.014 StartY=14.1107 StartZ=0 EndX=-67.874 EndY=14.1107 EndZ=0
    g137: LineSegment StartX=-63.944 StartY=14.1107 StartZ=0 EndX=-59.804 EndY=14.1107 EndZ=0
    g138: LineSegment StartX=-80.0879 StartY=14.1107 StartZ=0 EndX=-80.0879 EndY=25.9907 EndZ=0
    g139: LineSegment StartX=-80.0879 StartY=25.9907 StartZ=0 EndX=-76.0579 EndY=25.9907 EndZ=0
    g140: LineSegment StartX=-76.0579 StartY=25.9907 StartZ=0 EndX=-76.0579 EndY=24.0907 EndZ=0
    g141: LineSegment StartX=-75.944 StartY=14.1107 StartZ=0 EndX=-75.944 EndY=19.9107 EndZ=0
    g142: LineSegment StartX=-67.874 StartY=14.1107 StartZ=0 EndX=-67.874 EndY=19.9107 EndZ=0
    g143: LineSegment StartX=-72.014 StartY=14.1107 StartZ=0 EndX=-72.014 EndY=21.0107 EndZ=0
    g144-g148: Circle x5 (B-spline internal-alignment scaffolding for g149; pole/knot coordinates omitted)
    g149: BSplineCurve PolesCount=11 KnotsCount=9 Degree=3 IsPeriodic=0
    g150-g158: GeomPoint x9 (B-spline internal-alignment scaffolding for g149; pole/knot coordinates omitted)
    g159: BSplineCurve PolesCount=11 KnotsCount=9 Degree=3 IsPeriodic=0
    g160-g167: Circle x8 (B-spline internal-alignment scaffolding for g168; pole/knot coordinates omitted)
    g168: BSplineCurve PolesCount=8 KnotsCount=6 Degree=3 IsPeriodic=0
    g169-g174: GeomPoint x6 (B-spline internal-alignment scaffolding for g168; pole/knot coordinates omitted)
    g175: BSplineCurve PolesCount=8 KnotsCount=6 Degree=3 IsPeriodic=0
    g176: LineSegment StartX=-63.944 StartY=21.0107 StartZ=0 EndX=-63.944 EndY=14.1107 EndZ=0
    g177: LineSegment StartX=-59.804 StartY=14.1107 StartZ=0 EndX=-59.804 EndY=21.5868 EndZ=0
    g178: BSplineCurve PolesCount=4 KnotsCount=2 Degree=3 IsPeriodic=0
    g179: GeomPoint X=-59.804 Y=21.5868 Z=0
    g180: GeomPoint X=-60.2379 Y=24.0907 Z=0
    g181: LineSegment StartX=-81.6055 StartY=14.1107 StartZ=0 EndX=-81.6055 EndY=21.5868 EndZ=0
    g182: LineSegment StartX=-151.619 StartY=24.0313 StartZ=0 EndX=-145.128 EndY=24.0313 EndZ=0
    g183: Circle CenterX=-82.0394 CenterY=24.0907 CenterZ=0 NormalX=0 NormalY=0 NormalZ=1 AngleXU=0 Radius=1
    g184: Circle CenterX=-81.7131 CenterY=23.2736 CenterZ=0 NormalX=0 NormalY=0 NormalZ=1 AngleXU=0 Radius=1
    g185: Circle CenterX=-81.6055 CenterY=21.5868 CenterZ=0 NormalX=0 NormalY=0 NormalZ=1 AngleXU=0 Radius=1
    g186: BSplineCurve PolesCount=3 KnotsCount=2 Degree=2 IsPeriodic=0
    g187: GeomPoint X=-82.0394 Y=24.0907 Z=0
    g188: GeomPoint X=-81.6055 Y=21.5868 Z=0
    g189: Ellipse CenterX=-37.3522 CenterY=19.9515 CenterZ=0 NormalX=0 NormalY=0 NormalZ=1 MajorRadius=2.99755 MinorRadius=2.49 AngleXU=1.5708
    g190: GeomPoint X=-37.3522 Y=21.6203 Z=0
    g191: GeomPoint X=-37.3522 Y=18.2826 Z=0
    g192: ArcOfEllipse CenterX=-38.7647 CenterY=20.06 CenterZ=0 NormalX=0 NormalY=0 NormalZ=1 MajorRadius=6.30025 MinorRadius=5.3849 AngleXU=1.57276 StartAngle=5.50632 EndAngle=10.3035
    g193: GeomPoint X=-38.7711 Y=23.3304 Z=0
    g194: GeomPoint X=-38.7583 Y=16.7895 Z=0
    g195: LineSegment StartX=-34.6109 StartY=14.1107 StartZ=0 EndX=-30.8984 EndY=14.1107 EndZ=0
    g196: LineSegment StartX=-30.8984 StartY=14.1107 StartZ=0 EndX=-30.8984 EndY=31.1784 EndZ=0
    g197: LineSegment StartX=-30.8984 StartY=31.1784 StartZ=0 EndX=-34.9984 EndY=31.1784 EndZ=0
    g198: LineSegment StartX=-34.9984 StartY=24.5602 StartZ=0 EndX=-34.9984 EndY=31.1784 EndZ=0
    g199: LineSegment StartX=-34.6109 StartY=16.0476 StartZ=0 EndX=-34.6109 EndY=14.1107 EndZ=0
    g200: LineSegment StartX=-14.8781 StartY=14.1107 StartZ=0 EndX=-10.5106 EndY=14.1107 EndZ=0
    g201: LineSegment StartX=-14.8781 StartY=14.1107 StartZ=0 EndX=-14.8781 EndY=25.8504 EndZ=0
    g202: LineSegment StartX=-14.8781 StartY=25.8504 StartZ=0 EndX=-10.8534 EndY=25.8504 EndZ=0
    g203: LineSegment StartX=-10.8534 StartY=25.8504 StartZ=0 EndX=-10.8534 EndY=24.0923 EndZ=0
    g204: LineSegment StartX=-10.5106 StartY=14.1107 StartZ=0 EndX=-10.5106 EndY=19.7752 EndZ=0
    g205: LineSegment StartX=-5.96397 StartY=25.9304 StartZ=0 EndX=-5.96397 EndY=22.574 EndZ=0
    g206-g214: Circle x9 (B-spline internal-alignment scaffolding for g215; pole/knot coordinates omitted)
    g215: BSplineCurve PolesCount=9 KnotsCount=7 Degree=3 IsPeriodic=0
    g216-g222: GeomPoint x7 (B-spline internal-alignment scaffolding for g215; pole/knot coordinates omitted)
    g223-g232: Circle x10 (B-spline internal-alignment scaffolding for g233; pole/knot coordinates omitted)
    g233: BSplineCurve PolesCount=10 KnotsCount=8 Degree=3 IsPeriodic=0
    g234-g241: GeomPoint x8 (B-spline internal-alignment scaffolding for g233; pole/knot coordinates omitted)
    g242: LineSegment StartX=-1.58923 StartY=21.0696 StartZ=0 EndX=2.62034 EndY=21.0696 EndZ=0
    g243: LineSegment StartX=-1.55856 StartY=18.7342 StartZ=0 EndX=6.45946 EndY=18.7342 EndZ=0
    g244: LineSegment StartX=5.29231 StartY=17.386 StartZ=0 EndX=5.29231 EndY=14.3674 EndZ=0
    g245-g269: Circle x25 (B-spline internal-alignment scaffolding for g270; pole/knot coordinates omitted)
    g270: BSplineCurve PolesCount=25 KnotsCount=23 Degree=3 IsPeriodic=0
    g271-g293: GeomPoint x23 (B-spline internal-alignment scaffolding for g270; pole/knot coordinates omitted)
    g294-g304: Circle x11 (B-spline internal-alignment scaffolding for g305; pole/knot coordinates omitted)
    g305: BSplineCurve PolesCount=11 KnotsCount=9 Degree=3 IsPeriodic=0
    g306-g314: GeomPoint x9 (B-spline internal-alignment scaffolding for g305; pole/knot coordinates omitted)
    g315-g326: Circle x12 (B-spline internal-alignment scaffolding for g327; pole/knot coordinates omitted)
    g327: BSplineCurve PolesCount=12 KnotsCount=10 Degree=3 IsPeriodic=0
    g328-g337: GeomPoint x10 (B-spline internal-alignment scaffolding for g327; pole/knot coordinates omitted)
  constraints (252):
    c: Coincident(g1,g0)
    c: Horizontal(g0)
    c: Vertical(g1)
    c: Coincident(g2,g3)
    c: Coincident(g3,g4)
    c: Horizontal(g4)
    c: Horizontal(g2)
    c: Vertical(g3)
    c: Block(g1)
    c: Distance(g3) = 4.86
    c: Block(g4)
    c: Distance(g0) = 10.8
    c: Distance(g2) = 10.8
    c: Coincident(g5,g0)
    c: Coincident(g6,g4)
    c: Coincident(g6,g2)
    c: Block(g8)
    c: Block(g7)
    c: Coincident(g9,g8)
    c: Coincident(g9,g7)
    c: Vertical(g9)
    c: Coincident(g10,g7)
    c: Coincident(g10,g8)
    c: Vertical(g10)
    c: Weight(g11) = 1
    c: Equal(g11, g12-g21) x10
    c: InternalAlignment(g11-g21 -> g22) x11
    c: InternalAlignment(g23-g31 -> g22) x9
    c: Block(g22)
    c: Weight(g32) = 1
    c: Equal(g32, g33-g49) x17
    c: InternalAlignment(g32-g49 -> g50) x18
    c: InternalAlignment(g51-g66 -> g50) x16
    c: Block(g50)
    c: Coincident(g67,g50)
    c: Coincident(g67,g22)
    c: Coincident(g68,g22)
    c: Coincident(g68,g50)
    c: InternalAlignment(g70,g69)
    c: InternalAlignment(g71,g69)
    c: Block(g69)
    c: InternalAlignment(g73,g72)
    c: InternalAlignment(g74,g72)
    c: Block(g72)
    c: InternalAlignment(g76,g75)
    c: InternalAlignment(g77,g75)
    c: InternalAlignment(g78,g80)
    c: InternalAlignment(g79,g80)
    c: Block(g80)
    c: Coincident(g75,g80)
    c: Block(g75)
    c: InternalAlignment(g82,g81)
    c: InternalAlignment(g83,g81)
    c: InternalAlignment(g84,g86)
    c: InternalAlignment(g85,g86)
    c: Block(g86)
    c: Coincident(g81,g86)
    c: Block(g81)
    c: Horizontal(g87)
    c: Block(g87)
    c: Horizontal(g88)
    c: Distance(g88) = 4.14
    c: Horizontal(g89)
    c: Equal(g88,g89) = 4.14
    c: Block(g89)
    c: Block(g88)
    c: Coincident(g90,g87)
    c: Vertical(g90)
    c: Distance(g90) = 11.88
    c: Coincident(g91,g90)
    c: Horizontal(g91)
    c: Coincident(g92,g91)
    c: Vertical(g92)
    c: Distance(g91) = 4.03
    c: Distance(g92) = 1.9
    c: Coincident(g93,g87)
    c: Vertical(g93)
    c: Vertical(g94)
    c: Coincident(g94,g88)
    c: Distance(g93) = 5.8
    c: Distance(g94) = 5.8
    c: Vertical(g95)
    c: Coincident(g95,g88)
    c: Distance(g95) = 6.9
    c: Coincident(g107,g92)
    c: Weight(g96) = 1
    c: Equal(g96, g97-g106) x10
    c: InternalAlignment(g96-g106 -> g107) x11
    c: InternalAlignment(g108-g116 -> g107) x9
    c: Block(g107)
    c: Block(g117)
    c: Coincident(g126,g93)
    c: Weight(g118) = 1
    c: Equal(g118, g119-g125) x7
    c: Coincident(g126,g95)
    c: InternalAlignment(g118-g125 -> g126) x8
    c: InternalAlignment(g127-g132 -> g126) x6
    c: Coincident(g133,g94)
    c: Block(g126)
    c: Block(g133)
    c: Coincident(g134,g133)
    c: Coincident(g134,g89)
    c: Vertical(g134)
    c: Horizontal(g135)
    c: Block(g135)
    c: Horizontal(g136)
    c: Equal(g88,g136) = 4.14
    c: Horizontal(g137)
    c: Equal(g136,g137) = 4.14
    c: Block(g137)
    c: Block(g136)
    c: Coincident(g138,g135)
    c: Vertical(g138)
    c: Equal(g90,g138) = 11.88
    c: Coincident(g139,g138)
    c: Horizontal(g139)
    c: Coincident(g140,g139)
    c: Vertical(g140)
    c: Equal(g91,g139) = 4.03
    c: Equal(g92,g140) = 1.9
    c: Coincident(g141,g135)
    c: Vertical(g141)
    c: Vertical(g142)
    c: Coincident(g142,g136)
    c: Equal(g93,g141) = 5.8
    c: Equal(g94,g142) = 5.8
    c: Vertical(g143)
    c: Coincident(g143,g136)
    c: Equal(g95,g143) = 6.9
    c: Coincident(g149,g140)
    c: Equal(g96,g144) = 1
    c: Equal(g144, g145-g148) x4
    c: InternalAlignment(g144-g148 -> g149) x5
    c: InternalAlignment(g150-g158 -> g149) x9
    c: Block(g149)
    c: Block(g159)
    c: Coincident(g168,g141)
    c: Equal(g118,g160) = 1
    c: Equal(g160, g161-g167) x7
    c: Coincident(g168,g143)
    c: InternalAlignment(g160-g167 -> g168) x8
    c: InternalAlignment(g169-g174 -> g168) x6
    c: Coincident(g175,g142)
    c: Block(g168)
    c: Block(g175)
    c: Coincident(g176,g175)
    c: Coincident(g176,g137)
    c: Vertical(g176)
    c: Coincident(g177,g137)
    c: Vertical(g177)
    c: Coincident(g178,g177)
    c: Coincident(g178,g159)
    c: InternalAlignment(g179,g178)
    c: InternalAlignment(g180,g178)
    c: Block(g178)
    c: Vertical(g181)
    c: Coincident(g181,g89)
    c: Block(g5)
    c: Coincident(g182,g1)
    c: Coincident(g182,g5)
    c: Horizontal(g182)
    c: Coincident(g186,g117)
    c: Weight(g183) = 1
    c: Equal(g183,g184)
    c: Equal(g183,g185)
    c: Coincident(g186,g181)
    c: InternalAlignment(g183,g186)
    c: InternalAlignment(g184,g186)
    c: InternalAlignment(g185,g186)
    c: InternalAlignment(g187,g186)
    c: InternalAlignment(g188,g186)
    c: Block(g186)
    c: InternalAlignment(g190,g189)
    c: InternalAlignment(g191,g189)
    c: Block(g189)
    c: InternalAlignment(g193,g192)
    c: InternalAlignment(g194,g192)
    c: Block(g192)
    c: Horizontal(g195)
    c: Block(g195)
    c: Coincident(g196,g195)
    c: Vertical(g196)
    c: Block(g196)
    c: Distance(g195) = 3.71244
    c: Coincident(g197,g196)
    c: Horizontal(g197)
    c: Distance(g197) = 4.1
    c: Coincident(g198,g192)
    c: Coincident(g198,g197)
    c: Vertical(g198)
    c: Block(g198)
    c: Coincident(g199,g192)
    c: Coincident(g199,g195)
    c: Vertical(g199)
    c: Block(g199)
    c: Horizontal(g200)
    c: Block(g200)
    c: Coincident(g201,g200)
    c: Vertical(g201)
    c: Block(g201)
    c: Coincident(g202,g201)
    c: Horizontal(g202)
    c: Block(g202)
    c: Coincident(g203,g202)
    c: Vertical(g203)
    c: Block(g203)
    c: Coincident(g204,g200)
    c: Vertical(g204)
    c: Block(g204)
    c: Coincident(g215,g203)
    c: Weight(g206) = 1
    c: Equal(g206, g207-g214) x8
    c: Coincident(g215,g205)
    c: InternalAlignment(g206-g214 -> g215) x9
    c: InternalAlignment(g216-g222 -> g215) x7
    c: Coincident(g233,g204)
    c: Weight(g223) = 1
    c: Equal(g223, g224-g232) x9
    c: Coincident(g233,g205)
    c: InternalAlignment(g223-g232 -> g233) x10
    c: InternalAlignment(g234-g241 -> g233) x8
    c: Vertical(g205)
    c: Block(g205)
    c: Block(g215)
    c: Block(g233)
    c: Horizontal(g242)
    c: Horizontal(g243)
    c: Block(g242)
    c: Block(g243)
    c: Vertical(g244)
    c: Block(g244)
    c: Coincident(g270,g243)
    c: Weight(g245) = 1
    c: Equal(g245, g246-g269) x24
    c: Coincident(g270,g244)
    c: InternalAlignment(g245-g269 -> g270) x25
    c: InternalAlignment(g271-g293 -> g270) x23
    c: Coincident(g305,g242)
    c: Weight(g294) = 1
    c: Equal(g294, g295-g304) x10
    c: Coincident(g305,g242)
    c: InternalAlignment(g294-g304 -> g305) x11
    c: InternalAlignment(g306-g314 -> g305) x9
    c: Block(g305)
    c: Coincident(g327,g243)
    c: Weight(g315) = 1
    c: Equal(g315, g316-g326) x11
    c: Coincident(g327,g244)
    c: InternalAlignment(g315-g326 -> g327) x12
    c: InternalAlignment(g328-g337 -> g327) x10
    c: Block(g327)
    c: Block(g270)
FEATURE [PartDesign::Body] Body  label="CommodoreLogoAndText"
  Group = -> [Sketch083]
  Origin = -> Origin
FEATURE [Part::Extrusion] Extrude074  label="CommodoreLogoAndText001"
  Base = -> Sketch083
  Dir = (0,0,1)
  DirMode = 2
  FaceMakerClass = Part::FaceMakerBullseye
  LengthFwd = 10
  LengthRev = 0
  Solid = true
  Symmetric = false
FEATURE [Part::FeaturePython] Clone  label="CommodoreLogoAndTextScale"  # Draft clone (typed FeaturePython)
  AttacherType = Attacher::AttachEngine3D
  Fuse = false
  Objects = -> [Extrude074]
  Placement = pos=(111,5.37,-11.6) rot=(0,0,1;0rad)
  Scale = (0.62,0.62,1)
FEATURE [Part::Mirroring] Part__Mirroring  label="CommodoreLogoAndTextScale (Mirror #1)"
  Base = (0,0,0)
  Normal = (1,0,0)
  Placement = pos=(123.576,0,0) rot=(0,0,1;0rad)
  Source = -> Clone
FEATURE [Sketcher::SketchObject] Sketch084
  FullyConstrained = true
  MapMode = 5
  Support = -> [XY_Plane001]
  sketch-geometry (338):
    g0: LineSegment StartX=-151.619 StartY=28.8932 StartZ=0 EndX=-140.819 EndY=28.8932 EndZ=0
    g1: LineSegment StartX=-151.619 StartY=24.0313 StartZ=0 EndX=-151.619 EndY=28.8932 EndZ=0
    g2: LineSegment StartX=-140.819 StartY=17.7713 StartZ=0 EndX=-151.619 EndY=17.7713 EndZ=0
    g3: LineSegment StartX=-151.619 StartY=17.7713 StartZ=0 EndX=-151.619 EndY=22.6313 EndZ=0
    g4: LineSegment StartX=-151.619 StartY=22.6313 StartZ=0 EndX=-145.128 EndY=22.6313 EndZ=0
    g5: LineSegment StartX=-145.128 StartY=24.0313 StartZ=0 EndX=-140.819 EndY=28.8932 EndZ=0
    g6: LineSegment StartX=-145.128 StartY=22.6313 StartZ=0 EndX=-140.819 EndY=17.7713 EndZ=0
    g7: ArcOfCircle CenterX=-155.157 CenterY=23.3323 CenterZ=0 NormalX=0 NormalY=0 NormalZ=1 AngleXU=0 Radius=6.92354 StartAngle=1.03434 EndAngle=5.24885
    g8: ArcOfCircle CenterX=-155.157 CenterY=23.3323 CenterZ=0 NormalX=0 NormalY=0 NormalZ=1 AngleXU=0 Radius=12.6269 StartAngle=1.28675 EndAngle=4.99643
    g9: LineSegment StartX=-151.619 StartY=35.4532 StartZ=0 EndX=-151.619 EndY=29.2832 EndZ=0
    g10: LineSegment StartX=-151.619 StartY=17.3813 StartZ=0 EndX=-151.619 EndY=11.2113 EndZ=0
    g11-g21: Circle x11 (B-spline internal-alignment scaffolding for g22; pole/knot coordinates omitted)
    g22: BSplineCurve PolesCount=11 KnotsCount=9 Degree=3 IsPeriodic=0
    g23-g31: GeomPoint x9 (B-spline internal-alignment scaffolding for g22; pole/knot coordinates omitted)
    g32-g49: Circle x18 (B-spline internal-alignment scaffolding for g50; pole/knot coordinates omitted)
    g50: BSplineCurve PolesCount=18 KnotsCount=16 Degree=3 IsPeriodic=0
    g51-g66: GeomPoint x16 (B-spline internal-alignment scaffolding for g50; pole/knot coordinates omitted)
    g67: LineSegment StartX=-117.124 StartY=30.093 StartZ=0 EndX=-117.603 EndY=26.5272 EndZ=0
    g68: LineSegment StartX=-117.603 StartY=17.8472 StartZ=0 EndX=-117.124 EndY=14.2659 EndZ=0
    g69: Ellipse CenterX=-109.671 CenterY=20.025 CenterZ=0 NormalX=0 NormalY=0 NormalZ=1 MajorRadius=3.34798 MinorRadius=2.71052 AngleXU=-1.56793
    g70: GeomPoint X=-109.666 Y=18.0598 Z=0
    g71: GeomPoint X=-109.677 Y=21.9902 Z=0
    g72: Ellipse CenterX=-109.671 CenterY=20.0123 CenterZ=0 NormalX=0 NormalY=0 NormalZ=1 MajorRadius=6.93002 MinorRadius=6.36273 AngleXU=-3.13976
    g73: GeomPoint X=-112.417 Y=20.0073 Z=0
    g74: GeomPoint X=-106.925 Y=20.0173 Z=0
    g75: Ellipse CenterX=-51.7682 CenterY=20.1463 CenterZ=0 NormalX=0 NormalY=0 NormalZ=1 MajorRadius=3.19279 MinorRadius=2.71052 AngleXU=-1.52774
    g76: GeomPoint X=-51.6955 Y=18.4606 Z=0
    g77: GeomPoint X=-51.8408 Y=21.832 Z=0
    g78: GeomPoint X=-54.5142 Y=20.1413 Z=0
    g79: GeomPoint X=-49.0221 Y=20.1513 Z=0
    g80: Ellipse CenterX=-51.7682 CenterY=20.1463 CenterZ=0 NormalX=0 NormalY=0 NormalZ=1 MajorRadius=6.93002 MinorRadius=6.36273 AngleXU=-3.13976
    g81: Ellipse CenterX=-22.8436 CenterY=20.1783 CenterZ=0 NormalX=0 NormalY=0 NormalZ=1 MajorRadius=3.31512 MinorRadius=2.71052 AngleXU=-1.60214
    g82: GeomPoint X=-22.9034 Y=18.2706 Z=0
    g83: GeomPoint X=-22.7838 Y=22.0861 Z=0
    g84: GeomPoint X=-25.5897 Y=20.1733 Z=0
    g85: GeomPoint X=-20.0976 Y=20.1833 Z=0
    g86: Ellipse CenterX=-22.8436 CenterY=20.1783 CenterZ=0 NormalX=0 NormalY=0 NormalZ=1 MajorRadius=6.93002 MinorRadius=6.36273 AngleXU=-3.13976
    g87: LineSegment StartX=-101.889 StartY=14.1107 StartZ=0 EndX=-97.7455 EndY=14.1107 EndZ=0
    g88: LineSegment StartX=-93.8155 StartY=14.1107 StartZ=0 EndX=-89.6755 EndY=14.1107 EndZ=0
    g89: LineSegment StartX=-85.7455 StartY=14.1107 StartZ=0 EndX=-81.6055 EndY=14.1107 EndZ=0
    g90: LineSegment StartX=-101.889 StartY=14.1107 StartZ=0 EndX=-101.889 EndY=25.9907 EndZ=0
    g91: LineSegment StartX=-101.889 StartY=25.9907 StartZ=0 EndX=-97.8594 EndY=25.9907 EndZ=0
    g92: LineSegment StartX=-97.8594 StartY=25.9907 StartZ=0 EndX=-97.8594 EndY=24.0907 EndZ=0
    g93: LineSegment StartX=-97.7455 StartY=14.1107 StartZ=0 EndX=-97.7455 EndY=19.9107 EndZ=0
    g94: LineSegment StartX=-89.6755 StartY=14.1107 StartZ=0 EndX=-89.6755 EndY=19.9107 EndZ=0
    g95: LineSegment StartX=-93.8155 StartY=14.1107 StartZ=0 EndX=-93.8155 EndY=21.0107 EndZ=0
    g96-g106: Circle x11 (B-spline internal-alignment scaffolding for g107; pole/knot coordinates omitted)
    g107: BSplineCurve PolesCount=11 KnotsCount=9 Degree=3 IsPeriodic=0
    g108-g116: GeomPoint x9 (B-spline internal-alignment scaffolding for g107; pole/knot coordinates omitted)
    g117: BSplineCurve PolesCount=11 KnotsCount=9 Degree=3 IsPeriodic=0
    g118-g125: Circle x8 (B-spline internal-alignment scaffolding for g126; pole/knot coordinates omitted)
    g126: BSplineCurve PolesCount=8 KnotsCount=6 Degree=3 IsPeriodic=0
    g127-g132: GeomPoint x6 (B-spline internal-alignment scaffolding for g126; pole/knot coordinates omitted)
    g133: BSplineCurve PolesCount=8 KnotsCount=6 Degree=3 IsPeriodic=0
    g134: LineSegment StartX=-85.7455 StartY=21.0107 StartZ=0 EndX=-85.7455 EndY=14.1107 EndZ=0
    g135: LineSegment StartX=-80.0879 StartY=14.1107 StartZ=0 EndX=-75.944 EndY=14.1107 EndZ=0
    g136: LineSegment StartX=-72.014 StartY=14.1107 StartZ=0 EndX=-67.874 EndY=14.1107 EndZ=0
    g137: LineSegment StartX=-63.944 StartY=14.1107 StartZ=0 EndX=-59.804 EndY=14.1107 EndZ=0
    g138: LineSegment StartX=-80.0879 StartY=14.1107 StartZ=0 EndX=-80.0879 EndY=25.9907 EndZ=0
    g139: LineSegment StartX=-80.0879 StartY=25.9907 StartZ=0 EndX=-76.0579 EndY=25.9907 EndZ=0
    g140: LineSegment StartX=-76.0579 StartY=25.9907 StartZ=0 EndX=-76.0579 EndY=24.0907 EndZ=0
    g141: LineSegment StartX=-75.944 StartY=14.1107 StartZ=0 EndX=-75.944 EndY=19.9107 EndZ=0
    g142: LineSegment StartX=-67.874 StartY=14.1107 StartZ=0 EndX=-67.874 EndY=19.9107 EndZ=0
    g143: LineSegment StartX=-72.014 StartY=14.1107 StartZ=0 EndX=-72.014 EndY=21.0107 EndZ=0
    g144-g148: Circle x5 (B-spline internal-alignment scaffolding for g149; pole/knot coordinates omitted)
    g149: BSplineCurve PolesCount=11 KnotsCount=9 Degree=3 IsPeriodic=0
    g150-g158: GeomPoint x9 (B-spline internal-alignment scaffolding for g149; pole/knot coordinates omitted)
    g159: BSplineCurve PolesCount=11 KnotsCount=9 Degree=3 IsPeriodic=0
    g160-g167: Circle x8 (B-spline internal-alignment scaffolding for g168; pole/knot coordinates omitted)
    g168: BSplineCurve PolesCount=8 KnotsCount=6 Degree=3 IsPeriodic=0
    g169-g174: GeomPoint x6 (B-spline internal-alignment scaffolding for g168; pole/knot coordinates omitted)
    g175: BSplineCurve PolesCount=8 KnotsCount=6 Degree=3 IsPeriodic=0
    g176: LineSegment StartX=-63.944 StartY=21.0107 StartZ=0 EndX=-63.944 EndY=14.1107 EndZ=0
    g177: LineSegment StartX=-59.804 StartY=14.1107 StartZ=0 EndX=-59.804 EndY=21.5868 EndZ=0
    g178: BSplineCurve PolesCount=4 KnotsCount=2 Degree=3 IsPeriodic=0
    g179: GeomPoint X=-59.804 Y=21.5868 Z=0
    g180: GeomPoint X=-60.2379 Y=24.0907 Z=0
    g181: LineSegment StartX=-81.6055 StartY=14.1107 StartZ=0 EndX=-81.6055 EndY=21.5868 EndZ=0
    g182: LineSegment StartX=-151.619 StartY=24.0313 StartZ=0 EndX=-145.128 EndY=24.0313 EndZ=0
    g183: Circle CenterX=-82.0394 CenterY=24.0907 CenterZ=0 NormalX=0 NormalY=0 NormalZ=1 AngleXU=0 Radius=1
    g184: Circle CenterX=-81.7131 CenterY=23.2736 CenterZ=0 NormalX=0 NormalY=0 NormalZ=1 AngleXU=0 Radius=1
    g185: Circle CenterX=-81.6055 CenterY=21.5868 CenterZ=0 NormalX=0 NormalY=0 NormalZ=1 AngleXU=0 Radius=1
    g186: BSplineCurve PolesCount=3 KnotsCount=2 Degree=2 IsPeriodic=0
    g187: GeomPoint X=-82.0394 Y=24.0907 Z=0
    g188: GeomPoint X=-81.6055 Y=21.5868 Z=0
    g189: Ellipse CenterX=-37.3522 CenterY=19.9515 CenterZ=0 NormalX=0 NormalY=0 NormalZ=1 MajorRadius=2.99755 MinorRadius=2.49 AngleXU=1.5708
    g190: GeomPoint X=-37.3522 Y=21.6203 Z=0
    g191: GeomPoint X=-37.3522 Y=18.2826 Z=0
    g192: ArcOfEllipse CenterX=-38.7647 CenterY=20.06 CenterZ=0 NormalX=0 NormalY=0 NormalZ=1 MajorRadius=6.30025 MinorRadius=5.3849 AngleXU=1.57276 StartAngle=5.50632 EndAngle=10.3035
    g193: GeomPoint X=-38.7711 Y=23.3304 Z=0
    g194: GeomPoint X=-38.7583 Y=16.7895 Z=0
    g195: LineSegment StartX=-34.6109 StartY=14.1107 StartZ=0 EndX=-30.8984 EndY=14.1107 EndZ=0
    g196: LineSegment StartX=-30.8984 StartY=14.1107 StartZ=0 EndX=-30.8984 EndY=31.1784 EndZ=0
    g197: LineSegment StartX=-30.8984 StartY=31.1784 StartZ=0 EndX=-34.9984 EndY=31.1784 EndZ=0
    g198: LineSegment StartX=-34.9984 StartY=24.5602 StartZ=0 EndX=-34.9984 EndY=31.1784 EndZ=0
    g199: LineSegment StartX=-34.6109 StartY=16.0476 StartZ=0 EndX=-34.6109 EndY=14.1107 EndZ=0
    g200: LineSegment StartX=-14.8781 StartY=14.1107 StartZ=0 EndX=-10.5106 EndY=14.1107 EndZ=0
    g201: LineSegment StartX=-14.8781 StartY=14.1107 StartZ=0 EndX=-14.8781 EndY=25.8504 EndZ=0
    g202: LineSegment StartX=-14.8781 StartY=25.8504 StartZ=0 EndX=-10.8534 EndY=25.8504 EndZ=0
    g203: LineSegment StartX=-10.8534 StartY=25.8504 StartZ=0 EndX=-10.8534 EndY=24.0923 EndZ=0
    g204: LineSegment StartX=-10.5106 StartY=14.1107 StartZ=0 EndX=-10.5106 EndY=19.7752 EndZ=0
    g205: LineSegment StartX=-5.96397 StartY=25.9304 StartZ=0 EndX=-5.96397 EndY=22.574 EndZ=0
    g206-g214: Circle x9 (B-spline internal-alignment scaffolding for g215; pole/knot coordinates omitted)
    g215: BSplineCurve PolesCount=9 KnotsCount=7 Degree=3 IsPeriodic=0
    g216-g222: GeomPoint x7 (B-spline internal-alignment scaffolding for g215; pole/knot coordinates omitted)
    g223-g232: Circle x10 (B-spline internal-alignment scaffolding for g233; pole/knot coordinates omitted)
    g233: BSplineCurve PolesCount=10 KnotsCount=8 Degree=3 IsPeriodic=0
    g234-g241: GeomPoint x8 (B-spline internal-alignment scaffolding for g233; pole/knot coordinates omitted)
    g242: LineSegment StartX=-1.58923 StartY=21.0696 StartZ=0 EndX=2.62034 EndY=21.0696 EndZ=0
    g243: LineSegment StartX=-1.55856 StartY=18.7342 StartZ=0 EndX=6.45946 EndY=18.7342 EndZ=0
    g244: LineSegment StartX=5.29231 StartY=17.386 StartZ=0 EndX=5.29231 EndY=14.3674 EndZ=0
    g245-g269: Circle x25 (B-spline internal-alignment scaffolding for g270; pole/knot coordinates omitted)
    g270: BSplineCurve PolesCount=25 KnotsCount=23 Degree=3 IsPeriodic=0
    g271-g293: GeomPoint x23 (B-spline internal-alignment scaffolding for g270; pole/knot coordinates omitted)
    g294-g304: Circle x11 (B-spline internal-alignment scaffolding for g305; pole/knot coordinates omitted)
    g305: BSplineCurve PolesCount=11 KnotsCount=9 Degree=3 IsPeriodic=0
    g306-g314: GeomPoint x9 (B-spline internal-alignment scaffolding for g305; pole/knot coordinates omitted)
    g315-g326: Circle x12 (B-spline internal-alignment scaffolding for g327; pole/knot coordinates omitted)
    g327: BSplineCurve PolesCount=12 KnotsCount=10 Degree=3 IsPeriodic=0
    g328-g337: GeomPoint x10 (B-spline internal-alignment scaffolding for g327; pole/knot coordinates omitted)
  constraints (252):
    c: Coincident(g1,g0)
    c: Horizontal(g0)
    c: Vertical(g1)
    c: Coincident(g2,g3)
    c: Coincident(g3,g4)
    c: Horizontal(g4)
    c: Horizontal(g2)
    c: Vertical(g3)
    c: Block(g1)
    c: Distance(g3) = 4.86
    c: Block(g4)
    c: Distance(g0) = 10.8
    c: Distance(g2) = 10.8
    c: Coincident(g5,g0)
    c: Coincident(g6,g4)
    c: Coincident(g6,g2)
    c: Block(g8)
    c: Block(g7)
    c: Coincident(g9,g8)
    c: Coincident(g9,g7)
    c: Vertical(g9)
    c: Coincident(g10,g7)
    c: Coincident(g10,g8)
    c: Vertical(g10)
    c: Weight(g11) = 1
    c: Equal(g11, g12-g21) x10
    c: InternalAlignment(g11-g21 -> g22) x11
    c: InternalAlignment(g23-g31 -> g22) x9
    c: Block(g22)
    c: Weight(g32) = 1
    c: Equal(g32, g33-g49) x17
    c: InternalAlignment(g32-g49 -> g50) x18
    c: InternalAlignment(g51-g66 -> g50) x16
    c: Block(g50)
    c: Coincident(g67,g50)
    c: Coincident(g67,g22)
    c: Coincident(g68,g22)
    c: Coincident(g68,g50)
    c: InternalAlignment(g70,g69)
    c: InternalAlignment(g71,g69)
    c: Block(g69)
    c: InternalAlignment(g73,g72)
    c: InternalAlignment(g74,g72)
    c: Block(g72)
    c: InternalAlignment(g76,g75)
    c: InternalAlignment(g77,g75)
    c: InternalAlignment(g78,g80)
    c: InternalAlignment(g79,g80)
    c: Block(g80)
    c: Coincident(g75,g80)
    c: Block(g75)
    c: InternalAlignment(g82,g81)
    c: InternalAlignment(g83,g81)
    c: InternalAlignment(g84,g86)
    c: InternalAlignment(g85,g86)
    c: Block(g86)
    c: Coincident(g81,g86)
    c: Block(g81)
    c: Horizontal(g87)
    c: Block(g87)
    c: Horizontal(g88)
    c: Distance(g88) = 4.14
    c: Horizontal(g89)
    c: Equal(g88,g89) = 4.14
    c: Block(g89)
    c: Block(g88)
    c: Coincident(g90,g87)
    c: Vertical(g90)
    c: Distance(g90) = 11.88
    c: Coincident(g91,g90)
    c: Horizontal(g91)
    c: Coincident(g92,g91)
    c: Vertical(g92)
    c: Distance(g91) = 4.03
    c: Distance(g92) = 1.9
    c: Coincident(g93,g87)
    c: Vertical(g93)
    c: Vertical(g94)
    c: Coincident(g94,g88)
    c: Distance(g93) = 5.8
    c: Distance(g94) = 5.8
    c: Vertical(g95)
    c: Coincident(g95,g88)
    c: Distance(g95) = 6.9
    c: Coincident(g107,g92)
    c: Weight(g96) = 1
    c: Equal(g96, g97-g106) x10
    c: InternalAlignment(g96-g106 -> g107) x11
    c: InternalAlignment(g108-g116 -> g107) x9
    c: Block(g107)
    c: Block(g117)
    c: Coincident(g126,g93)
    c: Weight(g118) = 1
    c: Equal(g118, g119-g125) x7
    c: Coincident(g126,g95)
    c: InternalAlignment(g118-g125 -> g126) x8
    c: InternalAlignment(g127-g132 -> g126) x6
    c: Coincident(g133,g94)
    c: Block(g126)
    c: Block(g133)
    c: Coincident(g134,g133)
    c: Coincident(g134,g89)
    c: Vertical(g134)
    c: Horizontal(g135)
    c: Block(g135)
    c: Horizontal(g136)
    c: Equal(g88,g136) = 4.14
    c: Horizontal(g137)
    c: Equal(g136,g137) = 4.14
    c: Block(g137)
    c: Block(g136)
    c: Coincident(g138,g135)
    c: Vertical(g138)
    c: Equal(g90,g138) = 11.88
    c: Coincident(g139,g138)
    c: Horizontal(g139)
    c: Coincident(g140,g139)
    c: Vertical(g140)
    c: Equal(g91,g139) = 4.03
    c: Equal(g92,g140) = 1.9
    c: Coincident(g141,g135)
    c: Vertical(g141)
    c: Vertical(g142)
    c: Coincident(g142,g136)
    c: Equal(g93,g141) = 5.8
    c: Equal(g94,g142) = 5.8
    c: Vertical(g143)
    c: Coincident(g143,g136)
    c: Equal(g95,g143) = 6.9
    c: Coincident(g149,g140)
    c: Equal(g96,g144) = 1
    c: Equal(g144, g145-g148) x4
    c: InternalAlignment(g144-g148 -> g149) x5
    c: InternalAlignment(g150-g158 -> g149) x9
    c: Block(g149)
    c: Block(g159)
    c: Coincident(g168,g141)
    c: Equal(g118,g160) = 1
    c: Equal(g160, g161-g167) x7
    c: Coincident(g168,g143)
    c: InternalAlignment(g160-g167 -> g168) x8
    c: InternalAlignment(g169-g174 -> g168) x6
    c: Coincident(g175,g142)
    c: Block(g168)
    c: Block(g175)
    c: Coincident(g176,g175)
    c: Coincident(g176,g137)
    c: Vertical(g176)
    c: Coincident(g177,g137)
    c: Vertical(g177)
    c: Coincident(g178,g177)
    c: Coincident(g178,g159)
    c: InternalAlignment(g179,g178)
    c: InternalAlignment(g180,g178)
    c: Block(g178)
    c: Vertical(g181)
    c: Coincident(g181,g89)
    c: Block(g5)
    c: Coincident(g182,g1)
    c: Coincident(g182,g5)
    c: Horizontal(g182)
    c: Coincident(g186,g117)
    c: Weight(g183) = 1
    c: Equal(g183,g184)
    c: Equal(g183,g185)
    c: Coincident(g186,g181)
    c: InternalAlignment(g183,g186)
    c: InternalAlignment(g184,g186)
    c: InternalAlignment(g185,g186)
    c: InternalAlignment(g187,g186)
    c: InternalAlignment(g188,g186)
    c: Block(g186)
    c: InternalAlignment(g190,g189)
    c: InternalAlignment(g191,g189)
    c: Block(g189)
    c: InternalAlignment(g193,g192)
    c: InternalAlignment(g194,g192)
    c: Block(g192)
    c: Horizontal(g195)
    c: Block(g195)
    c: Coincident(g196,g195)
    c: Vertical(g196)
    c: Block(g196)
    c: Distance(g195) = 3.71244
    c: Coincident(g197,g196)
    c: Horizontal(g197)
    c: Distance(g197) = 4.1
    c: Coincident(g198,g192)
    c: Coincident(g198,g197)
    c: Vertical(g198)
    c: Block(g198)
    c: Coincident(g199,g192)
    c: Coincident(g199,g195)
    c: Vertical(g199)
    c: Block(g199)
    c: Horizontal(g200)
    c: Block(g200)
    c: Coincident(g201,g200)
    c: Vertical(g201)
    c: Block(g201)
    c: Coincident(g202,g201)
    c: Horizontal(g202)
    c: Block(g202)
    c: Coincident(g203,g202)
    c: Vertical(g203)
    c: Block(g203)
    c: Coincident(g204,g200)
    c: Vertical(g204)
    c: Block(g204)
    c: Coincident(g215,g203)
    c: Weight(g206) = 1
    c: Equal(g206, g207-g214) x8
    c: Coincident(g215,g205)
    c: InternalAlignment(g206-g214 -> g215) x9
    c: InternalAlignment(g216-g222 -> g215) x7
    c: Coincident(g233,g204)
    c: Weight(g223) = 1
    c: Equal(g223, g224-g232) x9
    c: Coincident(g233,g205)
    c: InternalAlignment(g223-g232 -> g233) x10
    c: InternalAlignment(g234-g241 -> g233) x8
    c: Vertical(g205)
    c: Block(g205)
    c: Block(g215)
    c: Block(g233)
    c: Horizontal(g242)
    c: Horizontal(g243)
    c: Block(g242)
    c: Block(g243)
    c: Vertical(g244)
    c: Block(g244)
    c: Coincident(g270,g243)
    c: Weight(g245) = 1
    c: Equal(g245, g246-g269) x24
    c: Coincident(g270,g244)
    c: InternalAlignment(g245-g269 -> g270) x25
    c: InternalAlignment(g271-g293 -> g270) x23
    c: Coincident(g305,g242)
    c: Weight(g294) = 1
    c: Equal(g294, g295-g304) x10
    c: Coincident(g305,g242)
    c: InternalAlignment(g294-g304 -> g305) x11
    c: InternalAlignment(g306-g314 -> g305) x9
    c: Block(g305)
    c: Coincident(g327,g243)
    c: Weight(g315) = 1
    c: Equal(g315, g316-g326) x11
    c: Coincident(g327,g244)
    c: InternalAlignment(g315-g326 -> g327) x12
    c: InternalAlignment(g328-g337 -> g327) x10
    c: Block(g327)
    c: Block(g270)
FEATURE [Part::Extrusion] Extrude075  label="CommodoreLogoAndText002"
  Base = -> Sketch084
  Dir = (0,0,1)
  DirMode = 2
  FaceMakerClass = Part::FaceMakerBullseye
  LengthFwd = 10
  LengthRev = 0
  Solid = true
  Symmetric = false
FEATURE [Part::FeaturePython] Clone001  label="CommodoreLogoAndTextScale001"  # Draft clone (typed FeaturePython)
  AttacherType = Attacher::AttachEngine3D
  Fuse = false
  Objects = -> [Extrude075]
  Placement = pos=(112.566,5.37,70.6) rot=(0,0,1;0rad)
  Scale = (0.62,0.62,1)
FEATURE [Part::Cut] Cut073  label="sideA005"
  Base = -> Extrude002
  Tool = -> Part__Mirroring
